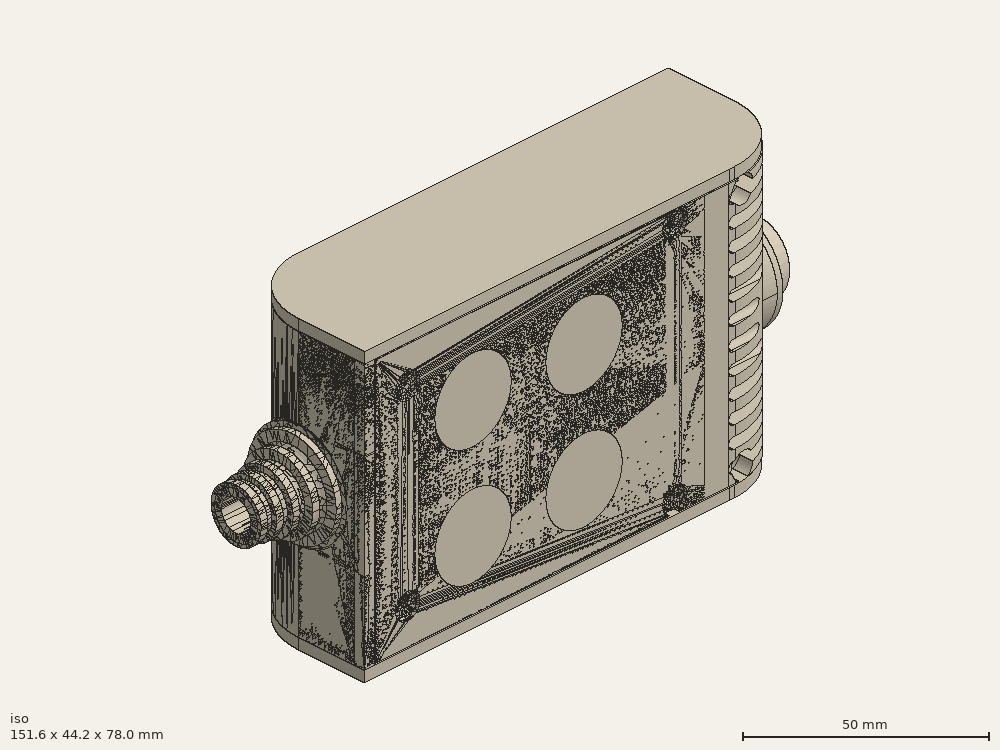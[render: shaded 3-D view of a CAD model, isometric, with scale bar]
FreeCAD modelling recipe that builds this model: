
FCSTD DOCUMENT  (FreeCAD 0.19R0.19.2)
Label: enclosure_174FCStd
License: All rights reserved
LicenseURL: http://en.wikipedia.org/wiki/All_rights_reserved
objects: Part::Revolution×152, Part::Feature×146, Part::MultiFuse×145, Sketcher::SketchObject×82, Part::Cut×69, Part::Extrusion×67, Part::Cylinder×66, Part::Fillet×58, Part::Box×36, App::MeasureDistance×4
note: 821 computed .brp shape members not serialized (recipe doc carries the construction recipe); baked Part::Feature solids carry a one-line shape summary decoded from their .brp

FEATURE [Sketcher::SketchObject] Sketch  label="topSketch"
  FullyConstrained = true
  sketch-geometry (20):
    g0: LineSegment StartX=5.21097e-06 StartY=3 StartZ=0 EndX=5.21097e-06 EndY=19 EndZ=0
    g1: ArcOfCircle CenterX=19 CenterY=19 CenterZ=0 NormalX=0 NormalY=0 NormalZ=1 AngleXU=0 Radius=19 StartAngle=1.5708 EndAngle=3.14159
    g2: ArcOfCircle CenterX=19 CenterY=19 CenterZ=0 NormalX=0 NormalY=0 NormalZ=1 AngleXU=0 Radius=16 StartAngle=1.5708 EndAngle=3.14159
    g3: LineSegment StartX=114 StartY=35 StartZ=0 EndX=19 EndY=35 EndZ=0
    g4: LineSegment StartX=5.21097e-06 StartY=3 StartZ=0 EndX=5.21097e-06 EndY=0 EndZ=0
    g5: LineSegment StartX=3 StartY=0 StartZ=0 EndX=5.21097e-06 EndY=0 EndZ=0
    g6: LineSegment StartX=3 StartY=19 StartZ=0 EndX=3 EndY=0 EndZ=0
    g7: LineSegment StartX=19 StartY=38 StartZ=0 EndX=124 EndY=38 EndZ=0
    g8: Circle CenterX=119 CenterY=35 CenterZ=0 NormalX=0 NormalY=0 NormalZ=1 AngleXU=0 Radius=1
    g9: Circle CenterX=121 CenterY=35 CenterZ=0 NormalX=0 NormalY=0 NormalZ=1 AngleXU=0 Radius=1
    g10: Circle CenterX=121 CenterY=33 CenterZ=0 NormalX=0 NormalY=0 NormalZ=1 AngleXU=0 Radius=1
    g11: BSplineCurve PolesCount=3 KnotsCount=2 Degree=2 IsPeriodic=0
    g12: GeomPoint X=119 Y=35 Z=0
    g13: GeomPoint X=121 Y=33 Z=0
    g14: LineSegment StartX=119 StartY=35 StartZ=0 EndX=114 EndY=35 EndZ=0
    g15: ArcOfCircle CenterX=105 CenterY=19 CenterZ=0 NormalX=0 NormalY=0 NormalZ=1 AngleXU=0 Radius=19 StartAngle=5.7297 EndAngle=6.28319
    g16: ArcOfCircle CenterX=105 CenterY=19 CenterZ=0 NormalX=0 NormalY=0 NormalZ=1 AngleXU=0 Radius=16 StartAngle=5.60905 EndAngle=6.28319
    g17: LineSegment StartX=121 StartY=33 StartZ=0 EndX=121 EndY=19 EndZ=0
    g18: LineSegment StartX=124 StartY=38 StartZ=0 EndX=124 EndY=19 EndZ=0
    g19: LineSegment StartX=117.5 StartY=9.01251 StartZ=0 EndX=121.163 EndY=9.0125 EndZ=0
  constraints (46):
    c: Vertical(g0)
    c: Block(g0)
    c: Coincident(g1,g0)
    c: Block(g1)
    c: Coincident(g2,g1)
    c: Block(g2)
    c: Coincident(g3,g2)
    c: Horizontal(g3)
    c: Tangent(g3,g2)
    c: Coincident(g4,g0)
    c: Distance(g4) = 3
    c: Vertical(g4)
    c: Coincident(g5,g4)
    c: Horizontal(g5)
    c: Coincident(g6,g2)
    c: Coincident(g6,g5)
    c: Vertical(g6)
    c: Horizontal(g7)
    c: Distance(g7) = 105
    c: Coincident(g7,g1)
    c: Block(g3)
    c: Weight(g8) = 1
    c: Equal(g8,g9)
    c: Equal(g8,g10)
    c: InternalAlignment(g8,g11)
    c: InternalAlignment(g9,g11)
    c: InternalAlignment(g10,g11)
    c: InternalAlignment(g12,g11)
    c: InternalAlignment(g13,g11)
    c: Block(g11)
    c: Coincident(g14,g11)
    c: Coincident(g14,g3)
    c: Horizontal(g14)
    c: Block(g15)
    c: Coincident(g16,g15)
    c: Block(g16)
    c: Coincident(g17,g11)
    c: Coincident(g17,g16)
    c: Vertical(g17)
    c: Distance(g17) = 14
    c: Coincident(g18,g7)
    c: Coincident(g18,g15)
    c: Vertical(g18)
    c: Distance(g18) = 19
    c: Coincident(g19,g16)
    c: Coincident(g19,g15)
FEATURE [Sketcher::SketchObject] Sketch001  label="bottomSketch"
  FullyConstrained = true
  sketch-geometry (32):
    g0: LineSegment StartX=3.3 StartY=-6.03275e-07 StartZ=0 EndX=98 EndY=-6.03275e-07 EndZ=0
    g1: ArcOfCircle CenterX=98 CenterY=19 CenterZ=0 NormalX=0 NormalY=0 NormalZ=1 AngleXU=0 Radius=19 StartAngle=4.71239 EndAngle=5.71103
    g2: LineSegment StartX=6.3 StartY=8 StartZ=0 EndX=3.3 EndY=8 EndZ=0
    g3: LineSegment StartX=3.3 StartY=8 StartZ=0 EndX=3.3 EndY=-6.03275e-07 EndZ=0
    g4: ArcOfCircle CenterX=8.3 CenterY=5 CenterZ=0 NormalX=0 NormalY=0 NormalZ=1 AngleXU=0 Radius=2 StartAngle=3.14159 EndAngle=4.71239
    g5: LineSegment StartX=6.3 StartY=8 StartZ=0 EndX=6.3 EndY=5 EndZ=0
    g6: ArcOfCircle CenterX=98 CenterY=19 CenterZ=0 NormalX=0 NormalY=0 NormalZ=1 AngleXU=0 Radius=12.7 StartAngle=4.71239 EndAngle=6.28319
    g7: LineSegment StartX=94.7 StartY=3 StartZ=0 EndX=8.3 EndY=3 EndZ=0
    g8-g12: Circle x5 (B-spline internal-alignment scaffolding for g13; pole/knot coordinates omitted)
    g13: BSplineCurve PolesCount=5 KnotsCount=3 Degree=3 IsPeriodic=0
    g14: GeomPoint X=98 Y=6.3 Z=0
    g15: GeomPoint X=96.3938 Y=4.71946 Z=0
    g16: GeomPoint X=94.7 Y=3 Z=0
    g17-g23: Circle x7 (B-spline internal-alignment scaffolding for g24; pole/knot coordinates omitted)
    g24: BSplineCurve PolesCount=7 KnotsCount=5 Degree=3 IsPeriodic=0
    g25-g29: GeomPoint x5 (B-spline internal-alignment scaffolding for g24; pole/knot coordinates omitted)
    g30: ArcOfCircle CenterX=98 CenterY=19 CenterZ=0 NormalX=0 NormalY=0 NormalZ=1 AngleXU=0 Radius=15.7 StartAngle=5.81226 EndAngle=6.28319
    g31: LineSegment StartX=110.7 StartY=19 StartZ=0 EndX=113.7 EndY=19 EndZ=0
  constraints (41):
    c: Horizontal(g0)
    c: Coincident(g1,g0)
    c: Block(g1)
    c: Horizontal(g2)
    c: Distance(g2) = 3
    c: Coincident(g3,g2)
    c: Vertical(g3)
    c: Coincident(g3,g0)
    c: Block(g4)
    c: Block(g2)
    c: Coincident(g5,g2)
    c: Coincident(g5,g4)
    c: Vertical(g5)
    c: Coincident(g6,g1)
    c: Block(g6)
    c: Coincident(g7,g4)
    c: Horizontal(g7)
    c: Block(g0)
    c: Block(g7)
    c: Block(g3)
    c: Coincident(g13,g6)
    c: Weight(g8) = 1
    c: Equal(g8, g9-g12) x4
    c: Coincident(g13,g7)
    c: InternalAlignment(g8-g12 -> g13) x5
    c: InternalAlignment(g14,g13)
    c: InternalAlignment(g15,g13)
    c: InternalAlignment(g16,g13)
    c: Block(g13)
    c: Weight(g17) = 1
    c: Equal(g17, g18-g23) x6
    c: Coincident(g24,g1)
    c: InternalAlignment(g17-g23 -> g24) x7
    c: InternalAlignment(g25-g29 -> g24) x5
    c: Block(g24)
    c: Coincident(g30,g24)
    c: Coincident(g31,g6)
    c: Coincident(g31,g30)
    c: Horizontal(g31)
    c: Block(g31)
    c: Block(g30)
FEATURE [Part::Extrusion] Extrude  label="top"
  Base = -> Sketch
  Dir = (0,0,1)
  DirMode = 2
  FaceMakerClass = Part::FaceMakerBullseye
  LengthFwd = 72
  LengthRev = 0
  Solid = true
  Symmetric = false
FEATURE [Part::Extrusion] Extrude001  label="bottom"
  Base = -> Sketch001
  Dir = (0,0,1)
  DirMode = 2
  FaceMakerClass = Part::FaceMakerBullseye
  LengthFwd = 71.4
  LengthRev = 0
  Placement = pos=(0,0,0.3) rot=(0,0,1;0rad)
  Solid = true
  Symmetric = false
FEATURE [Sketcher::SketchObject] Sketch002  label="topSketch001"
  FullyConstrained = true
  sketch-geometry (8):
    g0: ArcOfCircle CenterX=19 CenterY=19.0975 CenterZ=0 NormalX=0 NormalY=0 NormalZ=1 AngleXU=0 Radius=18.9025 StartAngle=1.5708 EndAngle=3.14674
    g1: LineSegment StartX=0.0977805 StartY=19.0003 StartZ=0 EndX=0.0977805 EndY=0.000251602 EndZ=0
    g2: LineSegment StartX=19 StartY=38 StartZ=0 EndX=124 EndY=38 EndZ=0
    g3: LineSegment StartX=0.0977805 StartY=0.000251602 StartZ=0 EndX=105.098 EndY=0.000251602 EndZ=0
    g4: LineSegment StartX=124 StartY=38 StartZ=0 EndX=125.616 EndY=38 EndZ=0
    g5: LineSegment StartX=105.098 StartY=0.000251602 StartZ=0 EndX=106.713 EndY=0.000251602 EndZ=0
    g6: ArcOfCircle CenterX=106.616 CenterY=19 CenterZ=0 NormalX=0 NormalY=0 NormalZ=1 AngleXU=0 Radius=19 StartAngle=4.71754 EndAngle=6.28319
    g7: LineSegment StartX=125.616 StartY=38 StartZ=0 EndX=125.616 EndY=19 EndZ=0
  constraints (21):
    c: Block(g0)
    c: Coincident(g1,g0)
    c: Vertical(g1)
    c: Horizontal(g2)
    c: Distance(g2) = 105
    c: Coincident(g2,g0)
    c: Distance(g1) = 19
    c: Coincident(g3,g1)
    c: Horizontal(g3)
    c: Distance(g3) = 105
    c: Coincident(g4,g2)
    c: Horizontal(g4)
    c: Distance(g4) = 1.61553
    c: Horizontal(g5)
    c: Equal(g4,g5) = 1.61553
    c: Coincident(g5,g3)
    c: Block(g6)
    c: Coincident(g6,g5)
    c: Coincident(g7,g4)
    c: Coincident(g7,g6)
    c: Vertical(g7)
FEATURE [Part::Extrusion] Extrude002  label="sideA"
  Base = -> Sketch002
  Dir = (0,0,1)
  DirMode = 2
  FaceMakerClass = Part::FaceMakerBullseye
  LengthFwd = 3
  LengthRev = 0
  Placement = pos=(0,0,-3) rot=(0,0,1;0rad)
  Solid = true
  Symmetric = false
FEATURE [Sketcher::SketchObject] Sketch003  label="topSketch002"
  FullyConstrained = true
  sketch-geometry (6):
    g0: LineSegment StartX=19 StartY=38 StartZ=0 EndX=117 EndY=38 EndZ=0
    g1: ArcOfCircle CenterX=19 CenterY=19 CenterZ=0 NormalX=0 NormalY=0 NormalZ=1 AngleXU=0 Radius=19 StartAngle=1.5708 EndAngle=3.14159
    g2: LineSegment StartX=117 StartY=38 StartZ=0 EndX=117 EndY=19 EndZ=0
    g3: LineSegment StartX=98 StartY=1.0161e-12 StartZ=0 EndX=5.22862e-06 EndY=1.0161e-12 EndZ=0
    g4: LineSegment StartX=5.22862e-06 StartY=19 StartZ=0 EndX=5.22862e-06 EndY=1.0161e-12 EndZ=0
    g5: ArcOfCircle CenterX=98 CenterY=19 CenterZ=0 NormalX=0 NormalY=0 NormalZ=1 AngleXU=0 Radius=19 StartAngle=4.71239 EndAngle=6.28319
  constraints (16):
    c: Horizontal(g0)
    c: Distance(g0) = 98
    c: Coincident(g1,g0)
    c: Block(g1)
    c: Coincident(g2,g0)
    c: Vertical(g2)
    c: Distance(g2) = 19
    c: Horizontal(g3)
    c: Coincident(g4,g1)
    c: Vertical(g4)
    c: Coincident(g3,g4)
    c: Block(g3)
    c: Coincident(g5,g2)
    c: Coincident(g5,g3)
    c: Block(g0)
    c: Block(g5)
FEATURE [Sketcher::SketchObject] Sketch004
  FullyConstrained = true
  MapMode = 3
  Placement = pos=(0,0,0) rot=(1,0,0;1.5708rad)
  Support = -> [Extrude]
  sketch-geometry (8):
    g0: Circle CenterX=80.351 CenterY=-67.6202 CenterZ=0 NormalX=0 NormalY=0 NormalZ=1 AngleXU=0 Radius=2
    g1: Circle CenterX=80.351 CenterY=-67.6202 CenterZ=0 NormalX=0 NormalY=0 NormalZ=1 AngleXU=0 Radius=3
    g2: Circle CenterX=80.351 CenterY=-4.92017 CenterZ=0 NormalX=0 NormalY=0 NormalZ=1 AngleXU=0 Radius=2
    g3: Circle CenterX=80.351 CenterY=-4.92017 CenterZ=0 NormalX=0 NormalY=0 NormalZ=1 AngleXU=0 Radius=3
    g4: Circle CenterX=23.851 CenterY=-4.92017 CenterZ=0 NormalX=0 NormalY=0 NormalZ=1 AngleXU=0 Radius=2
    g5: Circle CenterX=23.851 CenterY=-4.92017 CenterZ=0 NormalX=0 NormalY=0 NormalZ=1 AngleXU=0 Radius=3
    g6: Circle CenterX=23.851 CenterY=-67.6202 CenterZ=0 NormalX=0 NormalY=0 NormalZ=1 AngleXU=0 Radius=2
    g7: Circle CenterX=23.851 CenterY=-67.6202 CenterZ=0 NormalX=0 NormalY=0 NormalZ=1 AngleXU=0 Radius=3
  constraints (8):
    c: Block(g3)
    c: Block(g2)
    c: Block(g1)
    c: Block(g0)
    c: Block(g6)
    c: Block(g7)
    c: Block(g4)
    c: Block(g5)
FEATURE [Part::Extrusion] Extrude004
  Base = -> Sketch004
  Dir = (0,-1,2e-16)
  DirMode = 2
  FaceMakerClass = Part::FaceMakerBullseye
  LengthFwd = 6
  LengthRev = 0
  Placement = pos=(0,9,0) rot=(0,0,1;0rad)
  Solid = true
  Symmetric = false
FEATURE [Sketcher::SketchObject] Sketch005
  FullyConstrained = true
  MapMode = 3
  Placement = pos=(0,0,0) rot=(1,0,0;1.5708rad)
  Support = -> [Extrude]
  sketch-geometry (8):
    g0: Circle CenterX=80.351 CenterY=-67.6202 CenterZ=0 NormalX=0 NormalY=0 NormalZ=1 AngleXU=0 Radius=3
    g1: Circle CenterX=80.351 CenterY=-4.92017 CenterZ=0 NormalX=0 NormalY=0 NormalZ=1 AngleXU=0 Radius=3
    g2: Circle CenterX=23.851 CenterY=-4.92017 CenterZ=0 NormalX=0 NormalY=0 NormalZ=1 AngleXU=0 Radius=3
    g3: Circle CenterX=23.851 CenterY=-67.6202 CenterZ=0 NormalX=0 NormalY=0 NormalZ=1 AngleXU=0 Radius=3
    g4: Circle CenterX=23.851 CenterY=-67.6202 CenterZ=0 NormalX=0 NormalY=0 NormalZ=1 AngleXU=0 Radius=5
    g5: Circle CenterX=80.351 CenterY=-67.6202 CenterZ=0 NormalX=0 NormalY=0 NormalZ=1 AngleXU=0 Radius=5
    g6: Circle CenterX=23.851 CenterY=-4.92017 CenterZ=0 NormalX=0 NormalY=0 NormalZ=1 AngleXU=0 Radius=5
    g7: Circle CenterX=80.351 CenterY=-4.92017 CenterZ=0 NormalX=0 NormalY=0 NormalZ=1 AngleXU=0 Radius=5
  constraints (8):
    c: Block(g1)
    c: Block(g0)
    c: Block(g3)
    c: Block(g2)
    c: Block(g5)
    c: Block(g4)
    c: Block(g6)
    c: Block(g7)
FEATURE [Part::Extrusion] Extrude005
  Base = -> Sketch005
  Dir = (0,-1,2e-16)
  DirMode = 2
  FaceMakerClass = Part::FaceMakerBullseye
  LengthFwd = 2
  LengthRev = 0
  Solid = true
  Symmetric = false
FEATURE [Sketcher::SketchObject] Sketch006
  FullyConstrained = true
  MapMode = 3
  Placement = pos=(0,0,0) rot=(1,0,0;1.5708rad)
  sketch-geometry (8):
    g0: Circle CenterX=80.351 CenterY=-67.6202 CenterZ=0 NormalX=0 NormalY=0 NormalZ=1 AngleXU=0 Radius=3
    g1: Circle CenterX=80.351 CenterY=-4.92017 CenterZ=0 NormalX=0 NormalY=0 NormalZ=1 AngleXU=0 Radius=3
    g2: Circle CenterX=23.851 CenterY=-4.92017 CenterZ=0 NormalX=0 NormalY=0 NormalZ=1 AngleXU=0 Radius=3
    g3: Circle CenterX=23.851 CenterY=-67.6202 CenterZ=0 NormalX=0 NormalY=0 NormalZ=1 AngleXU=0 Radius=3
    g4: Circle CenterX=23.851 CenterY=-67.6202 CenterZ=0 NormalX=0 NormalY=0 NormalZ=1 AngleXU=0 Radius=5
    g5: Circle CenterX=80.351 CenterY=-67.6202 CenterZ=0 NormalX=0 NormalY=0 NormalZ=1 AngleXU=0 Radius=5
    g6: Circle CenterX=23.851 CenterY=-4.92017 CenterZ=0 NormalX=0 NormalY=0 NormalZ=1 AngleXU=0 Radius=5
    g7: Circle CenterX=80.351 CenterY=-4.92017 CenterZ=0 NormalX=0 NormalY=0 NormalZ=1 AngleXU=0 Radius=5
  constraints (8):
    c: Block(g1)
    c: Block(g0)
    c: Block(g3)
    c: Block(g2)
    c: Block(g5)
    c: Block(g4)
    c: Block(g6)
    c: Block(g7)
FEATURE [Part::Extrusion] Extrude007
  Base = -> Sketch006
  Dir = (0,-1,2e-16)
  DirMode = 2
  FaceMakerClass = Part::FaceMakerBullseye
  LengthFwd = 2
  LengthRev = 0
  Solid = true
  Symmetric = false
FEATURE [Part::Fillet] Fillet
  Base = -> Extrude007
  Edges = 4 edges r=1.99: [Edge6,Edge12,Edge18,Edge24]
FEATURE [Part::Cut] Cut
  Base = -> Extrude005
  Placement = pos=(0,5,0) rot=(0,0,1;0rad)
  Tool = -> Fillet
FEATURE [Part::MultiFuse] Fusion  label="pCBScrews"
  Placement = pos=(-2.5,0,72.3) rot=(0,0,1;0rad)
  Shapes = -> [Extrude004,Cut]
FEATURE [App::MeasureDistance] Distance  label="Distance: 0.69 mm"
  Distance = 0.685967
  P1 = (24.0138,2.9647,0.3)
  P2 = (23.8901,3,-0.373787)
FEATURE [App::MeasureDistance] Distance001  label="Distance: 0.53 mm"
  Distance = 0.533607
  P1 = (80.2939,3,72.2334)
  P2 = (80.281,2.99661,71.7)
FEATURE [Part::Fillet] Fillet001
  Base = -> Extrude001
  Edges = 1 edges r=2.4: [Edge17]
FEATURE [Part::Fillet] Fillet002  label="bottom001"
  Base = -> Fillet001
  Edges = 1 edges r=2.4: [Edge36]
FEATURE [Part::Fillet] Fillet003  label="top001"
  Base = -> Extrude
  Edges = 1 edges r=2: [Edge1]
FEATURE [Sketcher::SketchObject] Sketch007
  FullyConstrained = true
  sketch-geometry (16):
    g0: LineSegment StartX=4 StartY=0 StartZ=0 EndX=4 EndY=2.4 EndZ=0
    g1: LineSegment StartX=4 StartY=2.4 StartZ=0 EndX=7 EndY=2.4 EndZ=0
    g2: LineSegment StartX=4 StartY=0 StartZ=0 EndX=5.7 EndY=0 EndZ=0
    g3: LineSegment StartX=5.7 StartY=0 StartZ=0 EndX=5.7 EndY=-5.6 EndZ=0
    g4-g8: Circle x5 (B-spline internal-alignment scaffolding for g9; pole/knot coordinates omitted)
    g9: BSplineCurve PolesCount=5 KnotsCount=3 Degree=3 IsPeriodic=0
    g10: GeomPoint X=7 Y=2.4 Z=0
    g11: GeomPoint X=10.4582 Y=-1.55472 Z=0
    g12: GeomPoint X=14 Y=-5.6 Z=0
    g13: LineSegment StartX=14 StartY=-5.6 StartZ=0 EndX=14 EndY=-14.1 EndZ=0
    g14: LineSegment StartX=14 StartY=-14.1 StartZ=0 EndX=6.5 EndY=-14.1 EndZ=0
    g15: LineSegment StartX=5.7 StartY=-5.6 StartZ=0 EndX=6.5 EndY=-14.1 EndZ=0
  constraints (28):
    c: Distance(g0) = 2.4
    c: Vertical(g0)
    c: Block(g0)
    c: Coincident(g1,g0)
    c: Horizontal(g1)
    c: Distance(g1) = 3
    c: Coincident(g2,g0)
    c: Horizontal(g2)
    c: Distance(g2) = 1.7
    c: Coincident(g3,g2)
    c: Vertical(g3)
    c: Distance(g3) = 5.6
    c: Coincident(g9,g1)
    c: Weight(g4) = 1
    c: Equal(g4, g5-g8) x4
    c: InternalAlignment(g4-g8 -> g9) x5
    c: InternalAlignment(g10,g9)
    c: InternalAlignment(g11,g9)
    c: InternalAlignment(g12,g9)
    c: Block(g9)
    c: Coincident(g13,g9)
    c: Vertical(g13)
    c: Distance(g13) = 8.5
    c: Coincident(g14,g13)
    c: Horizontal(g14)
    c: Distance(g14) = 7.5
    c: Coincident(g15,g3)
    c: Coincident(g15,g14)
FEATURE [Part::Feature] Face
  shape: bbox 10 x 16.5 x 2e-07 mm, 1 faces, 0 solids (baked)
FEATURE [Part::Revolution] Revolve  label="plugHousing"
  Angle = 360
  Axis = (0,1,0)
  Base = (0,0,0)
  FaceMakerClass = Part::FaceMakerBullseye
  Placement = pos=(0,0,36.15) rot=(0,0,1;0rad)
  Solid = false
  Source = -> Face
  Symmetric = false
FEATURE [Part::Feature] Face001
  shape: bbox 10 x 16.5 x 2e-07 mm, 1 faces, 0 solids (baked)
FEATURE [Part::Revolution] Revolve001  label="plugHousing001"
  Angle = 360
  Axis = (0,1,0)
  Base = (0,0,0)
  FaceMakerClass = Part::FaceMakerBullseye
  Placement = pos=(0,0,36.15) rot=(0,0,1;0rad)
  Solid = false
  Source = -> Face001
  Symmetric = false
FEATURE [Part::MultiFuse] Fusion001  label="plugHousing002"
  Placement = pos=(0,0,0) rot=(0,0,1;1.5708rad)
  Shapes = -> [Revolve001,Revolve]
FEATURE [Part::Feature] Face002
  shape: bbox 10 x 16.5 x 2e-07 mm, 1 faces, 0 solids (baked)
FEATURE [Part::Revolution] Revolve003  label="plugHousing005"
  Angle = 360
  Axis = (0,1,0)
  Base = (0,0,0)
  FaceMakerClass = Part::FaceMakerBullseye
  Placement = pos=(0,0,36.15) rot=(0,0,1;0rad)
  Solid = false
  Source = -> Face002
  Symmetric = false
FEATURE [Part::Feature] Face003
  shape: bbox 10 x 16.5 x 2e-07 mm, 1 faces, 0 solids (baked)
FEATURE [Part::Revolution] Revolve002  label="plugHousing003"
  Angle = 360
  Axis = (0,1,0)
  Base = (0,0,0)
  FaceMakerClass = Part::FaceMakerBullseye
  Placement = pos=(0,0,36.15) rot=(0,0,1;0rad)
  Solid = false
  Source = -> Face003
  Symmetric = false
FEATURE [Part::MultiFuse] Fusion002  label="plugHousing004"
  Placement = pos=(0,0,0) rot=(0,0,1;1.5708rad)
  Shapes = -> [Revolve002,Revolve003]
FEATURE [Part::MultiFuse] Fusion003  label="plugHousing006"
  Placement = pos=(0,19,0) rot=(0,0,1;3.14159rad)
  Shapes = -> [Fusion002,Fusion001]
FEATURE [Part::Feature] Face004
  shape: bbox 10 x 16.5 x 2e-07 mm, 1 faces, 0 solids (baked)
FEATURE [Part::Revolution] Revolve006  label="plugHousing010"
  Angle = 360
  Axis = (0,1,0)
  Base = (0,0,0)
  FaceMakerClass = Part::FaceMakerBullseye
  Placement = pos=(0,0,36.15) rot=(0,0,1;0rad)
  Solid = false
  Source = -> Face004
  Symmetric = false
FEATURE [Part::Feature] Face005
  shape: bbox 10 x 16.5 x 2e-07 mm, 1 faces, 0 solids (baked)
FEATURE [Part::Revolution] Revolve007  label="plugHousing011"
  Angle = 360
  Axis = (0,1,0)
  Base = (0,0,0)
  FaceMakerClass = Part::FaceMakerBullseye
  Placement = pos=(0,0,36.15) rot=(0,0,1;0rad)
  Solid = false
  Source = -> Face005
  Symmetric = false
FEATURE [Part::Feature] Face006
  shape: bbox 10 x 16.5 x 2e-07 mm, 1 faces, 0 solids (baked)
FEATURE [Part::Revolution] Revolve004  label="plugHousing007"
  Angle = 360
  Axis = (0,1,0)
  Base = (0,0,0)
  FaceMakerClass = Part::FaceMakerBullseye
  Placement = pos=(0,0,36.15) rot=(0,0,1;0rad)
  Solid = false
  Source = -> Face006
  Symmetric = false
FEATURE [Part::MultiFuse] Fusion004  label="plugHousing009"
  Placement = pos=(0,0,0) rot=(0,0,1;1.5708rad)
  Shapes = -> [Revolve004,Revolve007]
FEATURE [Part::Feature] Face007
  shape: bbox 10 x 16.5 x 2e-07 mm, 1 faces, 0 solids (baked)
FEATURE [Part::Revolution] Revolve005  label="plugHousing008"
  Angle = 360
  Axis = (0,1,0)
  Base = (0,0,0)
  FaceMakerClass = Part::FaceMakerBullseye
  Placement = pos=(0,0,36.15) rot=(0,0,1;0rad)
  Solid = false
  Source = -> Face007
  Symmetric = false
FEATURE [Part::MultiFuse] Fusion005  label="plugHousing012"
  Placement = pos=(0,0,0) rot=(0,0,1;1.5708rad)
  Shapes = -> [Revolve006,Revolve005]
FEATURE [Part::MultiFuse] Fusion006  label="plugHousing013"
  Placement = pos=(0,19,0) rot=(0,0,1;3.14159rad)
  Shapes = -> [Fusion005,Fusion004]
FEATURE [Part::MultiFuse] Fusion007  label="plugHousing014"
  Placement = pos=(122.621,0,-0.15) rot=(0,0,1;0rad)
  Shapes = -> [Fusion003,Fusion006]
FEATURE [Part::Cylinder] Cylinder002
  Angle = 360
  AttacherType = Attacher::AttachEngine3D
  Height = 20
  Placement = pos=(0,0,36.15) rot=(0,0,1;0rad)
  Radius = 4
FEATURE [Part::Cylinder] Cylinder003
  Angle = 360
  AttacherType = Attacher::AttachEngine3D
  Height = 10
  Placement = pos=(0,0,36.15) rot=(0,0,1;0rad)
  Radius = 4
FEATURE [Part::MultiFuse] Fusion009  label="removeToCreateHoleForPlugHousing"
  Placement = pos=(70,19,36.15) rot=(0,1,0;1.5708rad)
  Shapes = -> [Cylinder002,Cylinder003]
FEATURE [Part::Cylinder] Cylinder004
  Angle = 360
  AttacherType = Attacher::AttachEngine3D
  Height = 20
  Placement = pos=(0,0,36.15) rot=(0,0,1;0rad)
  Radius = 4
FEATURE [Part::Cylinder] Cylinder005
  Angle = 360
  AttacherType = Attacher::AttachEngine3D
  Height = 10
  Placement = pos=(0,0,36.15) rot=(0,0,1;0rad)
  Radius = 4
FEATURE [Part::MultiFuse] Fusion010  label="removeToCreateHoleForPlugHousing001"
  Placement = pos=(70,19,36.15) rot=(0,1,0;1.5708rad)
  Shapes = -> [Cylinder004,Cylinder005]
FEATURE [Part::Cut] Cut001
  Base = -> Fillet003
  Tool = -> Fusion010
FEATURE [Part::Cut] Cut002  label="Bottom"
  Base = -> Fillet002
  Tool = -> Fusion009
FEATURE [Part::Feature] Face008
  shape: bbox 10 x 16.5 x 2e-07 mm, 1 faces, 0 solids (baked)
FEATURE [Part::Revolution] Revolve011  label="plugHousing021"
  Angle = 360
  Axis = (0,1,0)
  Base = (0,0,0)
  FaceMakerClass = Part::FaceMakerBullseye
  Placement = pos=(0,0,36.15) rot=(0,0,1;0rad)
  Solid = false
  Source = -> Face008
  Symmetric = false
FEATURE [Part::Feature] Face009
  shape: bbox 10 x 16.5 x 2e-07 mm, 1 faces, 0 solids (baked)
FEATURE [Part::Revolution] Revolve012  label="plugHousing022"
  Angle = 360
  Axis = (0,1,0)
  Base = (0,0,0)
  FaceMakerClass = Part::FaceMakerBullseye
  Placement = pos=(0,0,36.15) rot=(0,0,1;0rad)
  Solid = false
  Source = -> Face009
  Symmetric = false
FEATURE [Part::Feature] Face010 .. Face013  x4 (patterned run collapsed; names and placements below)
  shape: bbox 10 x 16.5 x 2e-07 mm, 1 faces, 0 solids (baked)
FEATURE [Part::Revolution] Revolve015  label="plugHousing027"
  Angle = 360
  Axis = (0,1,0)
  Base = (0,0,0)
  FaceMakerClass = Part::FaceMakerBullseye
  Placement = pos=(0,0,36.15) rot=(0,0,1;0rad)
  Solid = false
  Source = -> Face013
  Symmetric = false
FEATURE [Part::Feature] Face014
  shape: bbox 10 x 16.5 x 2e-07 mm, 1 faces, 0 solids (baked)
FEATURE [Part::Feature] Face015
  shape: bbox 10 x 16.5 x 2e-07 mm, 1 faces, 0 solids (baked)
FEATURE [Part::Feature] Face016
  shape: bbox 10 x 16.5 x 2e-07 mm, 1 faces, 0 solids (baked)
FEATURE [Part::Revolution] Revolve019  label="plugHousing033"
  Angle = 360
  Axis = (0,1,0)
  Base = (0,0,0)
  FaceMakerClass = Part::FaceMakerBullseye
  Placement = pos=(0,0,36.15) rot=(0,0,1;0rad)
  Solid = false
  Source = -> Face016
  Symmetric = false
FEATURE [Part::Feature] Face017
  shape: bbox 10 x 16.5 x 2e-07 mm, 1 faces, 0 solids (baked)
FEATURE [Part::Revolution] Revolve020  label="plugHousing034"
  Angle = 360
  Axis = (0,1,0)
  Base = (0,0,0)
  FaceMakerClass = Part::FaceMakerBullseye
  Placement = pos=(0,0,36.15) rot=(0,0,1;0rad)
  Solid = false
  Source = -> Face017
  Symmetric = false
FEATURE [Part::Feature] Face018
  shape: bbox 10 x 16.5 x 2e-07 mm, 1 faces, 0 solids (baked)
FEATURE [Part::Revolution] Revolve016  label="plugHousing030"
  Angle = 360
  Axis = (0,1,0)
  Base = (0,0,0)
  FaceMakerClass = Part::FaceMakerBullseye
  Placement = pos=(0,0,36.15) rot=(0,0,1;0rad)
  Solid = false
  Source = -> Face018
  Symmetric = false
FEATURE [Part::MultiFuse] Fusion020  label="plugHousing038"
  Placement = pos=(0,0,0) rot=(0,0,1;1.5708rad)
  Shapes = -> [Revolve016,Revolve020]
FEATURE [Part::Feature] Face019
  shape: bbox 10 x 16.5 x 2e-07 mm, 1 faces, 0 solids (baked)
FEATURE [Part::Feature] Face020
  shape: bbox 10 x 16.5 x 2e-07 mm, 1 faces, 0 solids (baked)
FEATURE [Part::Revolution] Revolve017  label="plugHousing031"
  Angle = 360
  Axis = (0,1,0)
  Base = (0,0,0)
  FaceMakerClass = Part::FaceMakerBullseye
  Placement = pos=(0,0,36.15) rot=(0,0,1;0rad)
  Solid = false
  Source = -> Face020
  Symmetric = false
FEATURE [Part::MultiFuse] Fusion021  label="plugHousing039"
  Placement = pos=(0,0,0) rot=(0,0,1;1.5708rad)
  Shapes = -> [Revolve019,Revolve017]
FEATURE [Part::MultiFuse] Fusion023  label="plugHousing041"
  Placement = pos=(0,19,0) rot=(0,0,1;3.14159rad)
  Shapes = -> [Fusion021,Fusion020]
FEATURE [Part::Revolution] Revolve022  label="plugHousing043"
  Angle = 360
  Axis = (0,1,0)
  Base = (0,0,0)
  FaceMakerClass = Part::FaceMakerBullseye
  Placement = pos=(0,0,36.15) rot=(0,0,1;0rad)
  Solid = false
  Source = -> Face019
  Symmetric = false
FEATURE [Part::Feature] Face021
  shape: bbox 10 x 16.5 x 2e-07 mm, 1 faces, 0 solids (baked)
FEATURE [Part::Revolution] Revolve023  label="plugHousing044"
  Angle = 360
  Axis = (0,1,0)
  Base = (0,0,0)
  FaceMakerClass = Part::FaceMakerBullseye
  Placement = pos=(0,0,36.15) rot=(0,0,1;0rad)
  Solid = false
  Source = -> Face021
  Symmetric = false
FEATURE [Part::Feature] Face022
  shape: bbox 10 x 16.5 x 2e-07 mm, 1 faces, 0 solids (baked)
FEATURE [Part::Revolution] Revolve018  label="plugHousing032"
  Angle = 360
  Axis = (0,1,0)
  Base = (0,0,0)
  FaceMakerClass = Part::FaceMakerBullseye
  Placement = pos=(0,0,36.15) rot=(0,0,1;0rad)
  Solid = false
  Source = -> Face022
  Symmetric = false
FEATURE [Part::MultiFuse] Fusion022  label="plugHousing040"
  Placement = pos=(0,0,0) rot=(0,0,1;1.5708rad)
  Shapes = -> [Revolve018,Revolve023]
FEATURE [Part::Feature] Face023
  shape: bbox 10 x 16.5 x 2e-07 mm, 1 faces, 0 solids (baked)
FEATURE [Part::Revolution] Revolve021  label="plugHousing035"
  Angle = 360
  Axis = (0,1,0)
  Base = (0,0,0)
  FaceMakerClass = Part::FaceMakerBullseye
  Placement = pos=(0,0,36.15) rot=(0,0,1;0rad)
  Solid = false
  Source = -> Face023
  Symmetric = false
FEATURE [Part::MultiFuse] Fusion018  label="plugHousing036"
  Placement = pos=(0,0,0) rot=(0,0,1;1.5708rad)
  Shapes = -> [Revolve022,Revolve021]
FEATURE [Part::MultiFuse] Fusion019  label="plugHousing037"
  Placement = pos=(0,19,0) rot=(0,0,1;3.14159rad)
  Shapes = -> [Fusion018,Fusion022]
FEATURE [Part::MultiFuse] Fusion024  label="plugHousing042"
  Placement = pos=(122.621,0,-0.15) rot=(0,0,1;0rad)
  Shapes = -> [Fusion023,Fusion019]
FEATURE [Part::Cylinder] Cylinder006
  Angle = 360
  AttacherType = Attacher::AttachEngine3D
  Height = 20
  Placement = pos=(0,0,36.15) rot=(0,0,1;0rad)
  Radius = 14.3
FEATURE [Part::Cylinder] Cylinder007
  Angle = 360
  AttacherType = Attacher::AttachEngine3D
  Height = 10
  Placement = pos=(0,0,36.15) rot=(0,0,1;0rad)
  Radius = 4
FEATURE [Part::MultiFuse] Fusion026  label="removeToCreteHoleForPlugHousing"
  Placement = pos=(70,19,36) rot=(0,1,0;1.5708rad)
  Shapes = -> [Cylinder006,Cylinder007]
FEATURE [Part::Box] Box001  label="Cube001"
  AttacherType = Attacher::AttachEngine3D
  Height = 28
  Length = 3
  Placement = pos=(110.7,19,22) rot=(0,0,1;0rad)
  Width = 15.7
FEATURE [Part::Cut] Cut003  label="top002"
  Base = -> Cut001
  Tool = -> Fusion007
FEATURE [Part::Revolution] Revolve008  label="plugHousing015"
  Angle = 360
  Axis = (0,1,0)
  Base = (0,0,0)
  FaceMakerClass = Part::FaceMakerBullseye
  Placement = pos=(0,0,36.15) rot=(0,0,1;0rad)
  Solid = false
  Source = -> Face010
  Symmetric = false
FEATURE [Part::MultiFuse] Fusion013  label="plugHousing020"
  Placement = pos=(0,0,0) rot=(0,0,1;1.5708rad)
  Shapes = -> [Revolve008,Revolve012]
FEATURE [Part::Cut] Cut004  label="top003"
  Base = -> Cut003
  Placement = pos=(1,0,0) rot=(0,0,1;0rad)
  Tool = -> Fusion026
FEATURE [Part::Cylinder] Cylinder008
  Angle = 360
  AttacherType = Attacher::AttachEngine3D
  Height = 20
  Placement = pos=(0,0,36.15) rot=(0,0,1;0rad)
  Radius = 10.3
FEATURE [Part::Cylinder] Cylinder009
  Angle = 360
  AttacherType = Attacher::AttachEngine3D
  Height = 10
  Placement = pos=(0,0,36.15) rot=(0,0,1;0rad)
  Radius = 4
FEATURE [Part::MultiFuse] Fusion027  label="removeToCreteHoleForPlugHousing001"
  Placement = pos=(70,19,36) rot=(0,1,0;1.5708rad)
  Shapes = -> [Cylinder008,Cylinder009]
FEATURE [Part::Cut] Cut005  label="plugHousingTab"
  Base = -> Box001
  Tool = -> Fusion027
FEATURE [Part::MultiFuse] Fusion028  label="plugHousing045"
  Shapes = -> [Fusion024,Cut005]
FEATURE [Part::Box] Box002  label="Cube002"
  AttacherType = Attacher::AttachEngine3D
  Height = 28.8
  Length = 3
  Placement = pos=(107.3,28,21.6) rot=(0,0,1;0rad)
  Width = 7
FEATURE [Part::Box] Box003  label="Cube003"
  AttacherType = Attacher::AttachEngine3D
  Height = 3
  Length = 6.4
  Placement = pos=(107.3,28,18.6) rot=(0,0,1;0rad)
  Width = 7
FEATURE [Part::Box] Box004  label="Cube004"
  AttacherType = Attacher::AttachEngine3D
  Height = 3
  Length = 6.4
  Placement = pos=(107.3,28,50.4) rot=(0,0,1;0rad)
  Width = 7
FEATURE [Part::MultiFuse] Fusion029  label="plugHousingBracketHolder"
  Shapes = -> [Box004,Box002,Box003]
FEATURE [Part::Cylinder] Cylinder010
  Angle = 360
  AttacherType = Attacher::AttachEngine3D
  Height = 20
  Placement = pos=(0,0,36.15) rot=(0,0,1;0rad)
  Radius = 14.3
FEATURE [Part::Cylinder] Cylinder011
  Angle = 360
  AttacherType = Attacher::AttachEngine3D
  Height = 10
  Placement = pos=(0,0,36.15) rot=(0,0,1;0rad)
  Radius = 4
FEATURE [Part::MultiFuse] Fusion030  label="removeToCreteHoleForPlugHousing002"
  Placement = pos=(70,19,36) rot=(0,1,0;1.5708rad)
  Shapes = -> [Cylinder010,Cylinder011]
FEATURE [Part::Cut] Cut006  label="plugHousingBracketHolder001"
  Base = -> Fusion029
  Tool = -> Fusion030
FEATURE [Part::Cylinder] Cylinder012
  Angle = 360
  AttacherType = Attacher::AttachEngine3D
  Height = 20
  Placement = pos=(0,0,36.15) rot=(0,0,1;0rad)
  Radius = 7
FEATURE [Part::Cylinder] Cylinder013
  Angle = 360
  AttacherType = Attacher::AttachEngine3D
  Height = 10
  Placement = pos=(0,0,36.15) rot=(0,0,1;0rad)
  Radius = 4
FEATURE [Part::MultiFuse] Fusion032  label="removeToCreteHoleForPlugHousing003"
  Placement = pos=(70,19,36) rot=(0,1,0;1.5708rad)
  Shapes = -> [Cylinder012,Cylinder013]
FEATURE [Part::Cut] Cut007  label="bottom002"
  Base = -> Cut002
  Tool = -> Fusion032
FEATURE [Sketcher::SketchObject] Sketch008
  FullyConstrained = true
  sketch-geometry (54):
    g0: LineSegment StartX=-4.2 StartY=0 StartZ=0 EndX=-6.2 EndY=0 EndZ=0
    g1: LineSegment StartX=-14 StartY=-18 StartZ=0 EndX=-14 EndY=-26.5 EndZ=0
    g2: LineSegment StartX=-4.2 StartY=0 StartZ=0 EndX=-4.2 EndY=-13.4877 EndZ=0
    g3: Circle CenterX=-4.2 CenterY=-13.4877 CenterZ=0 NormalX=0 NormalY=0 NormalZ=1 AngleXU=0 Radius=1
    g4: Circle CenterX=-4.2 CenterY=-26.5 CenterZ=0 NormalX=0 NormalY=0 NormalZ=1 AngleXU=0 Radius=1
    g5: Circle CenterX=-8.2 CenterY=-26.5 CenterZ=0 NormalX=0 NormalY=0 NormalZ=1 AngleXU=0 Radius=1
    g6: BSplineCurve PolesCount=3 KnotsCount=2 Degree=2 IsPeriodic=0
    g7: GeomPoint X=-4.2 Y=-13.4877 Z=0
    g8: GeomPoint X=-8.2 Y=-26.5 Z=0
    g9: LineSegment StartX=-14 StartY=-26.5 StartZ=0 EndX=-8.2 EndY=-26.5 EndZ=0
    g10: LineSegment StartX=-10.15 StartY=-12 StartZ=0 EndX=-10.15 EndY=-14 EndZ=0
    g11: LineSegment StartX=-12.8401 StartY=-16 StartZ=0 EndX=-10.1571 EndY=-16 EndZ=0
    g12: LineSegment StartX=-10.15 StartY=-14 StartZ=0 EndX=-8.70761 EndY=-14 EndZ=0
    g13: LineSegment StartX=-12.8401 StartY=-16 StartZ=0 EndX=-12.8401 EndY=-17.6958 EndZ=0
    g14: LineSegment StartX=-10.15 StartY=-12 StartZ=0 EndX=-7.79258 EndY=-12 EndZ=0
    g15: Circle CenterX=-6.2215 CenterY=-2 CenterZ=0 NormalX=0 NormalY=0 NormalZ=1 AngleXU=0 Radius=1
    g16: Circle CenterX=-6.22762 CenterY=-2.58724 CenterZ=0 NormalX=0 NormalY=0 NormalZ=1 AngleXU=0 Radius=1
    g17: Circle CenterX=-6.32538 CenterY=-4 CenterZ=0 NormalX=0 NormalY=0 NormalZ=1 AngleXU=0 Radius=1
    g18: BSplineCurve PolesCount=3 KnotsCount=2 Degree=2 IsPeriodic=0
    g19: GeomPoint X=-6.2215 Y=-2 Z=0
    g20: GeomPoint X=-6.32538 Y=-4 Z=0
    g21: Circle CenterX=-6.48644 CenterY=-5.99526 CenterZ=0 NormalX=0 NormalY=0 NormalZ=1 AngleXU=0 Radius=1
    g22: Circle CenterX=-6.58486 CenterY=-6.99526 CenterZ=0 NormalX=0 NormalY=0 NormalZ=1 AngleXU=0 Radius=1
    g23: Circle CenterX=-6.77343 CenterY=-8 CenterZ=0 NormalX=0 NormalY=0 NormalZ=1 AngleXU=0 Radius=1
    g24: BSplineCurve PolesCount=3 KnotsCount=2 Degree=2 IsPeriodic=0
    g25: GeomPoint X=-6.48644 Y=-5.99526 Z=0
    g26: GeomPoint X=-6.77343 Y=-8 Z=0
    g27: Circle CenterX=-7.19003 CenterY=-10 CenterZ=0 NormalX=0 NormalY=0 NormalZ=1 AngleXU=0 Radius=1
    g28: Circle CenterX=-7.44407 CenterY=-11.0915 CenterZ=0 NormalX=0 NormalY=0 NormalZ=1 AngleXU=0 Radius=1
    g29: Circle CenterX=-7.79258 CenterY=-12 CenterZ=0 NormalX=0 NormalY=0 NormalZ=1 AngleXU=0 Radius=1
    g30: BSplineCurve PolesCount=3 KnotsCount=2 Degree=2 IsPeriodic=0
    g31: GeomPoint X=-7.19003 Y=-10 Z=0
    g32: GeomPoint X=-7.79258 Y=-12 Z=0
    g33: Circle CenterX=-8.70761 CenterY=-14 CenterZ=0 NormalX=0 NormalY=0 NormalZ=1 AngleXU=0 Radius=1
    g34: Circle CenterX=-9.33087 CenterY=-15.1837 CenterZ=0 NormalX=0 NormalY=0 NormalZ=1 AngleXU=0 Radius=1
    g35: Circle CenterX=-10.1571 CenterY=-16 CenterZ=0 NormalX=0 NormalY=0 NormalZ=1 AngleXU=0 Radius=1
    g36: BSplineCurve PolesCount=3 KnotsCount=2 Degree=2 IsPeriodic=0
    g37: GeomPoint X=-8.70761 Y=-14 Z=0
    g38: GeomPoint X=-10.1571 Y=-16 Z=0
    g39: Circle CenterX=-12.8401 CenterY=-17.6958 CenterZ=0 NormalX=0 NormalY=0 NormalZ=1 AngleXU=0 Radius=1
    g40: Circle CenterX=-13.3521 CenterY=-17.9027 CenterZ=0 NormalX=0 NormalY=0 NormalZ=1 AngleXU=0 Radius=1
    g41: Circle CenterX=-14 CenterY=-18 CenterZ=0 NormalX=0 NormalY=0 NormalZ=1 AngleXU=0 Radius=1
    g42: BSplineCurve PolesCount=3 KnotsCount=2 Degree=2 IsPeriodic=0
    g43: GeomPoint X=-12.8401 Y=-17.6958 Z=0
    g44: GeomPoint X=-14 Y=-18 Z=0
    g45: LineSegment StartX=-6.2 StartY=0 StartZ=0 EndX=-7.2 EndY=0 EndZ=0
    g46: LineSegment StartX=-7.2 StartY=0 StartZ=0 EndX=-7.2 EndY=-2 EndZ=0
    g47: LineSegment StartX=-7.2 StartY=-2 StartZ=0 EndX=-6.2215 EndY=-2 EndZ=0
    g48: LineSegment StartX=-6.32538 StartY=-4 StartZ=0 EndX=-7.65538 EndY=-4 EndZ=0
    g49: LineSegment StartX=-7.65538 StartY=-4 StartZ=0 EndX=-7.65538 EndY=-5.99526 EndZ=0
    g50: LineSegment StartX=-7.65538 StartY=-5.99526 StartZ=0 EndX=-6.48644 EndY=-5.99526 EndZ=0
    g51: LineSegment StartX=-6.77343 StartY=-8 StartZ=0 EndX=-8.43343 EndY=-8 EndZ=0
    g52: LineSegment StartX=-8.43343 StartY=-8 StartZ=0 EndX=-8.43343 EndY=-10 EndZ=0
    g53: LineSegment StartX=-8.43343 StartY=-10 StartZ=0 EndX=-7.19003 EndY=-10 EndZ=0
  constraints (112):
    c: Horizontal(g0)
    c: Distance(g0) = 2
    c: Block(g0)
    c: Vertical(g1)
    c: Coincident(g2,g0)
    c: Vertical(g2)
    c: Block(g2)
    c: Coincident(g6,g2)
    c: Weight(g3) = 1
    c: Equal(g3,g4)
    c: Equal(g3,g5)
    c: InternalAlignment(g3,g6)
    c: InternalAlignment(g4,g6)
    c: InternalAlignment(g5,g6)
    c: InternalAlignment(g7,g6)
    c: InternalAlignment(g8,g6)
    c: Block(g6)
    c: Coincident(g9,g1)
    c: Coincident(g9,g6)
    c: Horizontal(g9)
    c: Vertical(g10)
    c: Block(g10)
    c: Horizontal(g11)
    c: Block(g11)
    c: Coincident(g12,g10)
    c: Horizontal(g12)
    c: Block(g12)
    c: Coincident(g13,g11)
    c: Vertical(g13)
    c: Block(g13)
    c: Coincident(g14,g10)
    c: Horizontal(g14)
    c: Block(g14)
    c: Block(g9)
    c: Block(g1)
    c: Weight(g15) = 1
    c: Equal(g15,g16)
    c: Equal(g15,g17)
    c: InternalAlignment(g15,g18)
    c: InternalAlignment(g16,g18)
    c: InternalAlignment(g17,g18)
    c: InternalAlignment(g19,g18)
    c: InternalAlignment(g20,g18)
    c: Weight(g21) = 1
    c: Equal(g21,g22)
    c: Equal(g21,g23)
    c: InternalAlignment(g21,g24)
    c: InternalAlignment(g22,g24)
    c: InternalAlignment(g23,g24)
    c: InternalAlignment(g25,g24)
    c: InternalAlignment(g26,g24)
    c: Weight(g27) = 1
    c: Equal(g27,g28)
    c: Equal(g27,g29)
    c: Coincident(g30,g14)
    c: InternalAlignment(g27,g30)
    c: InternalAlignment(g28,g30)
    c: InternalAlignment(g29,g30)
    c: InternalAlignment(g31,g30)
    c: InternalAlignment(g32,g30)
    c: Coincident(g36,g12)
    c: Weight(g33) = 1
    c: Equal(g33,g34)
    c: Equal(g33,g35)
    c: Coincident(g36,g11)
    c: InternalAlignment(g33,g36)
    c: InternalAlignment(g34,g36)
    c: InternalAlignment(g35,g36)
    c: InternalAlignment(g37,g36)
    c: InternalAlignment(g38,g36)
    c: Coincident(g42,g13)
    c: Weight(g39) = 1
    c: Equal(g39,g40)
    c: Equal(g39,g41)
    c: Coincident(g42,g1)
    c: InternalAlignment(g39,g42)
    c: InternalAlignment(g40,g42)
    c: InternalAlignment(g41,g42)
    c: InternalAlignment(g43,g42)
    c: InternalAlignment(g44,g42)
    c: Block(g18)
    c: Block(g24)
    c: Block(g30)
    c: Block(g36)
    c: Block(g42)
    c: Horizontal(g45)
    c: Coincident(g45,g0)
    c: Vertical(g46)
    c: Coincident(g46,g45)
    c: Coincident(g47,g46)
    c: Coincident(g47,g18)
    c: Horizontal(g47)
    c: Block(g46)
    c: Coincident(g48,g18)
    c: Horizontal(g48)
    c: Distance(g48) = 1.33
    c: Vertical(g49)
    c: Coincident(g49,g48)
    c: Coincident(g50,g49)
    c: Coincident(g50,g24)
    c: Horizontal(g50)
    c: Tangent(g50,g22)
    c: Horizontal(g51)
    c: Coincident(g51,g24)
    c: Block(g51)
    c: Vertical(g52)
    c: Block(g52)
    c: Coincident(g52,g51)
    c: Coincident(g53,g52)
    c: Coincident(g53,g30)
    c: Horizontal(g53)
    c: Distance(g1) = 8.5
FEATURE [Part::Feature] Face024
  shape: bbox 9.8 x 26.5 x 2e-07 mm, 1 faces, 0 solids (baked)
FEATURE [Part::Revolution] Revolve024
  Angle = 360
  Axis = (0,1,0)
  Base = (0,0,0)
  FaceMakerClass = Part::FaceMakerBullseye
  Placement = pos=(0,0,0) rot=(0,0,1;1.5708rad)
  Solid = false
  Source = -> Face024
  Symmetric = false
FEATURE [Part::Feature] Face025
  shape: bbox 9.8 x 26.5 x 2e-07 mm, 1 faces, 0 solids (baked)
FEATURE [Part::Revolution] Revolve025
  Angle = 360
  Axis = (0,1,0)
  Base = (0,0,0)
  FaceMakerClass = Part::FaceMakerBullseye
  Placement = pos=(0,0,0) rot=(0,0,1;1.5708rad)
  Solid = false
  Source = -> Face025
  Symmetric = false
FEATURE [Part::MultiFuse] Fusion033
  Placement = pos=(-18,19,36) rot=(0,0,1;0rad)
  Shapes = -> [Revolve025,Revolve024]
FEATURE [Part::Cylinder] Cylinder014
  Angle = 360
  AttacherType = Attacher::AttachEngine3D
  Height = 20
  Placement = pos=(0,0,36.15) rot=(0,0,1;0rad)
  Radius = 14.3
FEATURE [Part::Cylinder] Cylinder015
  Angle = 360
  AttacherType = Attacher::AttachEngine3D
  Height = 10
  Placement = pos=(0,0,36.15) rot=(0,0,1;0rad)
  Radius = 4
FEATURE [Part::MultiFuse] Fusion034  label="removeToCreteHoleForPlugHousing004"
  Placement = pos=(-42,19,36) rot=(0,1,0;1.5708rad)
  Shapes = -> [Cylinder014,Cylinder015]
FEATURE [Part::Cut] Cut008  label="top004"
  Base = -> Cut004
  Placement = pos=(-1,0,0) rot=(0,0,1;0rad)
  Tool = -> Fusion034
FEATURE [Part::Box] Box005  label="Cube005"
  AttacherType = Attacher::AttachEngine3D
  Height = 28
  Length = 3
  Placement = pos=(110.7,19,22) rot=(0,0,1;0rad)
  Width = 15.7
FEATURE [Part::Cylinder] Cylinder016
  Angle = 360
  AttacherType = Attacher::AttachEngine3D
  Height = 10
  Placement = pos=(0,0,36.15) rot=(0,0,1;0rad)
  Radius = 4
FEATURE [Part::Cylinder] Cylinder017
  Angle = 360
  AttacherType = Attacher::AttachEngine3D
  Height = 20
  Placement = pos=(0,0,36.15) rot=(0,0,1;0rad)
  Radius = 10.3
FEATURE [Part::MultiFuse] Fusion035  label="removeToCreteHoleForPlugHousing005"
  Placement = pos=(70,19,36) rot=(0,1,0;1.5708rad)
  Shapes = -> [Cylinder017,Cylinder016]
FEATURE [Part::Cut] Cut009  label="plugHousingTab001"
  Base = -> Box005
  Placement = pos=(-107.4,-14,0) rot=(0,0,1;0rad)
  Tool = -> Fusion035
FEATURE [Part::Box] Box006  label="Cube006"
  AttacherType = Attacher::AttachEngine3D
  Height = 28
  Length = 3
  Placement = pos=(110.7,19,22) rot=(0,0,1;0rad)
  Width = 15.7
FEATURE [Part::Cylinder] Cylinder018
  Angle = 360
  AttacherType = Attacher::AttachEngine3D
  Height = 10
  Placement = pos=(0,0,36.15) rot=(0,0,1;0rad)
  Radius = 4
FEATURE [Part::Cylinder] Cylinder019
  Angle = 360
  AttacherType = Attacher::AttachEngine3D
  Height = 20
  Placement = pos=(0,0,36.15) rot=(0,0,1;0rad)
  Radius = 10.3
FEATURE [Part::MultiFuse] Fusion036  label="removeToCreteHoleForPlugHousing006"
  Placement = pos=(70,19,36) rot=(0,1,0;1.5708rad)
  Shapes = -> [Cylinder019,Cylinder018]
FEATURE [Part::Cut] Cut010  label="plugHousingTab002"
  Base = -> Box006
  Placement = pos=(-107.4,-14,0) rot=(0,0,1;0rad)
  Tool = -> Fusion036
FEATURE [Part::MultiFuse] Fusion037
  Placement = pos=(9.6,23,0) rot=(0,0,1;3.14159rad)
  Shapes = -> [Cut009,Cut010]
FEATURE [Part::Box] Box  label="Cube"
  AttacherType = Attacher::AttachEngine3D
  Height = 10
  Length = 3
  Placement = pos=(3.3,4,12) rot=(0,0,1;0rad)
  Width = 10
FEATURE [Part::Fillet] Fillet004
  Base = -> Fusion028
  Edges = 1 edges r=2: [Edge25]
FEATURE [Part::Fillet] Fillet005  label="plugHousing046"
  Base = -> Fillet004
  Edges = 1 edges r=2: [Edge8]
FEATURE [Part::Fillet] Fillet006
  Base = -> Box
  Edges = 1 edges r=2: [Edge11]
FEATURE [Part::Box] Box007  label="Cube007"
  AttacherType = Attacher::AttachEngine3D
  Height = 10
  Length = 3
  Placement = pos=(3.3,4,50) rot=(0,0,1;0rad)
  Width = 10
FEATURE [Part::Fillet] Fillet007
  Base = -> Box007
  Edges = 1 edges r=2: [Edge12]
FEATURE [Part::Box] Box008  label="Cube008"
  AttacherType = Attacher::AttachEngine3D
  Height = 28
  Length = 4
  Placement = pos=(5,0,22) rot=(0,0,1;0rad)
  Width = 10
FEATURE [Part::Fillet] Fillet008
  Base = -> Box008
  Edges = 1 edges r=1: [Edge7]
FEATURE [Part::Fillet] Fillet009
  Base = -> Fillet008
  Edges = 1 edges r=2: [Edge5]
FEATURE [Part::Fillet] Fillet010
  Base = -> Fillet009
  Edges = 1 edges r=2: [Edge2]
FEATURE [Sketcher::SketchObject] Sketch009  label="topSketch003"
  FullyConstrained = true
  sketch-geometry (4):
    g0: LineSegment StartX=16.8446 StartY=31.512 StartZ=0 EndX=16.3251 EndY=34.4666 EndZ=0
    g1: ArcOfCircle CenterX=19 CenterY=19.2524 CenterZ=0 NormalX=0 NormalY=0 NormalZ=1 AngleXU=0 Radius=15.4476 StartAngle=1.74483 EndAngle=2.72717
    g2: ArcOfCircle CenterX=19 CenterY=19.2524 CenterZ=0 NormalX=0 NormalY=0 NormalZ=1 AngleXU=0 Radius=12.4476 StartAngle=1.74483 EndAngle=2.73189
    g3: LineSegment StartX=4.86004 StartY=25.4725 StartZ=0 EndX=7.58253 EndY=24.2107 EndZ=0
  constraints (7):
    c: Block(g0)
    c: Coincident(g1,g0)
    c: Coincident(g2,g0)
    c: Coincident(g3,g1)
    c: Coincident(g3,g2)
    c: Block(g1)
    c: Block(g2)
FEATURE [Part::Extrusion] Extrude008
  Base = -> Sketch009
  Dir = (0,0,1)
  DirMode = 2
  FaceMakerClass = Part::FaceMakerBullseye
  LengthFwd = 10
  LengthRev = 0
  Placement = pos=(0,0,31) rot=(0,0,1;0rad)
  Solid = true
  Symmetric = false
FEATURE [Part::Cylinder] Cylinder020
  Angle = 360
  AttacherType = Attacher::AttachEngine3D
  Height = 20
  Placement = pos=(0,0,36.15) rot=(0,0,1;0rad)
  Radius = 8.2
FEATURE [Part::Cylinder] Cylinder021
  Angle = 360
  AttacherType = Attacher::AttachEngine3D
  Height = 10
  Placement = pos=(0,0,36.15) rot=(0,0,1;0rad)
  Radius = 4
FEATURE [Part::MultiFuse] Fusion038  label="removeToCreteHoleForPlugHousing007"
  Placement = pos=(-42,19,36) rot=(0,1,0;1.5708rad)
  Shapes = -> [Cylinder020,Cylinder021]
FEATURE [Part::Cut] Cut011
  Base = -> Extrude008
  Tool = -> Fusion038
FEATURE [Part::Fillet] Fillet011
  Base = -> Cut011
  Edges = 1 edges r=2: [Edge1]
FEATURE [Part::Fillet] Fillet012
  Base = -> Fillet011
  Edges = 1 edges r=2.5: [Edge1]
FEATURE [Part::Fillet] Fillet013
  Base = -> Fillet012
  Edges = 1 edges r=2.5: [Edge2]
FEATURE [Part::Box] Box010  label="Cube010"
  AttacherType = Attacher::AttachEngine3D
  Height = 16
  Length = 8
  Placement = pos=(12.7,31.52,28) rot=(0,0,1;0rad)
  Width = 4
FEATURE [Sketcher::SketchObject] Sketch010  label="topSketch004"
  FullyConstrained = true
  sketch-geometry (4):
    g0: LineSegment StartX=16.8446 StartY=31.512 StartZ=0 EndX=16.3251 EndY=34.4666 EndZ=0
    g1: ArcOfCircle CenterX=19 CenterY=19.2524 CenterZ=0 NormalX=0 NormalY=0 NormalZ=1 AngleXU=0 Radius=15.4476 StartAngle=1.74483 EndAngle=2.72717
    g2: ArcOfCircle CenterX=19 CenterY=19.2524 CenterZ=0 NormalX=0 NormalY=0 NormalZ=1 AngleXU=0 Radius=12.4476 StartAngle=1.74483 EndAngle=2.73189
    g3: LineSegment StartX=4.86004 StartY=25.4725 StartZ=0 EndX=7.58253 EndY=24.2107 EndZ=0
  constraints (7):
    c: Block(g0)
    c: Coincident(g1,g0)
    c: Coincident(g2,g0)
    c: Coincident(g3,g1)
    c: Coincident(g3,g2)
    c: Block(g1)
    c: Block(g2)
FEATURE [Part::Cylinder] Cylinder022
  Angle = 360
  AttacherType = Attacher::AttachEngine3D
  Height = 10
  Placement = pos=(0,0,36.15) rot=(0,0,1;0rad)
  Radius = 4
FEATURE [Sketcher::SketchObject] Sketch011  label="topSketch005"
  FullyConstrained = true
  sketch-geometry (4):
    g0: LineSegment StartX=16.8446 StartY=31.512 StartZ=0 EndX=16.3251 EndY=34.4666 EndZ=0
    g1: ArcOfCircle CenterX=19 CenterY=19.2524 CenterZ=0 NormalX=0 NormalY=0 NormalZ=1 AngleXU=0 Radius=15.4476 StartAngle=1.74483 EndAngle=2.72717
    g2: ArcOfCircle CenterX=19 CenterY=19.2524 CenterZ=0 NormalX=0 NormalY=0 NormalZ=1 AngleXU=0 Radius=12.4476 StartAngle=1.74483 EndAngle=2.73189
    g3: LineSegment StartX=4.86004 StartY=25.4725 StartZ=0 EndX=7.58253 EndY=24.2107 EndZ=0
  constraints (7):
    c: Block(g0)
    c: Coincident(g1,g0)
    c: Coincident(g2,g0)
    c: Coincident(g3,g1)
    c: Coincident(g3,g2)
    c: Block(g1)
    c: Block(g2)
FEATURE [Part::Extrusion] Extrude010
  Base = -> Sketch011
  Dir = (0,0,1)
  DirMode = 2
  FaceMakerClass = Part::FaceMakerBullseye
  LengthFwd = 10.6
  LengthRev = 0
  Placement = pos=(0,0,31) rot=(0,0,1;0rad)
  Solid = true
  Symmetric = false
FEATURE [Part::Cylinder] Cylinder023
  Angle = 360
  AttacherType = Attacher::AttachEngine3D
  Height = 20
  Placement = pos=(0,0,36.15) rot=(0,0,1;0rad)
  Radius = 8.2
FEATURE [Part::MultiFuse] Fusion039  label="removeToCreteHoleForPlugHousing008"
  Placement = pos=(-42,19,36) rot=(0,1,0;1.5708rad)
  Shapes = -> [Cylinder023,Cylinder022]
FEATURE [Part::Cut] Cut012
  Base = -> Extrude010
  Placement = pos=(0,0,-0.3) rot=(0,0,1;0rad)
  Tool = -> Fusion039
FEATURE [Part::Cut] Cut013
  Base = -> Box010
  Tool = -> Cut012
FEATURE [Part::Fillet] Fillet014
  Base = -> Cut013
  Edges = 1 edges r=0.7: [Edge13]
FEATURE [Part::Fillet] Fillet015
  Base = -> Fillet014
  Edges = 1 edges r=0.7: [Edge13]
FEATURE [Part::Fillet] Fillet016
  Base = -> Fillet015
  Edges = 1 edges r=0.7: [Edge16]
FEATURE [Part::Fillet] Fillet017
  Base = -> Fillet016
  Edges = 1 edges r=0.7: [Edge11]
FEATURE [Part::Fillet] Fillet018
  Base = -> Fillet017
  Edges = 1 edges r=0.7: [Edge10]
FEATURE [Part::Fillet] Fillet019
  Base = -> Fillet018
  Edges = 1 edges r=1.2: [Edge5]
FEATURE [Part::Fillet] Fillet020
  Base = -> Fillet019
  Edges = 1 edges r=1.2: [Edge12]
FEATURE [Part::Fillet] Fillet021
  Base = -> Fillet020
  Edges = 1 edges r=2: [Edge1]
  Placement = pos=(0.3,0,0) rot=(0,0,1;0rad)
FEATURE [Part::MultiFuse] Fusion040  label="top005"
  Shapes = -> [Cut008,Fillet021]
FEATURE [Part::MultiFuse] Fusion041  label="wireHolder"
  Shapes = -> [Fusion033,Fillet013]
FEATURE [Part::MultiFuse] Fusion042
  Shapes = -> [Fillet007,Fusion041]
FEATURE [Part::MultiFuse] Fusion043  label="wireHolder001"
  Shapes = -> [Fusion042,Fillet010]
FEATURE [Part::MultiFuse] Fusion044  label="wireHolder002"
  Shapes = -> [Fillet006,Fusion037,Fusion043]
FEATURE [Part::Feature] Face026
  shape: bbox 11 x 6 x 2e-07 mm, 1 faces, 0 solids (baked)
FEATURE [Part::Revolution] Revolve026
  Angle = 360
  Axis = (0,1,0)
  Base = (0,0,0)
  FaceMakerClass = Part::FaceMakerBullseye
  Placement = pos=(30.3,-1,19.7) rot=(0,0,1;0rad)
  Solid = false
  Source = -> Face026
  Symmetric = false
FEATURE [Sketcher::SketchObject] Sketch013  label="topSketch006"
  FullyConstrained = true
  sketch-geometry (13):
    g0: LineSegment StartX=117 StartY=19 StartZ=0 EndX=117 EndY=38 EndZ=0
    g1: ArcOfCircle CenterX=98 CenterY=19 CenterZ=0 NormalX=0 NormalY=0 NormalZ=1 AngleXU=0 Radius=19 StartAngle=5.7297 EndAngle=6.28319
    g2: LineSegment StartX=0 StartY=3 StartZ=0 EndX=0 EndY=19 EndZ=0
    g3: LineSegment StartX=19 StartY=38 StartZ=0 EndX=117 EndY=38 EndZ=0
    g4: ArcOfCircle CenterX=19 CenterY=19 CenterZ=0 NormalX=0 NormalY=0 NormalZ=1 AngleXU=0 Radius=19 StartAngle=1.5708 EndAngle=3.14159
    g5: ArcOfCircle CenterX=19 CenterY=19 CenterZ=0 NormalX=0 NormalY=0 NormalZ=1 AngleXU=0 Radius=16 StartAngle=1.5708 EndAngle=3.14159
    g6: ArcOfCircle CenterX=98 CenterY=19 CenterZ=0 NormalX=0 NormalY=0 NormalZ=1 AngleXU=0 Radius=16 StartAngle=5.60905 EndAngle=6.28319
    g7: LineSegment StartX=114 StartY=19 StartZ=0 EndX=114 EndY=35 EndZ=0
    g8: LineSegment StartX=110.5 StartY=9.01251 StartZ=0 EndX=114.163 EndY=9.01251 EndZ=0
    g9: LineSegment StartX=114 StartY=35 StartZ=0 EndX=19 EndY=35 EndZ=0
    g10: LineSegment StartX=0 StartY=3 StartZ=0 EndX=0 EndY=0 EndZ=0
    g11: LineSegment StartX=3 StartY=0 StartZ=0 EndX=0 EndY=0 EndZ=0
    g12: LineSegment StartX=3 StartY=19 StartZ=0 EndX=3 EndY=0 EndZ=0
  constraints (33):
    c: Vertical(g0)
    c: Distance(g0) = 19
    c: Block(g0)
    c: Coincident(g1,g0)
    c: Block(g1)
    c: Vertical(g2)
    c: Block(g2)
    c: Coincident(g3,g0)
    c: Horizontal(g3)
    c: Distance(g3) = 98
    c: Coincident(g4,g3)
    c: Coincident(g4,g2)
    c: Block(g4)
    c: Coincident(g5,g4)
    c: Coincident(g6,g1)
    c: Block(g6)
    c: Block(g5)
    c: Coincident(g7,g6)
    c: Vertical(g7)
    c: Coincident(g8,g6)
    c: Coincident(g8,g1)
    c: Coincident(g9,g7)
    c: Coincident(g9,g5)
    c: Horizontal(g9)
    c: Tangent(g9,g5)
    c: Coincident(g10,g2)
    c: Distance(g10) = 3
    c: Vertical(g10)
    c: Coincident(g11,g10)
    c: Horizontal(g11)
    c: Coincident(g12,g5)
    c: Coincident(g12,g11)
    c: Vertical(g12)
FEATURE [Part::Extrusion] Extrude011  label="top006"
  Base = -> Sketch013
  Dir = (0,0,1)
  DirMode = 2
  FaceMakerClass = Part::FaceMakerBullseye
  LengthFwd = 72
  LengthRev = 0
  Solid = true
  Symmetric = false
FEATURE [Sketcher::SketchObject] Sketch014
  FullyConstrained = true
  MapMode = 3
  Placement = pos=(0,0,0) rot=(1,0,0;1.5708rad)
  Support = -> [Extrude011]
  sketch-geometry (8):
    g0: Circle CenterX=80.351 CenterY=-67.6202 CenterZ=0 NormalX=0 NormalY=0 NormalZ=1 AngleXU=0 Radius=2
    g1: Circle CenterX=80.351 CenterY=-67.6202 CenterZ=0 NormalX=0 NormalY=0 NormalZ=1 AngleXU=0 Radius=3
    g2: Circle CenterX=80.351 CenterY=-4.92017 CenterZ=0 NormalX=0 NormalY=0 NormalZ=1 AngleXU=0 Radius=2
    g3: Circle CenterX=80.351 CenterY=-4.92017 CenterZ=0 NormalX=0 NormalY=0 NormalZ=1 AngleXU=0 Radius=3
    g4: Circle CenterX=23.851 CenterY=-4.92017 CenterZ=0 NormalX=0 NormalY=0 NormalZ=1 AngleXU=0 Radius=2
    g5: Circle CenterX=23.851 CenterY=-4.92017 CenterZ=0 NormalX=0 NormalY=0 NormalZ=1 AngleXU=0 Radius=3
    g6: Circle CenterX=23.851 CenterY=-67.6202 CenterZ=0 NormalX=0 NormalY=0 NormalZ=1 AngleXU=0 Radius=2
    g7: Circle CenterX=23.851 CenterY=-67.6202 CenterZ=0 NormalX=0 NormalY=0 NormalZ=1 AngleXU=0 Radius=3
  constraints (8):
    c: Block(g3)
    c: Block(g2)
    c: Block(g1)
    c: Block(g0)
    c: Block(g6)
    c: Block(g7)
    c: Block(g4)
    c: Block(g5)
FEATURE [Part::Feature] Face027
  shape: bbox 11 x 6 x 2e-07 mm, 1 faces, 0 solids (baked)
FEATURE [Part::Revolution] Revolve027
  Angle = 360
  Axis = (0,1,0)
  Base = (0,0,0)
  FaceMakerClass = Part::FaceMakerBullseye
  Placement = pos=(30.3,-1,51.7) rot=(0,0,1;0rad)
  Solid = false
  Source = -> Face027
  Symmetric = false
FEATURE [Part::Feature] Face028
  shape: bbox 11 x 6 x 2e-07 mm, 1 faces, 0 solids (baked)
FEATURE [Part::Revolution] Revolve028
  Angle = 360
  Axis = (0,1,0)
  Base = (0,0,0)
  FaceMakerClass = Part::FaceMakerBullseye
  Placement = pos=(62.3,-1,19.7) rot=(0,0,1;0rad)
  Solid = false
  Source = -> Face028
  Symmetric = false
FEATURE [Part::Feature] Face029
  shape: bbox 11 x 6 x 2e-07 mm, 1 faces, 0 solids (baked)
FEATURE [Part::Revolution] Revolve029
  Angle = 360
  Axis = (0,1,0)
  Base = (0,0,0)
  FaceMakerClass = Part::FaceMakerBullseye
  Placement = pos=(62.3,-1,51.7) rot=(0,0,1;0rad)
  Solid = false
  Source = -> Face029
  Symmetric = false
FEATURE [Part::Feature] Wire
  shape: bbox 11 x 5.2 x 2e-07 mm, 0 faces, 0 solids (baked)
FEATURE [Part::Revolution] Revolve030
  Angle = 360
  Axis = (0,1,0)
  Base = (0,0,0)
  FaceMakerClass = Part::FaceMakerBullseye
  Placement = pos=(30.3,38,19.7) rot=(0,0,1;0rad)
  Solid = true
  Source = -> Wire
  Symmetric = false
FEATURE [Part::Feature] Wire001
  shape: bbox 11 x 5.2 x 2e-07 mm, 0 faces, 0 solids (baked)
FEATURE [Part::Revolution] Revolve031
  Angle = 360
  Axis = (0,1,0)
  Base = (0,0,0)
  FaceMakerClass = Part::FaceMakerBullseye
  Placement = pos=(30.3,38,51.7) rot=(0,0,1;0rad)
  Solid = true
  Source = -> Wire001
  Symmetric = false
FEATURE [Part::Feature] Wire002
  shape: bbox 11 x 5.2 x 2e-07 mm, 0 faces, 0 solids (baked)
FEATURE [Part::Revolution] Revolve032
  Angle = 360
  Axis = (0,1,0)
  Base = (0,0,0)
  FaceMakerClass = Part::FaceMakerBullseye
  Placement = pos=(62.3,38,51.7) rot=(0,0,1;0rad)
  Solid = true
  Source = -> Wire002
  Symmetric = false
FEATURE [Part::Feature] Wire003
  shape: bbox 11 x 5.2 x 2e-07 mm, 0 faces, 0 solids (baked)
FEATURE [Part::Revolution] Revolve033
  Angle = 360
  Axis = (0,1,0)
  Base = (0,0,0)
  FaceMakerClass = Part::FaceMakerBullseye
  Placement = pos=(62.3,38,19.7) rot=(0,0,1;0rad)
  Solid = true
  Source = -> Wire003
  Symmetric = false
FEATURE [Part::MultiFuse] Fusion045  label="altRandScrewHousing"
  Shapes = -> [Revolve029,Revolve027,Revolve028,Revolve026]
FEATURE [Part::MultiFuse] Fusion046  label="fanScrewHousing"
  Shapes = -> [Revolve033,Revolve032,Revolve031,Revolve030]
FEATURE [Sketcher::SketchObject] Sketch015
  FullyConstrained = true
  sketch-geometry (17):
    g0: Circle CenterX=-3.5 CenterY=23.5 CenterZ=0 NormalX=0 NormalY=0 NormalZ=1 AngleXU=0 Radius=1
    g1: Circle CenterX=-1 CenterY=15.25 CenterZ=0 NormalX=0 NormalY=0 NormalZ=1 AngleXU=0 Radius=1
    g2: Circle CenterX=-3.5 CenterY=7 CenterZ=0 NormalX=0 NormalY=0 NormalZ=1 AngleXU=0 Radius=1
    g3: BSplineCurve PolesCount=3 KnotsCount=2 Degree=2 IsPeriodic=0
    g4: GeomPoint X=-3.5 Y=23.5 Z=0
    g5: GeomPoint X=-3.5 Y=7 Z=0
    g6: Circle CenterX=-4.8 CenterY=30.5 CenterZ=0 NormalX=0 NormalY=0 NormalZ=1 AngleXU=0 Radius=1
    g7: Circle CenterX=-3.5 CenterY=30.5 CenterZ=0 NormalX=0 NormalY=0 NormalZ=1 AngleXU=0 Radius=1
    g8: Circle CenterX=-3.5 CenterY=29.2 CenterZ=0 NormalX=0 NormalY=0 NormalZ=1 AngleXU=0 Radius=1
    g9: BSplineCurve PolesCount=3 KnotsCount=2 Degree=2 IsPeriodic=0
    g10: GeomPoint X=-4.8 Y=30.5 Z=0
    g11: GeomPoint X=-3.5 Y=29.2 Z=0
    g12: LineSegment StartX=-3.5 StartY=29.2 StartZ=0 EndX=-3.5 EndY=23.5 EndZ=0
    g13: LineSegment StartX=-4.8 StartY=30.5 StartZ=0 EndX=0 EndY=30.5 EndZ=0
    g14: LineSegment StartX=-3.5 StartY=0.3 StartZ=0 EndX=0 EndY=0.3 EndZ=0
    g15: LineSegment StartX=-3.5 StartY=0.3 StartZ=0 EndX=-3.5 EndY=7 EndZ=0
    g16: LineSegment StartX=0 StartY=0.3 StartZ=0 EndX=0 EndY=30.5 EndZ=0
  constraints (33):
    c: Weight(g0) = 1
    c: Equal(g0,g1)
    c: Equal(g0,g2)
    c: InternalAlignment(g0,g3)
    c: InternalAlignment(g1,g3)
    c: InternalAlignment(g2,g3)
    c: InternalAlignment(g4,g3)
    c: InternalAlignment(g5,g3)
    c: Block(g3)
    c: Weight(g6) = 1
    c: Equal(g6,g7)
    c: Equal(g6,g8)
    c: InternalAlignment(g6,g9)
    c: InternalAlignment(g7,g9)
    c: InternalAlignment(g8,g9)
    c: InternalAlignment(g10,g9)
    c: InternalAlignment(g11,g9)
    c: Block(g9)
    c: Coincident(g12,g9)
    c: Coincident(g12,g3)
    c: Vertical(g12)
    c: Coincident(g13,g9)
    c: Horizontal(g13)
    c: Distance(g13) = 4.8
    c: Horizontal(g14)
    c: Block(g14)
    c: Coincident(g15,g14)
    c: Coincident(g15,g3)
    c: Vertical(g15)
    c: Coincident(g16,g14)
    c: Coincident(g16,g13)
    c: Vertical(g16)
    c: Tangent(g16,g1)
FEATURE [Sketcher::SketchObject] Sketch016
  FullyConstrained = true
  sketch-geometry (16):
    g0: Circle CenterX=-3.5 CenterY=23.5 CenterZ=0 NormalX=0 NormalY=0 NormalZ=1 AngleXU=0 Radius=1
    g1: Circle CenterX=-1 CenterY=15.25 CenterZ=0 NormalX=0 NormalY=0 NormalZ=1 AngleXU=0 Radius=1
    g2: Circle CenterX=-3.5 CenterY=7 CenterZ=0 NormalX=0 NormalY=0 NormalZ=1 AngleXU=0 Radius=1
    g3: BSplineCurve PolesCount=3 KnotsCount=2 Degree=2 IsPeriodic=0
    g4: GeomPoint X=-3.5 Y=23.5 Z=0
    g5: GeomPoint X=-3.5 Y=7 Z=0
    g6: LineSegment StartX=-3.5 StartY=28.2 StartZ=0 EndX=-3.5 EndY=23.5 EndZ=0
    g7: LineSegment StartX=0 StartY=29.5 StartZ=0 EndX=0 EndY=30 EndZ=0
    g8: LineSegment StartX=-3.5 StartY=28.2 StartZ=0 EndX=-3.5 EndY=30 EndZ=0
    g9: LineSegment StartX=0 StartY=30 StartZ=0 EndX=0 EndY=30.5 EndZ=0
    g10: LineSegment StartX=0 StartY=30.5 StartZ=0 EndX=-3.5 EndY=30.5 EndZ=0
    g11: LineSegment StartX=-3.5 StartY=30.5 StartZ=0 EndX=-3.5 EndY=30 EndZ=0
    g12: LineSegment StartX=0 StartY=29.5 StartZ=0 EndX=0 EndY=5 EndZ=0
    g13: LineSegment StartX=-3.5 StartY=0.3 StartZ=0 EndX=-3.5 EndY=7 EndZ=0
    g14: LineSegment StartX=-3.5 StartY=0.3 StartZ=0 EndX=0 EndY=0.3 EndZ=0
    g15: LineSegment StartX=0 StartY=5 StartZ=0 EndX=0 EndY=0.3 EndZ=0
  constraints (39):
    c: Weight(g0) = 1
    c: Equal(g0,g1)
    c: Equal(g0,g2)
    c: InternalAlignment(g0,g3)
    c: InternalAlignment(g1,g3)
    c: InternalAlignment(g2,g3)
    c: InternalAlignment(g4,g3)
    c: InternalAlignment(g5,g3)
    c: Block(g3)
    c: Coincident(g6,g3)
    c: Vertical(g6)
    c: Vertical(g7)
    c: Distance(g7) = 0.5
    c: Coincident(g8,g6)
    c: Vertical(g8)
    c: Block(g6)
    c: Block(g7)
    c: Vertical(g9)
    c: Equal(g7,g9) = 0.5
    c: Block(g9)
    c: Coincident(g9,g7)
    c: Horizontal(g10)
    c: Coincident(g10,g9)
    c: Coincident(g11,g10)
    c: Coincident(g11,g8)
    c: Vertical(g11)
    c: Block(g11)
    c: Coincident(g12,g7)
    c: Vertical(g12)
    c: Coincident(g13,g3)
    c: Vertical(g13)
    c: Distance(g13) = 6.7
    c: Coincident(g14,g13)
    c: Horizontal(g14)
    c: Block(g14)
    c: Coincident(g15,g12)
    c: Coincident(g15,g14)
    c: Vertical(g15)
    c: Block(g15)
FEATURE [Sketcher::SketchObject] Sketch017
  FullyConstrained = true
  sketch-geometry (11):
    g0: LineSegment StartX=-3.5 StartY=1e-16 StartZ=0 EndX=-1.6 EndY=1e-16 EndZ=0
    g1: LineSegment StartX=-1.6 StartY=1e-16 StartZ=0 EndX=-1.6 EndY=1.5 EndZ=0
    g2: LineSegment StartX=-3.5 StartY=1.5 StartZ=0 EndX=-1.6 EndY=1.5 EndZ=0
    g3: LineSegment StartX=-3.5 StartY=1e-16 StartZ=0 EndX=-4.8 EndY=1e-16 EndZ=0
    g4: Circle CenterX=-3.5 CenterY=1.3 CenterZ=0 NormalX=0 NormalY=0 NormalZ=1 AngleXU=0 Radius=1
    g5: Circle CenterX=-3.5 CenterY=1e-16 CenterZ=0 NormalX=0 NormalY=0 NormalZ=1 AngleXU=0 Radius=1
    g6: Circle CenterX=-4.8 CenterY=1e-16 CenterZ=0 NormalX=0 NormalY=0 NormalZ=1 AngleXU=0 Radius=1
    g7: BSplineCurve PolesCount=3 KnotsCount=2 Degree=2 IsPeriodic=0
    g8: GeomPoint X=-3.5 Y=1.3 Z=0
    g9: GeomPoint X=-4.8 Y=1e-16 Z=0
    g10: LineSegment StartX=-3.5 StartY=1.3 StartZ=0 EndX=-3.5 EndY=1.5 EndZ=0
  constraints (24):
    c: Horizontal(g0)
    c: Distance(g0) = 1.9
    c: Block(g0)
    c: Coincident(g1,g0)
    c: Vertical(g1)
    c: Coincident(g2,g1)
    c: Horizontal(g2)
    c: Coincident(g3,g0)
    c: Horizontal(g3)
    c: Distance(g3) = 1.3
    c: Weight(g4) = 1
    c: Equal(g4,g5)
    c: Coincident(g5,g0)
    c: Equal(g4,g6)
    c: Coincident(g7,g3)
    c: InternalAlignment(g4,g7)
    c: InternalAlignment(g5,g7)
    c: InternalAlignment(g6,g7)
    c: InternalAlignment(g8,g7)
    c: InternalAlignment(g9,g7)
    c: Coincident(g10,g7)
    c: Coincident(g10,g2)
    c: Vertical(g10)
    c: Block(g10)
FEATURE [Part::Feature] Face035
  shape: bbox 3.2 x 1.5 x 2e-07 mm, 1 faces, 0 solids (baked)
FEATURE [Part::Revolution] Revolve039  label="backCaseScrewRetainer"
  Angle = 360
  Axis = (0,1,0)
  Base = (0,0,0)
  FaceMakerClass = Part::FaceMakerBullseye
  Placement = pos=(12.5,3,62) rot=(0,0,1;0rad)
  Solid = false
  Source = -> Face035
  Symmetric = false
FEATURE [Part::Feature] Face036
  shape: bbox 3.2 x 1.5 x 2e-07 mm, 1 faces, 0 solids (baked)
FEATURE [Part::Feature] Face039
  shape: bbox 4.8 x 30.2 x 2e-07 mm, 1 faces, 0 solids (baked)
FEATURE [Part::Revolution] Revolve043  label="frontCaseScrewPost002"
  Angle = 360
  Axis = (0,1,0)
  Base = (0,0,0)
  FaceMakerClass = Part::FaceMakerBullseye
  Placement = pos=(89.5,4.5,3.5) rot=(0,0,1;0rad)
  Solid = false
  Source = -> Face039
  Symmetric = false
FEATURE [Part::Feature] Face042
  shape: bbox 4.8 x 30.2 x 2e-07 mm, 1 faces, 0 solids (baked)
FEATURE [Part::Revolution] Revolve046  label="frontCaseScrewPost003"
  Angle = 360
  Axis = (0,1,0)
  Base = (0,0,0)
  FaceMakerClass = Part::FaceMakerBullseye
  Placement = pos=(89.5,4.5,68.5) rot=(0,0,1;0rad)
  Solid = false
  Source = -> Face042
  Symmetric = false
FEATURE [Part::Feature] Face043
  shape: bbox 3.2 x 1.5 x 2e-07 mm, 1 faces, 0 solids (baked)
FEATURE [Part::Revolution] Revolve047  label="frontCaseScrewRetainer002"
  Angle = 360
  Axis = (0,1,0)
  Base = (0,0,0)
  FaceMakerClass = Part::FaceMakerBullseye
  Placement = pos=(89.5,3,68.5) rot=(0,0,1;0rad)
  Solid = false
  Source = -> Face043
  Symmetric = false
FEATURE [Part::Feature] Face044
  shape: bbox 3.2 x 1.5 x 2e-07 mm, 1 faces, 0 solids (baked)
FEATURE [Part::Revolution] Revolve048  label="frontCaseScrewRetainer003"
  Angle = 360
  Axis = (0,1,0)
  Base = (0,0,0)
  FaceMakerClass = Part::FaceMakerBullseye
  Placement = pos=(89.5,3,3.5) rot=(0,0,1;0rad)
  Solid = false
  Source = -> Face044
  Symmetric = false
FEATURE [App::MeasureDistance] Distance002  label="Distance: 1.67 mm"
  Distance = 1.66921
  P1 = (99.2361,4.7524,71.7)
  P2 = (99.2347,6.42161,71.7)
FEATURE [Sketcher::SketchObject] Sketch018
  FullyConstrained = true
  sketch-geometry (7):
    g0: LineSegment StartX=0 StartY=0 StartZ=0 EndX=0 EndY=6 EndZ=0
    g1: Circle CenterX=0 CenterY=0 CenterZ=0 NormalX=0 NormalY=0 NormalZ=1 AngleXU=0 Radius=1
    g2: Circle CenterX=8 CenterY=6 CenterZ=0 NormalX=0 NormalY=0 NormalZ=1 AngleXU=0 Radius=1
    g3: BSplineCurve PolesCount=3 KnotsCount=2 Degree=2 IsPeriodic=0
    g4: GeomPoint X=0 Y=0 Z=0
    g5: GeomPoint X=8 Y=6 Z=0
    g6: LineSegment StartX=0 StartY=6 StartZ=0 EndX=8 EndY=6 EndZ=0
  constraints (14):
    c: Coincident(g0,g-1)
    c: Distance(g0) = 6
    c: Vertical(g0)
    c: Coincident(g3,g0)
    c: Weight(g1) = 1
    c: Equal(g1,g2)
    c: InternalAlignment(g1,g3)
    c: InternalAlignment(g2,g3)
    c: InternalAlignment(g4,g3)
    c: InternalAlignment(g5,g3)
    c: Block(g3)
    c: Coincident(g6,g0)
    c: Coincident(g6,g3)
    c: Horizontal(g6)
FEATURE [Part::Extrusion] Extrude012  label="caseScrewPillarBracket"
  Base = -> Sketch018
  Dir = (0,0,1)
  DirMode = 2
  FaceMakerClass = Part::FaceMakerBullseye
  LengthFwd = 2.4
  LengthRev = 0
  Placement = pos=(15.76,29,8.8) rot=(0,1,0;0rad)
  Solid = true
  Symmetric = false
FEATURE [Sketcher::SketchObject] Sketch019
  FullyConstrained = true
  sketch-geometry (7):
    g0: LineSegment StartX=0 StartY=0 StartZ=0 EndX=0 EndY=6 EndZ=0
    g1: Circle CenterX=0 CenterY=0 CenterZ=0 NormalX=0 NormalY=0 NormalZ=1 AngleXU=0 Radius=1
    g2: Circle CenterX=8 CenterY=6 CenterZ=0 NormalX=0 NormalY=0 NormalZ=1 AngleXU=0 Radius=1
    g3: BSplineCurve PolesCount=3 KnotsCount=2 Degree=2 IsPeriodic=0
    g4: GeomPoint X=0 Y=0 Z=0
    g5: GeomPoint X=8 Y=6 Z=0
    g6: LineSegment StartX=0 StartY=6 StartZ=0 EndX=8 EndY=6 EndZ=0
  constraints (14):
    c: Coincident(g0,g-1)
    c: Distance(g0) = 6
    c: Vertical(g0)
    c: Coincident(g3,g0)
    c: Weight(g1) = 1
    c: Equal(g1,g2)
    c: InternalAlignment(g1,g3)
    c: InternalAlignment(g2,g3)
    c: InternalAlignment(g4,g3)
    c: InternalAlignment(g5,g3)
    c: Block(g3)
    c: Coincident(g6,g0)
    c: Coincident(g6,g3)
    c: Horizontal(g6)
FEATURE [Part::Extrusion] Extrude013  label="caseScrewPillarBracket001"
  Base = -> Sketch019
  Dir = (0,0,1)
  DirMode = 2
  FaceMakerClass = Part::FaceMakerBullseye
  LengthFwd = 2.4
  LengthRev = 0
  Placement = pos=(15.76,29,60.8) rot=(0,0,1;0rad)
  Solid = true
  Symmetric = false
FEATURE [Sketcher::SketchObject] Sketch020
  FullyConstrained = true
  sketch-geometry (7):
    g0: LineSegment StartX=0 StartY=0 StartZ=0 EndX=0 EndY=6 EndZ=0
    g1: Circle CenterX=0 CenterY=0 CenterZ=0 NormalX=0 NormalY=0 NormalZ=1 AngleXU=0 Radius=1
    g2: Circle CenterX=8 CenterY=6 CenterZ=0 NormalX=0 NormalY=0 NormalZ=1 AngleXU=0 Radius=1
    g3: BSplineCurve PolesCount=3 KnotsCount=2 Degree=2 IsPeriodic=0
    g4: GeomPoint X=0 Y=0 Z=0
    g5: GeomPoint X=8 Y=6 Z=0
    g6: LineSegment StartX=0 StartY=6 StartZ=0 EndX=8 EndY=6 EndZ=0
  constraints (14):
    c: Coincident(g0,g-1)
    c: Distance(g0) = 6
    c: Vertical(g0)
    c: Coincident(g3,g0)
    c: Weight(g1) = 1
    c: Equal(g1,g2)
    c: InternalAlignment(g1,g3)
    c: InternalAlignment(g2,g3)
    c: InternalAlignment(g4,g3)
    c: InternalAlignment(g5,g3)
    c: Block(g3)
    c: Coincident(g6,g0)
    c: Coincident(g6,g3)
    c: Horizontal(g6)
FEATURE [Part::Extrusion] Extrude014  label="caseScrewPillarBracket002"
  Base = -> Sketch020
  Dir = (0,0,1)
  DirMode = 2
  FaceMakerClass = Part::FaceMakerBullseye
  LengthFwd = 2.4
  LengthRev = 0
  Placement = pos=(13.7,29,13.26) rot=(0,-1,0;1.5708rad)
  Solid = true
  Symmetric = false
FEATURE [Sketcher::SketchObject] Sketch021
  FullyConstrained = true
  sketch-geometry (7):
    g0: LineSegment StartX=0 StartY=0 StartZ=0 EndX=0 EndY=6 EndZ=0
    g1: Circle CenterX=0 CenterY=0 CenterZ=0 NormalX=0 NormalY=0 NormalZ=1 AngleXU=0 Radius=1
    g2: Circle CenterX=8 CenterY=6 CenterZ=0 NormalX=0 NormalY=0 NormalZ=1 AngleXU=0 Radius=1
    g3: BSplineCurve PolesCount=3 KnotsCount=2 Degree=2 IsPeriodic=0
    g4: GeomPoint X=0 Y=0 Z=0
    g5: GeomPoint X=8 Y=6 Z=0
    g6: LineSegment StartX=0 StartY=6 StartZ=0 EndX=8 EndY=6 EndZ=0
  constraints (14):
    c: Coincident(g0,g-1)
    c: Distance(g0) = 6
    c: Vertical(g0)
    c: Coincident(g3,g0)
    c: Weight(g1) = 1
    c: Equal(g1,g2)
    c: InternalAlignment(g1,g3)
    c: InternalAlignment(g2,g3)
    c: InternalAlignment(g4,g3)
    c: InternalAlignment(g5,g3)
    c: Block(g3)
    c: Coincident(g6,g0)
    c: Coincident(g6,g3)
    c: Horizontal(g6)
FEATURE [Part::Extrusion] Extrude015  label="caseScrewPillarBracket003"
  Base = -> Sketch021
  Dir = (0,0,1)
  DirMode = 2
  FaceMakerClass = Part::FaceMakerBullseye
  LengthFwd = 2.4
  LengthRev = 0
  Placement = pos=(11.3,29,58.74) rot=(0,1,0;1.5708rad)
  Solid = true
  Symmetric = false
FEATURE [Sketcher::SketchObject] Sketch022
  FullyConstrained = true
  sketch-geometry (7):
    g0: LineSegment StartX=0 StartY=0 StartZ=0 EndX=0 EndY=6 EndZ=0
    g1: Circle CenterX=0 CenterY=0 CenterZ=0 NormalX=0 NormalY=0 NormalZ=1 AngleXU=0 Radius=1
    g2: Circle CenterX=8 CenterY=6 CenterZ=0 NormalX=0 NormalY=0 NormalZ=1 AngleXU=0 Radius=1
    g3: BSplineCurve PolesCount=3 KnotsCount=2 Degree=2 IsPeriodic=0
    g4: GeomPoint X=0 Y=0 Z=0
    g5: GeomPoint X=8 Y=6 Z=0
    g6: LineSegment StartX=0 StartY=6 StartZ=0 EndX=8 EndY=6 EndZ=0
  constraints (14):
    c: Coincident(g0,g-1)
    c: Distance(g0) = 6
    c: Vertical(g0)
    c: Coincident(g3,g0)
    c: Weight(g1) = 1
    c: Equal(g1,g2)
    c: InternalAlignment(g1,g3)
    c: InternalAlignment(g2,g3)
    c: InternalAlignment(g4,g3)
    c: InternalAlignment(g5,g3)
    c: Block(g3)
    c: Coincident(g6,g0)
    c: Coincident(g6,g3)
    c: Horizontal(g6)
FEATURE [Part::Extrusion] Extrude016  label="caseScrewPillarBracket004"
  Base = -> Sketch022
  Dir = (0,0,1)
  DirMode = 2
  FaceMakerClass = Part::FaceMakerBullseye
  LengthFwd = 2.4
  LengthRev = 0
  Placement = pos=(88.3,29,65.23) rot=(0,1,0;1.5708rad)
  Solid = true
  Symmetric = false
FEATURE [Sketcher::SketchObject] Sketch023
  FullyConstrained = true
  sketch-geometry (7):
    g0: LineSegment StartX=0 StartY=0 StartZ=0 EndX=0 EndY=6 EndZ=0
    g1: Circle CenterX=0 CenterY=0 CenterZ=0 NormalX=0 NormalY=0 NormalZ=1 AngleXU=0 Radius=1
    g2: Circle CenterX=8 CenterY=6 CenterZ=0 NormalX=0 NormalY=0 NormalZ=1 AngleXU=0 Radius=1
    g3: BSplineCurve PolesCount=3 KnotsCount=2 Degree=2 IsPeriodic=0
    g4: GeomPoint X=0 Y=0 Z=0
    g5: GeomPoint X=8 Y=6 Z=0
    g6: LineSegment StartX=0 StartY=6 StartZ=0 EndX=8 EndY=6 EndZ=0
  constraints (14):
    c: Coincident(g0,g-1)
    c: Distance(g0) = 6
    c: Vertical(g0)
    c: Coincident(g3,g0)
    c: Weight(g1) = 1
    c: Equal(g1,g2)
    c: InternalAlignment(g1,g3)
    c: InternalAlignment(g2,g3)
    c: InternalAlignment(g4,g3)
    c: InternalAlignment(g5,g3)
    c: Block(g3)
    c: Coincident(g6,g0)
    c: Coincident(g6,g3)
    c: Horizontal(g6)
FEATURE [Part::Extrusion] Extrude017  label="caseScrewPillarBracket005"
  Base = -> Sketch023
  Dir = (0,0,1)
  DirMode = 2
  FaceMakerClass = Part::FaceMakerBullseye
  LengthFwd = 2.4
  LengthRev = 0
  Placement = pos=(90.7,29,6.77) rot=(0,-1,0;1.5708rad)
  Solid = true
  Symmetric = false
FEATURE [Sketcher::SketchObject] Sketch024
  FullyConstrained = true
  sketch-geometry (7):
    g0: LineSegment StartX=0 StartY=0 StartZ=0 EndX=0 EndY=6 EndZ=0
    g1: Circle CenterX=0 CenterY=0 CenterZ=0 NormalX=0 NormalY=0 NormalZ=1 AngleXU=0 Radius=1
    g2: Circle CenterX=8 CenterY=6 CenterZ=0 NormalX=0 NormalY=0 NormalZ=1 AngleXU=0 Radius=1
    g3: BSplineCurve PolesCount=3 KnotsCount=2 Degree=2 IsPeriodic=0
    g4: GeomPoint X=0 Y=0 Z=0
    g5: GeomPoint X=8 Y=6 Z=0
    g6: LineSegment StartX=0 StartY=6 StartZ=0 EndX=8 EndY=6 EndZ=0
  constraints (14):
    c: Coincident(g0,g-1)
    c: Distance(g0) = 6
    c: Vertical(g0)
    c: Coincident(g3,g0)
    c: Weight(g1) = 1
    c: Equal(g1,g2)
    c: InternalAlignment(g1,g3)
    c: InternalAlignment(g2,g3)
    c: InternalAlignment(g4,g3)
    c: InternalAlignment(g5,g3)
    c: Block(g3)
    c: Coincident(g6,g0)
    c: Coincident(g6,g3)
    c: Horizontal(g6)
FEATURE [Part::Extrusion] Extrude018  label="caseScrewPillarBracket006"
  Base = -> Sketch024
  Dir = (0,0,1)
  DirMode = 2
  FaceMakerClass = Part::FaceMakerBullseye
  LengthFwd = 2.4
  LengthRev = 0
  Placement = pos=(103.7,29,6.77) rot=(0,-1,0;1.5708rad)
  Solid = true
  Symmetric = false
FEATURE [Sketcher::SketchObject] Sketch025
  FullyConstrained = true
  sketch-geometry (7):
    g0: LineSegment StartX=0 StartY=0 StartZ=0 EndX=0 EndY=6 EndZ=0
    g1: Circle CenterX=0 CenterY=0 CenterZ=0 NormalX=0 NormalY=0 NormalZ=1 AngleXU=0 Radius=1
    g2: Circle CenterX=8 CenterY=6 CenterZ=0 NormalX=0 NormalY=0 NormalZ=1 AngleXU=0 Radius=1
    g3: BSplineCurve PolesCount=3 KnotsCount=2 Degree=2 IsPeriodic=0
    g4: GeomPoint X=0 Y=0 Z=0
    g5: GeomPoint X=8 Y=6 Z=0
    g6: LineSegment StartX=0 StartY=6 StartZ=0 EndX=8 EndY=6 EndZ=0
  constraints (14):
    c: Coincident(g0,g-1)
    c: Distance(g0) = 6
    c: Vertical(g0)
    c: Coincident(g3,g0)
    c: Weight(g1) = 1
    c: Equal(g1,g2)
    c: InternalAlignment(g1,g3)
    c: InternalAlignment(g2,g3)
    c: InternalAlignment(g4,g3)
    c: InternalAlignment(g5,g3)
    c: Block(g3)
    c: Coincident(g6,g0)
    c: Coincident(g6,g3)
    c: Horizontal(g6)
FEATURE [Part::Extrusion] Extrude019  label="caseScrewPillarBracket007"
  Base = -> Sketch025
  Dir = (0,0,1)
  DirMode = 2
  FaceMakerClass = Part::FaceMakerBullseye
  LengthFwd = 2.4
  LengthRev = 0
  Placement = pos=(101.3,29,65.23) rot=(0,1,0;1.5708rad)
  Solid = true
  Symmetric = false
FEATURE [Part::Box] Box011  label="frontCaseScrewPillarBracket"
  AttacherType = Attacher::AttachEngine3D
  Height = 2.4
  Length = 16
  Placement = pos=(87,28,2.3) rot=(0,0,1;0rad)
  Width = 7
FEATURE [Part::Box] Box012  label="frontCaseScrewPillarBracket001"
  AttacherType = Attacher::AttachEngine3D
  Height = 2.4
  Length = 16
  Placement = pos=(87,28,67.3) rot=(0,0,1;0rad)
  Width = 7
FEATURE [Sketcher::SketchObject] Sketch026
  FullyConstrained = true
  sketch-geometry (17):
    g0: Circle CenterX=-3.5 CenterY=23.5 CenterZ=0 NormalX=0 NormalY=0 NormalZ=1 AngleXU=0 Radius=1
    g1: Circle CenterX=-1 CenterY=15.25 CenterZ=0 NormalX=0 NormalY=0 NormalZ=1 AngleXU=0 Radius=1
    g2: Circle CenterX=-3.5 CenterY=7 CenterZ=0 NormalX=0 NormalY=0 NormalZ=1 AngleXU=0 Radius=1
    g3: BSplineCurve PolesCount=3 KnotsCount=2 Degree=2 IsPeriodic=0
    g4: GeomPoint X=-3.5 Y=23.5 Z=0
    g5: GeomPoint X=-3.5 Y=7 Z=0
    g6: Circle CenterX=-4.8 CenterY=30.5 CenterZ=0 NormalX=0 NormalY=0 NormalZ=1 AngleXU=0 Radius=1
    g7: Circle CenterX=-3.5 CenterY=30.5 CenterZ=0 NormalX=0 NormalY=0 NormalZ=1 AngleXU=0 Radius=1
    g8: Circle CenterX=-3.5 CenterY=29.2 CenterZ=0 NormalX=0 NormalY=0 NormalZ=1 AngleXU=0 Radius=1
    g9: BSplineCurve PolesCount=3 KnotsCount=2 Degree=2 IsPeriodic=0
    g10: GeomPoint X=-4.8 Y=30.5 Z=0
    g11: GeomPoint X=-3.5 Y=29.2 Z=0
    g12: LineSegment StartX=-3.5 StartY=29.2 StartZ=0 EndX=-3.5 EndY=23.5 EndZ=0
    g13: LineSegment StartX=-4.8 StartY=30.5 StartZ=0 EndX=0 EndY=30.5 EndZ=0
    g14: LineSegment StartX=-3.5 StartY=5 StartZ=0 EndX=-3.5 EndY=7 EndZ=0
    g15: LineSegment StartX=0 StartY=5 StartZ=0 EndX=0 EndY=30.5 EndZ=0
    g16: LineSegment StartX=-3.5 StartY=5 StartZ=0 EndX=0 EndY=5 EndZ=0
  constraints (33):
    c: Weight(g0) = 1
    c: Equal(g0,g1)
    c: Equal(g0,g2)
    c: InternalAlignment(g0,g3)
    c: InternalAlignment(g1,g3)
    c: InternalAlignment(g2,g3)
    c: InternalAlignment(g4,g3)
    c: InternalAlignment(g5,g3)
    c: Block(g3)
    c: Weight(g6) = 1
    c: Equal(g6,g7)
    c: Equal(g6,g8)
    c: InternalAlignment(g6,g9)
    c: InternalAlignment(g7,g9)
    c: InternalAlignment(g8,g9)
    c: InternalAlignment(g10,g9)
    c: InternalAlignment(g11,g9)
    c: Block(g9)
    c: Coincident(g12,g9)
    c: Coincident(g12,g3)
    c: Vertical(g12)
    c: Coincident(g13,g9)
    c: Horizontal(g13)
    c: Distance(g13) = 4.8
    c: Coincident(g14,g3)
    c: Vertical(g14)
    c: Coincident(g15,g13)
    c: Vertical(g15)
    c: Tangent(g15,g1)
    c: Distance(g14) = 2
    c: Coincident(g16,g14)
    c: Horizontal(g16)
    c: Coincident(g15,g16)
FEATURE [Part::Feature] Face050
  shape: bbox 4.8 x 25.5 x 2e-07 mm, 1 faces, 0 solids (baked)
FEATURE [Part::Revolution] Revolve054  label="moreFrontCaseScrewPost001"
  Angle = 360
  Axis = (0,1,0)
  Base = (0,0,0)
  FaceMakerClass = Part::FaceMakerBullseye
  Placement = pos=(102.5,4.5,3.5) rot=(0,0,1;0rad)
  Solid = false
  Source = -> Face050
  Symmetric = false
FEATURE [Part::Feature] Face051
  shape: bbox 4.8 x 25.5 x 2e-07 mm, 1 faces, 0 solids (baked)
FEATURE [Part::Revolution] Revolve055  label="moreFrontCaseScrewPost002"
  Angle = 360
  Axis = (0,1,0)
  Base = (0,0,0)
  FaceMakerClass = Part::FaceMakerBullseye
  Placement = pos=(102.5,4.5,68.5) rot=(0,0,1;0rad)
  Solid = false
  Source = -> Face051
  Symmetric = false
FEATURE [Sketcher::SketchObject] Sketch027
  FullyConstrained = true
  sketch-geometry (10):
    g0: LineSegment StartX=-1.6 StartY=4.7 StartZ=0 EndX=-1.6 EndY=1.7 EndZ=0
    g1: LineSegment StartX=-3.5 StartY=4.7 StartZ=0 EndX=-1.6 EndY=4.7 EndZ=0
    g2: LineSegment StartX=-1.6 StartY=1.7 StartZ=0 EndX=-1.6 EndY=1.5 EndZ=0
    g3: LineSegment StartX=-1.6 StartY=1.5 StartZ=0 EndX=-5.2 EndY=1.5 EndZ=0
    g4: Circle CenterX=-3.5 CenterY=4.7 CenterZ=0 NormalX=0 NormalY=0 NormalZ=1 AngleXU=0 Radius=1
    g5: Circle CenterX=-3.59627 CenterY=2.99743 CenterZ=0 NormalX=0 NormalY=0 NormalZ=1 AngleXU=0 Radius=1
    g6: Circle CenterX=-5.2 CenterY=1.5 CenterZ=0 NormalX=0 NormalY=0 NormalZ=1 AngleXU=0 Radius=1
    g7: BSplineCurve PolesCount=3 KnotsCount=2 Degree=2 IsPeriodic=0
    g8: GeomPoint X=-3.5 Y=4.7 Z=0
    g9: GeomPoint X=-5.2 Y=1.5 Z=0
  constraints (23):
    c: Vertical(g0)
    c: Distance(g0) = 3
    c: Coincident(g1,g0)
    c: Horizontal(g1)
    c: Block(g0)
    c: Block(g1)
    c: Coincident(g2,g0)
    c: Vertical(g2)
    c: Distance(g2) = 0.2
    c: Coincident(g3,g2)
    c: Horizontal(g3)
    c: Block(g3)
    c: Coincident(g7,g1)
    c: Weight(g4) = 1
    c: Equal(g4,g5)
    c: Equal(g4,g6)
    c: Coincident(g7,g3)
    c: InternalAlignment(g4,g7)
    c: InternalAlignment(g5,g7)
    c: InternalAlignment(g6,g7)
    c: InternalAlignment(g8,g7)
    c: InternalAlignment(g9,g7)
    c: Block(g7)
FEATURE [Sketcher::SketchObject] Sketch028
  FullyConstrained = true
  sketch-geometry (18):
    g0: LineSegment StartX=0 StartY=3e-16 StartZ=0 EndX=0 EndY=1.7 EndZ=0
    g1: LineSegment StartX=-3.5 StartY=0 StartZ=0 EndX=-3.5 EndY=0.9 EndZ=0
    g2: Circle CenterX=-2.7 CenterY=1.7 CenterZ=0 NormalX=0 NormalY=0 NormalZ=1 AngleXU=0 Radius=1
    g3: Circle CenterX=-3.5 CenterY=1.7 CenterZ=0 NormalX=0 NormalY=0 NormalZ=1 AngleXU=0 Radius=1
    g4: Circle CenterX=-3.5 CenterY=0.9 CenterZ=0 NormalX=0 NormalY=0 NormalZ=1 AngleXU=0 Radius=1
    g5: BSplineCurve PolesCount=3 KnotsCount=2 Degree=2 IsPeriodic=0
    g6: GeomPoint X=-2.7 Y=1.7 Z=0
    g7: GeomPoint X=-3.5 Y=0.9 Z=0
    g8: LineSegment StartX=-3.5 StartY=0 StartZ=0 EndX=-3.5 EndY=-7 EndZ=0
    g9: LineSegment StartX=0 StartY=3e-16 StartZ=0 EndX=0 EndY=-7 EndZ=0
    g10: LineSegment StartX=-3.5 StartY=-7 StartZ=0 EndX=0 EndY=-7 EndZ=0
    g11: LineSegment StartX=-2.7 StartY=1.7 StartZ=0 EndX=-1.6 EndY=1.7 EndZ=0
    g12: LineSegment StartX=0 StartY=1.7 StartZ=0 EndX=0 EndY=4.5 EndZ=0
    g13: LineSegment StartX=0 StartY=4.5 StartZ=0 EndX=0 EndY=10.8 EndZ=0
    g14: LineSegment StartX=0 StartY=10.8 StartZ=0 EndX=-2 EndY=10.8 EndZ=0
    g15: LineSegment StartX=-1.6 StartY=4.7 StartZ=0 EndX=-1.6 EndY=1.7 EndZ=0
    g16: LineSegment StartX=-1.6 StartY=4.7 StartZ=0 EndX=-2 EndY=4.7 EndZ=0
    g17: LineSegment StartX=-2 StartY=4.7 StartZ=0 EndX=-2 EndY=10.8 EndZ=0
  constraints (44):
    c: Vertical(g0)
    c: Vertical(g1)
    c: Distance(g1) = 0.9
    c: Block(g0)
    c: Distance(g0) = 1.7
    c: Weight(g2) = 1
    c: Equal(g2,g3)
    c: Equal(g2,g4)
    c: Coincident(g5,g1)
    c: InternalAlignment(g2,g5)
    c: InternalAlignment(g3,g5)
    c: InternalAlignment(g4,g5)
    c: InternalAlignment(g6,g5)
    c: InternalAlignment(g7,g5)
    c: Block(g5)
    c: Coincident(g8,g1)
    c: Vertical(g8)
    c: Distance(g8) = 7
    c: Vertical(g9)
    c: Equal(g8,g9) = 7
    c: Coincident(g9,g0)
    c: Coincident(g10,g8)
    c: Coincident(g10,g9)
    c: Horizontal(g10)
    c: Coincident(g11,g5)
    c: Horizontal(g11)
    c: Coincident(g12,g0)
    c: Vertical(g12)
    c: Distance(g12) = 2.8
    c: Coincident(g13,g12)
    c: Vertical(g13)
    c: Distance(g13) = 6.3
    c: Coincident(g14,g13)
    c: Horizontal(g14)
    c: Distance(g14) = 2
    c: Vertical(g15)
    c: Distance(g15) = 3
    c: Block(g11)
    c: Coincident(g15,g11)
    c: Coincident(g16,g15)
    c: Horizontal(g16)
    c: Coincident(g17,g16)
    c: Coincident(g17,g14)
    c: Vertical(g17)
FEATURE [Part::Revolution] Revolve040  label="backCaseScrewRetainer001"
  Angle = 360
  Axis = (0,1,0)
  Base = (0,0,0)
  FaceMakerClass = Part::FaceMakerBullseye
  Placement = pos=(12.5,3,10) rot=(0,0,1;0rad)
  Solid = false
  Source = -> Face036
  Symmetric = false
FEATURE [Part::Feature] Face055
  shape: bbox 3.5 x 30.2 x 2e-07 mm, 1 faces, 0 solids (baked)
FEATURE [Part::Revolution] Revolve059  label="backCaseScrewPost"
  Angle = 360
  Axis = (0,1,0)
  Base = (0,0,0)
  FaceMakerClass = Part::FaceMakerBullseye
  Placement = pos=(12.5,4.5,10) rot=(0,0,1;0rad)
  Solid = false
  Source = -> Face055
  Symmetric = false
FEATURE [Part::Feature] Face056
  shape: bbox 3.5 x 30.2 x 2e-07 mm, 1 faces, 0 solids (baked)
FEATURE [Part::Revolution] Revolve060  label="backCaseScrewPost001"
  Angle = 360
  Axis = (0,1,0)
  Base = (0,0,0)
  FaceMakerClass = Part::FaceMakerBullseye
  Placement = pos=(12.5,4.5,62) rot=(0,0,1;0rad)
  Solid = false
  Source = -> Face056
  Symmetric = false
FEATURE [Part::Feature] Face057
  shape: bbox 3.5 x 17.8 x 2e-07 mm, 1 faces, 0 solids (baked)
FEATURE [Part::Revolution] Revolve061  label="removeToCreateScrewAndThreadedInsertHole"
  Angle = 360
  Axis = (0,1,0)
  Base = (0,0,0)
  FaceMakerClass = Part::FaceMakerBullseye
  Placement = pos=(12.5,0,10) rot=(0,0,1;0rad)
  Solid = false
  Source = -> Face057
  Symmetric = false
FEATURE [Part::Feature] Face058
  shape: bbox 3.5 x 17.8 x 2e-07 mm, 1 faces, 0 solids (baked)
FEATURE [Part::Revolution] Revolve062  label="removeToCreateScrewAndThreadedInsertHole001"
  Angle = 360
  Axis = (0,1,0)
  Base = (0,0,0)
  FaceMakerClass = Part::FaceMakerBullseye
  Placement = pos=(12.5,0,62) rot=(0,0,1;0rad)
  Solid = false
  Source = -> Face058
  Symmetric = false
FEATURE [Part::Feature] Face059
  shape: bbox 3.5 x 17.8 x 2e-07 mm, 1 faces, 0 solids (baked)
FEATURE [Part::Revolution] Revolve063  label="removeToCreateScrewAndThreadedInsertHole002"
  Angle = 360
  Axis = (0,1,0)
  Base = (0,0,0)
  FaceMakerClass = Part::FaceMakerBullseye
  Placement = pos=(89.5,0,68.5) rot=(0,0,1;0rad)
  Solid = false
  Source = -> Face059
  Symmetric = false
FEATURE [Part::Feature] Face060
  shape: bbox 3.5 x 17.8 x 2e-07 mm, 1 faces, 0 solids (baked)
FEATURE [Part::Revolution] Revolve064  label="removeToCreateScrewAndThreadedInsertHole003"
  Angle = 360
  Axis = (0,1,0)
  Base = (0,0,0)
  FaceMakerClass = Part::FaceMakerBullseye
  Placement = pos=(89.5,0,3.5) rot=(0,0,1;0rad)
  Solid = false
  Source = -> Face060
  Symmetric = false
FEATURE [Part::Feature] Face061
  shape: bbox 3.5 x 17.8 x 2e-07 mm, 1 faces, 0 solids (baked)
FEATURE [Part::Revolution] Revolve065  label="removeToCreateScrewAndThreadedInsertHole004"
  Angle = 360
  Axis = (0,1,0)
  Base = (0,0,0)
  FaceMakerClass = Part::FaceMakerBullseye
  Placement = pos=(102.5,4.7,3.5) rot=(0,0,1;0rad)
  Solid = false
  Source = -> Face061
  Symmetric = false
FEATURE [Part::Feature] Face062
  shape: bbox 3.5 x 17.8 x 2e-07 mm, 1 faces, 0 solids (baked)
FEATURE [Part::Revolution] Revolve066  label="removeToCreateScrewAndThreadedInsertHole005"
  Angle = 360
  Axis = (0,1,0)
  Base = (0,0,0)
  FaceMakerClass = Part::FaceMakerBullseye
  Placement = pos=(102.5,4.7,68.5) rot=(0,0,1;0rad)
  Solid = false
  Source = -> Face062
  Symmetric = false
FEATURE [Part::MultiFuse] Fusion047  label="makeHoles"
  Shapes = -> [Revolve066,Revolve065,Revolve064,Revolve063,Revolve062,Revolve061]
FEATURE [Part::Feature] Face063
  shape: bbox 3.6 x 3.2 x 2e-07 mm, 1 faces, 0 solids (baked)
FEATURE [Part::Revolution] Revolve067  label="moreFrontCaseScrewRetainer002"
  Angle = 360
  Axis = (0,1,0)
  Base = (0,0,0)
  FaceMakerClass = Part::FaceMakerBullseye
  Placement = pos=(102.5,4.5,68.5) rot=(0,0,1;0rad)
  Solid = false
  Source = -> Face063
  Symmetric = false
FEATURE [Part::Feature] Face064
  shape: bbox 3.6 x 3.2 x 2e-07 mm, 1 faces, 0 solids (baked)
FEATURE [Part::Revolution] Revolve068  label="moreFrontCaseScrewRetainer003"
  Angle = 360
  Axis = (0,1,0)
  Base = (0,0,0)
  FaceMakerClass = Part::FaceMakerBullseye
  Placement = pos=(102.5,4.5,3.5) rot=(0,0,1;0rad)
  Solid = false
  Source = -> Face064
  Symmetric = false
FEATURE [Part::Feature] Face065
  shape: bbox 3.5 x 17.8 x 2e-07 mm, 1 faces, 0 solids (baked)
FEATURE [Part::Revolution] Revolve069  label="removeToCreateScrewAndThreadedInsertHole006"
  Angle = 360
  Axis = (0,1,0)
  Base = (0,0,0)
  FaceMakerClass = Part::FaceMakerBullseye
  Placement = pos=(12.5,0,10) rot=(0,0,1;0rad)
  Solid = false
  Source = -> Face065
  Symmetric = false
FEATURE [Part::Feature] Face066
  shape: bbox 3.5 x 17.8 x 2e-07 mm, 1 faces, 0 solids (baked)
FEATURE [Part::Revolution] Revolve070  label="removeToCreateScrewAndThreadedInsertHole007"
  Angle = 360
  Axis = (0,1,0)
  Base = (0,0,0)
  FaceMakerClass = Part::FaceMakerBullseye
  Placement = pos=(12.5,0,62) rot=(0,0,1;0rad)
  Solid = false
  Source = -> Face066
  Symmetric = false
FEATURE [Part::Feature] Face067
  shape: bbox 3.5 x 17.8 x 2e-07 mm, 1 faces, 0 solids (baked)
FEATURE [Part::Revolution] Revolve071  label="removeToCreateScrewAndThreadedInsertHole008"
  Angle = 360
  Axis = (0,1,0)
  Base = (0,0,0)
  FaceMakerClass = Part::FaceMakerBullseye
  Placement = pos=(89.5,0,68.5) rot=(0,0,1;0rad)
  Solid = false
  Source = -> Face067
  Symmetric = false
FEATURE [Part::Feature] Face068
  shape: bbox 3.5 x 17.8 x 2e-07 mm, 1 faces, 0 solids (baked)
FEATURE [Part::Revolution] Revolve072  label="removeToCreateScrewAndThreadedInsertHole009"
  Angle = 360
  Axis = (0,1,0)
  Base = (0,0,0)
  FaceMakerClass = Part::FaceMakerBullseye
  Placement = pos=(89.5,0,3.5) rot=(0,0,1;0rad)
  Solid = false
  Source = -> Face068
  Symmetric = false
FEATURE [Part::Feature] Face069
  shape: bbox 3.5 x 17.8 x 2e-07 mm, 1 faces, 0 solids (baked)
FEATURE [Part::Feature] Face070
  shape: bbox 3.5 x 17.8 x 2e-07 mm, 1 faces, 0 solids (baked)
FEATURE [Part::Revolution] Revolve073  label="removeToCreateScrewAndThreadedInsertHole010"
  Angle = 360
  Axis = (0,1,0)
  Base = (0,0,0)
  FaceMakerClass = Part::FaceMakerBullseye
  Placement = pos=(102.5,4.7,3.5) rot=(0,0,1;0rad)
  Solid = false
  Source = -> Face069
  Symmetric = false
FEATURE [Part::Revolution] Revolve074  label="removeToCreateScrewAndThreadedInsertHole011"
  Angle = 360
  Axis = (0,1,0)
  Base = (0,0,0)
  FaceMakerClass = Part::FaceMakerBullseye
  Placement = pos=(102.5,4.7,68.5) rot=(0,0,1;0rad)
  Solid = false
  Source = -> Face070
  Symmetric = false
FEATURE [Part::MultiFuse] Fusion048  label="makeHoles001"
  Shapes = -> [Revolve074,Revolve073,Revolve072,Revolve071,Revolve070,Revolve069]
FEATURE [Part::MultiFuse] Fusion049  label="caseScrewRetainers"
  Shapes = -> [Revolve067,Revolve068,Revolve048,Revolve047,Revolve039,Revolve040]
FEATURE [Part::Cut] Cut015  label="caseScrewRetainers001"
  Base = -> Fusion049
  Tool = -> Fusion048
FEATURE [Part::MultiFuse] Fusion050  label="casePillars"
  Shapes = -> [Revolve055,Revolve054,Revolve043,Revolve046,Revolve059,Revolve060]
FEATURE [Part::Feature] Face071 .. Face076  x6 (patterned run collapsed; names and placements below)
  shape: bbox 3.5 x 17.8 x 2e-07 mm, 1 faces, 0 solids (baked)
FEATURE [Part::Revolution] Revolve075  label="removeToCreateScrewAndThreadedInsertHole012"
  Angle = 360
  Axis = (0,1,0)
  Base = (0,0,0)
  FaceMakerClass = Part::FaceMakerBullseye
  Placement = pos=(12.5,0,10) rot=(0,0,1;0rad)
  Solid = false
  Source = -> Face071
  Symmetric = false
FEATURE [Part::Revolution] Revolve076  label="removeToCreateScrewAndThreadedInsertHole013"
  Angle = 360
  Axis = (0,1,0)
  Base = (0,0,0)
  FaceMakerClass = Part::FaceMakerBullseye
  Placement = pos=(12.5,0,62) rot=(0,0,1;0rad)
  Solid = false
  Source = -> Face072
  Symmetric = false
FEATURE [Part::Revolution] Revolve077  label="removeToCreateScrewAndThreadedInsertHole014"
  Angle = 360
  Axis = (0,1,0)
  Base = (0,0,0)
  FaceMakerClass = Part::FaceMakerBullseye
  Placement = pos=(89.5,0,68.5) rot=(0,0,1;0rad)
  Solid = false
  Source = -> Face073
  Symmetric = false
FEATURE [Part::Revolution] Revolve078  label="removeToCreateScrewAndThreadedInsertHole015"
  Angle = 360
  Axis = (0,1,0)
  Base = (0,0,0)
  FaceMakerClass = Part::FaceMakerBullseye
  Placement = pos=(89.5,0,3.5) rot=(0,0,1;0rad)
  Solid = false
  Source = -> Face074
  Symmetric = false
FEATURE [Part::Revolution] Revolve079  label="removeToCreateScrewAndThreadedInsertHole016"
  Angle = 360
  Axis = (0,1,0)
  Base = (0,0,0)
  FaceMakerClass = Part::FaceMakerBullseye
  Placement = pos=(102.5,4.7,3.5) rot=(0,0,1;0rad)
  Solid = false
  Source = -> Face075
  Symmetric = false
FEATURE [Part::Revolution] Revolve080  label="removeToCreateScrewAndThreadedInsertHole017"
  Angle = 360
  Axis = (0,1,0)
  Base = (0,0,0)
  FaceMakerClass = Part::FaceMakerBullseye
  Placement = pos=(102.5,4.7,68.5) rot=(0,0,1;0rad)
  Solid = false
  Source = -> Face076
  Symmetric = false
FEATURE [Part::MultiFuse] Fusion051  label="makeHoles002"
  Shapes = -> [Revolve080,Revolve079,Revolve078,Revolve077,Revolve076,Revolve075]
FEATURE [Part::Cut] Cut016  label="caesPillars"
  Base = -> Fusion050
  Tool = -> Fusion051
FEATURE [Part::Revolution] Revolve009  label="plugHousing016"
  Angle = 360
  Axis = (0,1,0)
  Base = (0,0,0)
  FaceMakerClass = Part::FaceMakerBullseye
  Placement = pos=(0,0,36.15) rot=(0,0,1;0rad)
  Solid = false
  Source = -> Face012
  Symmetric = false
FEATURE [Part::MultiFuse] Fusion014  label="plugHousing023"
  Placement = pos=(0,0,0) rot=(0,0,1;1.5708rad)
  Shapes = -> [Revolve011,Revolve009]
FEATURE [Part::Revolution] Revolve010  label="plugHousing017"
  Angle = 360
  Axis = (0,1,0)
  Base = (0,0,0)
  FaceMakerClass = Part::FaceMakerBullseye
  Placement = pos=(0,0,36.15) rot=(0,0,1;0rad)
  Solid = false
  Source = -> Face014
  Symmetric = false
FEATURE [Part::MultiFuse] Fusion015  label="plugHousing024"
  Placement = pos=(0,0,0) rot=(0,0,1;1.5708rad)
  Shapes = -> [Revolve010,Revolve015]
FEATURE [Part::Revolution] Revolve014  label="plugHousing026"
  Angle = 360
  Axis = (0,1,0)
  Base = (0,0,0)
  FaceMakerClass = Part::FaceMakerBullseye
  Placement = pos=(0,0,36.15) rot=(0,0,1;0rad)
  Solid = false
  Source = -> Face011
  Symmetric = false
FEATURE [Part::Revolution] Revolve013  label="plugHousing025"
  Angle = 360
  Axis = (0,1,0)
  Base = (0,0,0)
  FaceMakerClass = Part::FaceMakerBullseye
  Placement = pos=(0,0,36.15) rot=(0,0,1;0rad)
  Solid = false
  Source = -> Face015
  Symmetric = false
FEATURE [Part::MultiFuse] Fusion016  label="plugHousing028"
  Placement = pos=(0,19,0) rot=(0,0,1;3.14159rad)
  Shapes = -> [Fusion014,Fusion013]
FEATURE [Part::MultiFuse] Fusion011  label="plugHousing018"
  Placement = pos=(0,0,0) rot=(0,0,1;1.5708rad)
  Shapes = -> [Revolve014,Revolve013]
FEATURE [Part::MultiFuse] Fusion012  label="plugHousing019"
  Placement = pos=(0,19,0) rot=(0,0,1;3.14159rad)
  Shapes = -> [Fusion011,Fusion015]
FEATURE [Part::MultiFuse] Fusion017  label="plugHousing029"
  Placement = pos=(122.621,0,-0.15) rot=(0,0,1;0rad)
  Shapes = -> [Fusion016,Fusion012]
FEATURE [Part::MultiFuse] Fusion052  label="casePillarRetainers"
  Shapes = -> [Extrude012,Extrude013,Extrude014,Extrude015,Extrude016,Extrude017,Extrude018,Extrude019,Box011,Box012]
FEATURE [Part::Feature] Face077
  shape: bbox 3.5 x 17.8 x 2e-07 mm, 1 faces, 0 solids (baked)
FEATURE [Part::Revolution] Revolve081  label="removeToCreateScrewAndThreadedInsertHole018"
  Angle = 360
  Axis = (0,1,0)
  Base = (0,0,0)
  FaceMakerClass = Part::FaceMakerBullseye
  Placement = pos=(62.3,30.3,19.7) rot=(0,0,1;0rad)
  Solid = false
  Source = -> Face077
  Symmetric = false
FEATURE [Part::Feature] Face078
  shape: bbox 3.5 x 17.8 x 2e-07 mm, 1 faces, 0 solids (baked)
FEATURE [Part::Revolution] Revolve082  label="removeToCreateScrewAndThreadedInsertHole019"
  Angle = 360
  Axis = (0,1,0)
  Base = (0,0,0)
  FaceMakerClass = Part::FaceMakerBullseye
  Placement = pos=(62.3,30.3,51.7) rot=(0,0,1;0rad)
  Solid = false
  Source = -> Face078
  Symmetric = false
FEATURE [Part::Feature] Face079
  shape: bbox 3.5 x 17.8 x 2e-07 mm, 1 faces, 0 solids (baked)
FEATURE [Part::Revolution] Revolve083  label="removeToCreateScrewAndThreadedInsertHole020"
  Angle = 360
  Axis = (0,1,0)
  Base = (0,0,0)
  FaceMakerClass = Part::FaceMakerBullseye
  Placement = pos=(30.3,30.3,19.7) rot=(0,0,1;0rad)
  Solid = false
  Source = -> Face079
  Symmetric = false
FEATURE [Part::Feature] Face080
  shape: bbox 3.5 x 17.8 x 2e-07 mm, 1 faces, 0 solids (baked)
FEATURE [Part::Revolution] Revolve084  label="removeToCreateScrewAndThreadedInsertHole021"
  Angle = 360
  Axis = (0,1,0)
  Base = (0,0,0)
  FaceMakerClass = Part::FaceMakerBullseye
  Placement = pos=(30.3,30.3,51.7) rot=(0,0,1;0rad)
  Solid = false
  Source = -> Face080
  Symmetric = false
FEATURE [Part::MultiFuse] Fusion053  label="createThreadedInsertHolesForFan"
  Shapes = -> [Revolve081,Revolve082,Revolve083,Revolve084]
FEATURE [Part::Cut] Cut017  label="fanScrewHousing001"
  Base = -> Fusion046
  Tool = -> Fusion053
FEATURE [Part::Feature] Face081
  shape: bbox 3.5 x 17.8 x 2e-07 mm, 1 faces, 0 solids (baked)
FEATURE [Part::Revolution] Revolve085  label="removeToCreateScrewAndThreadedInsertHole022"
  Angle = 360
  Axis = (0,1,0)
  Base = (0,0,0)
  FaceMakerClass = Part::FaceMakerBullseye
  Placement = pos=(62.3,30.3,19.7) rot=(0,0,1;0rad)
  Solid = false
  Source = -> Face081
  Symmetric = false
FEATURE [Part::Feature] Face082
  shape: bbox 3.5 x 17.8 x 2e-07 mm, 1 faces, 0 solids (baked)
FEATURE [Part::Revolution] Revolve086  label="removeToCreateScrewAndThreadedInsertHole023"
  Angle = 360
  Axis = (0,1,0)
  Base = (0,0,0)
  FaceMakerClass = Part::FaceMakerBullseye
  Placement = pos=(62.3,30.3,51.7) rot=(0,0,1;0rad)
  Solid = false
  Source = -> Face082
  Symmetric = false
FEATURE [Part::Feature] Face083
  shape: bbox 3.5 x 17.8 x 2e-07 mm, 1 faces, 0 solids (baked)
FEATURE [Part::Revolution] Revolve087  label="removeToCreateScrewAndThreadedInsertHole024"
  Angle = 360
  Axis = (0,1,0)
  Base = (0,0,0)
  FaceMakerClass = Part::FaceMakerBullseye
  Placement = pos=(30.3,30.3,19.7) rot=(0,0,1;0rad)
  Solid = false
  Source = -> Face083
  Symmetric = false
FEATURE [Part::Feature] Face084
  shape: bbox 3.5 x 17.8 x 2e-07 mm, 1 faces, 0 solids (baked)
FEATURE [Part::Revolution] Revolve088  label="removeToCreateScrewAndThreadedInsertHole025"
  Angle = 360
  Axis = (0,1,0)
  Base = (0,0,0)
  FaceMakerClass = Part::FaceMakerBullseye
  Placement = pos=(30.3,30.3,51.7) rot=(0,0,1;0rad)
  Solid = false
  Source = -> Face084
  Symmetric = false
FEATURE [Part::MultiFuse] Fusion054  label="createThreadedInsertHolesForFan001"
  Shapes = -> [Revolve085,Revolve086,Revolve087,Revolve088]
FEATURE [Part::Cut] Cut018  label="top007"
  Base = -> Fusion040
  Tool = -> Fusion054
FEATURE [Sketcher::SketchObject] Sketch029
  FullyConstrained = false
  Placement = pos=(0,0,0) rot=(1,0,0;1.5708rad)
  sketch-geometry (24):
    g0: ArcOfCircle CenterX=-4 CenterY=-10.5 CenterZ=0 NormalX=0 NormalY=0 NormalZ=1 AngleXU=0 Radius=1.5 StartAngle=6e-16 EndAngle=3.14159
    g1: ArcOfCircle CenterX=-34.2 CenterY=-10.5 CenterZ=0 NormalX=0 NormalY=0 NormalZ=1 AngleXU=0 Radius=1.5 StartAngle=0 EndAngle=3.14159
    g2: ArcOfCircle CenterX=-34.2 CenterY=-27.7 CenterZ=0 NormalX=0 NormalY=0 NormalZ=1 AngleXU=0 Radius=1.5 StartAngle=3.14159 EndAngle=6.28319
    g3: ArcOfCircle CenterX=-4 CenterY=-27.7 CenterZ=0 NormalX=0 NormalY=0 NormalZ=1 AngleXU=0 Radius=1.5 StartAngle=3.1416 EndAngle=6.28319
    g4: ArcOfCircle CenterX=-10 CenterY=-4.3 CenterZ=0 NormalX=0 NormalY=0 NormalZ=1 AngleXU=0 Radius=1.5 StartAngle=2e-16 EndAngle=3.14159
    g5: ArcOfCircle CenterX=-16.1 CenterY=-1.8 CenterZ=0 NormalX=0 NormalY=0 NormalZ=1 AngleXU=0 Radius=1.5 StartAngle=5e-16 EndAngle=3.14159
    g6: ArcOfCircle CenterX=-22.1 CenterY=-1.8 CenterZ=0 NormalX=0 NormalY=0 NormalZ=1 AngleXU=0 Radius=1.5 StartAngle=5e-16 EndAngle=3.14159
    g7: ArcOfCircle CenterX=-28.2 CenterY=-4.3 CenterZ=0 NormalX=0 NormalY=0 NormalZ=1 AngleXU=0 Radius=1.5 StartAngle=2e-16 EndAngle=3.14159
    g8: ArcOfCircle CenterX=-10 CenterY=-33.9 CenterZ=0 NormalX=0 NormalY=0 NormalZ=1 AngleXU=0 Radius=1.5 StartAngle=3.14159 EndAngle=6.28319
    g9: ArcOfCircle CenterX=-16.1 CenterY=-36.4 CenterZ=0 NormalX=0 NormalY=0 NormalZ=1 AngleXU=0 Radius=1.5 StartAngle=3.14159 EndAngle=6.28319
    g10: ArcOfCircle CenterX=-22.1 CenterY=-36.4 CenterZ=0 NormalX=0 NormalY=0 NormalZ=1 AngleXU=0 Radius=1.5 StartAngle=3.14159 EndAngle=6.28319
    g11: ArcOfCircle CenterX=-28.2 CenterY=-33.9 CenterZ=0 NormalX=0 NormalY=0 NormalZ=1 AngleXU=0 Radius=1.5 StartAngle=3.14159 EndAngle=6.28319
    g12: LineSegment StartX=-35.7 StartY=-10.5 StartZ=0 EndX=-35.7 EndY=-27.7 EndZ=0
    g13: LineSegment StartX=-32.7 StartY=-10.5 StartZ=0 EndX=-32.7 EndY=-27.7 EndZ=0
    g14: LineSegment StartX=-29.7 StartY=-33.9 StartZ=0 EndX=-29.7 EndY=-4.3 EndZ=0
    g15: LineSegment StartX=-26.7 StartY=-33.9 StartZ=0 EndX=-26.7 EndY=-4.3 EndZ=0
    g16: LineSegment StartX=-2.5 StartY=-10.5 StartZ=0 EndX=-2.5 EndY=-27.7 EndZ=0
    g17: LineSegment StartX=-8.5 StartY=-4.3 StartZ=0 EndX=-8.5 EndY=-33.9 EndZ=0
    g18: LineSegment StartX=-5.5 StartY=-10.5 StartZ=0 EndX=-5.5 EndY=-27.7 EndZ=0
    g19: LineSegment StartX=-11.5 StartY=-4.3 StartZ=0 EndX=-11.5 EndY=-33.9 EndZ=0
    g20: LineSegment StartX=-14.6 StartY=-1.8 StartZ=0 EndX=-14.6 EndY=-36.4 EndZ=0
    g21: LineSegment StartX=-17.6 StartY=-1.8 StartZ=0 EndX=-17.6 EndY=-36.4 EndZ=0
    g22: LineSegment StartX=-20.6 StartY=-36.4 StartZ=0 EndX=-20.6 EndY=-1.8 EndZ=0
    g23: LineSegment StartX=-23.6 StartY=-1.8 StartZ=0 EndX=-23.6 EndY=-36.4 EndZ=0
  constraints (48):
    c: Block(g0)
    c: Block(g1)
    c: Block(g2)
    c: Block(g3)
    c: Block(g4)
    c: Block(g5)
    c: Block(g6)
    c: Block(g7)
    c: Block(g8)
    c: Block(g9)
    c: Block(g10)
    c: Block(g11)
    c: Coincident(g12,g1)
    c: Coincident(g12,g2)
    c: Vertical(g12)
    c: Coincident(g13,g1)
    c: Coincident(g13,g2)
    c: Vertical(g13)
    c: Coincident(g14,g11)
    c: Coincident(g14,g7)
    c: Vertical(g14)
    c: Coincident(g15,g11)
    c: Coincident(g15,g7)
    c: Vertical(g15)
    c: Coincident(g16,g0)
    c: Coincident(g16,g3)
    c: Vertical(g16)
    c: Coincident(g17,g4)
    c: Coincident(g17,g8)
    c: Vertical(g17)
    c: Coincident(g18,g0)
    c: Coincident(g18,g3)
    c: Vertical(g18)
    c: Coincident(g19,g4)
    c: Coincident(g19,g8)
    c: Vertical(g19)
    c: Coincident(g20,g5)
    c: Coincident(g20,g9)
    c: Vertical(g20)
    c: Coincident(g21,g5)
    c: Coincident(g21,g9)
    c: Vertical(g21)
    c: Coincident(g22,g10)
    c: Coincident(g22,g6)
    c: Vertical(g22)
    c: Coincident(g23,g6)
    c: Coincident(g23,g10)
    c: Vertical(g23)
FEATURE [Part::Extrusion] Extrude020  label="removeToCreateFanGrillHoles"
  Base = -> Sketch029
  Dir = (0,-1,6e-16)
  DirMode = 2
  FaceMakerClass = Part::FaceMakerBullseye
  LengthFwd = 10
  LengthRev = 0
  Placement = pos=(65.4,44,54.82) rot=(0,0,1;0rad)
  Solid = true
  Symmetric = false
FEATURE [Part::MultiFuse] Fusion055  label="top008"
  Shapes = -> [Cut017,Cut018]
FEATURE [Part::Cut] Cut019  label="top009"
  Base = -> Fusion055
  Tool = -> Extrude020
FEATURE [App::MeasureDistance] Distance003  label="Distance: 71.95 mm"
  Distance = 71.9513
  P1 = (117,38,72)
  P2 = (117,38,0.0487319)
FEATURE [Sketcher::SketchObject] Sketch030
  FullyConstrained = true
  Placement = pos=(117,19,0) rot=(0.57735,0.57735,0.57735;2.0944rad)
  sketch-geometry (48):
    g0: LineSegment StartX=-49.19 StartY=69.25 StartZ=0 EndX=-49.19 EndY=66.25 EndZ=0
    g1: LineSegment StartX=-49.19 StartY=63.5 StartZ=0 EndX=-49.19 EndY=60.5 EndZ=0
    g2: LineSegment StartX=-49.19 StartY=57.75 StartZ=0 EndX=-49.19 EndY=54.75 EndZ=0
    g3: LineSegment StartX=-49.19 StartY=52 StartZ=0 EndX=-49.19 EndY=49 EndZ=0
    g4: LineSegment StartX=-49.19 StartY=46.25 StartZ=0 EndX=-49.19 EndY=43.25 EndZ=0
    g5: LineSegment StartX=-49.19 StartY=40.5 StartZ=0 EndX=-49.19 EndY=37.5 EndZ=0
    g6: LineSegment StartX=-49.19 StartY=34.5 StartZ=0 EndX=-49.19 EndY=31.5 EndZ=0
    g7: LineSegment StartX=-49.19 StartY=28.75 StartZ=0 EndX=-49.19 EndY=25.75 EndZ=0
    g8: LineSegment StartX=-49.19 StartY=23 StartZ=0 EndX=-49.19 EndY=20 EndZ=0
    g9: LineSegment StartX=-49.19 StartY=17.25 StartZ=0 EndX=-49.19 EndY=14.25 EndZ=0
    g10: LineSegment StartX=-49.19 StartY=11.5 StartZ=0 EndX=-49.19 EndY=8.5 EndZ=0
    g11: LineSegment StartX=-49.19 StartY=5.75 StartZ=0 EndX=-49.19 EndY=2.75 EndZ=0
    g12: ArcOfCircle CenterX=-1.5 CenterY=67.75 CenterZ=0 NormalX=0 NormalY=0 NormalZ=1 AngleXU=0 Radius=1.5 StartAngle=4.71239 EndAngle=7.85398
    g13: ArcOfCircle CenterX=-1.5 CenterY=62 CenterZ=0 NormalX=0 NormalY=0 NormalZ=1 AngleXU=0 Radius=1.5 StartAngle=4.71239 EndAngle=7.85398
    g14: ArcOfCircle CenterX=-1.5 CenterY=56.25 CenterZ=0 NormalX=0 NormalY=0 NormalZ=1 AngleXU=0 Radius=1.5 StartAngle=4.71239 EndAngle=7.85398
    g15: ArcOfCircle CenterX=-11.49 CenterY=50.5 CenterZ=0 NormalX=0 NormalY=0 NormalZ=1 AngleXU=0 Radius=1.5 StartAngle=4.71239 EndAngle=7.85398
    g16: ArcOfCircle CenterX=-16.28 CenterY=44.75 CenterZ=0 NormalX=0 NormalY=0 NormalZ=1 AngleXU=0 Radius=1.5 StartAngle=4.71239 EndAngle=7.85398
    g17: ArcOfCircle CenterX=-18.2337 CenterY=39 CenterZ=0 NormalX=0 NormalY=0 NormalZ=1 AngleXU=0 Radius=1.5 StartAngle=4.71485 EndAngle=7.85398
    g18: ArcOfCircle CenterX=-16.2837 CenterY=27.25 CenterZ=0 NormalX=0 NormalY=0 NormalZ=1 AngleXU=0 Radius=1.5 StartAngle=4.71485 EndAngle=7.85398
    g19: ArcOfCircle CenterX=-18.2337 CenterY=33 CenterZ=0 NormalX=0 NormalY=0 NormalZ=1 AngleXU=0 Radius=1.5 StartAngle=4.71485 EndAngle=7.85398
    g20: ArcOfCircle CenterX=-11.49 CenterY=21.5 CenterZ=0 NormalX=0 NormalY=0 NormalZ=1 AngleXU=0 Radius=1.5 StartAngle=4.71239 EndAngle=7.85398
    g21: ArcOfCircle CenterX=-1.5 CenterY=4.25 CenterZ=0 NormalX=0 NormalY=0 NormalZ=1 AngleXU=0 Radius=1.5 StartAngle=4.71239 EndAngle=7.85398
    g22: ArcOfCircle CenterX=-1.5 CenterY=10 CenterZ=0 NormalX=0 NormalY=0 NormalZ=1 AngleXU=0 Radius=1.5 StartAngle=4.71239 EndAngle=7.85398
    g23: ArcOfCircle CenterX=-1.5 CenterY=15.75 CenterZ=0 NormalX=0 NormalY=0 NormalZ=1 AngleXU=0 Radius=1.5 StartAngle=4.71239 EndAngle=7.85398
    g24: LineSegment StartX=-49.19 StartY=69.25 StartZ=0 EndX=-1.5 EndY=69.25 EndZ=0
    g25: LineSegment StartX=-49.19 StartY=66.25 StartZ=0 EndX=-1.5 EndY=66.25 EndZ=0
    g26: LineSegment StartX=-49.19 StartY=63.5 StartZ=0 EndX=-1.5 EndY=63.5 EndZ=0
    g27: LineSegment StartX=-49.19 StartY=60.5 StartZ=0 EndX=-1.5 EndY=60.5 EndZ=0
    g28: LineSegment StartX=-49.19 StartY=57.75 StartZ=0 EndX=-1.5 EndY=57.75 EndZ=0
    g29: LineSegment StartX=-49.19 StartY=54.75 StartZ=0 EndX=-1.5 EndY=54.75 EndZ=0
    g30: LineSegment StartX=-49.19 StartY=52 StartZ=0 EndX=-11.49 EndY=52 EndZ=0
    g31: LineSegment StartX=-49.19 StartY=49 StartZ=0 EndX=-11.49 EndY=49 EndZ=0
    g32: LineSegment StartX=-49.19 StartY=46.25 StartZ=0 EndX=-16.28 EndY=46.25 EndZ=0
    g33: LineSegment StartX=-49.19 StartY=43.25 StartZ=0 EndX=-16.28 EndY=43.25 EndZ=0
    g34: LineSegment StartX=-49.19 StartY=40.5 StartZ=0 EndX=-18.2337 EndY=40.5 EndZ=0
    g35: LineSegment StartX=-49.19 StartY=37.5 StartZ=0 EndX=-18.23 EndY=37.5 EndZ=0
    g36: LineSegment StartX=-49.19 StartY=34.5 StartZ=0 EndX=-18.2337 EndY=34.5 EndZ=0
    g37: LineSegment StartX=-49.19 StartY=31.5 StartZ=0 EndX=-18.23 EndY=31.5 EndZ=0
    g38: LineSegment StartX=-49.19 StartY=28.75 StartZ=0 EndX=-16.2837 EndY=28.75 EndZ=0
    g39: LineSegment StartX=-49.19 StartY=25.75 StartZ=0 EndX=-16.28 EndY=25.75 EndZ=0
    g40: LineSegment StartX=-49.19 StartY=23 StartZ=0 EndX=-11.49 EndY=23 EndZ=0
    g41: LineSegment StartX=-49.19 StartY=20 StartZ=0 EndX=-11.49 EndY=20 EndZ=0
    g42: LineSegment StartX=-49.19 StartY=17.25 StartZ=0 EndX=-1.5 EndY=17.25 EndZ=0
    g43: LineSegment StartX=-49.19 StartY=14.25 StartZ=0 EndX=-1.5 EndY=14.25 EndZ=0
    g44: LineSegment StartX=-49.19 StartY=11.5 StartZ=0 EndX=-1.5 EndY=11.5 EndZ=0
    g45: LineSegment StartX=-49.19 StartY=8.5 StartZ=0 EndX=-1.5 EndY=8.5 EndZ=0
    g46: LineSegment StartX=-49.19 StartY=5.75 StartZ=0 EndX=-1.5 EndY=5.75 EndZ=0
    g47: LineSegment StartX=-49.19 StartY=2.75 StartZ=0 EndX=-1.5 EndY=2.75 EndZ=0
  constraints (120):
    c: Vertical(g0)
    c: Distance(g0) = 3
    c: Block(g0)
    c: Vertical(g1)
    c: Distance(g1) = 3
    c: Vertical(g2)
    c: Equal(g0,g2) = 3
    c: Block(g2)
    c: Vertical(g3)
    c: Equal(g1,g3) = 3
    c: Vertical(g4)
    c: Equal(g0,g4) = 3
    c: Block(g4)
    c: Vertical(g5)
    c: Equal(g1,g5) = 3
    c: Vertical(g6)
    c: Equal(g0,g6) = 3
    c: Block(g6)
    c: Vertical(g7)
    c: Equal(g1,g7) = 3
    c: Vertical(g8)
    c: Equal(g0,g8) = 3
    c: Block(g8)
    c: Vertical(g9)
    c: Equal(g1,g9) = 3
    c: Vertical(g10)
    c: Equal(g0,g10) = 3
    c: Block(g10)
    c: Vertical(g11)
    c: Equal(g1,g11) = 3
    c: Block(g12)
    c: Block(g13)
    c: Block(g14)
    c: Block(g15)
    c: Block(g16)
    c: Block(g17)
    c: Block(g18)
    c: Block(g19)
    c: Block(g20)
    c: Block(g21)
    c: Block(g22)
    c: Block(g23)
    c: Block(g11)
    c: Block(g9)
    c: Block(g7)
    c: Block(g5)
    c: Block(g3)
    c: Block(g1)
    c: Coincident(g24,g0)
    c: Coincident(g24,g12)
    c: Horizontal(g24)
    c: Coincident(g25,g0)
    c: Coincident(g25,g12)
    c: Horizontal(g25)
    c: Coincident(g26,g1)
    c: Coincident(g26,g13)
    c: Horizontal(g26)
    c: Coincident(g27,g1)
    c: Coincident(g27,g13)
    c: Horizontal(g27)
    c: Coincident(g28,g2)
    c: Coincident(g28,g14)
    c: Horizontal(g28)
    c: Coincident(g29,g2)
    c: Coincident(g29,g14)
    c: Horizontal(g29)
    c: Coincident(g30,g3)
    c: Coincident(g30,g15)
    c: Horizontal(g30)
    c: Coincident(g31,g3)
    c: Coincident(g31,g15)
    c: Horizontal(g31)
    c: Coincident(g32,g4)
    c: Coincident(g32,g16)
    c: Horizontal(g32)
    c: Coincident(g33,g4)
    c: Coincident(g33,g16)
    c: Horizontal(g33)
    c: Coincident(g34,g5)
    c: Coincident(g34,g17)
    c: Horizontal(g34)
    c: Coincident(g35,g5)
    c: Coincident(g35,g17)
    c: Horizontal(g35)
    c: Coincident(g36,g6)
    c: Coincident(g36,g19)
    c: Horizontal(g36)
    c: Coincident(g37,g6)
    c: Coincident(g37,g19)
    c: Horizontal(g37)
    c: Coincident(g38,g7)
    c: Coincident(g38,g18)
    c: Horizontal(g38)
    c: Coincident(g39,g7)
    c: Coincident(g39,g18)
    c: Horizontal(g39)
    c: Coincident(g40,g8)
    c: Coincident(g40,g20)
    c: Horizontal(g40)
    c: Coincident(g41,g8)
    c: Coincident(g41,g20)
    c: Horizontal(g41)
    c: Coincident(g42,g9)
    c: Coincident(g42,g23)
    c: Horizontal(g42)
    c: Coincident(g43,g9)
    c: Coincident(g43,g23)
    c: Horizontal(g43)
    c: Coincident(g44,g10)
    c: Coincident(g44,g22)
    c: Horizontal(g44)
    c: Coincident(g45,g10)
    c: Coincident(g45,g22)
    c: Horizontal(g45)
    c: Coincident(g46,g11)
    c: Coincident(g46,g21)
    c: Horizontal(g46)
    c: Coincident(g47,g11)
    c: Coincident(g47,g21)
    c: Horizontal(g47)
FEATURE [Sketcher::SketchObject] Sketch031
  FullyConstrained = true
  Placement = pos=(117,19,0) rot=(0.57735,0.57735,0.57735;2.0944rad)
  sketch-geometry (24):
    g0: ArcOfCircle CenterX=-49.19 CenterY=67.75 CenterZ=0 NormalX=0 NormalY=0 NormalZ=1 AngleXU=0 Radius=1.5 StartAngle=1.5708 EndAngle=4.71239
    g1: ArcOfCircle CenterX=-49.19 CenterY=62 CenterZ=0 NormalX=0 NormalY=0 NormalZ=1 AngleXU=0 Radius=1.5 StartAngle=1.5708 EndAngle=4.71239
    g2: ArcOfCircle CenterX=-49.19 CenterY=56.25 CenterZ=0 NormalX=0 NormalY=0 NormalZ=1 AngleXU=0 Radius=1.5 StartAngle=1.5708 EndAngle=4.71239
    g3: ArcOfCircle CenterX=-49.19 CenterY=50.5 CenterZ=0 NormalX=0 NormalY=0 NormalZ=1 AngleXU=0 Radius=1.5 StartAngle=1.5708 EndAngle=4.71239
    g4: ArcOfCircle CenterX=-49.19 CenterY=44.75 CenterZ=0 NormalX=0 NormalY=0 NormalZ=1 AngleXU=0 Radius=1.5 StartAngle=1.5708 EndAngle=4.71239
    g5: ArcOfCircle CenterX=-49.19 CenterY=39 CenterZ=0 NormalX=0 NormalY=0 NormalZ=1 AngleXU=0 Radius=1.5 StartAngle=1.5708 EndAngle=4.71239
    g6: ArcOfCircle CenterX=-49.19 CenterY=33 CenterZ=0 NormalX=0 NormalY=0 NormalZ=1 AngleXU=0 Radius=1.5 StartAngle=1.5708 EndAngle=4.71239
    g7: ArcOfCircle CenterX=-49.19 CenterY=27.25 CenterZ=0 NormalX=0 NormalY=0 NormalZ=1 AngleXU=0 Radius=1.5 StartAngle=1.5708 EndAngle=4.71239
    g8: ArcOfCircle CenterX=-49.19 CenterY=21.5 CenterZ=0 NormalX=0 NormalY=0 NormalZ=1 AngleXU=0 Radius=1.5 StartAngle=1.5708 EndAngle=4.71239
    g9: ArcOfCircle CenterX=-49.19 CenterY=15.75 CenterZ=0 NormalX=0 NormalY=0 NormalZ=1 AngleXU=0 Radius=1.5 StartAngle=1.5708 EndAngle=4.71239
    g10: ArcOfCircle CenterX=-49.19 CenterY=10 CenterZ=0 NormalX=0 NormalY=0 NormalZ=1 AngleXU=0 Radius=1.5 StartAngle=1.5708 EndAngle=4.71239
    g11: ArcOfCircle CenterX=-49.19 CenterY=4.25 CenterZ=0 NormalX=0 NormalY=0 NormalZ=1 AngleXU=0 Radius=1.5 StartAngle=1.5708 EndAngle=4.71239
    g12: LineSegment StartX=-49.19 StartY=69.25 StartZ=0 EndX=-49.19 EndY=66.25 EndZ=0
    g13: LineSegment StartX=-49.19 StartY=63.5 StartZ=0 EndX=-49.19 EndY=60.5 EndZ=0
    g14: LineSegment StartX=-49.19 StartY=57.75 StartZ=0 EndX=-49.19 EndY=54.75 EndZ=0
    g15: LineSegment StartX=-49.19 StartY=52 StartZ=0 EndX=-49.19 EndY=49 EndZ=0
    g16: LineSegment StartX=-49.19 StartY=46.25 StartZ=0 EndX=-49.19 EndY=43.25 EndZ=0
    g17: LineSegment StartX=-49.19 StartY=40.5 StartZ=0 EndX=-49.19 EndY=37.5 EndZ=0
    g18: LineSegment StartX=-49.19 StartY=34.5 StartZ=0 EndX=-49.19 EndY=31.5 EndZ=0
    g19: LineSegment StartX=-49.19 StartY=28.75 StartZ=0 EndX=-49.19 EndY=25.75 EndZ=0
    g20: LineSegment StartX=-49.19 StartY=23 StartZ=0 EndX=-49.19 EndY=20 EndZ=0
    g21: LineSegment StartX=-49.19 StartY=17.25 StartZ=0 EndX=-49.19 EndY=14.25 EndZ=0
    g22: LineSegment StartX=-49.19 StartY=11.5 StartZ=0 EndX=-49.19 EndY=8.5 EndZ=0
    g23: LineSegment StartX=-49.19 StartY=5.75 StartZ=0 EndX=-49.19 EndY=2.75 EndZ=0
  constraints (48):
    c: Block(g0)
    c: Block(g1)
    c: Block(g2)
    c: Block(g3)
    c: Block(g4)
    c: Block(g5)
    c: Block(g6)
    c: Block(g7)
    c: Block(g8)
    c: Block(g9)
    c: Block(g10)
    c: Block(g11)
    c: Coincident(g12,g0)
    c: Coincident(g12,g0)
    c: Vertical(g12)
    c: Vertical(g13)
    c: Coincident(g13,g1)
    c: Vertical(g14)
    c: Coincident(g14,g2)
    c: Vertical(g15)
    c: Coincident(g15,g3)
    c: Vertical(g16)
    c: Coincident(g16,g4)
    c: Vertical(g17)
    c: Coincident(g17,g5)
    c: Vertical(g18)
    c: Coincident(g18,g6)
    c: Vertical(g19)
    c: Coincident(g19,g7)
    c: Vertical(g20)
    c: Coincident(g20,g8)
    c: Vertical(g21)
    c: Coincident(g21,g9)
    c: Vertical(g22)
    c: Coincident(g22,g10)
    c: Vertical(g23)
    c: Coincident(g23,g11)
    c: Block(g23)
    c: Block(g22)
    c: Block(g21)
    c: Block(g20)
    c: Block(g13)
    c: Block(g14)
    c: Block(g15)
    c: Block(g16)
    c: Block(g17)
    c: Block(g18)
    c: Block(g19)
FEATURE [Part::Extrusion] Extrude022
  Base = -> Sketch030
  Dir = (1,-2e-16,2e-16)
  DirMode = 2
  FaceMakerClass = Part::FaceMakerBullseye
  LengthFwd = 19
  LengthRev = 0
  Placement = pos=(-19,0,0) rot=(0,0,1;0rad)
  Solid = true
  Symmetric = false
FEATURE [Part::Fillet] Fillet022
  Base = -> Extrude022
  Edges = 24 edges r=1.49: [Edge6,Edge11,Edge18,Edge23,Edge30,Edge35,Edge42,Edge47,Edge54,Edge59,Edge66,Edge71,Edge78,Edge83,Edge90,Edge95,Edge102,Edge107,Edge114,Edge119,Edge126,Edge131,Edge138,Edge143]
FEATURE [Part::Cut] Cut020  label="top010"
  Base = -> Cut019
  Tool = -> Fillet022
FEATURE [Sketcher::SketchObject] Sketch032
  FullyConstrained = true
  Placement = pos=(117,19,0) rot=(0.57735,0.57735,0.57735;2.0944rad)
  sketch-geometry (48):
    g0: LineSegment StartX=-49.19 StartY=69.25 StartZ=0 EndX=-49.19 EndY=66.25 EndZ=0
    g1: LineSegment StartX=-49.19 StartY=63.5 StartZ=0 EndX=-49.19 EndY=60.5 EndZ=0
    g2: LineSegment StartX=-49.19 StartY=57.75 StartZ=0 EndX=-49.19 EndY=54.75 EndZ=0
    g3: LineSegment StartX=-49.19 StartY=52 StartZ=0 EndX=-49.19 EndY=49 EndZ=0
    g4: LineSegment StartX=-49.19 StartY=46.25 StartZ=0 EndX=-49.19 EndY=43.25 EndZ=0
    g5: LineSegment StartX=-49.19 StartY=40.5 StartZ=0 EndX=-49.19 EndY=37.5 EndZ=0
    g6: LineSegment StartX=-49.19 StartY=34.5 StartZ=0 EndX=-49.19 EndY=31.5 EndZ=0
    g7: LineSegment StartX=-49.19 StartY=28.75 StartZ=0 EndX=-49.19 EndY=25.75 EndZ=0
    g8: LineSegment StartX=-49.19 StartY=23 StartZ=0 EndX=-49.19 EndY=20 EndZ=0
    g9: LineSegment StartX=-49.19 StartY=17.25 StartZ=0 EndX=-49.19 EndY=14.25 EndZ=0
    g10: LineSegment StartX=-49.19 StartY=11.5 StartZ=0 EndX=-49.19 EndY=8.5 EndZ=0
    g11: LineSegment StartX=-49.19 StartY=5.75 StartZ=0 EndX=-49.19 EndY=2.75 EndZ=0
    g12: ArcOfCircle CenterX=-1.5 CenterY=67.75 CenterZ=0 NormalX=0 NormalY=0 NormalZ=1 AngleXU=0 Radius=1.5 StartAngle=4.71239 EndAngle=7.85398
    g13: ArcOfCircle CenterX=-1.5 CenterY=62 CenterZ=0 NormalX=0 NormalY=0 NormalZ=1 AngleXU=0 Radius=1.5 StartAngle=4.71239 EndAngle=7.85398
    g14: ArcOfCircle CenterX=-1.5 CenterY=56.25 CenterZ=0 NormalX=0 NormalY=0 NormalZ=1 AngleXU=0 Radius=1.5 StartAngle=4.71239 EndAngle=7.85398
    g15: ArcOfCircle CenterX=-11.49 CenterY=50.5 CenterZ=0 NormalX=0 NormalY=0 NormalZ=1 AngleXU=0 Radius=1.5 StartAngle=4.71239 EndAngle=7.85398
    g16: ArcOfCircle CenterX=-16.28 CenterY=44.75 CenterZ=0 NormalX=0 NormalY=0 NormalZ=1 AngleXU=0 Radius=1.5 StartAngle=4.71239 EndAngle=7.85398
    g17: ArcOfCircle CenterX=-18.2337 CenterY=39 CenterZ=0 NormalX=0 NormalY=0 NormalZ=1 AngleXU=0 Radius=1.5 StartAngle=4.71485 EndAngle=7.85398
    g18: ArcOfCircle CenterX=-16.2837 CenterY=27.25 CenterZ=0 NormalX=0 NormalY=0 NormalZ=1 AngleXU=0 Radius=1.5 StartAngle=4.71485 EndAngle=7.85398
    g19: ArcOfCircle CenterX=-18.2337 CenterY=33 CenterZ=0 NormalX=0 NormalY=0 NormalZ=1 AngleXU=0 Radius=1.5 StartAngle=4.71485 EndAngle=7.85398
    g20: ArcOfCircle CenterX=-11.49 CenterY=21.5 CenterZ=0 NormalX=0 NormalY=0 NormalZ=1 AngleXU=0 Radius=1.5 StartAngle=4.71239 EndAngle=7.85398
    g21: ArcOfCircle CenterX=-1.5 CenterY=4.25 CenterZ=0 NormalX=0 NormalY=0 NormalZ=1 AngleXU=0 Radius=1.5 StartAngle=4.71239 EndAngle=7.85398
    g22: ArcOfCircle CenterX=-1.5 CenterY=10 CenterZ=0 NormalX=0 NormalY=0 NormalZ=1 AngleXU=0 Radius=1.5 StartAngle=4.71239 EndAngle=7.85398
    g23: ArcOfCircle CenterX=-1.5 CenterY=15.75 CenterZ=0 NormalX=0 NormalY=0 NormalZ=1 AngleXU=0 Radius=1.5 StartAngle=4.71239 EndAngle=7.85398
    g24: LineSegment StartX=-49.19 StartY=69.25 StartZ=0 EndX=-1.5 EndY=69.25 EndZ=0
    g25: LineSegment StartX=-49.19 StartY=66.25 StartZ=0 EndX=-1.5 EndY=66.25 EndZ=0
    g26: LineSegment StartX=-49.19 StartY=63.5 StartZ=0 EndX=-1.5 EndY=63.5 EndZ=0
    g27: LineSegment StartX=-49.19 StartY=60.5 StartZ=0 EndX=-1.5 EndY=60.5 EndZ=0
    g28: LineSegment StartX=-49.19 StartY=57.75 StartZ=0 EndX=-1.5 EndY=57.75 EndZ=0
    g29: LineSegment StartX=-49.19 StartY=54.75 StartZ=0 EndX=-1.5 EndY=54.75 EndZ=0
    g30: LineSegment StartX=-49.19 StartY=52 StartZ=0 EndX=-11.49 EndY=52 EndZ=0
    g31: LineSegment StartX=-49.19 StartY=49 StartZ=0 EndX=-11.49 EndY=49 EndZ=0
    g32: LineSegment StartX=-49.19 StartY=46.25 StartZ=0 EndX=-16.28 EndY=46.25 EndZ=0
    g33: LineSegment StartX=-49.19 StartY=43.25 StartZ=0 EndX=-16.28 EndY=43.25 EndZ=0
    g34: LineSegment StartX=-49.19 StartY=40.5 StartZ=0 EndX=-18.2337 EndY=40.5 EndZ=0
    g35: LineSegment StartX=-49.19 StartY=37.5 StartZ=0 EndX=-18.23 EndY=37.5 EndZ=0
    g36: LineSegment StartX=-49.19 StartY=34.5 StartZ=0 EndX=-18.2337 EndY=34.5 EndZ=0
    g37: LineSegment StartX=-49.19 StartY=31.5 StartZ=0 EndX=-18.23 EndY=31.5 EndZ=0
    g38: LineSegment StartX=-49.19 StartY=28.75 StartZ=0 EndX=-16.2837 EndY=28.75 EndZ=0
    g39: LineSegment StartX=-49.19 StartY=25.75 StartZ=0 EndX=-16.28 EndY=25.75 EndZ=0
    g40: LineSegment StartX=-49.19 StartY=23 StartZ=0 EndX=-11.49 EndY=23 EndZ=0
    g41: LineSegment StartX=-49.19 StartY=20 StartZ=0 EndX=-11.49 EndY=20 EndZ=0
    g42: LineSegment StartX=-49.19 StartY=17.25 StartZ=0 EndX=-1.5 EndY=17.25 EndZ=0
    g43: LineSegment StartX=-49.19 StartY=14.25 StartZ=0 EndX=-1.5 EndY=14.25 EndZ=0
    g44: LineSegment StartX=-49.19 StartY=11.5 StartZ=0 EndX=-1.5 EndY=11.5 EndZ=0
    g45: LineSegment StartX=-49.19 StartY=8.5 StartZ=0 EndX=-1.5 EndY=8.5 EndZ=0
    g46: LineSegment StartX=-49.19 StartY=5.75 StartZ=0 EndX=-1.5 EndY=5.75 EndZ=0
    g47: LineSegment StartX=-49.19 StartY=2.75 StartZ=0 EndX=-1.5 EndY=2.75 EndZ=0
  constraints (120):
    c: Vertical(g0)
    c: Distance(g0) = 3
    c: Block(g0)
    c: Vertical(g1)
    c: Distance(g1) = 3
    c: Vertical(g2)
    c: Equal(g0,g2) = 3
    c: Block(g2)
    c: Vertical(g3)
    c: Equal(g1,g3) = 3
    c: Vertical(g4)
    c: Equal(g0,g4) = 3
    c: Block(g4)
    c: Vertical(g5)
    c: Equal(g1,g5) = 3
    c: Vertical(g6)
    c: Equal(g0,g6) = 3
    c: Block(g6)
    c: Vertical(g7)
    c: Equal(g1,g7) = 3
    c: Vertical(g8)
    c: Equal(g0,g8) = 3
    c: Block(g8)
    c: Vertical(g9)
    c: Equal(g1,g9) = 3
    c: Vertical(g10)
    c: Equal(g0,g10) = 3
    c: Block(g10)
    c: Vertical(g11)
    c: Equal(g1,g11) = 3
    c: Block(g12)
    c: Block(g13)
    c: Block(g14)
    c: Block(g15)
    c: Block(g16)
    c: Block(g17)
    c: Block(g18)
    c: Block(g19)
    c: Block(g20)
    c: Block(g21)
    c: Block(g22)
    c: Block(g23)
    c: Block(g11)
    c: Block(g9)
    c: Block(g7)
    c: Block(g5)
    c: Block(g3)
    c: Block(g1)
    c: Coincident(g24,g0)
    c: Coincident(g24,g12)
    c: Horizontal(g24)
    c: Coincident(g25,g0)
    c: Coincident(g25,g12)
    c: Horizontal(g25)
    c: Coincident(g26,g1)
    c: Coincident(g26,g13)
    c: Horizontal(g26)
    c: Coincident(g27,g1)
    c: Coincident(g27,g13)
    c: Horizontal(g27)
    c: Coincident(g28,g2)
    c: Coincident(g28,g14)
    c: Horizontal(g28)
    c: Coincident(g29,g2)
    c: Coincident(g29,g14)
    c: Horizontal(g29)
    c: Coincident(g30,g3)
    c: Coincident(g30,g15)
    c: Horizontal(g30)
    c: Coincident(g31,g3)
    c: Coincident(g31,g15)
    c: Horizontal(g31)
    c: Coincident(g32,g4)
    c: Coincident(g32,g16)
    c: Horizontal(g32)
    c: Coincident(g33,g4)
    c: Coincident(g33,g16)
    c: Horizontal(g33)
    c: Coincident(g34,g5)
    c: Coincident(g34,g17)
    c: Horizontal(g34)
    c: Coincident(g35,g5)
    c: Coincident(g35,g17)
    c: Horizontal(g35)
    c: Coincident(g36,g6)
    c: Coincident(g36,g19)
    c: Horizontal(g36)
    c: Coincident(g37,g6)
    c: Coincident(g37,g19)
    c: Horizontal(g37)
    c: Coincident(g38,g7)
    c: Coincident(g38,g18)
    c: Horizontal(g38)
    c: Coincident(g39,g7)
    c: Coincident(g39,g18)
    c: Horizontal(g39)
    c: Coincident(g40,g8)
    c: Coincident(g40,g20)
    c: Horizontal(g40)
    c: Coincident(g41,g8)
    c: Coincident(g41,g20)
    c: Horizontal(g41)
    c: Coincident(g42,g9)
    c: Coincident(g42,g23)
    c: Horizontal(g42)
    c: Coincident(g43,g9)
    c: Coincident(g43,g23)
    c: Horizontal(g43)
    c: Coincident(g44,g10)
    c: Coincident(g44,g22)
    c: Horizontal(g44)
    c: Coincident(g45,g10)
    c: Coincident(g45,g22)
    c: Horizontal(g45)
    c: Coincident(g46,g11)
    c: Coincident(g46,g21)
    c: Horizontal(g46)
    c: Coincident(g47,g11)
    c: Coincident(g47,g21)
    c: Horizontal(g47)
FEATURE [Part::Extrusion] Extrude023
  Base = -> Sketch032
  Dir = (1,-2e-16,2e-16)
  DirMode = 2
  FaceMakerClass = Part::FaceMakerBullseye
  LengthFwd = 19
  LengthRev = 0
  Placement = pos=(-19,0,0) rot=(0,0,1;0rad)
  Solid = true
  Symmetric = false
FEATURE [Part::Fillet] Fillet023
  Base = -> Extrude023
  Edges = <same value as first occurrence — deduplicated (x6 in doc)>
  Placement = pos=(0,0.05,0) rot=(0,0,1;0rad)
FEATURE [Part::Cut] Cut014  label="bottom003"
  Base = -> Cut007
  Tool = -> Fusion047
FEATURE [Part::Cut] Cut021  label="bottom004"
  Base = -> Cut014
  Tool = -> Fillet023
FEATURE [Sketcher::SketchObject] Sketch033
  FullyConstrained = true
  Placement = pos=(117,19,0) rot=(0.57735,0.57735,0.57735;2.0944rad)
  sketch-geometry (8):
    g0: LineSegment StartX=-49.19 StartY=69.25 StartZ=0 EndX=-49.19 EndY=66.25 EndZ=0
    g1: LineSegment StartX=-49.19 StartY=5.75 StartZ=0 EndX=-49.19 EndY=2.75 EndZ=0
    g2: ArcOfCircle CenterX=-1.5 CenterY=67.75 CenterZ=0 NormalX=0 NormalY=0 NormalZ=1 AngleXU=0 Radius=1.5 StartAngle=4.71239 EndAngle=7.85398
    g3: ArcOfCircle CenterX=-1.5 CenterY=4.25 CenterZ=0 NormalX=0 NormalY=0 NormalZ=1 AngleXU=0 Radius=1.5 StartAngle=4.71239 EndAngle=7.85398
    g4: LineSegment StartX=-49.19 StartY=69.25 StartZ=0 EndX=-1.5 EndY=69.25 EndZ=0
    g5: LineSegment StartX=-49.19 StartY=66.25 StartZ=0 EndX=-1.5 EndY=66.25 EndZ=0
    g6: LineSegment StartX=-49.19 StartY=5.75 StartZ=0 EndX=-1.5 EndY=5.75 EndZ=0
    g7: LineSegment StartX=-49.19 StartY=2.75 StartZ=0 EndX=-1.5 EndY=2.75 EndZ=0
  constraints (19):
    c: Vertical(g0)
    c: Distance(g0) = 3
    c: Block(g0)
    c: Vertical(g1)
    c: Block(g2)
    c: Block(g3)
    c: Block(g1)
    c: Coincident(g4,g0)
    c: Coincident(g4,g2)
    c: Horizontal(g4)
    c: Coincident(g5,g0)
    c: Coincident(g5,g2)
    c: Horizontal(g5)
    c: Coincident(g6,g1)
    c: Coincident(g6,g3)
    c: Horizontal(g6)
    c: Coincident(g7,g1)
    c: Coincident(g7,g3)
    c: Horizontal(g7)
FEATURE [Sketcher::SketchObject] Sketch034
  FullyConstrained = true
  Placement = pos=(117,19,0) rot=(0.57735,0.57735,0.57735;2.0944rad)
  sketch-geometry (8):
    g0: LineSegment StartX=-49.19 StartY=63.5 StartZ=0 EndX=-49.19 EndY=60.5 EndZ=0
    g1: LineSegment StartX=-49.19 StartY=11.5 StartZ=0 EndX=-49.19 EndY=8.5 EndZ=0
    g2: ArcOfCircle CenterX=-1.5 CenterY=62 CenterZ=0 NormalX=0 NormalY=0 NormalZ=1 AngleXU=0 Radius=1.5 StartAngle=4.71239 EndAngle=7.85398
    g3: ArcOfCircle CenterX=-1.5 CenterY=10 CenterZ=0 NormalX=0 NormalY=0 NormalZ=1 AngleXU=0 Radius=1.5 StartAngle=4.71239 EndAngle=7.85398
    g4: LineSegment StartX=-49.19 StartY=63.5 StartZ=0 EndX=-1.5 EndY=63.5 EndZ=0
    g5: LineSegment StartX=-49.19 StartY=60.5 StartZ=0 EndX=-1.5 EndY=60.5 EndZ=0
    g6: LineSegment StartX=-49.19 StartY=11.5 StartZ=0 EndX=-1.5 EndY=11.5 EndZ=0
    g7: LineSegment StartX=-49.19 StartY=8.5 StartZ=0 EndX=-1.5 EndY=8.5 EndZ=0
  constraints (19):
    c: Vertical(g0)
    c: Distance(g0) = 3
    c: Vertical(g1)
    c: Block(g1)
    c: Block(g2)
    c: Block(g3)
    c: Block(g0)
    c: Coincident(g4,g0)
    c: Coincident(g4,g2)
    c: Horizontal(g4)
    c: Coincident(g5,g0)
    c: Coincident(g5,g2)
    c: Horizontal(g5)
    c: Coincident(g6,g1)
    c: Coincident(g6,g3)
    c: Horizontal(g6)
    c: Coincident(g7,g1)
    c: Coincident(g7,g3)
    c: Horizontal(g7)
FEATURE [Part::Extrusion] Extrude024
  Base = -> Sketch033
  Dir = (1,0,0)
  DirMode = 2
  FaceMakerClass = Part::FaceMakerBullseye
  LengthFwd = 10
  LengthRev = 0
  Solid = true
  Symmetric = false
FEATURE [Part::Extrusion] Extrude025
  Base = -> Sketch034
  Dir = (1,0,0)
  DirMode = 2
  FaceMakerClass = Part::FaceMakerBullseye
  LengthFwd = 10
  LengthRev = 0
  Solid = true
  Symmetric = false
FEATURE [Part::Fillet] Fillet024  label="removeFromtMoreFrontCaseScrewRetainers"
  Base = -> Extrude024
  Edges = 4 edges r=1.49: [Edge6,Edge11,Edge18,Edge23]
  Placement = pos=(-11,0,0) rot=(0,0,1;0rad)
FEATURE [Part::Fillet] Fillet025  label="removeFromtMoreFrontCaseScrewRetainers001"
  Base = -> Extrude025
  Edges = 4 edges r=1.49: [Edge6,Edge11,Edge18,Edge23]
  Placement = pos=(-19,0,0) rot=(0,0,1;0rad)
FEATURE [Part::Cut] Cut022
  Base = -> Cut015
  Tool = -> Fillet025
FEATURE [Part::Cut] Cut023  label="screwRetainers"
  Base = -> Cut022
  Tool = -> Fillet024
FEATURE [Part::MultiFuse] Fusion056  label="bottom005"
  Shapes = -> [Fusion044,Cut021]
FEATURE [Part::MultiFuse] Fusion057  label="casePillars001"
  Shapes = -> [Cut016,Fusion052]
FEATURE [Part::MultiFuse] Fusion058  label="bottom006"
  Shapes = -> [Fusion056,Cut023]
FEATURE [Part::MultiFuse] Fusion059  label="bottom007"
  Shapes = -> [Fusion058,Fillet005]
FEATURE [Part::MultiFuse] Fusion060  label="bottom008"
  Shapes = -> [Fusion059,Fusion]
FEATURE [Part::MultiFuse] Fusion061  label="top011"
  Shapes = -> [Cut006,Cut020]
FEATURE [Part::MultiFuse] Fusion062  label="top012"
  Shapes = -> [Fusion057,Fusion061]
FEATURE [Sketcher::SketchObject] Sketch035  label="topSketch007"
  FullyConstrained = true
  sketch-geometry (6):
    g0: LineSegment StartX=19 StartY=38 StartZ=0 EndX=117 EndY=38 EndZ=0
    g1: ArcOfCircle CenterX=19 CenterY=19 CenterZ=0 NormalX=0 NormalY=0 NormalZ=1 AngleXU=0 Radius=19 StartAngle=1.5708 EndAngle=3.14159
    g2: LineSegment StartX=117 StartY=38 StartZ=0 EndX=117 EndY=19 EndZ=0
    g3: LineSegment StartX=98 StartY=1.0161e-12 StartZ=0 EndX=5.22862e-06 EndY=1.0161e-12 EndZ=0
    g4: LineSegment StartX=5.22862e-06 StartY=19 StartZ=0 EndX=5.22862e-06 EndY=1.0161e-12 EndZ=0
    g5: ArcOfCircle CenterX=98 CenterY=19 CenterZ=0 NormalX=0 NormalY=0 NormalZ=1 AngleXU=0 Radius=19 StartAngle=4.71239 EndAngle=6.28319
  constraints (16):
    c: Horizontal(g0)
    c: Distance(g0) = 98
    c: Coincident(g1,g0)
    c: Block(g1)
    c: Coincident(g2,g0)
    c: Vertical(g2)
    c: Distance(g2) = 19
    c: Horizontal(g3)
    c: Coincident(g4,g1)
    c: Vertical(g4)
    c: Coincident(g3,g4)
    c: Block(g3)
    c: Coincident(g5,g2)
    c: Coincident(g5,g3)
    c: Block(g0)
    c: Block(g5)
FEATURE [Part::Extrusion] Extrude026  label="sideA001"
  Base = -> Sketch035
  Dir = (0,0,1)
  DirMode = 2
  FaceMakerClass = Part::FaceMakerBullseye
  LengthFwd = 3
  LengthRev = 0
  Placement = pos=(0,0,-2.7) rot=(0,0,1;0rad)
  Solid = true
  Symmetric = false
FEATURE [Sketcher::SketchObject] Sketch036  label="topSketch008"
  FullyConstrained = true
  sketch-geometry (6):
    g0: LineSegment StartX=19 StartY=38 StartZ=0 EndX=117 EndY=38 EndZ=0
    g1: ArcOfCircle CenterX=19 CenterY=19 CenterZ=0 NormalX=0 NormalY=0 NormalZ=1 AngleXU=0 Radius=19 StartAngle=1.5708 EndAngle=3.14159
    g2: LineSegment StartX=117 StartY=38 StartZ=0 EndX=117 EndY=19 EndZ=0
    g3: LineSegment StartX=98 StartY=1.0161e-12 StartZ=0 EndX=5.22862e-06 EndY=1.0161e-12 EndZ=0
    g4: LineSegment StartX=5.22862e-06 StartY=19 StartZ=0 EndX=5.22862e-06 EndY=1.0161e-12 EndZ=0
    g5: ArcOfCircle CenterX=98 CenterY=19 CenterZ=0 NormalX=0 NormalY=0 NormalZ=1 AngleXU=0 Radius=19 StartAngle=4.71239 EndAngle=6.28319
  constraints (16):
    c: Horizontal(g0)
    c: Distance(g0) = 98
    c: Coincident(g1,g0)
    c: Block(g1)
    c: Coincident(g2,g0)
    c: Vertical(g2)
    c: Distance(g2) = 19
    c: Horizontal(g3)
    c: Coincident(g4,g1)
    c: Vertical(g4)
    c: Coincident(g3,g4)
    c: Block(g3)
    c: Coincident(g5,g2)
    c: Coincident(g5,g3)
    c: Block(g0)
    c: Block(g5)
FEATURE [Part::Extrusion] Extrude027  label="sideB001"
  Base = -> Sketch036
  Dir = (0,0,1)
  DirMode = 2
  FaceMakerClass = Part::FaceMakerBullseye
  LengthFwd = 3
  LengthRev = 0
  Placement = pos=(0,0,71.7) rot=(0,0,1;0rad)
  Solid = true
  Symmetric = false
FEATURE [Part::MultiFuse] Fusion064  label="removeFromBottom"
  Shapes = -> [Extrude026,Extrude027]
FEATURE [Part::Cut] Cut024  label="bottom009"
  Base = -> Fusion060
  Tool = -> Fusion064
FEATURE [Sketcher::SketchObject] Sketch037  label="topSketch009"
  FullyConstrained = true
  sketch-geometry (8):
    g0: ArcOfCircle CenterX=19 CenterY=19.1201 CenterZ=0 NormalX=0 NormalY=0 NormalZ=1 AngleXU=0 Radius=18.8799 StartAngle=1.5708 EndAngle=3.14793
    g1: LineSegment StartX=0.120501 StartY=19.0004 StartZ=0 EndX=0.120501 EndY=0.000382114 EndZ=0
    g2: LineSegment StartX=19 StartY=38 StartZ=0 EndX=124 EndY=38 EndZ=0
    g3: LineSegment StartX=0.120501 StartY=0.000382114 StartZ=0 EndX=105.121 EndY=0.000382114 EndZ=0
    g4: LineSegment StartX=124 StartY=38 StartZ=0 EndX=125.616 EndY=38 EndZ=0
    g5: LineSegment StartX=105.121 StartY=0.000382114 StartZ=0 EndX=106.736 EndY=0.000382114 EndZ=0
    g6: ArcOfCircle CenterX=106.616 CenterY=19 CenterZ=0 NormalX=0 NormalY=0 NormalZ=1 AngleXU=0 Radius=19 StartAngle=4.71873 EndAngle=6.28319
    g7: LineSegment StartX=125.616 StartY=38 StartZ=0 EndX=125.616 EndY=19 EndZ=0
  constraints (21):
    c: Block(g0)
    c: Coincident(g1,g0)
    c: Vertical(g1)
    c: Horizontal(g2)
    c: Distance(g2) = 105
    c: Coincident(g2,g0)
    c: Distance(g1) = 19
    c: Coincident(g3,g1)
    c: Horizontal(g3)
    c: Distance(g3) = 105
    c: Coincident(g4,g2)
    c: Horizontal(g4)
    c: Distance(g4) = 1.61553
    c: Horizontal(g5)
    c: Equal(g4,g5) = 1.61553
    c: Coincident(g5,g3)
    c: Block(g6)
    c: Coincident(g6,g5)
    c: Coincident(g7,g4)
    c: Coincident(g7,g6)
    c: Vertical(g7)
FEATURE [Part::Extrusion] Extrude028  label="sideB"
  Base = -> Sketch037
  Dir = (0,0,1)
  DirMode = 2
  FaceMakerClass = Part::FaceMakerBullseye
  LengthFwd = 3
  LengthRev = 0
  Placement = pos=(0,0,72) rot=(0,0,1;0rad)
  Solid = true
  Symmetric = false
FEATURE [Sketcher::SketchObject] Sketch038  label="topSketch010"
  FullyConstrained = true
  sketch-geometry (22):
    g0: LineSegment StartX=5.21097e-06 StartY=3 StartZ=0 EndX=5.21097e-06 EndY=19 EndZ=0
    g1: ArcOfCircle CenterX=19 CenterY=19 CenterZ=0 NormalX=0 NormalY=0 NormalZ=1 AngleXU=0 Radius=19 StartAngle=1.5708 EndAngle=3.14159
    g2: ArcOfCircle CenterX=19 CenterY=19 CenterZ=0 NormalX=0 NormalY=0 NormalZ=1 AngleXU=0 Radius=16 StartAngle=1.5708 EndAngle=3.14159
    g3: LineSegment StartX=114 StartY=35 StartZ=0 EndX=19 EndY=35 EndZ=0
    g4: LineSegment StartX=5.21097e-06 StartY=3 StartZ=0 EndX=5.21097e-06 EndY=0 EndZ=0
    g5: LineSegment StartX=3 StartY=0 StartZ=0 EndX=5.21097e-06 EndY=0 EndZ=0
    g6: LineSegment StartX=3 StartY=19 StartZ=0 EndX=3 EndY=0 EndZ=0
    g7: LineSegment StartX=19 StartY=38 StartZ=0 EndX=124 EndY=38 EndZ=0
    g8: Circle CenterX=119 CenterY=35 CenterZ=0 NormalX=0 NormalY=0 NormalZ=1 AngleXU=0 Radius=1
    g9: Circle CenterX=121 CenterY=35 CenterZ=0 NormalX=0 NormalY=0 NormalZ=1 AngleXU=0 Radius=1
    g10: Circle CenterX=121 CenterY=33 CenterZ=0 NormalX=0 NormalY=0 NormalZ=1 AngleXU=0 Radius=1
    g11: BSplineCurve PolesCount=3 KnotsCount=2 Degree=2 IsPeriodic=0
    g12: GeomPoint X=119 Y=35 Z=0
    g13: GeomPoint X=121 Y=33 Z=0
    g14: LineSegment StartX=119 StartY=35 StartZ=0 EndX=114 EndY=35 EndZ=0
    g15: ArcOfCircle CenterX=105 CenterY=19 CenterZ=0 NormalX=0 NormalY=0 NormalZ=1 AngleXU=0 Radius=16 StartAngle=5.60905 EndAngle=6.28319
    g16: LineSegment StartX=121 StartY=33 StartZ=0 EndX=121 EndY=19 EndZ=0
    g17: LineSegment StartX=117.5 StartY=9.01251 StartZ=0 EndX=121.163 EndY=9.0125 EndZ=0
    g18: ArcOfCircle CenterX=105 CenterY=19 CenterZ=0 NormalX=0 NormalY=0 NormalZ=1 AngleXU=0 Radius=20.6155 StartAngle=5.7297 EndAngle=6.28319
    g19: LineSegment StartX=121.163 StartY=9.0125 StartZ=0 EndX=122.538 EndY=8.16329 EndZ=0
    g20: LineSegment StartX=124 StartY=38 StartZ=0 EndX=125.616 EndY=38 EndZ=0
    g21: LineSegment StartX=125.616 StartY=19 StartZ=0 EndX=125.616 EndY=38 EndZ=0
  constraints (49):
    c: Vertical(g0)
    c: Block(g0)
    c: Coincident(g1,g0)
    c: Block(g1)
    c: Coincident(g2,g1)
    c: Block(g2)
    c: Coincident(g3,g2)
    c: Horizontal(g3)
    c: Tangent(g3,g2)
    c: Coincident(g4,g0)
    c: Distance(g4) = 3
    c: Vertical(g4)
    c: Coincident(g5,g4)
    c: Horizontal(g5)
    c: Coincident(g6,g2)
    c: Coincident(g6,g5)
    c: Vertical(g6)
    c: Horizontal(g7)
    c: Distance(g7) = 105
    c: Coincident(g7,g1)
    c: Block(g3)
    c: Weight(g8) = 1
    c: Equal(g8,g9)
    c: Equal(g8,g10)
    c: InternalAlignment(g8,g11)
    c: InternalAlignment(g9,g11)
    c: InternalAlignment(g10,g11)
    c: InternalAlignment(g12,g11)
    c: InternalAlignment(g13,g11)
    c: Block(g11)
    c: Coincident(g14,g11)
    c: Coincident(g14,g3)
    c: Horizontal(g14)
    c: Block(g15)
    c: Coincident(g16,g11)
    c: Coincident(g16,g15)
    c: Vertical(g16)
    c: Distance(g16) = 14
    c: Coincident(g17,g15)
    c: Block(g18)
    c: Coincident(g19,g18)
    c: Coincident(g20,g7)
    c: Horizontal(g20)
    c: Vertical(g21)
    c: Coincident(g20,g21)
    c: Block(g20)
    c: Block(g21)
    c: Block(g19)
    c: Block(g17)
FEATURE [Part::Extrusion] Extrude029
  Base = -> Sketch038
  Dir = (0,0,1)
  DirMode = 2
  FaceMakerClass = Part::FaceMakerBullseye
  LengthFwd = 72
  LengthRev = 0
  Solid = true
  Symmetric = false
FEATURE [Part::Feature] Face085
  shape: bbox 4.8 x 25.5 x 2e-07 mm, 1 faces, 0 solids (baked)
FEATURE [Part::Revolution] Revolve089  label="moreFrontCaseScrewPost003"
  Angle = 360
  Axis = (0,1,0)
  Base = (0,0,0)
  FaceMakerClass = Part::FaceMakerBullseye
  Placement = pos=(109.5,4.5,3.5) rot=(0,0,1;0rad)
  Solid = false
  Source = -> Face085
  Symmetric = false
FEATURE [Part::Feature] Face086
  shape: bbox 4.8 x 25.5 x 2e-07 mm, 1 faces, 0 solids (baked)
FEATURE [Part::Revolution] Revolve090  label="moreFrontCaseScrewPost004"
  Angle = 360
  Axis = (0,1,0)
  Base = (0,0,0)
  FaceMakerClass = Part::FaceMakerBullseye
  Placement = pos=(109.5,4.5,68.5) rot=(0,0,1;0rad)
  Solid = false
  Source = -> Face086
  Symmetric = false
FEATURE [Part::Fillet] Fillet026  label="top013"
  Base = -> Extrude029
  Edges = 1 edges r=2: [Edge35]
FEATURE [Sketcher::SketchObject] Sketch039
  FullyConstrained = true
  sketch-geometry (7):
    g0: LineSegment StartX=0 StartY=0 StartZ=0 EndX=0 EndY=6 EndZ=0
    g1: Circle CenterX=0 CenterY=0 CenterZ=0 NormalX=0 NormalY=0 NormalZ=1 AngleXU=0 Radius=1
    g2: Circle CenterX=8 CenterY=6 CenterZ=0 NormalX=0 NormalY=0 NormalZ=1 AngleXU=0 Radius=1
    g3: BSplineCurve PolesCount=3 KnotsCount=2 Degree=2 IsPeriodic=0
    g4: GeomPoint X=0 Y=0 Z=0
    g5: GeomPoint X=8 Y=6 Z=0
    g6: LineSegment StartX=0 StartY=6 StartZ=0 EndX=8 EndY=6 EndZ=0
  constraints (14):
    c: Coincident(g0,g-1)
    c: Distance(g0) = 6
    c: Vertical(g0)
    c: Coincident(g3,g0)
    c: Weight(g1) = 1
    c: Equal(g1,g2)
    c: InternalAlignment(g1,g3)
    c: InternalAlignment(g2,g3)
    c: InternalAlignment(g4,g3)
    c: InternalAlignment(g5,g3)
    c: Block(g3)
    c: Coincident(g6,g0)
    c: Coincident(g6,g3)
    c: Horizontal(g6)
FEATURE [Sketcher::SketchObject] Sketch040
  FullyConstrained = true
  sketch-geometry (7):
    g0: LineSegment StartX=0 StartY=0 StartZ=0 EndX=0 EndY=6 EndZ=0
    g1: Circle CenterX=0 CenterY=0 CenterZ=0 NormalX=0 NormalY=0 NormalZ=1 AngleXU=0 Radius=1
    g2: Circle CenterX=8 CenterY=6 CenterZ=0 NormalX=0 NormalY=0 NormalZ=1 AngleXU=0 Radius=1
    g3: BSplineCurve PolesCount=3 KnotsCount=2 Degree=2 IsPeriodic=0
    g4: GeomPoint X=0 Y=0 Z=0
    g5: GeomPoint X=8 Y=6 Z=0
    g6: LineSegment StartX=0 StartY=6 StartZ=0 EndX=8 EndY=6 EndZ=0
  constraints (14):
    c: Coincident(g0,g-1)
    c: Distance(g0) = 6
    c: Vertical(g0)
    c: Coincident(g3,g0)
    c: Weight(g1) = 1
    c: Equal(g1,g2)
    c: InternalAlignment(g1,g3)
    c: InternalAlignment(g2,g3)
    c: InternalAlignment(g4,g3)
    c: InternalAlignment(g5,g3)
    c: Block(g3)
    c: Coincident(g6,g0)
    c: Coincident(g6,g3)
    c: Horizontal(g6)
FEATURE [Sketcher::SketchObject] Sketch041
  FullyConstrained = true
  sketch-geometry (7):
    g0: LineSegment StartX=0 StartY=0 StartZ=0 EndX=0 EndY=6 EndZ=0
    g1: Circle CenterX=0 CenterY=0 CenterZ=0 NormalX=0 NormalY=0 NormalZ=1 AngleXU=0 Radius=1
    g2: Circle CenterX=8 CenterY=6 CenterZ=0 NormalX=0 NormalY=0 NormalZ=1 AngleXU=0 Radius=1
    g3: BSplineCurve PolesCount=3 KnotsCount=2 Degree=2 IsPeriodic=0
    g4: GeomPoint X=0 Y=0 Z=0
    g5: GeomPoint X=8 Y=6 Z=0
    g6: LineSegment StartX=0 StartY=6 StartZ=0 EndX=8 EndY=6 EndZ=0
  constraints (14):
    c: Coincident(g0,g-1)
    c: Distance(g0) = 6
    c: Vertical(g0)
    c: Coincident(g3,g0)
    c: Weight(g1) = 1
    c: Equal(g1,g2)
    c: InternalAlignment(g1,g3)
    c: InternalAlignment(g2,g3)
    c: InternalAlignment(g4,g3)
    c: InternalAlignment(g5,g3)
    c: Block(g3)
    c: Coincident(g6,g0)
    c: Coincident(g6,g3)
    c: Horizontal(g6)
FEATURE [Sketcher::SketchObject] Sketch042
  FullyConstrained = true
  sketch-geometry (7):
    g0: LineSegment StartX=0 StartY=0 StartZ=0 EndX=0 EndY=6 EndZ=0
    g1: Circle CenterX=0 CenterY=0 CenterZ=0 NormalX=0 NormalY=0 NormalZ=1 AngleXU=0 Radius=1
    g2: Circle CenterX=8 CenterY=6 CenterZ=0 NormalX=0 NormalY=0 NormalZ=1 AngleXU=0 Radius=1
    g3: BSplineCurve PolesCount=3 KnotsCount=2 Degree=2 IsPeriodic=0
    g4: GeomPoint X=0 Y=0 Z=0
    g5: GeomPoint X=8 Y=6 Z=0
    g6: LineSegment StartX=0 StartY=6 StartZ=0 EndX=8 EndY=6 EndZ=0
  constraints (14):
    c: Coincident(g0,g-1)
    c: Distance(g0) = 6
    c: Vertical(g0)
    c: Coincident(g3,g0)
    c: Weight(g1) = 1
    c: Equal(g1,g2)
    c: InternalAlignment(g1,g3)
    c: InternalAlignment(g2,g3)
    c: InternalAlignment(g4,g3)
    c: InternalAlignment(g5,g3)
    c: Block(g3)
    c: Coincident(g6,g0)
    c: Coincident(g6,g3)
    c: Horizontal(g6)
FEATURE [Part::Extrusion] Extrude030  label="caseScrewPillarBracket008"
  Base = -> Sketch039
  Dir = (0,0,1)
  DirMode = 2
  FaceMakerClass = Part::FaceMakerBullseye
  LengthFwd = 2.4
  LengthRev = 0
  Placement = pos=(15.76,29,8.8) rot=(0,1,0;0rad)
  Solid = true
  Symmetric = false
FEATURE [Part::Extrusion] Extrude031  label="caseScrewPillarBracket009"
  Base = -> Sketch040
  Dir = (0,0,1)
  DirMode = 2
  FaceMakerClass = Part::FaceMakerBullseye
  LengthFwd = 2.4
  LengthRev = 0
  Placement = pos=(15.76,29,60.8) rot=(0,0,1;0rad)
  Solid = true
  Symmetric = false
FEATURE [Part::Extrusion] Extrude032  label="caseScrewPillarBracket010"
  Base = -> Sketch041
  Dir = (0,0,1)
  DirMode = 2
  FaceMakerClass = Part::FaceMakerBullseye
  LengthFwd = 2.4
  LengthRev = 0
  Placement = pos=(13.7,29,13.26) rot=(0,-1,0;1.5708rad)
  Solid = true
  Symmetric = false
FEATURE [Part::Extrusion] Extrude033  label="caseScrewPillarBracket011"
  Base = -> Sketch042
  Dir = (0,0,1)
  DirMode = 2
  FaceMakerClass = Part::FaceMakerBullseye
  LengthFwd = 2.4
  LengthRev = 0
  Placement = pos=(11.3,29,58.74) rot=(0,1,0;1.5708rad)
  Solid = true
  Symmetric = false
FEATURE [Sketcher::SketchObject] Sketch043
  FullyConstrained = true
  sketch-geometry (7):
    g0: LineSegment StartX=0 StartY=0 StartZ=0 EndX=0 EndY=6 EndZ=0
    g1: Circle CenterX=0 CenterY=0 CenterZ=0 NormalX=0 NormalY=0 NormalZ=1 AngleXU=0 Radius=1
    g2: Circle CenterX=8 CenterY=6 CenterZ=0 NormalX=0 NormalY=0 NormalZ=1 AngleXU=0 Radius=1
    g3: BSplineCurve PolesCount=3 KnotsCount=2 Degree=2 IsPeriodic=0
    g4: GeomPoint X=0 Y=0 Z=0
    g5: GeomPoint X=8 Y=6 Z=0
    g6: LineSegment StartX=0 StartY=6 StartZ=0 EndX=8 EndY=6 EndZ=0
  constraints (14):
    c: Coincident(g0,g-1)
    c: Distance(g0) = 6
    c: Vertical(g0)
    c: Coincident(g3,g0)
    c: Weight(g1) = 1
    c: Equal(g1,g2)
    c: InternalAlignment(g1,g3)
    c: InternalAlignment(g2,g3)
    c: InternalAlignment(g4,g3)
    c: InternalAlignment(g5,g3)
    c: Block(g3)
    c: Coincident(g6,g0)
    c: Coincident(g6,g3)
    c: Horizontal(g6)
FEATURE [Part::Extrusion] Extrude034  label="caseScrewPillarBracket012"
  Base = -> Sketch043
  Dir = (0,0,1)
  DirMode = 2
  FaceMakerClass = Part::FaceMakerBullseye
  LengthFwd = 2.4
  LengthRev = 0
  Placement = pos=(88.3,29,65.23) rot=(0,1,0;1.5708rad)
  Solid = true
  Symmetric = false
FEATURE [Sketcher::SketchObject] Sketch044
  FullyConstrained = true
  sketch-geometry (7):
    g0: LineSegment StartX=0 StartY=0 StartZ=0 EndX=0 EndY=6 EndZ=0
    g1: Circle CenterX=0 CenterY=0 CenterZ=0 NormalX=0 NormalY=0 NormalZ=1 AngleXU=0 Radius=1
    g2: Circle CenterX=8 CenterY=6 CenterZ=0 NormalX=0 NormalY=0 NormalZ=1 AngleXU=0 Radius=1
    g3: BSplineCurve PolesCount=3 KnotsCount=2 Degree=2 IsPeriodic=0
    g4: GeomPoint X=0 Y=0 Z=0
    g5: GeomPoint X=8 Y=6 Z=0
    g6: LineSegment StartX=0 StartY=6 StartZ=0 EndX=8 EndY=6 EndZ=0
  constraints (14):
    c: Coincident(g0,g-1)
    c: Distance(g0) = 6
    c: Vertical(g0)
    c: Coincident(g3,g0)
    c: Weight(g1) = 1
    c: Equal(g1,g2)
    c: InternalAlignment(g1,g3)
    c: InternalAlignment(g2,g3)
    c: InternalAlignment(g4,g3)
    c: InternalAlignment(g5,g3)
    c: Block(g3)
    c: Coincident(g6,g0)
    c: Coincident(g6,g3)
    c: Horizontal(g6)
FEATURE [Part::Extrusion] Extrude035  label="caseScrewPillarBracket013"
  Base = -> Sketch044
  Dir = (0,0,1)
  DirMode = 2
  FaceMakerClass = Part::FaceMakerBullseye
  LengthFwd = 2.4
  LengthRev = 0
  Placement = pos=(90.7,29,6.77) rot=(0,-1,0;1.5708rad)
  Solid = true
  Symmetric = false
FEATURE [Sketcher::SketchObject] Sketch045
  FullyConstrained = true
  sketch-geometry (7):
    g0: LineSegment StartX=0 StartY=0 StartZ=0 EndX=0 EndY=6 EndZ=0
    g1: Circle CenterX=0 CenterY=0 CenterZ=0 NormalX=0 NormalY=0 NormalZ=1 AngleXU=0 Radius=1
    g2: Circle CenterX=8 CenterY=6 CenterZ=0 NormalX=0 NormalY=0 NormalZ=1 AngleXU=0 Radius=1
    g3: BSplineCurve PolesCount=3 KnotsCount=2 Degree=2 IsPeriodic=0
    g4: GeomPoint X=0 Y=0 Z=0
    g5: GeomPoint X=8 Y=6 Z=0
    g6: LineSegment StartX=0 StartY=6 StartZ=0 EndX=8 EndY=6 EndZ=0
  constraints (14):
    c: Coincident(g0,g-1)
    c: Distance(g0) = 6
    c: Vertical(g0)
    c: Coincident(g3,g0)
    c: Weight(g1) = 1
    c: Equal(g1,g2)
    c: InternalAlignment(g1,g3)
    c: InternalAlignment(g2,g3)
    c: InternalAlignment(g4,g3)
    c: InternalAlignment(g5,g3)
    c: Block(g3)
    c: Coincident(g6,g0)
    c: Coincident(g6,g3)
    c: Horizontal(g6)
FEATURE [Sketcher::SketchObject] Sketch046
  FullyConstrained = true
  sketch-geometry (7):
    g0: LineSegment StartX=0 StartY=0 StartZ=0 EndX=0 EndY=6 EndZ=0
    g1: Circle CenterX=0 CenterY=0 CenterZ=0 NormalX=0 NormalY=0 NormalZ=1 AngleXU=0 Radius=1
    g2: Circle CenterX=8 CenterY=6 CenterZ=0 NormalX=0 NormalY=0 NormalZ=1 AngleXU=0 Radius=1
    g3: BSplineCurve PolesCount=3 KnotsCount=2 Degree=2 IsPeriodic=0
    g4: GeomPoint X=0 Y=0 Z=0
    g5: GeomPoint X=8 Y=6 Z=0
    g6: LineSegment StartX=0 StartY=6 StartZ=0 EndX=8 EndY=6 EndZ=0
  constraints (14):
    c: Coincident(g0,g-1)
    c: Distance(g0) = 6
    c: Vertical(g0)
    c: Coincident(g3,g0)
    c: Weight(g1) = 1
    c: Equal(g1,g2)
    c: InternalAlignment(g1,g3)
    c: InternalAlignment(g2,g3)
    c: InternalAlignment(g4,g3)
    c: InternalAlignment(g5,g3)
    c: Block(g3)
    c: Coincident(g6,g0)
    c: Coincident(g6,g3)
    c: Horizontal(g6)
FEATURE [Part::Extrusion] Extrude036  label="caseScrewPillarBracket014"
  Base = -> Sketch045
  Dir = (0,0,1)
  DirMode = 2
  FaceMakerClass = Part::FaceMakerBullseye
  LengthFwd = 2.4
  LengthRev = 0
  Placement = pos=(110.7,29,6.77) rot=(0,-1,0;1.5708rad)
  Solid = true
  Symmetric = false
FEATURE [Part::Extrusion] Extrude037  label="caseScrewPillarBracket015"
  Base = -> Sketch046
  Dir = (0,0,1)
  DirMode = 2
  FaceMakerClass = Part::FaceMakerBullseye
  LengthFwd = 2.4
  LengthRev = 0
  Placement = pos=(108.3,29,65.23) rot=(0,1,0;1.5708rad)
  Solid = true
  Symmetric = false
FEATURE [Part::Box] Box013  label="frontCaseScrewPillarBracket002"
  AttacherType = Attacher::AttachEngine3D
  Height = 2.4
  Length = 22
  Placement = pos=(87,28,2.3) rot=(0,0,1;0rad)
  Width = 7
FEATURE [Part::Box] Box014  label="frontCaseScrewPillarBracket003"
  AttacherType = Attacher::AttachEngine3D
  Height = 2.4
  Length = 22
  Placement = pos=(87,28,67.3) rot=(0,0,1;0rad)
  Width = 7
FEATURE [Part::Feature] Face087
  shape: bbox 4.8 x 30.2 x 2e-07 mm, 1 faces, 0 solids (baked)
FEATURE [Part::Revolution] Revolve091  label="frontCaseScrewPost004"
  Angle = 360
  Axis = (0,1,0)
  Base = (0,0,0)
  FaceMakerClass = Part::FaceMakerBullseye
  Placement = pos=(89.5,4.5,3.5) rot=(0,0,1;0rad)
  Solid = false
  Source = -> Face087
  Symmetric = false
FEATURE [Part::Feature] Face088
  shape: bbox 4.8 x 30.2 x 2e-07 mm, 1 faces, 0 solids (baked)
FEATURE [Part::Revolution] Revolve092  label="frontCaseScrewPost005"
  Angle = 360
  Axis = (0,1,0)
  Base = (0,0,0)
  FaceMakerClass = Part::FaceMakerBullseye
  Placement = pos=(89.5,4.5,68.5) rot=(0,0,1;0rad)
  Solid = false
  Source = -> Face088
  Symmetric = false
FEATURE [Part::Feature] Face089
  shape: bbox 3.5 x 30.2 x 2e-07 mm, 1 faces, 0 solids (baked)
FEATURE [Part::Revolution] Revolve093  label="backCaseScrewPost002"
  Angle = 360
  Axis = (0,1,0)
  Base = (0,0,0)
  FaceMakerClass = Part::FaceMakerBullseye
  Placement = pos=(12.5,4.5,10) rot=(0,0,1;0rad)
  Solid = false
  Source = -> Face089
  Symmetric = false
FEATURE [Part::Feature] Face090
  shape: bbox 3.5 x 30.2 x 2e-07 mm, 1 faces, 0 solids (baked)
FEATURE [Part::Revolution] Revolve094  label="backCaseScrewPost003"
  Angle = 360
  Axis = (0,1,0)
  Base = (0,0,0)
  FaceMakerClass = Part::FaceMakerBullseye
  Placement = pos=(12.5,4.5,62) rot=(0,0,1;0rad)
  Solid = false
  Source = -> Face090
  Symmetric = false
FEATURE [Part::Box] Box015  label="Cube011"
  AttacherType = Attacher::AttachEngine3D
  Height = 28.8
  Length = 3
  Placement = pos=(107.3,28,21.6) rot=(0,0,1;0rad)
  Width = 7
FEATURE [Part::Box] Box016  label="Cube012"
  AttacherType = Attacher::AttachEngine3D
  Height = 3
  Length = 7.4
  Placement = pos=(107.3,28,18.6) rot=(0,0,1;0rad)
  Width = 7
FEATURE [Part::Box] Box017  label="Cube013"
  AttacherType = Attacher::AttachEngine3D
  Height = 3
  Length = 7.4
  Placement = pos=(107.3,28,50.4) rot=(0,0,1;0rad)
  Width = 7
FEATURE [Part::Cylinder] Cylinder024
  Angle = 360
  AttacherType = Attacher::AttachEngine3D
  Height = 20
  Placement = pos=(0,0,36.15) rot=(0,0,1;0rad)
  Radius = 14.3
FEATURE [Part::Cylinder] Cylinder025
  Angle = 360
  AttacherType = Attacher::AttachEngine3D
  Height = 10
  Placement = pos=(0,0,36.15) rot=(0,0,1;0rad)
  Radius = 4
FEATURE [Part::MultiFuse] Fusion066  label="removeToCreteHoleForPlugHousing009"
  Placement = pos=(70,19,36) rot=(0,1,0;1.5708rad)
  Shapes = -> [Cylinder024,Cylinder025]
FEATURE [Part::MultiFuse] Fusion065  label="plugHousingBracketHolder002"
  Shapes = -> [Box017,Box015,Box016]
FEATURE [Part::Cut] Cut025  label="plugHousingBracketHolder003"
  Base = -> Fusion065
  Placement = pos=(7,0,0) rot=(0,0,1;0rad)
  Tool = -> Fusion066
FEATURE [Sketcher::SketchObject] Sketch047
  FullyConstrained = false
  Placement = pos=(0,0,0) rot=(1,0,0;1.5708rad)
  sketch-geometry (24):
    g0: ArcOfCircle CenterX=-4 CenterY=-10.5 CenterZ=0 NormalX=0 NormalY=0 NormalZ=1 AngleXU=0 Radius=1.5 StartAngle=6e-16 EndAngle=3.14159
    g1: ArcOfCircle CenterX=-34.2 CenterY=-10.5 CenterZ=0 NormalX=0 NormalY=0 NormalZ=1 AngleXU=0 Radius=1.5 StartAngle=0 EndAngle=3.14159
    g2: ArcOfCircle CenterX=-34.2 CenterY=-27.7 CenterZ=0 NormalX=0 NormalY=0 NormalZ=1 AngleXU=0 Radius=1.5 StartAngle=3.14159 EndAngle=6.28319
    g3: ArcOfCircle CenterX=-4 CenterY=-27.7 CenterZ=0 NormalX=0 NormalY=0 NormalZ=1 AngleXU=0 Radius=1.5 StartAngle=3.1416 EndAngle=6.28319
    g4: ArcOfCircle CenterX=-10 CenterY=-4.3 CenterZ=0 NormalX=0 NormalY=0 NormalZ=1 AngleXU=0 Radius=1.5 StartAngle=2e-16 EndAngle=3.14159
    g5: ArcOfCircle CenterX=-16.1 CenterY=-1.8 CenterZ=0 NormalX=0 NormalY=0 NormalZ=1 AngleXU=0 Radius=1.5 StartAngle=5e-16 EndAngle=3.14159
    g6: ArcOfCircle CenterX=-22.1 CenterY=-1.8 CenterZ=0 NormalX=0 NormalY=0 NormalZ=1 AngleXU=0 Radius=1.5 StartAngle=5e-16 EndAngle=3.14159
    g7: ArcOfCircle CenterX=-28.2 CenterY=-4.3 CenterZ=0 NormalX=0 NormalY=0 NormalZ=1 AngleXU=0 Radius=1.5 StartAngle=2e-16 EndAngle=3.14159
    g8: ArcOfCircle CenterX=-10 CenterY=-33.9 CenterZ=0 NormalX=0 NormalY=0 NormalZ=1 AngleXU=0 Radius=1.5 StartAngle=3.14159 EndAngle=6.28319
    g9: ArcOfCircle CenterX=-16.1 CenterY=-36.4 CenterZ=0 NormalX=0 NormalY=0 NormalZ=1 AngleXU=0 Radius=1.5 StartAngle=3.14159 EndAngle=6.28319
    g10: ArcOfCircle CenterX=-22.1 CenterY=-36.4 CenterZ=0 NormalX=0 NormalY=0 NormalZ=1 AngleXU=0 Radius=1.5 StartAngle=3.14159 EndAngle=6.28319
    g11: ArcOfCircle CenterX=-28.2 CenterY=-33.9 CenterZ=0 NormalX=0 NormalY=0 NormalZ=1 AngleXU=0 Radius=1.5 StartAngle=3.14159 EndAngle=6.28319
    g12: LineSegment StartX=-35.7 StartY=-10.5 StartZ=0 EndX=-35.7 EndY=-27.7 EndZ=0
    g13: LineSegment StartX=-32.7 StartY=-10.5 StartZ=0 EndX=-32.7 EndY=-27.7 EndZ=0
    g14: LineSegment StartX=-29.7 StartY=-33.9 StartZ=0 EndX=-29.7 EndY=-4.3 EndZ=0
    g15: LineSegment StartX=-26.7 StartY=-33.9 StartZ=0 EndX=-26.7 EndY=-4.3 EndZ=0
    g16: LineSegment StartX=-2.5 StartY=-10.5 StartZ=0 EndX=-2.5 EndY=-27.7 EndZ=0
    g17: LineSegment StartX=-8.5 StartY=-4.3 StartZ=0 EndX=-8.5 EndY=-33.9 EndZ=0
    g18: LineSegment StartX=-5.5 StartY=-10.5 StartZ=0 EndX=-5.5 EndY=-27.7 EndZ=0
    g19: LineSegment StartX=-11.5 StartY=-4.3 StartZ=0 EndX=-11.5 EndY=-33.9 EndZ=0
    g20: LineSegment StartX=-14.6 StartY=-1.8 StartZ=0 EndX=-14.6 EndY=-36.4 EndZ=0
    g21: LineSegment StartX=-17.6 StartY=-1.8 StartZ=0 EndX=-17.6 EndY=-36.4 EndZ=0
    g22: LineSegment StartX=-20.6 StartY=-36.4 StartZ=0 EndX=-20.6 EndY=-1.8 EndZ=0
    g23: LineSegment StartX=-23.6 StartY=-1.8 StartZ=0 EndX=-23.6 EndY=-36.4 EndZ=0
  constraints (48):
    c: Block(g0)
    c: Block(g1)
    c: Block(g2)
    c: Block(g3)
    c: Block(g4)
    c: Block(g5)
    c: Block(g6)
    c: Block(g7)
    c: Block(g8)
    c: Block(g9)
    c: Block(g10)
    c: Block(g11)
    c: Coincident(g12,g1)
    c: Coincident(g12,g2)
    c: Vertical(g12)
    c: Coincident(g13,g1)
    c: Coincident(g13,g2)
    c: Vertical(g13)
    c: Coincident(g14,g11)
    c: Coincident(g14,g7)
    c: Vertical(g14)
    c: Coincident(g15,g11)
    c: Coincident(g15,g7)
    c: Vertical(g15)
    c: Coincident(g16,g0)
    c: Coincident(g16,g3)
    c: Vertical(g16)
    c: Coincident(g17,g4)
    c: Coincident(g17,g8)
    c: Vertical(g17)
    c: Coincident(g18,g0)
    c: Coincident(g18,g3)
    c: Vertical(g18)
    c: Coincident(g19,g4)
    c: Coincident(g19,g8)
    c: Vertical(g19)
    c: Coincident(g20,g5)
    c: Coincident(g20,g9)
    c: Vertical(g20)
    c: Coincident(g21,g5)
    c: Coincident(g21,g9)
    c: Vertical(g21)
    c: Coincident(g22,g10)
    c: Coincident(g22,g6)
    c: Vertical(g22)
    c: Coincident(g23,g6)
    c: Coincident(g23,g10)
    c: Vertical(g23)
FEATURE [Part::Extrusion] Extrude038  label="removeToCreateFanGrillHoles001"
  Base = -> Sketch047
  Dir = (0,-1,6e-16)
  DirMode = 2
  FaceMakerClass = Part::FaceMakerBullseye
  LengthFwd = 10
  LengthRev = 0
  Placement = pos=(65.4,44,54.82) rot=(0,0,1;0rad)
  Solid = true
  Symmetric = false
FEATURE [Part::Feature] Wire004
  shape: bbox 11 x 5.2 x 2e-07 mm, 0 faces, 0 solids (baked)
FEATURE [Part::Revolution] Revolve095
  Angle = 360
  Axis = (0,1,0)
  Base = (0,0,0)
  FaceMakerClass = Part::FaceMakerBullseye
  Placement = pos=(30.3,38,19.7) rot=(0,0,1;0rad)
  Solid = true
  Source = -> Wire004
  Symmetric = false
FEATURE [Part::Feature] Wire005
  shape: bbox 11 x 5.2 x 2e-07 mm, 0 faces, 0 solids (baked)
FEATURE [Part::Revolution] Revolve096
  Angle = 360
  Axis = (0,1,0)
  Base = (0,0,0)
  FaceMakerClass = Part::FaceMakerBullseye
  Placement = pos=(30.3,38,51.7) rot=(0,0,1;0rad)
  Solid = true
  Source = -> Wire005
  Symmetric = false
FEATURE [Part::Feature] Wire006
  shape: bbox 11 x 5.2 x 2e-07 mm, 0 faces, 0 solids (baked)
FEATURE [Part::Revolution] Revolve097
  Angle = 360
  Axis = (0,1,0)
  Base = (0,0,0)
  FaceMakerClass = Part::FaceMakerBullseye
  Placement = pos=(62.3,38,51.7) rot=(0,0,1;0rad)
  Solid = true
  Source = -> Wire006
  Symmetric = false
FEATURE [Part::Feature] Wire007
  shape: bbox 11 x 5.2 x 2e-07 mm, 0 faces, 0 solids (baked)
FEATURE [Part::Revolution] Revolve098
  Angle = 360
  Axis = (0,1,0)
  Base = (0,0,0)
  FaceMakerClass = Part::FaceMakerBullseye
  Placement = pos=(62.3,38,19.7) rot=(0,0,1;0rad)
  Solid = true
  Source = -> Wire007
  Symmetric = false
FEATURE [Part::MultiFuse] Fusion067  label="fanScrewHousing002"
  Shapes = -> [Revolve098,Revolve097,Revolve096,Revolve095]
FEATURE [Part::Feature] Face091 .. Face094  x4 (patterned run collapsed; names and placements below)
  shape: bbox 3.5 x 17.8 x 2e-07 mm, 1 faces, 0 solids (baked)
FEATURE [Part::Revolution] Revolve099  label="removeToCreateScrewAndThreadedInsertHole026"
  Angle = 360
  Axis = (0,1,0)
  Base = (0,0,0)
  FaceMakerClass = Part::FaceMakerBullseye
  Placement = pos=(62.3,30.3,19.7) rot=(0,0,1;0rad)
  Solid = false
  Source = -> Face091
  Symmetric = false
FEATURE [Part::Revolution] Revolve100  label="removeToCreateScrewAndThreadedInsertHole027"
  Angle = 360
  Axis = (0,1,0)
  Base = (0,0,0)
  FaceMakerClass = Part::FaceMakerBullseye
  Placement = pos=(62.3,30.3,51.7) rot=(0,0,1;0rad)
  Solid = false
  Source = -> Face092
  Symmetric = false
FEATURE [Part::Revolution] Revolve101  label="removeToCreateScrewAndThreadedInsertHole028"
  Angle = 360
  Axis = (0,1,0)
  Base = (0,0,0)
  FaceMakerClass = Part::FaceMakerBullseye
  Placement = pos=(30.3,30.3,19.7) rot=(0,0,1;0rad)
  Solid = false
  Source = -> Face093
  Symmetric = false
FEATURE [Part::Revolution] Revolve102  label="removeToCreateScrewAndThreadedInsertHole029"
  Angle = 360
  Axis = (0,1,0)
  Base = (0,0,0)
  FaceMakerClass = Part::FaceMakerBullseye
  Placement = pos=(30.3,30.3,51.7) rot=(0,0,1;0rad)
  Solid = false
  Source = -> Face094
  Symmetric = false
FEATURE [Part::MultiFuse] Fusion068  label="createThreadedInsertHolesForFan002"
  Shapes = -> [Revolve099,Revolve100,Revolve101,Revolve102]
FEATURE [Part::Cut] Cut026  label="fanScrewHousing003"
  Base = -> Fusion067
  Tool = -> Fusion068
FEATURE [Sketcher::SketchObject] Sketch048
  FullyConstrained = false
  Placement = pos=(0,0,0) rot=(1,0,0;1.5708rad)
  sketch-geometry (24):
    g0: ArcOfCircle CenterX=-4 CenterY=-10.5 CenterZ=0 NormalX=0 NormalY=0 NormalZ=1 AngleXU=0 Radius=1.5 StartAngle=6e-16 EndAngle=3.14159
    g1: ArcOfCircle CenterX=-34.2 CenterY=-10.5 CenterZ=0 NormalX=0 NormalY=0 NormalZ=1 AngleXU=0 Radius=1.5 StartAngle=0 EndAngle=3.14159
    g2: ArcOfCircle CenterX=-34.2 CenterY=-27.7 CenterZ=0 NormalX=0 NormalY=0 NormalZ=1 AngleXU=0 Radius=1.5 StartAngle=3.14159 EndAngle=6.28319
    g3: ArcOfCircle CenterX=-4 CenterY=-27.7 CenterZ=0 NormalX=0 NormalY=0 NormalZ=1 AngleXU=0 Radius=1.5 StartAngle=3.1416 EndAngle=6.28319
    g4: ArcOfCircle CenterX=-10 CenterY=-4.3 CenterZ=0 NormalX=0 NormalY=0 NormalZ=1 AngleXU=0 Radius=1.5 StartAngle=2e-16 EndAngle=3.14159
    g5: ArcOfCircle CenterX=-16.1 CenterY=-1.8 CenterZ=0 NormalX=0 NormalY=0 NormalZ=1 AngleXU=0 Radius=1.5 StartAngle=5e-16 EndAngle=3.14159
    g6: ArcOfCircle CenterX=-22.1 CenterY=-1.8 CenterZ=0 NormalX=0 NormalY=0 NormalZ=1 AngleXU=0 Radius=1.5 StartAngle=5e-16 EndAngle=3.14159
    g7: ArcOfCircle CenterX=-28.2 CenterY=-4.3 CenterZ=0 NormalX=0 NormalY=0 NormalZ=1 AngleXU=0 Radius=1.5 StartAngle=2e-16 EndAngle=3.14159
    g8: ArcOfCircle CenterX=-10 CenterY=-33.9 CenterZ=0 NormalX=0 NormalY=0 NormalZ=1 AngleXU=0 Radius=1.5 StartAngle=3.14159 EndAngle=6.28319
    g9: ArcOfCircle CenterX=-16.1 CenterY=-36.4 CenterZ=0 NormalX=0 NormalY=0 NormalZ=1 AngleXU=0 Radius=1.5 StartAngle=3.14159 EndAngle=6.28319
    g10: ArcOfCircle CenterX=-22.1 CenterY=-36.4 CenterZ=0 NormalX=0 NormalY=0 NormalZ=1 AngleXU=0 Radius=1.5 StartAngle=3.14159 EndAngle=6.28319
    g11: ArcOfCircle CenterX=-28.2 CenterY=-33.9 CenterZ=0 NormalX=0 NormalY=0 NormalZ=1 AngleXU=0 Radius=1.5 StartAngle=3.14159 EndAngle=6.28319
    g12: LineSegment StartX=-35.7 StartY=-10.5 StartZ=0 EndX=-35.7 EndY=-27.7 EndZ=0
    g13: LineSegment StartX=-32.7 StartY=-10.5 StartZ=0 EndX=-32.7 EndY=-27.7 EndZ=0
    g14: LineSegment StartX=-29.7 StartY=-33.9 StartZ=0 EndX=-29.7 EndY=-4.3 EndZ=0
    g15: LineSegment StartX=-26.7 StartY=-33.9 StartZ=0 EndX=-26.7 EndY=-4.3 EndZ=0
    g16: LineSegment StartX=-2.5 StartY=-10.5 StartZ=0 EndX=-2.5 EndY=-27.7 EndZ=0
    g17: LineSegment StartX=-8.5 StartY=-4.3 StartZ=0 EndX=-8.5 EndY=-33.9 EndZ=0
    g18: LineSegment StartX=-5.5 StartY=-10.5 StartZ=0 EndX=-5.5 EndY=-27.7 EndZ=0
    g19: LineSegment StartX=-11.5 StartY=-4.3 StartZ=0 EndX=-11.5 EndY=-33.9 EndZ=0
    g20: LineSegment StartX=-14.6 StartY=-1.8 StartZ=0 EndX=-14.6 EndY=-36.4 EndZ=0
    g21: LineSegment StartX=-17.6 StartY=-1.8 StartZ=0 EndX=-17.6 EndY=-36.4 EndZ=0
    g22: LineSegment StartX=-20.6 StartY=-36.4 StartZ=0 EndX=-20.6 EndY=-1.8 EndZ=0
    g23: LineSegment StartX=-23.6 StartY=-1.8 StartZ=0 EndX=-23.6 EndY=-36.4 EndZ=0
  constraints (48):
    c: Block(g0)
    c: Block(g1)
    c: Block(g2)
    c: Block(g3)
    c: Block(g4)
    c: Block(g5)
    c: Block(g6)
    c: Block(g7)
    c: Block(g8)
    c: Block(g9)
    c: Block(g10)
    c: Block(g11)
    c: Coincident(g12,g1)
    c: Coincident(g12,g2)
    c: Vertical(g12)
    c: Coincident(g13,g1)
    c: Coincident(g13,g2)
    c: Vertical(g13)
    c: Coincident(g14,g11)
    c: Coincident(g14,g7)
    c: Vertical(g14)
    c: Coincident(g15,g11)
    c: Coincident(g15,g7)
    c: Vertical(g15)
    c: Coincident(g16,g0)
    c: Coincident(g16,g3)
    c: Vertical(g16)
    c: Coincident(g17,g4)
    c: Coincident(g17,g8)
    c: Vertical(g17)
    c: Coincident(g18,g0)
    c: Coincident(g18,g3)
    c: Vertical(g18)
    c: Coincident(g19,g4)
    c: Coincident(g19,g8)
    c: Vertical(g19)
    c: Coincident(g20,g5)
    c: Coincident(g20,g9)
    c: Vertical(g20)
    c: Coincident(g21,g5)
    c: Coincident(g21,g9)
    c: Vertical(g21)
    c: Coincident(g22,g10)
    c: Coincident(g22,g6)
    c: Vertical(g22)
    c: Coincident(g23,g6)
    c: Coincident(g23,g10)
    c: Vertical(g23)
FEATURE [Part::Extrusion] Extrude039  label="removeToCreateFanGrillHoles002"
  Base = -> Sketch048
  Dir = (0,-1,6e-16)
  DirMode = 2
  FaceMakerClass = Part::FaceMakerBullseye
  LengthFwd = 10
  LengthRev = 0
  Placement = pos=(65.4,44,54.82) rot=(0,0,1;0rad)
  Solid = true
  Symmetric = false
FEATURE [Part::Cut] Cut027  label="fanScrewHousing004"
  Base = -> Cut026
  Tool = -> Extrude038
FEATURE [Part::Cut] Cut028  label="top014"
  Base = -> Fillet026
  Tool = -> Extrude039
FEATURE [Part::Feature] Face095 .. Face098  x4 (patterned run collapsed; names and placements below)
  shape: bbox 3.5 x 17.8 x 2e-07 mm, 1 faces, 0 solids (baked)
FEATURE [Part::Revolution] Revolve103  label="removeToCreateScrewAndThreadedInsertHole030"
  Angle = 360
  Axis = (0,1,0)
  Base = (0,0,0)
  FaceMakerClass = Part::FaceMakerBullseye
  Placement = pos=(62.3,30.3,19.7) rot=(0,0,1;0rad)
  Solid = false
  Source = -> Face095
  Symmetric = false
FEATURE [Part::Revolution] Revolve104  label="removeToCreateScrewAndThreadedInsertHole031"
  Angle = 360
  Axis = (0,1,0)
  Base = (0,0,0)
  FaceMakerClass = Part::FaceMakerBullseye
  Placement = pos=(62.3,30.3,51.7) rot=(0,0,1;0rad)
  Solid = false
  Source = -> Face096
  Symmetric = false
FEATURE [Part::Revolution] Revolve105  label="removeToCreateScrewAndThreadedInsertHole032"
  Angle = 360
  Axis = (0,1,0)
  Base = (0,0,0)
  FaceMakerClass = Part::FaceMakerBullseye
  Placement = pos=(30.3,30.3,19.7) rot=(0,0,1;0rad)
  Solid = false
  Source = -> Face097
  Symmetric = false
FEATURE [Part::Revolution] Revolve106  label="removeToCreateScrewAndThreadedInsertHole033"
  Angle = 360
  Axis = (0,1,0)
  Base = (0,0,0)
  FaceMakerClass = Part::FaceMakerBullseye
  Placement = pos=(30.3,30.3,51.7) rot=(0,0,1;0rad)
  Solid = false
  Source = -> Face098
  Symmetric = false
FEATURE [Part::MultiFuse] Fusion069  label="createThreadedInsertHolesForFan003"
  Shapes = -> [Revolve103,Revolve104,Revolve105,Revolve106]
FEATURE [Part::Cut] Cut029  label="top015"
  Base = -> Cut028
  Tool = -> Fusion054
FEATURE [Part::Cut] Cut030  label="fanScrewHousing005"
  Base = -> Cut027
  Tool = -> Fusion069
FEATURE [Part::Cylinder] Cylinder026  label="removeToCreteHoleForPlugHousing010"
  Angle = 360
  AttacherType = Attacher::AttachEngine3D
  Height = 20
  Placement = pos=(-2,19,36) rot=(0,1,0;1.5708rad)
  Radius = 14.3
FEATURE [Part::Box] Box018  label="removeToCreteHoleForPlugHousing011"
  AttacherType = Attacher::AttachEngine3D
  Height = 28.6
  Length = 10
  Placement = pos=(-2,0,21.7) rot=(0,0,1;0rad)
  Width = 19
FEATURE [Part::Box] Box019  label="wireHolderBottomCaseBit"
  AttacherType = Attacher::AttachEngine3D
  Height = 28
  Length = 3
  Placement = pos=(0,0,22) rot=(0,0,1;0rad)
  Width = 21
FEATURE [Part::Cylinder] Cylinder027  label="removeToCreteHoleForPlugHousing012"
  Angle = 360
  AttacherType = Attacher::AttachEngine3D
  Height = 20
  Placement = pos=(-2,19,36) rot=(0,1,0;1.5708rad)
  Radius = 14.3
FEATURE [Part::Cut] Cut031  label="wireHolderBottomCaseBit001"
  Base = -> Box019
  Tool = -> Cylinder027
FEATURE [Part::MultiFuse] Fusion070  label="removeToCreteHoleForPlugHousing013"
  Shapes = -> [Box018,Cylinder026]
FEATURE [Part::Cut] Cut032  label="top016"
  Base = -> Cut029
  Tool = -> Fusion070
FEATURE [Part::Cylinder] Cylinder028
  Angle = 360
  AttacherType = Attacher::AttachEngine3D
  Height = 20
  Placement = pos=(0,0,36.15) rot=(0,0,1;0rad)
  Radius = 14.3
FEATURE [Part::Cylinder] Cylinder029
  Angle = 360
  AttacherType = Attacher::AttachEngine3D
  Height = 10
  Placement = pos=(0,0,36.15) rot=(0,0,1;0rad)
  Radius = 4
FEATURE [Part::MultiFuse] Fusion071  label="removeToCreteHoleForPlugHousing014"
  Placement = pos=(70,19,36) rot=(0,1,0;1.5708rad)
  Shapes = -> [Cylinder028,Cylinder029]
FEATURE [Sketcher::SketchObject] Sketch049  label="topSketch011"
  FullyConstrained = true
  sketch-geometry (4):
    g0: ArcOfCircle CenterX=105 CenterY=19 CenterZ=0 NormalX=0 NormalY=0 NormalZ=1 AngleXU=0 Radius=20.6155 StartAngle=5.54125 EndAngle=6.28319
    g1: ArcOfCircle CenterX=105 CenterY=19 CenterZ=0 NormalX=0 NormalY=0 NormalZ=1 AngleXU=0 Radius=13 StartAngle=5.54125 EndAngle=6.28319
    g2: LineSegment StartX=118 StartY=19 StartZ=0 EndX=125.616 EndY=19 EndZ=0
    g3: LineSegment StartX=114.583 StartY=10.2157 StartZ=0 EndX=120.197 EndY=5.06982 EndZ=0
  constraints (7):
    c: Block(g0)
    c: Block(g1)
    c: Coincident(g2,g1)
    c: Coincident(g2,g0)
    c: Horizontal(g2)
    c: Coincident(g3,g1)
    c: Coincident(g3,g0)
FEATURE [Part::Box] Box020  label="removeToCreteHoleForPlugHousing015"
  AttacherType = Attacher::AttachEngine3D
  Height = 28.6
  Length = 20
  Placement = pos=(106.15,0,21.7) rot=(0,0,1;0rad)
  Width = 19
FEATURE [Part::MultiFuse] Fusion072  label="removeToCreteHoleForPlugHousing016"
  Shapes = -> [Box020,Fusion071]
FEATURE [Part::Cut] Cut033  label="removeToCreteHoleForPlugHousing017"
  Base = -> Cut032
  Tool = -> Fusion072
FEATURE [Part::Cylinder] Cylinder030
  Angle = 360
  AttacherType = Attacher::AttachEngine3D
  Height = 20
  Placement = pos=(0,0,36.15) rot=(0,0,1;0rad)
  Radius = 14.3
FEATURE [Part::Cylinder] Cylinder031
  Angle = 360
  AttacherType = Attacher::AttachEngine3D
  Height = 10
  Placement = pos=(0,0,36.15) rot=(0,0,1;0rad)
  Radius = 4
FEATURE [Part::Box] Box021  label="removeToCreteHoleForPlugHousing019"
  AttacherType = Attacher::AttachEngine3D
  Height = 28.6
  Length = 20
  Placement = pos=(106.15,0,21.7) rot=(0,0,1;0rad)
  Width = 19
FEATURE [Part::MultiFuse] Fusion074  label="removeToCreteHoleForPlugHousing020"
  Placement = pos=(70,19,36) rot=(0,1,0;1.5708rad)
  Shapes = -> [Cylinder030,Cylinder031]
FEATURE [Part::MultiFuse] Fusion073  label="removeToCreteHoleForPlugHousing018"
  Placement = pos=(0,0,28.3) rot=(0,0,1;0rad)
  Shapes = -> [Box021,Fusion074]
FEATURE [Part::Cylinder] Cylinder032
  Angle = 360
  AttacherType = Attacher::AttachEngine3D
  Height = 20
  Placement = pos=(0,0,36.15) rot=(0,0,1;0rad)
  Radius = 14.3
FEATURE [Part::Cylinder] Cylinder033
  Angle = 360
  AttacherType = Attacher::AttachEngine3D
  Height = 10
  Placement = pos=(0,0,36.15) rot=(0,0,1;0rad)
  Radius = 4
FEATURE [Part::Box] Box022  label="removeToCreteHoleForPlugHousing021"
  AttacherType = Attacher::AttachEngine3D
  Height = 28.6
  Length = 20
  Placement = pos=(106.15,0,21.7) rot=(0,0,1;0rad)
  Width = 19
FEATURE [Part::MultiFuse] Fusion076  label="removeToCreteHoleForPlugHousing023"
  Placement = pos=(70,19,36) rot=(0,1,0;1.5708rad)
  Shapes = -> [Cylinder032,Cylinder033]
FEATURE [Part::MultiFuse] Fusion075  label="removeToCreteHoleForPlugHousing022"
  Placement = pos=(0,0,-28.3) rot=(0,0,1;0rad)
  Shapes = -> [Box022,Fusion076]
FEATURE [Part::MultiFuse] Fusion077  label="removeToCreatePlugHousingBottomBit"
  Shapes = -> [Fusion075,Fusion073]
FEATURE [Part::Cylinder] Cylinder034
  Angle = 360
  AttacherType = Attacher::AttachEngine3D
  Height = 20
  Placement = pos=(0,0,36.15) rot=(0,0,1;0rad)
  Radius = 14
FEATURE [Part::Cylinder] Cylinder035
  Angle = 360
  AttacherType = Attacher::AttachEngine3D
  Height = 10
  Placement = pos=(0,0,36.15) rot=(0,0,1;0rad)
  Radius = 4
FEATURE [Part::MultiFuse] Fusion078  label="removeToCreteHoleForPlugHousing024"
  Placement = pos=(70,19,36) rot=(0,1,0;1.5708rad)
  Shapes = -> [Cylinder034,Cylinder035]
FEATURE [Part::MultiFuse] Fusion079  label="removeToCreatePlugHousingBottomBit001"
  Shapes = -> [Fusion078,Fusion077]
FEATURE [Part::Extrusion] Extrude040  label="bottomPlugHousingBit"
  Base = -> Sketch049
  Dir = (0,0,1)
  DirMode = 2
  FaceMakerClass = Part::FaceMakerBullseye
  LengthFwd = 72
  LengthRev = 0
  Solid = true
  Symmetric = false
FEATURE [Part::Cut] Cut034  label="bottomPlugHousingBit001"
  Base = -> Extrude040
  Placement = pos=(-0.09,0,0) rot=(0,0,1;0rad)
  Tool = -> Fusion079
FEATURE [Part::Box] Box023  label="Cube014"
  AttacherType = Attacher::AttachEngine3D
  Height = 16
  Length = 8
  Placement = pos=(12.7,31.52,28) rot=(0,0,1;0rad)
  Width = 4
FEATURE [Part::Cylinder] Cylinder036
  Angle = 360
  AttacherType = Attacher::AttachEngine3D
  Height = 10
  Placement = pos=(0,0,36.15) rot=(0,0,1;0rad)
  Radius = 4
FEATURE [Part::Cylinder] Cylinder037
  Angle = 360
  AttacherType = Attacher::AttachEngine3D
  Height = 20
  Placement = pos=(0,0,36.15) rot=(0,0,1;0rad)
  Radius = 8.2
FEATURE [Part::MultiFuse] Fusion080  label="removeToCreteHoleForPlugHousing025"
  Placement = pos=(-42,19,36) rot=(0,1,0;1.5708rad)
  Shapes = -> [Cylinder037,Cylinder036]
FEATURE [Sketcher::SketchObject] Sketch050  label="topSketch012"
  FullyConstrained = true
  sketch-geometry (4):
    g0: LineSegment StartX=16.8446 StartY=31.512 StartZ=0 EndX=16.3251 EndY=34.4666 EndZ=0
    g1: ArcOfCircle CenterX=19 CenterY=19.2524 CenterZ=0 NormalX=0 NormalY=0 NormalZ=1 AngleXU=0 Radius=15.4476 StartAngle=1.74483 EndAngle=2.72717
    g2: ArcOfCircle CenterX=19 CenterY=19.2524 CenterZ=0 NormalX=0 NormalY=0 NormalZ=1 AngleXU=0 Radius=12.4476 StartAngle=1.74483 EndAngle=2.73189
    g3: LineSegment StartX=4.86004 StartY=25.4725 StartZ=0 EndX=7.58253 EndY=24.2107 EndZ=0
  constraints (7):
    c: Block(g0)
    c: Coincident(g1,g0)
    c: Coincident(g2,g0)
    c: Coincident(g3,g1)
    c: Coincident(g3,g2)
    c: Block(g1)
    c: Block(g2)
FEATURE [Part::Extrusion] Extrude041
  Base = -> Sketch050
  Dir = (0,0,1)
  DirMode = 2
  FaceMakerClass = Part::FaceMakerBullseye
  LengthFwd = 10.6
  LengthRev = 0
  Placement = pos=(0,0,31) rot=(0,0,1;0rad)
  Solid = true
  Symmetric = false
FEATURE [Part::Cut] Cut035
  Base = -> Extrude041
  Placement = pos=(0,0,-0.3) rot=(0,0,1;0rad)
  Tool = -> Fusion080
FEATURE [Part::Cut] Cut036
  Base = -> Box023
  Tool = -> Cut035
FEATURE [Part::Fillet] Fillet027
  Base = -> Cut036
  Edges = 1 edges r=0.7: [Edge13]
FEATURE [Part::Fillet] Fillet028
  Base = -> Fillet027
  Edges = 1 edges r=0.7: [Edge13]
FEATURE [Part::Fillet] Fillet029
  Base = -> Fillet028
  Edges = 1 edges r=0.7: [Edge16]
FEATURE [Part::Fillet] Fillet030
  Base = -> Fillet029
  Edges = 1 edges r=0.7: [Edge11]
FEATURE [Part::Fillet] Fillet031
  Base = -> Fillet030
  Edges = 1 edges r=0.7: [Edge10]
FEATURE [Part::Fillet] Fillet032
  Base = -> Fillet031
  Edges = 1 edges r=1.2: [Edge5]
FEATURE [Part::Fillet] Fillet033
  Base = -> Fillet032
  Edges = 1 edges r=1.2: [Edge12]
FEATURE [Part::Fillet] Fillet034  label="wireHousingRetainer"
  Base = -> Fillet033
  Edges = 1 edges r=2: [Edge1]
  Placement = pos=(0.3,0,0) rot=(0,0,1;0rad)
FEATURE [Part::Feature] Face099
  shape: bbox 3.5 x 17.8 x 2e-07 mm, 1 faces, 0 solids (baked)
FEATURE [Part::Revolution] Revolve107  label="removeToCreateScrewAndThreadedInsertHole034"
  Angle = 360
  Axis = (0,1,0)
  Base = (0,0,0)
  FaceMakerClass = Part::FaceMakerBullseye
  Placement = pos=(12.5,0,10) rot=(0,0,1;0rad)
  Solid = false
  Source = -> Face099
  Symmetric = false
FEATURE [Part::Feature] Face100
  shape: bbox 3.5 x 17.8 x 2e-07 mm, 1 faces, 0 solids (baked)
FEATURE [Part::Revolution] Revolve108  label="removeToCreateScrewAndThreadedInsertHole035"
  Angle = 360
  Axis = (0,1,0)
  Base = (0,0,0)
  FaceMakerClass = Part::FaceMakerBullseye
  Placement = pos=(12.5,0,62) rot=(0,0,1;0rad)
  Solid = false
  Source = -> Face100
  Symmetric = false
FEATURE [Part::Feature] Face101
  shape: bbox 3.5 x 17.8 x 2e-07 mm, 1 faces, 0 solids (baked)
FEATURE [Part::Revolution] Revolve109  label="removeToCreateScrewAndThreadedInsertHole036"
  Angle = 360
  Axis = (0,1,0)
  Base = (0,0,0)
  FaceMakerClass = Part::FaceMakerBullseye
  Placement = pos=(89.5,0,68.5) rot=(0,0,1;0rad)
  Solid = false
  Source = -> Face101
  Symmetric = false
FEATURE [Part::Feature] Face102
  shape: bbox 3.5 x 17.8 x 2e-07 mm, 1 faces, 0 solids (baked)
FEATURE [Part::Revolution] Revolve110  label="removeToCreateScrewAndThreadedInsertHole037"
  Angle = 360
  Axis = (0,1,0)
  Base = (0,0,0)
  FaceMakerClass = Part::FaceMakerBullseye
  Placement = pos=(89.5,0,3.5) rot=(0,0,1;0rad)
  Solid = false
  Source = -> Face102
  Symmetric = false
FEATURE [Part::Feature] Face103
  shape: bbox 3.5 x 17.8 x 2e-07 mm, 1 faces, 0 solids (baked)
FEATURE [Part::Revolution] Revolve111  label="removeToCreateScrewAndThreadedInsertHole038"
  Angle = 360
  Axis = (0,1,0)
  Base = (0,0,0)
  FaceMakerClass = Part::FaceMakerBullseye
  Placement = pos=(109.5,4.7,3.5) rot=(0,0,1;0rad)
  Solid = false
  Source = -> Face103
  Symmetric = false
FEATURE [Part::Feature] Face104
  shape: bbox 3.5 x 17.8 x 2e-07 mm, 1 faces, 0 solids (baked)
FEATURE [Part::Revolution] Revolve112  label="removeToCreateScrewAndThreadedInsertHole039"
  Angle = 360
  Axis = (0,1,0)
  Base = (0,0,0)
  FaceMakerClass = Part::FaceMakerBullseye
  Placement = pos=(109.5,4.7,68.5) rot=(0,0,1;0rad)
  Solid = false
  Source = -> Face104
  Symmetric = false
FEATURE [Part::MultiFuse] Fusion081  label="removeToCreateScrewAndThreadedInsertHole040"
  Shapes = -> [Revolve107,Revolve108,Revolve109,Revolve110,Revolve111,Revolve112]
FEATURE [Part::MultiFuse] Fusion082  label="casePillars002"
  Shapes = -> [Revolve094,Revolve092,Revolve090,Revolve089,Revolve091,Revolve093]
FEATURE [Part::Cut] Cut037  label="casePillars003"
  Base = -> Fusion082
  Tool = -> Fusion081
FEATURE [Sketcher::SketchObject] Sketch051
  FullyConstrained = true
  Placement = pos=(117,19,0) rot=(0.57735,0.57735,0.57735;2.0944rad)
  sketch-geometry (48):
    g0: LineSegment StartX=-49.19 StartY=69.25 StartZ=0 EndX=-49.19 EndY=66.25 EndZ=0
    g1: LineSegment StartX=-49.19 StartY=63.5 StartZ=0 EndX=-49.19 EndY=60.5 EndZ=0
    g2: LineSegment StartX=-49.19 StartY=57.75 StartZ=0 EndX=-49.19 EndY=54.75 EndZ=0
    g3: LineSegment StartX=-49.19 StartY=52 StartZ=0 EndX=-49.19 EndY=49 EndZ=0
    g4: LineSegment StartX=-49.19 StartY=46.25 StartZ=0 EndX=-49.19 EndY=43.25 EndZ=0
    g5: LineSegment StartX=-49.19 StartY=40.5 StartZ=0 EndX=-49.19 EndY=37.5 EndZ=0
    g6: LineSegment StartX=-49.19 StartY=34.5 StartZ=0 EndX=-49.19 EndY=31.5 EndZ=0
    g7: LineSegment StartX=-49.19 StartY=28.75 StartZ=0 EndX=-49.19 EndY=25.75 EndZ=0
    g8: LineSegment StartX=-49.19 StartY=23 StartZ=0 EndX=-49.19 EndY=20 EndZ=0
    g9: LineSegment StartX=-49.19 StartY=17.25 StartZ=0 EndX=-49.19 EndY=14.25 EndZ=0
    g10: LineSegment StartX=-49.19 StartY=11.5 StartZ=0 EndX=-49.19 EndY=8.5 EndZ=0
    g11: LineSegment StartX=-49.19 StartY=5.75 StartZ=0 EndX=-49.19 EndY=2.75 EndZ=0
    g12: ArcOfCircle CenterX=-1.5 CenterY=67.75 CenterZ=0 NormalX=0 NormalY=0 NormalZ=1 AngleXU=0 Radius=1.5 StartAngle=4.71239 EndAngle=7.85398
    g13: ArcOfCircle CenterX=-1.5 CenterY=62 CenterZ=0 NormalX=0 NormalY=0 NormalZ=1 AngleXU=0 Radius=1.5 StartAngle=4.71239 EndAngle=7.85398
    g14: ArcOfCircle CenterX=-1.5 CenterY=56.25 CenterZ=0 NormalX=0 NormalY=0 NormalZ=1 AngleXU=0 Radius=1.5 StartAngle=4.71239 EndAngle=7.85398
    g15: ArcOfCircle CenterX=-11.49 CenterY=50.5 CenterZ=0 NormalX=0 NormalY=0 NormalZ=1 AngleXU=0 Radius=1.5 StartAngle=4.71239 EndAngle=7.85398
    g16: ArcOfCircle CenterX=-16.28 CenterY=44.75 CenterZ=0 NormalX=0 NormalY=0 NormalZ=1 AngleXU=0 Radius=1.5 StartAngle=4.71239 EndAngle=7.85398
    g17: ArcOfCircle CenterX=-18.2337 CenterY=39 CenterZ=0 NormalX=0 NormalY=0 NormalZ=1 AngleXU=0 Radius=1.5 StartAngle=4.71485 EndAngle=7.85398
    g18: ArcOfCircle CenterX=-16.2837 CenterY=27.25 CenterZ=0 NormalX=0 NormalY=0 NormalZ=1 AngleXU=0 Radius=1.5 StartAngle=4.71485 EndAngle=7.85398
    g19: ArcOfCircle CenterX=-18.2337 CenterY=33 CenterZ=0 NormalX=0 NormalY=0 NormalZ=1 AngleXU=0 Radius=1.5 StartAngle=4.71485 EndAngle=7.85398
    g20: ArcOfCircle CenterX=-11.49 CenterY=21.5 CenterZ=0 NormalX=0 NormalY=0 NormalZ=1 AngleXU=0 Radius=1.5 StartAngle=4.71239 EndAngle=7.85398
    g21: ArcOfCircle CenterX=-1.5 CenterY=4.25 CenterZ=0 NormalX=0 NormalY=0 NormalZ=1 AngleXU=0 Radius=1.5 StartAngle=4.71239 EndAngle=7.85398
    g22: ArcOfCircle CenterX=-1.5 CenterY=10 CenterZ=0 NormalX=0 NormalY=0 NormalZ=1 AngleXU=0 Radius=1.5 StartAngle=4.71239 EndAngle=7.85398
    g23: ArcOfCircle CenterX=-1.5 CenterY=15.75 CenterZ=0 NormalX=0 NormalY=0 NormalZ=1 AngleXU=0 Radius=1.5 StartAngle=4.71239 EndAngle=7.85398
    g24: LineSegment StartX=-49.19 StartY=69.25 StartZ=0 EndX=-1.5 EndY=69.25 EndZ=0
    g25: LineSegment StartX=-49.19 StartY=66.25 StartZ=0 EndX=-1.5 EndY=66.25 EndZ=0
    g26: LineSegment StartX=-49.19 StartY=63.5 StartZ=0 EndX=-1.5 EndY=63.5 EndZ=0
    g27: LineSegment StartX=-49.19 StartY=60.5 StartZ=0 EndX=-1.5 EndY=60.5 EndZ=0
    g28: LineSegment StartX=-49.19 StartY=57.75 StartZ=0 EndX=-1.5 EndY=57.75 EndZ=0
    g29: LineSegment StartX=-49.19 StartY=54.75 StartZ=0 EndX=-1.5 EndY=54.75 EndZ=0
    g30: LineSegment StartX=-49.19 StartY=52 StartZ=0 EndX=-11.49 EndY=52 EndZ=0
    g31: LineSegment StartX=-49.19 StartY=49 StartZ=0 EndX=-11.49 EndY=49 EndZ=0
    g32: LineSegment StartX=-49.19 StartY=46.25 StartZ=0 EndX=-16.28 EndY=46.25 EndZ=0
    g33: LineSegment StartX=-49.19 StartY=43.25 StartZ=0 EndX=-16.28 EndY=43.25 EndZ=0
    g34: LineSegment StartX=-49.19 StartY=40.5 StartZ=0 EndX=-18.2337 EndY=40.5 EndZ=0
    g35: LineSegment StartX=-49.19 StartY=37.5 StartZ=0 EndX=-18.23 EndY=37.5 EndZ=0
    g36: LineSegment StartX=-49.19 StartY=34.5 StartZ=0 EndX=-18.2337 EndY=34.5 EndZ=0
    g37: LineSegment StartX=-49.19 StartY=31.5 StartZ=0 EndX=-18.23 EndY=31.5 EndZ=0
    g38: LineSegment StartX=-49.19 StartY=28.75 StartZ=0 EndX=-16.2837 EndY=28.75 EndZ=0
    g39: LineSegment StartX=-49.19 StartY=25.75 StartZ=0 EndX=-16.28 EndY=25.75 EndZ=0
    g40: LineSegment StartX=-49.19 StartY=23 StartZ=0 EndX=-11.49 EndY=23 EndZ=0
    g41: LineSegment StartX=-49.19 StartY=20 StartZ=0 EndX=-11.49 EndY=20 EndZ=0
    g42: LineSegment StartX=-49.19 StartY=17.25 StartZ=0 EndX=-1.5 EndY=17.25 EndZ=0
    g43: LineSegment StartX=-49.19 StartY=14.25 StartZ=0 EndX=-1.5 EndY=14.25 EndZ=0
    g44: LineSegment StartX=-49.19 StartY=11.5 StartZ=0 EndX=-1.5 EndY=11.5 EndZ=0
    g45: LineSegment StartX=-49.19 StartY=8.5 StartZ=0 EndX=-1.5 EndY=8.5 EndZ=0
    g46: LineSegment StartX=-49.19 StartY=5.75 StartZ=0 EndX=-1.5 EndY=5.75 EndZ=0
    g47: LineSegment StartX=-49.19 StartY=2.75 StartZ=0 EndX=-1.5 EndY=2.75 EndZ=0
  constraints (120):
    c: Vertical(g0)
    c: Distance(g0) = 3
    c: Block(g0)
    c: Vertical(g1)
    c: Distance(g1) = 3
    c: Vertical(g2)
    c: Equal(g0,g2) = 3
    c: Block(g2)
    c: Vertical(g3)
    c: Equal(g1,g3) = 3
    c: Vertical(g4)
    c: Equal(g0,g4) = 3
    c: Block(g4)
    c: Vertical(g5)
    c: Equal(g1,g5) = 3
    c: Vertical(g6)
    c: Equal(g0,g6) = 3
    c: Block(g6)
    c: Vertical(g7)
    c: Equal(g1,g7) = 3
    c: Vertical(g8)
    c: Equal(g0,g8) = 3
    c: Block(g8)
    c: Vertical(g9)
    c: Equal(g1,g9) = 3
    c: Vertical(g10)
    c: Equal(g0,g10) = 3
    c: Block(g10)
    c: Vertical(g11)
    c: Equal(g1,g11) = 3
    c: Block(g12)
    c: Block(g13)
    c: Block(g14)
    c: Block(g15)
    c: Block(g16)
    c: Block(g17)
    c: Block(g18)
    c: Block(g19)
    c: Block(g20)
    c: Block(g21)
    c: Block(g22)
    c: Block(g23)
    c: Block(g11)
    c: Block(g9)
    c: Block(g7)
    c: Block(g5)
    c: Block(g3)
    c: Block(g1)
    c: Coincident(g24,g0)
    c: Coincident(g24,g12)
    c: Horizontal(g24)
    c: Coincident(g25,g0)
    c: Coincident(g25,g12)
    c: Horizontal(g25)
    c: Coincident(g26,g1)
    c: Coincident(g26,g13)
    c: Horizontal(g26)
    c: Coincident(g27,g1)
    c: Coincident(g27,g13)
    c: Horizontal(g27)
    c: Coincident(g28,g2)
    c: Coincident(g28,g14)
    c: Horizontal(g28)
    c: Coincident(g29,g2)
    c: Coincident(g29,g14)
    c: Horizontal(g29)
    c: Coincident(g30,g3)
    c: Coincident(g30,g15)
    c: Horizontal(g30)
    c: Coincident(g31,g3)
    c: Coincident(g31,g15)
    c: Horizontal(g31)
    c: Coincident(g32,g4)
    c: Coincident(g32,g16)
    c: Horizontal(g32)
    c: Coincident(g33,g4)
    c: Coincident(g33,g16)
    c: Horizontal(g33)
    c: Coincident(g34,g5)
    c: Coincident(g34,g17)
    c: Horizontal(g34)
    c: Coincident(g35,g5)
    c: Coincident(g35,g17)
    c: Horizontal(g35)
    c: Coincident(g36,g6)
    c: Coincident(g36,g19)
    c: Horizontal(g36)
    c: Coincident(g37,g6)
    c: Coincident(g37,g19)
    c: Horizontal(g37)
    c: Coincident(g38,g7)
    c: Coincident(g38,g18)
    c: Horizontal(g38)
    c: Coincident(g39,g7)
    c: Coincident(g39,g18)
    c: Horizontal(g39)
    c: Coincident(g40,g8)
    c: Coincident(g40,g20)
    c: Horizontal(g40)
    c: Coincident(g41,g8)
    c: Coincident(g41,g20)
    c: Horizontal(g41)
    c: Coincident(g42,g9)
    c: Coincident(g42,g23)
    c: Horizontal(g42)
    c: Coincident(g43,g9)
    c: Coincident(g43,g23)
    c: Horizontal(g43)
    c: Coincident(g44,g10)
    c: Coincident(g44,g22)
    c: Horizontal(g44)
    c: Coincident(g45,g10)
    c: Coincident(g45,g22)
    c: Horizontal(g45)
    c: Coincident(g46,g11)
    c: Coincident(g46,g21)
    c: Horizontal(g46)
    c: Coincident(g47,g11)
    c: Coincident(g47,g21)
    c: Horizontal(g47)
FEATURE [Part::Extrusion] Extrude042
  Base = -> Sketch051
  Dir = (1,-2e-16,2e-16)
  DirMode = 2
  FaceMakerClass = Part::FaceMakerBullseye
  LengthFwd = 19
  LengthRev = 0
  Placement = pos=(-19,0,0) rot=(0,0,1;0rad)
  Solid = true
  Symmetric = false
FEATURE [Part::Fillet] Fillet035  label="removeToCreateVentalationHoles"
  Base = -> Extrude042
  Edges = <same value as first occurrence — deduplicated (x6 in doc)>
  Placement = pos=(7,0,0) rot=(0,0,1;0rad)
FEATURE [Part::Cut] Cut038  label="top017"
  Base = -> Cut033
  Tool = -> Fillet035
FEATURE [Sketcher::SketchObject] Sketch052  label="bottomSketch001"
  FullyConstrained = true
  sketch-geometry (45):
    g0: LineSegment StartX=6.29999 StartY=8 StartZ=0 EndX=3.29999 EndY=8 EndZ=0
    g1: LineSegment StartX=3.29999 StartY=8 StartZ=0 EndX=3.29999 EndY=-6.03275e-07 EndZ=0
    g2: ArcOfCircle CenterX=8.29999 CenterY=5 CenterZ=0 NormalX=0 NormalY=0 NormalZ=1 AngleXU=0 Radius=2 StartAngle=3.14159 EndAngle=4.71239
    g3: LineSegment StartX=6.29999 StartY=8 StartZ=0 EndX=6.29999 EndY=5 EndZ=0
    g4: ArcOfCircle CenterX=105 CenterY=19 CenterZ=0 NormalX=0 NormalY=0 NormalZ=1 AngleXU=0 Radius=12.7 StartAngle=4.71239 EndAngle=5.94289
    g5-g11: Circle x7 (B-spline internal-alignment scaffolding for g12; pole/knot coordinates omitted)
    g12: BSplineCurve PolesCount=7 KnotsCount=5 Degree=3 IsPeriodic=0
    g13-g17: GeomPoint x5 (B-spline internal-alignment scaffolding for g12; pole/knot coordinates omitted)
    g18: ArcOfCircle CenterX=105 CenterY=19 CenterZ=0 NormalX=0 NormalY=0 NormalZ=1 AngleXU=0 Radius=15.7 StartAngle=5.81226 EndAngle=6.28319
    g19: BSplineCurve PolesCount=5 KnotsCount=3 Degree=3 IsPeriodic=0
    g20: LineSegment StartX=8.29999 StartY=3 StartZ=0 EndX=101.7 EndY=3 EndZ=0
    g21: LineSegment StartX=3.29999 StartY=-6.03275e-07 StartZ=0 EndX=105 EndY=-6.03275e-07 EndZ=0
    g22: LineSegment StartX=120.974 StartY=8.71251 StartZ=0 EndX=122.332 EndY=7.83778 EndZ=0
    g23: LineSegment StartX=105 StartY=-6.03274e-07 StartZ=0 EndX=113 EndY=-6.03274e-07 EndZ=0
    g24: ArcOfCircle CenterX=105 CenterY=19 CenterZ=0 NormalX=0 NormalY=0 NormalZ=1 AngleXU=0 Radius=20.6155 StartAngle=5.11091 EndAngle=5.71103
    g25: ArcOfCircle CenterX=117.7 CenterY=19 CenterZ=0 NormalX=0 NormalY=0 NormalZ=1 AngleXU=0 Radius=3 StartAngle=1.2e-15 EndAngle=2.10468
    g26: Circle CenterX=116.345 CenterY=16.3232 CenterZ=0 NormalX=0 NormalY=0 NormalZ=1 AngleXU=0 Radius=1
    g27: Circle CenterX=117.24 CenterY=15.7584 CenterZ=0 NormalX=0 NormalY=0 NormalZ=1 AngleXU=0 Radius=1
    g28: Circle CenterX=116.972 CenterY=14.7612 CenterZ=0 NormalX=0 NormalY=0 NormalZ=1 AngleXU=0 Radius=1
    g29: BSplineCurve PolesCount=3 KnotsCount=2 Degree=2 IsPeriodic=0
    g30: GeomPoint X=116.345 Y=16.3232 Z=0
    g31: GeomPoint X=116.972 Y=14.7612 Z=0
    g32: Circle CenterX=115.828 CenterY=17.157 CenterZ=0 NormalX=0 NormalY=0 NormalZ=1 AngleXU=0 Radius=1
    g33: Circle CenterX=115.841 CenterY=16.639 CenterZ=0 NormalX=0 NormalY=0 NormalZ=1 AngleXU=0 Radius=1
    g34: Circle CenterX=116.345 CenterY=16.3232 CenterZ=0 NormalX=0 NormalY=0 NormalZ=1 AngleXU=0 Radius=1
    g35: BSplineCurve PolesCount=3 KnotsCount=2 Degree=2 IsPeriodic=0
    g36: GeomPoint X=115.828 Y=17.157 Z=0
    g37: GeomPoint X=116.345 Y=16.3232 Z=0
    g38: LineSegment StartX=115.828 StartY=17.157 StartZ=0 EndX=115.828 EndY=20.8307 EndZ=0
    g39: Circle CenterX=115.828 CenterY=20.8307 CenterZ=0 NormalX=0 NormalY=0 NormalZ=1 AngleXU=0 Radius=1
    g40: Circle CenterX=115.831 CenterY=21.3396 CenterZ=0 NormalX=0 NormalY=0 NormalZ=1 AngleXU=0 Radius=1
    g41: Circle CenterX=116.173 CenterY=21.5825 CenterZ=0 NormalX=0 NormalY=0 NormalZ=1 AngleXU=0 Radius=1
    g42: BSplineCurve PolesCount=3 KnotsCount=2 Degree=2 IsPeriodic=0
    g43: GeomPoint X=115.828 Y=20.8307 Z=0
    g44: GeomPoint X=116.173 Y=21.5825 Z=0
  constraints (70):
    c: Horizontal(g0)
    c: Distance(g0) = 3
    c: Coincident(g1,g0)
    c: Vertical(g1)
    c: Block(g2)
    c: Block(g0)
    c: Coincident(g3,g0)
    c: Coincident(g3,g2)
    c: Vertical(g3)
    c: Block(g1)
    c: Block(g4)
    c: Coincident(g19,g4)
    c: Block(g19)
    c: Equal(g5, g6-g11) x6
    c: InternalAlignment(g5-g11 -> g12) x7
    c: InternalAlignment(g13-g17 -> g12) x5
    c: Block(g12)
    c: Coincident(g18,g12)
    c: Block(g18)
    c: Coincident(g20,g2)
    c: Coincident(g20,g19)
    c: Horizontal(g20)
    c: Distance(g20) = 93.4
    c: Coincident(g21,g1)
    c: Horizontal(g21)
    c: Distance(g21) = 101.7
    c: Horizontal(g23)
    c: Distance(g23) = 8
    c: Coincident(g24,g23)
    c: Block(g23)
    c: Coincident(g22,g24)
    c: Block(g24)
    c: Block(g22)
    c: Distance(g22) = 1.61553
    c: Coincident(g25,g18)
    c: Block(g25)
    c: Weight(g26) = 1
    c: Equal(g26,g27)
    c: Equal(g26,g28)
    c: Coincident(g29,g4)
    c: InternalAlignment(g26,g29)
    c: InternalAlignment(g27,g29)
    c: InternalAlignment(g28,g29)
    c: InternalAlignment(g30,g29)
    c: InternalAlignment(g31,g29)
    c: Block(g29)
    c: Weight(g32) = 1
    c: Equal(g32,g33)
    c: Equal(g32,g34)
    c: Coincident(g35,g29)
    c: InternalAlignment(g32,g35)
    c: InternalAlignment(g33,g35)
    c: InternalAlignment(g34,g35)
    c: InternalAlignment(g36,g35)
    c: InternalAlignment(g37,g35)
    c: Block(g35)
    c: Coincident(g38,g35)
    c: Vertical(g38)
    c: Block(g38)
    c: Coincident(g42,g38)
    c: Weight(g39) = 1
    c: Equal(g39,g40)
    c: Equal(g39,g41)
    c: Coincident(g42,g25)
    c: InternalAlignment(g39,g42)
    c: InternalAlignment(g40,g42)
    c: InternalAlignment(g41,g42)
    c: InternalAlignment(g43,g42)
    c: InternalAlignment(g44,g42)
    c: Block(g42)
FEATURE [Part::Extrusion] Extrude043  label="bottom010"
  Base = -> Sketch052
  Dir = (0,0,1)
  DirMode = 2
  FaceMakerClass = Part::FaceMakerBullseye
  LengthFwd = 71.4
  LengthRev = 0
  Placement = pos=(0,0,0.3) rot=(0,0,1;0rad)
  Solid = true
  Symmetric = false
FEATURE [Sketcher::SketchObject] Sketch053  label="topSketch013"
  FullyConstrained = true
  sketch-geometry (22):
    g0: LineSegment StartX=5.21097e-06 StartY=3 StartZ=0 EndX=5.21097e-06 EndY=19 EndZ=0
    g1: ArcOfCircle CenterX=19 CenterY=19 CenterZ=0 NormalX=0 NormalY=0 NormalZ=1 AngleXU=0 Radius=19 StartAngle=1.5708 EndAngle=3.14159
    g2: ArcOfCircle CenterX=19 CenterY=19 CenterZ=0 NormalX=0 NormalY=0 NormalZ=1 AngleXU=0 Radius=16 StartAngle=1.5708 EndAngle=3.14159
    g3: LineSegment StartX=114 StartY=35 StartZ=0 EndX=19 EndY=35 EndZ=0
    g4: LineSegment StartX=5.21097e-06 StartY=3 StartZ=0 EndX=5.21097e-06 EndY=0 EndZ=0
    g5: LineSegment StartX=3 StartY=0 StartZ=0 EndX=5.21097e-06 EndY=0 EndZ=0
    g6: LineSegment StartX=3 StartY=19 StartZ=0 EndX=3 EndY=0 EndZ=0
    g7: LineSegment StartX=19 StartY=38 StartZ=0 EndX=124 EndY=38 EndZ=0
    g8: Circle CenterX=119 CenterY=35 CenterZ=0 NormalX=0 NormalY=0 NormalZ=1 AngleXU=0 Radius=1
    g9: Circle CenterX=121 CenterY=35 CenterZ=0 NormalX=0 NormalY=0 NormalZ=1 AngleXU=0 Radius=1
    g10: Circle CenterX=121 CenterY=33 CenterZ=0 NormalX=0 NormalY=0 NormalZ=1 AngleXU=0 Radius=1
    g11: BSplineCurve PolesCount=3 KnotsCount=2 Degree=2 IsPeriodic=0
    g12: GeomPoint X=119 Y=35 Z=0
    g13: GeomPoint X=121 Y=33 Z=0
    g14: LineSegment StartX=119 StartY=35 StartZ=0 EndX=114 EndY=35 EndZ=0
    g15: ArcOfCircle CenterX=105 CenterY=19 CenterZ=0 NormalX=0 NormalY=0 NormalZ=1 AngleXU=0 Radius=16 StartAngle=5.60905 EndAngle=6.28319
    g16: LineSegment StartX=121 StartY=33 StartZ=0 EndX=121 EndY=19 EndZ=0
    g17: LineSegment StartX=117.5 StartY=9.01251 StartZ=0 EndX=121.163 EndY=9.0125 EndZ=0
    g18: ArcOfCircle CenterX=105 CenterY=19 CenterZ=0 NormalX=0 NormalY=0 NormalZ=1 AngleXU=0 Radius=20.6155 StartAngle=5.7297 EndAngle=6.28319
    g19: LineSegment StartX=121.163 StartY=9.0125 StartZ=0 EndX=122.538 EndY=8.16329 EndZ=0
    g20: LineSegment StartX=124 StartY=38 StartZ=0 EndX=125.616 EndY=38 EndZ=0
    g21: LineSegment StartX=125.616 StartY=19 StartZ=0 EndX=125.616 EndY=38 EndZ=0
  constraints (50):
    c: Vertical(g0)
    c: Block(g0)
    c: Coincident(g1,g0)
    c: Block(g1)
    c: Coincident(g2,g1)
    c: Block(g2)
    c: Coincident(g3,g2)
    c: Horizontal(g3)
    c: Tangent(g3,g2)
    c: Coincident(g4,g0)
    c: Distance(g4) = 3
    c: Vertical(g4)
    c: Coincident(g5,g4)
    c: Horizontal(g5)
    c: Coincident(g6,g2)
    c: Coincident(g6,g5)
    c: Vertical(g6)
    c: Horizontal(g7)
    c: Distance(g7) = 105
    c: Coincident(g7,g1)
    c: Block(g3)
    c: Weight(g8) = 1
    c: Equal(g8,g9)
    c: Equal(g8,g10)
    c: InternalAlignment(g8,g11)
    c: InternalAlignment(g9,g11)
    c: InternalAlignment(g10,g11)
    c: InternalAlignment(g12,g11)
    c: InternalAlignment(g13,g11)
    c: Block(g11)
    c: Coincident(g14,g11)
    c: Coincident(g14,g3)
    c: Horizontal(g14)
    c: Block(g15)
    c: Coincident(g16,g11)
    c: Coincident(g16,g15)
    c: Vertical(g16)
    c: Distance(g16) = 14
    c: Coincident(g17,g15)
    c: Block(g18)
    c: Coincident(g19,g18)
    c: Coincident(g20,g7)
    c: Horizontal(g20)
    c: Vertical(g21)
    c: Coincident(g20,g21)
    c: Block(g20)
    c: Block(g21)
    c: Block(g19)
    c: Block(g17)
    c: Distance(g20) = 1.61553
FEATURE [Part::Extrusion] Extrude044
  Base = -> Sketch053
  Dir = (0,0,1)
  DirMode = 2
  FaceMakerClass = Part::FaceMakerBullseye
  LengthFwd = 72
  LengthRev = 0
  Solid = true
  Symmetric = false
FEATURE [Part::Fillet] Fillet036  label="top018"
  Base = -> Extrude044
  Edges = 1 edges r=2: [Edge41]
FEATURE [Sketcher::SketchObject] Sketch054
  FullyConstrained = false
  Placement = pos=(0,0,0) rot=(1,0,0;1.5708rad)
  sketch-geometry (24):
    g0: ArcOfCircle CenterX=-4 CenterY=-10.5 CenterZ=0 NormalX=0 NormalY=0 NormalZ=1 AngleXU=0 Radius=1.5 StartAngle=6e-16 EndAngle=3.14159
    g1: ArcOfCircle CenterX=-34.2 CenterY=-10.5 CenterZ=0 NormalX=0 NormalY=0 NormalZ=1 AngleXU=0 Radius=1.5 StartAngle=0 EndAngle=3.14159
    g2: ArcOfCircle CenterX=-34.2 CenterY=-27.7 CenterZ=0 NormalX=0 NormalY=0 NormalZ=1 AngleXU=0 Radius=1.5 StartAngle=3.14159 EndAngle=6.28319
    g3: ArcOfCircle CenterX=-4 CenterY=-27.7 CenterZ=0 NormalX=0 NormalY=0 NormalZ=1 AngleXU=0 Radius=1.5 StartAngle=3.1416 EndAngle=6.28319
    g4: ArcOfCircle CenterX=-10 CenterY=-4.3 CenterZ=0 NormalX=0 NormalY=0 NormalZ=1 AngleXU=0 Radius=1.5 StartAngle=2e-16 EndAngle=3.14159
    g5: ArcOfCircle CenterX=-16.1 CenterY=-1.8 CenterZ=0 NormalX=0 NormalY=0 NormalZ=1 AngleXU=0 Radius=1.5 StartAngle=5e-16 EndAngle=3.14159
    g6: ArcOfCircle CenterX=-22.1 CenterY=-1.8 CenterZ=0 NormalX=0 NormalY=0 NormalZ=1 AngleXU=0 Radius=1.5 StartAngle=5e-16 EndAngle=3.14159
    g7: ArcOfCircle CenterX=-28.2 CenterY=-4.3 CenterZ=0 NormalX=0 NormalY=0 NormalZ=1 AngleXU=0 Radius=1.5 StartAngle=2e-16 EndAngle=3.14159
    g8: ArcOfCircle CenterX=-10 CenterY=-33.9 CenterZ=0 NormalX=0 NormalY=0 NormalZ=1 AngleXU=0 Radius=1.5 StartAngle=3.14159 EndAngle=6.28319
    g9: ArcOfCircle CenterX=-16.1 CenterY=-36.4 CenterZ=0 NormalX=0 NormalY=0 NormalZ=1 AngleXU=0 Radius=1.5 StartAngle=3.14159 EndAngle=6.28319
    g10: ArcOfCircle CenterX=-22.1 CenterY=-36.4 CenterZ=0 NormalX=0 NormalY=0 NormalZ=1 AngleXU=0 Radius=1.5 StartAngle=3.14159 EndAngle=6.28319
    g11: ArcOfCircle CenterX=-28.2 CenterY=-33.9 CenterZ=0 NormalX=0 NormalY=0 NormalZ=1 AngleXU=0 Radius=1.5 StartAngle=3.14159 EndAngle=6.28319
    g12: LineSegment StartX=-35.7 StartY=-10.5 StartZ=0 EndX=-35.7 EndY=-27.7 EndZ=0
    g13: LineSegment StartX=-32.7 StartY=-10.5 StartZ=0 EndX=-32.7 EndY=-27.7 EndZ=0
    g14: LineSegment StartX=-29.7 StartY=-33.9 StartZ=0 EndX=-29.7 EndY=-4.3 EndZ=0
    g15: LineSegment StartX=-26.7 StartY=-33.9 StartZ=0 EndX=-26.7 EndY=-4.3 EndZ=0
    g16: LineSegment StartX=-2.5 StartY=-10.5 StartZ=0 EndX=-2.5 EndY=-27.7 EndZ=0
    g17: LineSegment StartX=-8.5 StartY=-4.3 StartZ=0 EndX=-8.5 EndY=-33.9 EndZ=0
    g18: LineSegment StartX=-5.5 StartY=-10.5 StartZ=0 EndX=-5.5 EndY=-27.7 EndZ=0
    g19: LineSegment StartX=-11.5 StartY=-4.3 StartZ=0 EndX=-11.5 EndY=-33.9 EndZ=0
    g20: LineSegment StartX=-14.6 StartY=-1.8 StartZ=0 EndX=-14.6 EndY=-36.4 EndZ=0
    g21: LineSegment StartX=-17.6 StartY=-1.8 StartZ=0 EndX=-17.6 EndY=-36.4 EndZ=0
    g22: LineSegment StartX=-20.6 StartY=-36.4 StartZ=0 EndX=-20.6 EndY=-1.8 EndZ=0
    g23: LineSegment StartX=-23.6 StartY=-1.8 StartZ=0 EndX=-23.6 EndY=-36.4 EndZ=0
  constraints (48):
    c: Block(g0)
    c: Block(g1)
    c: Block(g2)
    c: Block(g3)
    c: Block(g4)
    c: Block(g5)
    c: Block(g6)
    c: Block(g7)
    c: Block(g8)
    c: Block(g9)
    c: Block(g10)
    c: Block(g11)
    c: Coincident(g12,g1)
    c: Coincident(g12,g2)
    c: Vertical(g12)
    c: Coincident(g13,g1)
    c: Coincident(g13,g2)
    c: Vertical(g13)
    c: Coincident(g14,g11)
    c: Coincident(g14,g7)
    c: Vertical(g14)
    c: Coincident(g15,g11)
    c: Coincident(g15,g7)
    c: Vertical(g15)
    c: Coincident(g16,g0)
    c: Coincident(g16,g3)
    c: Vertical(g16)
    c: Coincident(g17,g4)
    c: Coincident(g17,g8)
    c: Vertical(g17)
    c: Coincident(g18,g0)
    c: Coincident(g18,g3)
    c: Vertical(g18)
    c: Coincident(g19,g4)
    c: Coincident(g19,g8)
    c: Vertical(g19)
    c: Coincident(g20,g5)
    c: Coincident(g20,g9)
    c: Vertical(g20)
    c: Coincident(g21,g5)
    c: Coincident(g21,g9)
    c: Vertical(g21)
    c: Coincident(g22,g10)
    c: Coincident(g22,g6)
    c: Vertical(g22)
    c: Coincident(g23,g6)
    c: Coincident(g23,g10)
    c: Vertical(g23)
FEATURE [Part::Extrusion] Extrude045  label="removeToCreateFanGrillHoles003"
  Base = -> Sketch054
  Dir = (0,-1,6e-16)
  DirMode = 2
  FaceMakerClass = Part::FaceMakerBullseye
  LengthFwd = 10
  LengthRev = 0
  Placement = pos=(65.4,44,54.82) rot=(0,0,1;0rad)
  Solid = true
  Symmetric = false
FEATURE [Part::Feature] Face105 .. Face108  x4 (patterned run collapsed; names and placements below)
  shape: bbox 3.5 x 17.8 x 2e-07 mm, 1 faces, 0 solids (baked)
FEATURE [Part::Revolution] Revolve113  label="removeToCreateScrewAndThreadedInsertHole041"
  Angle = 360
  Axis = (0,1,0)
  Base = (0,0,0)
  FaceMakerClass = Part::FaceMakerBullseye
  Placement = pos=(62.3,30.3,19.7) rot=(0,0,1;0rad)
  Solid = false
  Source = -> Face105
  Symmetric = false
FEATURE [Part::Revolution] Revolve114  label="removeToCreateScrewAndThreadedInsertHole042"
  Angle = 360
  Axis = (0,1,0)
  Base = (0,0,0)
  FaceMakerClass = Part::FaceMakerBullseye
  Placement = pos=(62.3,30.3,51.7) rot=(0,0,1;0rad)
  Solid = false
  Source = -> Face106
  Symmetric = false
FEATURE [Part::Revolution] Revolve115  label="removeToCreateScrewAndThreadedInsertHole043"
  Angle = 360
  Axis = (0,1,0)
  Base = (0,0,0)
  FaceMakerClass = Part::FaceMakerBullseye
  Placement = pos=(30.3,30.3,19.7) rot=(0,0,1;0rad)
  Solid = false
  Source = -> Face107
  Symmetric = false
FEATURE [Part::Revolution] Revolve116  label="removeToCreateScrewAndThreadedInsertHole044"
  Angle = 360
  Axis = (0,1,0)
  Base = (0,0,0)
  FaceMakerClass = Part::FaceMakerBullseye
  Placement = pos=(30.3,30.3,51.7) rot=(0,0,1;0rad)
  Solid = false
  Source = -> Face108
  Symmetric = false
FEATURE [Part::MultiFuse] Fusion083  label="createThreadedInsertHolesForFan004"
  Shapes = -> [Revolve113,Revolve114,Revolve115,Revolve116]
FEATURE [Part::Box] Box024  label="removeToCreteHoleForPlugHousing026"
  AttacherType = Attacher::AttachEngine3D
  Height = 28.6
  Length = 10
  Placement = pos=(-2,0,21.7) rot=(0,0,1;0rad)
  Width = 19
FEATURE [Part::Cylinder] Cylinder038  label="removeToCreteHoleForPlugHousing027"
  Angle = 360
  AttacherType = Attacher::AttachEngine3D
  Height = 20
  Placement = pos=(-2,19,36) rot=(0,1,0;1.5708rad)
  Radius = 14.3
FEATURE [Part::MultiFuse] Fusion084  label="removeToCreteHoleForPlugHousing028"
  Shapes = -> [Box024,Cylinder038]
FEATURE [Part::Cylinder] Cylinder039
  Angle = 360
  AttacherType = Attacher::AttachEngine3D
  Height = 20
  Placement = pos=(0,0,36.15) rot=(0,0,1;0rad)
  Radius = 14.3
FEATURE [Part::Cylinder] Cylinder040
  Angle = 360
  AttacherType = Attacher::AttachEngine3D
  Height = 10
  Placement = pos=(0,0,36.15) rot=(0,0,1;0rad)
  Radius = 4
FEATURE [Part::Box] Box025  label="removeToCreteHoleForPlugHousing030"
  AttacherType = Attacher::AttachEngine3D
  Height = 28.6
  Length = 20
  Placement = pos=(106.15,0,21.7) rot=(0,0,1;0rad)
  Width = 19
FEATURE [Part::MultiFuse] Fusion086  label="removeToCreteHoleForPlugHousing031"
  Placement = pos=(70,19,36) rot=(0,1,0;1.5708rad)
  Shapes = -> [Cylinder039,Cylinder040]
FEATURE [Part::MultiFuse] Fusion085  label="removeToCreteHoleForPlugHousing029"
  Shapes = -> [Box025,Fusion086]
FEATURE [Sketcher::SketchObject] Sketch055
  FullyConstrained = true
  Placement = pos=(117,19,0) rot=(0.57735,0.57735,0.57735;2.0944rad)
  sketch-geometry (48):
    g0: LineSegment StartX=-49.19 StartY=69.25 StartZ=0 EndX=-49.19 EndY=66.25 EndZ=0
    g1: LineSegment StartX=-49.19 StartY=63.5 StartZ=0 EndX=-49.19 EndY=60.5 EndZ=0
    g2: LineSegment StartX=-49.19 StartY=57.75 StartZ=0 EndX=-49.19 EndY=54.75 EndZ=0
    g3: LineSegment StartX=-49.19 StartY=52 StartZ=0 EndX=-49.19 EndY=49 EndZ=0
    g4: LineSegment StartX=-49.19 StartY=46.25 StartZ=0 EndX=-49.19 EndY=43.25 EndZ=0
    g5: LineSegment StartX=-49.19 StartY=40.5 StartZ=0 EndX=-49.19 EndY=37.5 EndZ=0
    g6: LineSegment StartX=-49.19 StartY=34.5 StartZ=0 EndX=-49.19 EndY=31.5 EndZ=0
    g7: LineSegment StartX=-49.19 StartY=28.75 StartZ=0 EndX=-49.19 EndY=25.75 EndZ=0
    g8: LineSegment StartX=-49.19 StartY=23 StartZ=0 EndX=-49.19 EndY=20 EndZ=0
    g9: LineSegment StartX=-49.19 StartY=17.25 StartZ=0 EndX=-49.19 EndY=14.25 EndZ=0
    g10: LineSegment StartX=-49.19 StartY=11.5 StartZ=0 EndX=-49.19 EndY=8.5 EndZ=0
    g11: LineSegment StartX=-49.19 StartY=5.75 StartZ=0 EndX=-49.19 EndY=2.75 EndZ=0
    g12: ArcOfCircle CenterX=-1.5 CenterY=67.75 CenterZ=0 NormalX=0 NormalY=0 NormalZ=1 AngleXU=0 Radius=1.5 StartAngle=4.71239 EndAngle=7.85398
    g13: ArcOfCircle CenterX=-1.5 CenterY=62 CenterZ=0 NormalX=0 NormalY=0 NormalZ=1 AngleXU=0 Radius=1.5 StartAngle=4.71239 EndAngle=7.85398
    g14: ArcOfCircle CenterX=-1.5 CenterY=56.25 CenterZ=0 NormalX=0 NormalY=0 NormalZ=1 AngleXU=0 Radius=1.5 StartAngle=4.71239 EndAngle=7.85398
    g15: ArcOfCircle CenterX=-11.49 CenterY=50.5 CenterZ=0 NormalX=0 NormalY=0 NormalZ=1 AngleXU=0 Radius=1.5 StartAngle=4.71239 EndAngle=7.85398
    g16: ArcOfCircle CenterX=-16.28 CenterY=44.75 CenterZ=0 NormalX=0 NormalY=0 NormalZ=1 AngleXU=0 Radius=1.5 StartAngle=4.71239 EndAngle=7.85398
    g17: ArcOfCircle CenterX=-18.2337 CenterY=39 CenterZ=0 NormalX=0 NormalY=0 NormalZ=1 AngleXU=0 Radius=1.5 StartAngle=4.71485 EndAngle=7.85398
    g18: ArcOfCircle CenterX=-16.2837 CenterY=27.25 CenterZ=0 NormalX=0 NormalY=0 NormalZ=1 AngleXU=0 Radius=1.5 StartAngle=4.71485 EndAngle=7.85398
    g19: ArcOfCircle CenterX=-18.2337 CenterY=33 CenterZ=0 NormalX=0 NormalY=0 NormalZ=1 AngleXU=0 Radius=1.5 StartAngle=4.71485 EndAngle=7.85398
    g20: ArcOfCircle CenterX=-11.49 CenterY=21.5 CenterZ=0 NormalX=0 NormalY=0 NormalZ=1 AngleXU=0 Radius=1.5 StartAngle=4.71239 EndAngle=7.85398
    g21: ArcOfCircle CenterX=-1.5 CenterY=4.25 CenterZ=0 NormalX=0 NormalY=0 NormalZ=1 AngleXU=0 Radius=1.5 StartAngle=4.71239 EndAngle=7.85398
    g22: ArcOfCircle CenterX=-1.5 CenterY=10 CenterZ=0 NormalX=0 NormalY=0 NormalZ=1 AngleXU=0 Radius=1.5 StartAngle=4.71239 EndAngle=7.85398
    g23: ArcOfCircle CenterX=-1.5 CenterY=15.75 CenterZ=0 NormalX=0 NormalY=0 NormalZ=1 AngleXU=0 Radius=1.5 StartAngle=4.71239 EndAngle=7.85398
    g24: LineSegment StartX=-49.19 StartY=69.25 StartZ=0 EndX=-1.5 EndY=69.25 EndZ=0
    g25: LineSegment StartX=-49.19 StartY=66.25 StartZ=0 EndX=-1.5 EndY=66.25 EndZ=0
    g26: LineSegment StartX=-49.19 StartY=63.5 StartZ=0 EndX=-1.5 EndY=63.5 EndZ=0
    g27: LineSegment StartX=-49.19 StartY=60.5 StartZ=0 EndX=-1.5 EndY=60.5 EndZ=0
    g28: LineSegment StartX=-49.19 StartY=57.75 StartZ=0 EndX=-1.5 EndY=57.75 EndZ=0
    g29: LineSegment StartX=-49.19 StartY=54.75 StartZ=0 EndX=-1.5 EndY=54.75 EndZ=0
    g30: LineSegment StartX=-49.19 StartY=52 StartZ=0 EndX=-11.49 EndY=52 EndZ=0
    g31: LineSegment StartX=-49.19 StartY=49 StartZ=0 EndX=-11.49 EndY=49 EndZ=0
    g32: LineSegment StartX=-49.19 StartY=46.25 StartZ=0 EndX=-16.28 EndY=46.25 EndZ=0
    g33: LineSegment StartX=-49.19 StartY=43.25 StartZ=0 EndX=-16.28 EndY=43.25 EndZ=0
    g34: LineSegment StartX=-49.19 StartY=40.5 StartZ=0 EndX=-18.2337 EndY=40.5 EndZ=0
    g35: LineSegment StartX=-49.19 StartY=37.5 StartZ=0 EndX=-18.23 EndY=37.5 EndZ=0
    g36: LineSegment StartX=-49.19 StartY=34.5 StartZ=0 EndX=-18.2337 EndY=34.5 EndZ=0
    g37: LineSegment StartX=-49.19 StartY=31.5 StartZ=0 EndX=-18.23 EndY=31.5 EndZ=0
    g38: LineSegment StartX=-49.19 StartY=28.75 StartZ=0 EndX=-16.2837 EndY=28.75 EndZ=0
    g39: LineSegment StartX=-49.19 StartY=25.75 StartZ=0 EndX=-16.28 EndY=25.75 EndZ=0
    g40: LineSegment StartX=-49.19 StartY=23 StartZ=0 EndX=-11.49 EndY=23 EndZ=0
    g41: LineSegment StartX=-49.19 StartY=20 StartZ=0 EndX=-11.49 EndY=20 EndZ=0
    g42: LineSegment StartX=-49.19 StartY=17.25 StartZ=0 EndX=-1.5 EndY=17.25 EndZ=0
    g43: LineSegment StartX=-49.19 StartY=14.25 StartZ=0 EndX=-1.5 EndY=14.25 EndZ=0
    g44: LineSegment StartX=-49.19 StartY=11.5 StartZ=0 EndX=-1.5 EndY=11.5 EndZ=0
    g45: LineSegment StartX=-49.19 StartY=8.5 StartZ=0 EndX=-1.5 EndY=8.5 EndZ=0
    g46: LineSegment StartX=-49.19 StartY=5.75 StartZ=0 EndX=-1.5 EndY=5.75 EndZ=0
    g47: LineSegment StartX=-49.19 StartY=2.75 StartZ=0 EndX=-1.5 EndY=2.75 EndZ=0
  constraints (120):
    c: Vertical(g0)
    c: Distance(g0) = 3
    c: Block(g0)
    c: Vertical(g1)
    c: Distance(g1) = 3
    c: Vertical(g2)
    c: Equal(g0,g2) = 3
    c: Block(g2)
    c: Vertical(g3)
    c: Equal(g1,g3) = 3
    c: Vertical(g4)
    c: Equal(g0,g4) = 3
    c: Block(g4)
    c: Vertical(g5)
    c: Equal(g1,g5) = 3
    c: Vertical(g6)
    c: Equal(g0,g6) = 3
    c: Block(g6)
    c: Vertical(g7)
    c: Equal(g1,g7) = 3
    c: Vertical(g8)
    c: Equal(g0,g8) = 3
    c: Block(g8)
    c: Vertical(g9)
    c: Equal(g1,g9) = 3
    c: Vertical(g10)
    c: Equal(g0,g10) = 3
    c: Block(g10)
    c: Vertical(g11)
    c: Equal(g1,g11) = 3
    c: Block(g12)
    c: Block(g13)
    c: Block(g14)
    c: Block(g15)
    c: Block(g16)
    c: Block(g17)
    c: Block(g18)
    c: Block(g19)
    c: Block(g20)
    c: Block(g21)
    c: Block(g22)
    c: Block(g23)
    c: Block(g11)
    c: Block(g9)
    c: Block(g7)
    c: Block(g5)
    c: Block(g3)
    c: Block(g1)
    c: Coincident(g24,g0)
    c: Coincident(g24,g12)
    c: Horizontal(g24)
    c: Coincident(g25,g0)
    c: Coincident(g25,g12)
    c: Horizontal(g25)
    c: Coincident(g26,g1)
    c: Coincident(g26,g13)
    c: Horizontal(g26)
    c: Coincident(g27,g1)
    c: Coincident(g27,g13)
    c: Horizontal(g27)
    c: Coincident(g28,g2)
    c: Coincident(g28,g14)
    c: Horizontal(g28)
    c: Coincident(g29,g2)
    c: Coincident(g29,g14)
    c: Horizontal(g29)
    c: Coincident(g30,g3)
    c: Coincident(g30,g15)
    c: Horizontal(g30)
    c: Coincident(g31,g3)
    c: Coincident(g31,g15)
    c: Horizontal(g31)
    c: Coincident(g32,g4)
    c: Coincident(g32,g16)
    c: Horizontal(g32)
    c: Coincident(g33,g4)
    c: Coincident(g33,g16)
    c: Horizontal(g33)
    c: Coincident(g34,g5)
    c: Coincident(g34,g17)
    c: Horizontal(g34)
    c: Coincident(g35,g5)
    c: Coincident(g35,g17)
    c: Horizontal(g35)
    c: Coincident(g36,g6)
    c: Coincident(g36,g19)
    c: Horizontal(g36)
    c: Coincident(g37,g6)
    c: Coincident(g37,g19)
    c: Horizontal(g37)
    c: Coincident(g38,g7)
    c: Coincident(g38,g18)
    c: Horizontal(g38)
    c: Coincident(g39,g7)
    c: Coincident(g39,g18)
    c: Horizontal(g39)
    c: Coincident(g40,g8)
    c: Coincident(g40,g20)
    c: Horizontal(g40)
    c: Coincident(g41,g8)
    c: Coincident(g41,g20)
    c: Horizontal(g41)
    c: Coincident(g42,g9)
    c: Coincident(g42,g23)
    c: Horizontal(g42)
    c: Coincident(g43,g9)
    c: Coincident(g43,g23)
    c: Horizontal(g43)
    c: Coincident(g44,g10)
    c: Coincident(g44,g22)
    c: Horizontal(g44)
    c: Coincident(g45,g10)
    c: Coincident(g45,g22)
    c: Horizontal(g45)
    c: Coincident(g46,g11)
    c: Coincident(g46,g21)
    c: Horizontal(g46)
    c: Coincident(g47,g11)
    c: Coincident(g47,g21)
    c: Horizontal(g47)
FEATURE [Part::Extrusion] Extrude046
  Base = -> Sketch055
  Dir = (1,0,0)
  DirMode = 2
  FaceMakerClass = Part::FaceMakerBullseye
  LengthFwd = 23
  LengthRev = 0
  Placement = pos=(-19,0,0) rot=(0,0,1;0rad)
  Solid = true
  Symmetric = false
FEATURE [Part::Fillet] Fillet038  label="removeToCreateVentalationHoles001"
  Base = -> Extrude046
  Edges = <same value as first occurrence — deduplicated (x6 in doc)>
  Placement = pos=(7,0,0) rot=(0,0,1;0rad)
FEATURE [Sketcher::SketchObject] Sketch056  label="topSketch014"
  FullyConstrained = true
  sketch-geometry (22):
    g0: LineSegment StartX=5.21097e-06 StartY=3 StartZ=0 EndX=5.21097e-06 EndY=19 EndZ=0
    g1: ArcOfCircle CenterX=19 CenterY=19 CenterZ=0 NormalX=0 NormalY=0 NormalZ=1 AngleXU=0 Radius=19 StartAngle=1.5708 EndAngle=3.14159
    g2: ArcOfCircle CenterX=19 CenterY=19 CenterZ=0 NormalX=0 NormalY=0 NormalZ=1 AngleXU=0 Radius=16 StartAngle=1.5708 EndAngle=3.14159
    g3: LineSegment StartX=114 StartY=35 StartZ=0 EndX=19 EndY=35 EndZ=0
    g4: LineSegment StartX=5.21097e-06 StartY=3 StartZ=0 EndX=5.21097e-06 EndY=0 EndZ=0
    g5: LineSegment StartX=3 StartY=0 StartZ=0 EndX=5.21097e-06 EndY=0 EndZ=0
    g6: LineSegment StartX=3 StartY=19 StartZ=0 EndX=3 EndY=0 EndZ=0
    g7: LineSegment StartX=19 StartY=38 StartZ=0 EndX=124 EndY=38 EndZ=0
    g8: Circle CenterX=119 CenterY=35 CenterZ=0 NormalX=0 NormalY=0 NormalZ=1 AngleXU=0 Radius=1
    g9: Circle CenterX=121 CenterY=35 CenterZ=0 NormalX=0 NormalY=0 NormalZ=1 AngleXU=0 Radius=1
    g10: Circle CenterX=121 CenterY=33 CenterZ=0 NormalX=0 NormalY=0 NormalZ=1 AngleXU=0 Radius=1
    g11: BSplineCurve PolesCount=3 KnotsCount=2 Degree=2 IsPeriodic=0
    g12: GeomPoint X=119 Y=35 Z=0
    g13: GeomPoint X=121 Y=33 Z=0
    g14: LineSegment StartX=119 StartY=35 StartZ=0 EndX=114 EndY=35 EndZ=0
    g15: ArcOfCircle CenterX=105 CenterY=19 CenterZ=0 NormalX=0 NormalY=0 NormalZ=1 AngleXU=0 Radius=16 StartAngle=5.60905 EndAngle=6.28319
    g16: LineSegment StartX=121 StartY=33 StartZ=0 EndX=121 EndY=19 EndZ=0
    g17: LineSegment StartX=117.5 StartY=9.01251 StartZ=0 EndX=121.163 EndY=9.0125 EndZ=0
    g18: ArcOfCircle CenterX=105 CenterY=19 CenterZ=0 NormalX=0 NormalY=0 NormalZ=1 AngleXU=0 Radius=20.6155 StartAngle=5.7297 EndAngle=6.28319
    g19: LineSegment StartX=121.163 StartY=9.0125 StartZ=0 EndX=122.538 EndY=8.16329 EndZ=0
    g20: LineSegment StartX=124 StartY=38 StartZ=0 EndX=125.616 EndY=38 EndZ=0
    g21: LineSegment StartX=125.616 StartY=19 StartZ=0 EndX=125.616 EndY=38 EndZ=0
  constraints (49):
    c: Vertical(g0)
    c: Block(g0)
    c: Coincident(g1,g0)
    c: Block(g1)
    c: Coincident(g2,g1)
    c: Block(g2)
    c: Coincident(g3,g2)
    c: Horizontal(g3)
    c: Tangent(g3,g2)
    c: Coincident(g4,g0)
    c: Distance(g4) = 3
    c: Vertical(g4)
    c: Coincident(g5,g4)
    c: Horizontal(g5)
    c: Coincident(g6,g2)
    c: Coincident(g6,g5)
    c: Vertical(g6)
    c: Horizontal(g7)
    c: Distance(g7) = 105
    c: Coincident(g7,g1)
    c: Block(g3)
    c: Weight(g8) = 1
    c: Equal(g8,g9)
    c: Equal(g8,g10)
    c: InternalAlignment(g8,g11)
    c: InternalAlignment(g9,g11)
    c: InternalAlignment(g10,g11)
    c: InternalAlignment(g12,g11)
    c: InternalAlignment(g13,g11)
    c: Block(g11)
    c: Coincident(g14,g11)
    c: Coincident(g14,g3)
    c: Horizontal(g14)
    c: Block(g15)
    c: Coincident(g16,g11)
    c: Coincident(g16,g15)
    c: Vertical(g16)
    c: Distance(g16) = 14
    c: Coincident(g17,g15)
    c: Block(g18)
    c: Coincident(g19,g18)
    c: Coincident(g20,g7)
    c: Horizontal(g20)
    c: Vertical(g21)
    c: Coincident(g20,g21)
    c: Block(g20)
    c: Block(g21)
    c: Block(g19)
    c: Block(g17)
FEATURE [Part::Box] Box026  label="removeToCreteHoleForPlugHousing032"
  AttacherType = Attacher::AttachEngine3D
  Height = 28.6
  Length = 10
  Placement = pos=(-2,0,21.7) rot=(0,0,1;0rad)
  Width = 19
FEATURE [Part::Feature] Face109 .. Face112  x4 (patterned run collapsed; names and placements below)
  shape: bbox 3.5 x 17.8 x 2e-07 mm, 1 faces, 0 solids (baked)
FEATURE [Part::Revolution] Revolve117  label="removeToCreateScrewAndThreadedInsertHole045"
  Angle = 360
  Axis = (0,1,0)
  Base = (0,0,0)
  FaceMakerClass = Part::FaceMakerBullseye
  Placement = pos=(62.3,30.3,19.7) rot=(0,0,1;0rad)
  Solid = false
  Source = -> Face109
  Symmetric = false
FEATURE [Part::Revolution] Revolve118  label="removeToCreateScrewAndThreadedInsertHole046"
  Angle = 360
  Axis = (0,1,0)
  Base = (0,0,0)
  FaceMakerClass = Part::FaceMakerBullseye
  Placement = pos=(62.3,30.3,51.7) rot=(0,0,1;0rad)
  Solid = false
  Source = -> Face110
  Symmetric = false
FEATURE [Part::Revolution] Revolve119  label="removeToCreateScrewAndThreadedInsertHole047"
  Angle = 360
  Axis = (0,1,0)
  Base = (0,0,0)
  FaceMakerClass = Part::FaceMakerBullseye
  Placement = pos=(30.3,30.3,19.7) rot=(0,0,1;0rad)
  Solid = false
  Source = -> Face111
  Symmetric = false
FEATURE [Part::Revolution] Revolve120  label="removeToCreateScrewAndThreadedInsertHole048"
  Angle = 360
  Axis = (0,1,0)
  Base = (0,0,0)
  FaceMakerClass = Part::FaceMakerBullseye
  Placement = pos=(30.3,30.3,51.7) rot=(0,0,1;0rad)
  Solid = false
  Source = -> Face112
  Symmetric = false
FEATURE [Part::MultiFuse] Fusion087  label="createThreadedInsertHolesForFan005"
  Shapes = -> [Revolve117,Revolve118,Revolve119,Revolve120]
FEATURE [Part::Extrusion] Extrude047
  Base = -> Sketch056
  Dir = (0,0,1)
  DirMode = 2
  FaceMakerClass = Part::FaceMakerBullseye
  LengthFwd = 72
  LengthRev = 0
  Solid = true
  Symmetric = false
FEATURE [Part::Fillet] Fillet039  label="top019"
  Base = -> Extrude047
  Edges = 1 edges r=2: [Edge35]
FEATURE [Sketcher::SketchObject] Sketch057
  FullyConstrained = false
  Placement = pos=(0,0,0) rot=(1,0,0;1.5708rad)
  sketch-geometry (24):
    g0: ArcOfCircle CenterX=-4 CenterY=-10.5 CenterZ=0 NormalX=0 NormalY=0 NormalZ=1 AngleXU=0 Radius=1.5 StartAngle=6e-16 EndAngle=3.14159
    g1: ArcOfCircle CenterX=-34.2 CenterY=-10.5 CenterZ=0 NormalX=0 NormalY=0 NormalZ=1 AngleXU=0 Radius=1.5 StartAngle=0 EndAngle=3.14159
    g2: ArcOfCircle CenterX=-34.2 CenterY=-27.7 CenterZ=0 NormalX=0 NormalY=0 NormalZ=1 AngleXU=0 Radius=1.5 StartAngle=3.14159 EndAngle=6.28319
    g3: ArcOfCircle CenterX=-4 CenterY=-27.7 CenterZ=0 NormalX=0 NormalY=0 NormalZ=1 AngleXU=0 Radius=1.5 StartAngle=3.1416 EndAngle=6.28319
    g4: ArcOfCircle CenterX=-10 CenterY=-4.3 CenterZ=0 NormalX=0 NormalY=0 NormalZ=1 AngleXU=0 Radius=1.5 StartAngle=2e-16 EndAngle=3.14159
    g5: ArcOfCircle CenterX=-16.1 CenterY=-1.8 CenterZ=0 NormalX=0 NormalY=0 NormalZ=1 AngleXU=0 Radius=1.5 StartAngle=5e-16 EndAngle=3.14159
    g6: ArcOfCircle CenterX=-22.1 CenterY=-1.8 CenterZ=0 NormalX=0 NormalY=0 NormalZ=1 AngleXU=0 Radius=1.5 StartAngle=5e-16 EndAngle=3.14159
    g7: ArcOfCircle CenterX=-28.2 CenterY=-4.3 CenterZ=0 NormalX=0 NormalY=0 NormalZ=1 AngleXU=0 Radius=1.5 StartAngle=2e-16 EndAngle=3.14159
    g8: ArcOfCircle CenterX=-10 CenterY=-33.9 CenterZ=0 NormalX=0 NormalY=0 NormalZ=1 AngleXU=0 Radius=1.5 StartAngle=3.14159 EndAngle=6.28319
    g9: ArcOfCircle CenterX=-16.1 CenterY=-36.4 CenterZ=0 NormalX=0 NormalY=0 NormalZ=1 AngleXU=0 Radius=1.5 StartAngle=3.14159 EndAngle=6.28319
    g10: ArcOfCircle CenterX=-22.1 CenterY=-36.4 CenterZ=0 NormalX=0 NormalY=0 NormalZ=1 AngleXU=0 Radius=1.5 StartAngle=3.14159 EndAngle=6.28319
    g11: ArcOfCircle CenterX=-28.2 CenterY=-33.9 CenterZ=0 NormalX=0 NormalY=0 NormalZ=1 AngleXU=0 Radius=1.5 StartAngle=3.14159 EndAngle=6.28319
    g12: LineSegment StartX=-35.7 StartY=-10.5 StartZ=0 EndX=-35.7 EndY=-27.7 EndZ=0
    g13: LineSegment StartX=-32.7 StartY=-10.5 StartZ=0 EndX=-32.7 EndY=-27.7 EndZ=0
    g14: LineSegment StartX=-29.7 StartY=-33.9 StartZ=0 EndX=-29.7 EndY=-4.3 EndZ=0
    g15: LineSegment StartX=-26.7 StartY=-33.9 StartZ=0 EndX=-26.7 EndY=-4.3 EndZ=0
    g16: LineSegment StartX=-2.5 StartY=-10.5 StartZ=0 EndX=-2.5 EndY=-27.7 EndZ=0
    g17: LineSegment StartX=-8.5 StartY=-4.3 StartZ=0 EndX=-8.5 EndY=-33.9 EndZ=0
    g18: LineSegment StartX=-5.5 StartY=-10.5 StartZ=0 EndX=-5.5 EndY=-27.7 EndZ=0
    g19: LineSegment StartX=-11.5 StartY=-4.3 StartZ=0 EndX=-11.5 EndY=-33.9 EndZ=0
    g20: LineSegment StartX=-14.6 StartY=-1.8 StartZ=0 EndX=-14.6 EndY=-36.4 EndZ=0
    g21: LineSegment StartX=-17.6 StartY=-1.8 StartZ=0 EndX=-17.6 EndY=-36.4 EndZ=0
    g22: LineSegment StartX=-20.6 StartY=-36.4 StartZ=0 EndX=-20.6 EndY=-1.8 EndZ=0
    g23: LineSegment StartX=-23.6 StartY=-1.8 StartZ=0 EndX=-23.6 EndY=-36.4 EndZ=0
  constraints (48):
    c: Block(g0)
    c: Block(g1)
    c: Block(g2)
    c: Block(g3)
    c: Block(g4)
    c: Block(g5)
    c: Block(g6)
    c: Block(g7)
    c: Block(g8)
    c: Block(g9)
    c: Block(g10)
    c: Block(g11)
    c: Coincident(g12,g1)
    c: Coincident(g12,g2)
    c: Vertical(g12)
    c: Coincident(g13,g1)
    c: Coincident(g13,g2)
    c: Vertical(g13)
    c: Coincident(g14,g11)
    c: Coincident(g14,g7)
    c: Vertical(g14)
    c: Coincident(g15,g11)
    c: Coincident(g15,g7)
    c: Vertical(g15)
    c: Coincident(g16,g0)
    c: Coincident(g16,g3)
    c: Vertical(g16)
    c: Coincident(g17,g4)
    c: Coincident(g17,g8)
    c: Vertical(g17)
    c: Coincident(g18,g0)
    c: Coincident(g18,g3)
    c: Vertical(g18)
    c: Coincident(g19,g4)
    c: Coincident(g19,g8)
    c: Vertical(g19)
    c: Coincident(g20,g5)
    c: Coincident(g20,g9)
    c: Vertical(g20)
    c: Coincident(g21,g5)
    c: Coincident(g21,g9)
    c: Vertical(g21)
    c: Coincident(g22,g10)
    c: Coincident(g22,g6)
    c: Vertical(g22)
    c: Coincident(g23,g6)
    c: Coincident(g23,g10)
    c: Vertical(g23)
FEATURE [Part::Extrusion] Extrude048  label="removeToCreateFanGrillHoles004"
  Base = -> Sketch057
  Dir = (0,-1,6e-16)
  DirMode = 2
  FaceMakerClass = Part::FaceMakerBullseye
  LengthFwd = 10
  LengthRev = 0
  Placement = pos=(65.4,44,54.82) rot=(0,0,1;0rad)
  Solid = true
  Symmetric = false
FEATURE [Part::Cut] Cut040  label="top021"
  Base = -> Fillet039
  Tool = -> Extrude048
FEATURE [Part::Cylinder] Cylinder041  label="removeToCreteHoleForPlugHousing034"
  Angle = 360
  AttacherType = Attacher::AttachEngine3D
  Height = 20
  Placement = pos=(-2,19,36) rot=(0,1,0;1.5708rad)
  Radius = 14.3
FEATURE [Part::MultiFuse] Fusion089  label="removeToCreteHoleForPlugHousing035"
  Shapes = -> [Box026,Cylinder041]
FEATURE [Part::Cylinder] Cylinder042
  Angle = 360
  AttacherType = Attacher::AttachEngine3D
  Height = 20
  Placement = pos=(0,0,36.15) rot=(0,0,1;0rad)
  Radius = 14.3
FEATURE [Part::Cylinder] Cylinder043
  Angle = 360
  AttacherType = Attacher::AttachEngine3D
  Height = 10
  Placement = pos=(0,0,36.15) rot=(0,0,1;0rad)
  Radius = 4
FEATURE [Part::Box] Box027  label="removeToCreteHoleForPlugHousing036"
  AttacherType = Attacher::AttachEngine3D
  Height = 28.6
  Length = 20
  Placement = pos=(106.15,0,21.7) rot=(0,0,1;0rad)
  Width = 19
FEATURE [Part::Cut] Cut041  label="top022"
  Base = -> Cut040
  Tool = -> Fusion087
FEATURE [Part::Cut] Cut039  label="top020"
  Base = -> Cut041
  Tool = -> Fusion089
FEATURE [Part::MultiFuse] Fusion090  label="removeToCreteHoleForPlugHousing037"
  Placement = pos=(70,19,36) rot=(0,1,0;1.5708rad)
  Shapes = -> [Cylinder042,Cylinder043]
FEATURE [Part::MultiFuse] Fusion088  label="removeToCreteHoleForPlugHousing033"
  Shapes = -> [Box027,Fusion090]
FEATURE [Part::Cut] Cut042  label="removeToCreteHoleForPlugHousing038"
  Base = -> Cut039
  Tool = -> Fusion088
FEATURE [Part::MultiFuse] Fusion091  label="removeFromTop"
  Shapes = -> [Fillet038,Fusion085,Fusion084,Fusion083,Extrude045]
FEATURE [Part::Cut] Cut043  label="REAL TOP ====="
  Base = -> Fillet036
  Tool = -> Fusion091
FEATURE [Part::MultiFuse] Fusion092  label="caseScrewPillarBracket016"
  Shapes = -> [Extrude030,Extrude031,Extrude032,Extrude033,Extrude034,Extrude035,Extrude036,Extrude037,Box013,Box014]
FEATURE [Sketcher::SketchObject] Sketch058  label="topSketch015"
  FullyConstrained = true
  sketch-geometry (20):
    g0: LineSegment StartX=5.21097e-06 StartY=3 StartZ=0 EndX=5.21097e-06 EndY=19 EndZ=0
    g1: ArcOfCircle CenterX=19 CenterY=19 CenterZ=0 NormalX=0 NormalY=0 NormalZ=1 AngleXU=0 Radius=19 StartAngle=1.5708 EndAngle=3.14159
    g2: ArcOfCircle CenterX=19 CenterY=19 CenterZ=0 NormalX=0 NormalY=0 NormalZ=1 AngleXU=0 Radius=16 StartAngle=1.5708 EndAngle=3.14159
    g3: LineSegment StartX=114 StartY=35 StartZ=0 EndX=19 EndY=35 EndZ=0
    g4: LineSegment StartX=5.21097e-06 StartY=3 StartZ=0 EndX=5.21097e-06 EndY=0 EndZ=0
    g5: LineSegment StartX=3 StartY=0 StartZ=0 EndX=5.21097e-06 EndY=0 EndZ=0
    g6: LineSegment StartX=3 StartY=19 StartZ=0 EndX=3 EndY=0 EndZ=0
    g7: LineSegment StartX=19 StartY=38 StartZ=0 EndX=124 EndY=38 EndZ=0
    g8: Circle CenterX=119 CenterY=35 CenterZ=0 NormalX=0 NormalY=0 NormalZ=1 AngleXU=0 Radius=1
    g9: Circle CenterX=121 CenterY=35 CenterZ=0 NormalX=0 NormalY=0 NormalZ=1 AngleXU=0 Radius=1
    g10: Circle CenterX=121 CenterY=33 CenterZ=0 NormalX=0 NormalY=0 NormalZ=1 AngleXU=0 Radius=1
    g11: BSplineCurve PolesCount=3 KnotsCount=2 Degree=2 IsPeriodic=0
    g12: GeomPoint X=119 Y=35 Z=0
    g13: GeomPoint X=121 Y=33 Z=0
    g14: LineSegment StartX=119 StartY=35 StartZ=0 EndX=114 EndY=35 EndZ=0
    g15: ArcOfCircle CenterX=105 CenterY=19 CenterZ=0 NormalX=0 NormalY=0 NormalZ=1 AngleXU=0 Radius=19 StartAngle=5.7297 EndAngle=6.28319
    g16: ArcOfCircle CenterX=105 CenterY=19 CenterZ=0 NormalX=0 NormalY=0 NormalZ=1 AngleXU=0 Radius=16 StartAngle=5.60905 EndAngle=6.28319
    g17: LineSegment StartX=121 StartY=33 StartZ=0 EndX=121 EndY=19 EndZ=0
    g18: LineSegment StartX=124 StartY=38 StartZ=0 EndX=124 EndY=19 EndZ=0
    g19: LineSegment StartX=117.5 StartY=9.01251 StartZ=0 EndX=121.163 EndY=9.0125 EndZ=0
  constraints (46):
    c: Vertical(g0)
    c: Block(g0)
    c: Coincident(g1,g0)
    c: Block(g1)
    c: Coincident(g2,g1)
    c: Block(g2)
    c: Coincident(g3,g2)
    c: Horizontal(g3)
    c: Tangent(g3,g2)
    c: Coincident(g4,g0)
    c: Distance(g4) = 3
    c: Vertical(g4)
    c: Coincident(g5,g4)
    c: Horizontal(g5)
    c: Coincident(g6,g2)
    c: Coincident(g6,g5)
    c: Vertical(g6)
    c: Horizontal(g7)
    c: Distance(g7) = 105
    c: Coincident(g7,g1)
    c: Block(g3)
    c: Weight(g8) = 1
    c: Equal(g8,g9)
    c: Equal(g8,g10)
    c: InternalAlignment(g8,g11)
    c: InternalAlignment(g9,g11)
    c: InternalAlignment(g10,g11)
    c: InternalAlignment(g12,g11)
    c: InternalAlignment(g13,g11)
    c: Block(g11)
    c: Coincident(g14,g11)
    c: Coincident(g14,g3)
    c: Horizontal(g14)
    c: Block(g15)
    c: Coincident(g16,g15)
    c: Block(g16)
    c: Coincident(g17,g11)
    c: Coincident(g17,g16)
    c: Vertical(g17)
    c: Distance(g17) = 14
    c: Coincident(g18,g7)
    c: Coincident(g18,g15)
    c: Vertical(g18)
    c: Distance(g18) = 19
    c: Coincident(g19,g16)
    c: Coincident(g19,g15)
FEATURE [Part::Extrusion] Extrude049  label="top023"
  Base = -> Sketch058
  Dir = (0,0,1)
  DirMode = 2
  FaceMakerClass = Part::FaceMakerBullseye
  LengthFwd = 72
  LengthRev = 0
  Solid = true
  Symmetric = false
FEATURE [Sketcher::SketchObject] Sketch059
  FullyConstrained = true
  MapMode = 3
  Placement = pos=(0,0,0) rot=(1,0,0;1.5708rad)
  Support = -> [Extrude049]
  sketch-geometry (8):
    g0: Circle CenterX=80.351 CenterY=-67.6202 CenterZ=0 NormalX=0 NormalY=0 NormalZ=1 AngleXU=0 Radius=2
    g1: Circle CenterX=80.351 CenterY=-67.6202 CenterZ=0 NormalX=0 NormalY=0 NormalZ=1 AngleXU=0 Radius=3
    g2: Circle CenterX=80.351 CenterY=-4.92017 CenterZ=0 NormalX=0 NormalY=0 NormalZ=1 AngleXU=0 Radius=2
    g3: Circle CenterX=80.351 CenterY=-4.92017 CenterZ=0 NormalX=0 NormalY=0 NormalZ=1 AngleXU=0 Radius=3
    g4: Circle CenterX=23.851 CenterY=-4.92017 CenterZ=0 NormalX=0 NormalY=0 NormalZ=1 AngleXU=0 Radius=2
    g5: Circle CenterX=23.851 CenterY=-4.92017 CenterZ=0 NormalX=0 NormalY=0 NormalZ=1 AngleXU=0 Radius=3
    g6: Circle CenterX=23.851 CenterY=-67.6202 CenterZ=0 NormalX=0 NormalY=0 NormalZ=1 AngleXU=0 Radius=2
    g7: Circle CenterX=23.851 CenterY=-67.6202 CenterZ=0 NormalX=0 NormalY=0 NormalZ=1 AngleXU=0 Radius=3
  constraints (8):
    c: Block(g3)
    c: Block(g2)
    c: Block(g1)
    c: Block(g0)
    c: Block(g6)
    c: Block(g7)
    c: Block(g4)
    c: Block(g5)
FEATURE [Sketcher::SketchObject] Sketch060
  FullyConstrained = true
  MapMode = 3
  Placement = pos=(0,0,0) rot=(1,0,0;1.5708rad)
  Support = -> [Extrude049]
  sketch-geometry (8):
    g0: Circle CenterX=80.351 CenterY=-67.6202 CenterZ=0 NormalX=0 NormalY=0 NormalZ=1 AngleXU=0 Radius=3
    g1: Circle CenterX=80.351 CenterY=-4.92017 CenterZ=0 NormalX=0 NormalY=0 NormalZ=1 AngleXU=0 Radius=3
    g2: Circle CenterX=23.851 CenterY=-4.92017 CenterZ=0 NormalX=0 NormalY=0 NormalZ=1 AngleXU=0 Radius=3
    g3: Circle CenterX=23.851 CenterY=-67.6202 CenterZ=0 NormalX=0 NormalY=0 NormalZ=1 AngleXU=0 Radius=3
    g4: Circle CenterX=23.851 CenterY=-67.6202 CenterZ=0 NormalX=0 NormalY=0 NormalZ=1 AngleXU=0 Radius=5
    g5: Circle CenterX=80.351 CenterY=-67.6202 CenterZ=0 NormalX=0 NormalY=0 NormalZ=1 AngleXU=0 Radius=5
    g6: Circle CenterX=23.851 CenterY=-4.92017 CenterZ=0 NormalX=0 NormalY=0 NormalZ=1 AngleXU=0 Radius=5
    g7: Circle CenterX=80.351 CenterY=-4.92017 CenterZ=0 NormalX=0 NormalY=0 NormalZ=1 AngleXU=0 Radius=5
  constraints (8):
    c: Block(g1)
    c: Block(g0)
    c: Block(g3)
    c: Block(g2)
    c: Block(g5)
    c: Block(g4)
    c: Block(g6)
    c: Block(g7)
FEATURE [Sketcher::SketchObject] Sketch061
  FullyConstrained = true
  MapMode = 3
  Placement = pos=(0,0,0) rot=(1,0,0;1.5708rad)
  sketch-geometry (8):
    g0: Circle CenterX=80.351 CenterY=-67.6202 CenterZ=0 NormalX=0 NormalY=0 NormalZ=1 AngleXU=0 Radius=3
    g1: Circle CenterX=80.351 CenterY=-4.92017 CenterZ=0 NormalX=0 NormalY=0 NormalZ=1 AngleXU=0 Radius=3
    g2: Circle CenterX=23.851 CenterY=-4.92017 CenterZ=0 NormalX=0 NormalY=0 NormalZ=1 AngleXU=0 Radius=3
    g3: Circle CenterX=23.851 CenterY=-67.6202 CenterZ=0 NormalX=0 NormalY=0 NormalZ=1 AngleXU=0 Radius=3
    g4: Circle CenterX=23.851 CenterY=-67.6202 CenterZ=0 NormalX=0 NormalY=0 NormalZ=1 AngleXU=0 Radius=5
    g5: Circle CenterX=80.351 CenterY=-67.6202 CenterZ=0 NormalX=0 NormalY=0 NormalZ=1 AngleXU=0 Radius=5
    g6: Circle CenterX=23.851 CenterY=-4.92017 CenterZ=0 NormalX=0 NormalY=0 NormalZ=1 AngleXU=0 Radius=5
    g7: Circle CenterX=80.351 CenterY=-4.92017 CenterZ=0 NormalX=0 NormalY=0 NormalZ=1 AngleXU=0 Radius=5
  constraints (8):
    c: Block(g1)
    c: Block(g0)
    c: Block(g3)
    c: Block(g2)
    c: Block(g5)
    c: Block(g4)
    c: Block(g6)
    c: Block(g7)
FEATURE [Sketcher::SketchObject] Sketch062  label="topSketch016"
  FullyConstrained = true
  sketch-geometry (20):
    g0: LineSegment StartX=5.21097e-06 StartY=3 StartZ=0 EndX=5.21097e-06 EndY=19 EndZ=0
    g1: ArcOfCircle CenterX=19 CenterY=19 CenterZ=0 NormalX=0 NormalY=0 NormalZ=1 AngleXU=0 Radius=19 StartAngle=1.5708 EndAngle=3.14159
    g2: ArcOfCircle CenterX=19 CenterY=19 CenterZ=0 NormalX=0 NormalY=0 NormalZ=1 AngleXU=0 Radius=16 StartAngle=1.5708 EndAngle=3.14159
    g3: LineSegment StartX=114 StartY=35 StartZ=0 EndX=19 EndY=35 EndZ=0
    g4: LineSegment StartX=5.21097e-06 StartY=3 StartZ=0 EndX=5.21097e-06 EndY=0 EndZ=0
    g5: LineSegment StartX=3 StartY=0 StartZ=0 EndX=5.21097e-06 EndY=0 EndZ=0
    g6: LineSegment StartX=3 StartY=19 StartZ=0 EndX=3 EndY=0 EndZ=0
    g7: LineSegment StartX=19 StartY=38 StartZ=0 EndX=124 EndY=38 EndZ=0
    g8: Circle CenterX=119 CenterY=35 CenterZ=0 NormalX=0 NormalY=0 NormalZ=1 AngleXU=0 Radius=1
    g9: Circle CenterX=121 CenterY=35 CenterZ=0 NormalX=0 NormalY=0 NormalZ=1 AngleXU=0 Radius=1
    g10: Circle CenterX=121 CenterY=33 CenterZ=0 NormalX=0 NormalY=0 NormalZ=1 AngleXU=0 Radius=1
    g11: BSplineCurve PolesCount=3 KnotsCount=2 Degree=2 IsPeriodic=0
    g12: GeomPoint X=119 Y=35 Z=0
    g13: GeomPoint X=121 Y=33 Z=0
    g14: LineSegment StartX=119 StartY=35 StartZ=0 EndX=114 EndY=35 EndZ=0
    g15: ArcOfCircle CenterX=105 CenterY=19 CenterZ=0 NormalX=0 NormalY=0 NormalZ=1 AngleXU=0 Radius=19 StartAngle=5.7297 EndAngle=6.28319
    g16: ArcOfCircle CenterX=105 CenterY=19 CenterZ=0 NormalX=0 NormalY=0 NormalZ=1 AngleXU=0 Radius=16 StartAngle=5.60905 EndAngle=6.28319
    g17: LineSegment StartX=121 StartY=33 StartZ=0 EndX=121 EndY=19 EndZ=0
    g18: LineSegment StartX=124 StartY=38 StartZ=0 EndX=124 EndY=19 EndZ=0
    g19: LineSegment StartX=117.5 StartY=9.01251 StartZ=0 EndX=121.163 EndY=9.0125 EndZ=0
  constraints (46):
    c: Vertical(g0)
    c: Block(g0)
    c: Coincident(g1,g0)
    c: Block(g1)
    c: Coincident(g2,g1)
    c: Block(g2)
    c: Coincident(g3,g2)
    c: Horizontal(g3)
    c: Tangent(g3,g2)
    c: Coincident(g4,g0)
    c: Distance(g4) = 3
    c: Vertical(g4)
    c: Coincident(g5,g4)
    c: Horizontal(g5)
    c: Coincident(g6,g2)
    c: Coincident(g6,g5)
    c: Vertical(g6)
    c: Horizontal(g7)
    c: Distance(g7) = 105
    c: Coincident(g7,g1)
    c: Block(g3)
    c: Weight(g8) = 1
    c: Equal(g8,g9)
    c: Equal(g8,g10)
    c: InternalAlignment(g8,g11)
    c: InternalAlignment(g9,g11)
    c: InternalAlignment(g10,g11)
    c: InternalAlignment(g12,g11)
    c: InternalAlignment(g13,g11)
    c: Block(g11)
    c: Coincident(g14,g11)
    c: Coincident(g14,g3)
    c: Horizontal(g14)
    c: Block(g15)
    c: Coincident(g16,g15)
    c: Block(g16)
    c: Coincident(g17,g11)
    c: Coincident(g17,g16)
    c: Vertical(g17)
    c: Distance(g17) = 14
    c: Coincident(g18,g7)
    c: Coincident(g18,g15)
    c: Vertical(g18)
    c: Distance(g18) = 19
    c: Coincident(g19,g16)
    c: Coincident(g19,g15)
FEATURE [Part::Extrusion] Extrude053  label="top024"
  Base = -> Sketch062
  Dir = (0,0,1)
  DirMode = 2
  FaceMakerClass = Part::FaceMakerBullseye
  LengthFwd = 72
  LengthRev = 0
  Solid = true
  Symmetric = false
FEATURE [Sketcher::SketchObject] Sketch063
  FullyConstrained = true
  MapMode = 3
  Placement = pos=(0,0,0) rot=(1,0,0;1.5708rad)
  Support = -> [Extrude053]
  sketch-geometry (8):
    g0: Circle CenterX=80.351 CenterY=-67.6202 CenterZ=0 NormalX=0 NormalY=0 NormalZ=1 AngleXU=0 Radius=2
    g1: Circle CenterX=80.351 CenterY=-67.6202 CenterZ=0 NormalX=0 NormalY=0 NormalZ=1 AngleXU=0 Radius=3
    g2: Circle CenterX=80.351 CenterY=-4.92017 CenterZ=0 NormalX=0 NormalY=0 NormalZ=1 AngleXU=0 Radius=2
    g3: Circle CenterX=80.351 CenterY=-4.92017 CenterZ=0 NormalX=0 NormalY=0 NormalZ=1 AngleXU=0 Radius=3
    g4: Circle CenterX=23.851 CenterY=-4.92017 CenterZ=0 NormalX=0 NormalY=0 NormalZ=1 AngleXU=0 Radius=2
    g5: Circle CenterX=23.851 CenterY=-4.92017 CenterZ=0 NormalX=0 NormalY=0 NormalZ=1 AngleXU=0 Radius=3
    g6: Circle CenterX=23.851 CenterY=-67.6202 CenterZ=0 NormalX=0 NormalY=0 NormalZ=1 AngleXU=0 Radius=2
    g7: Circle CenterX=23.851 CenterY=-67.6202 CenterZ=0 NormalX=0 NormalY=0 NormalZ=1 AngleXU=0 Radius=3
  constraints (8):
    c: Block(g3)
    c: Block(g2)
    c: Block(g1)
    c: Block(g0)
    c: Block(g6)
    c: Block(g7)
    c: Block(g4)
    c: Block(g5)
FEATURE [Part::Extrusion] Extrude054
  Base = -> Sketch063
  Dir = (0,-1,2e-16)
  DirMode = 2
  FaceMakerClass = Part::FaceMakerBullseye
  LengthFwd = 6
  LengthRev = 0
  Placement = pos=(0,9,0) rot=(0,0,1;0rad)
  Solid = true
  Symmetric = false
FEATURE [Sketcher::SketchObject] Sketch064  label="topSketch017"
  FullyConstrained = true
  sketch-geometry (20):
    g0: LineSegment StartX=5.21097e-06 StartY=3 StartZ=0 EndX=5.21097e-06 EndY=19 EndZ=0
    g1: ArcOfCircle CenterX=19 CenterY=19 CenterZ=0 NormalX=0 NormalY=0 NormalZ=1 AngleXU=0 Radius=19 StartAngle=1.5708 EndAngle=3.14159
    g2: ArcOfCircle CenterX=19 CenterY=19 CenterZ=0 NormalX=0 NormalY=0 NormalZ=1 AngleXU=0 Radius=16 StartAngle=1.5708 EndAngle=3.14159
    g3: LineSegment StartX=114 StartY=35 StartZ=0 EndX=19 EndY=35 EndZ=0
    g4: LineSegment StartX=5.21097e-06 StartY=3 StartZ=0 EndX=5.21097e-06 EndY=0 EndZ=0
    g5: LineSegment StartX=3 StartY=0 StartZ=0 EndX=5.21097e-06 EndY=0 EndZ=0
    g6: LineSegment StartX=3 StartY=19 StartZ=0 EndX=3 EndY=0 EndZ=0
    g7: LineSegment StartX=19 StartY=38 StartZ=0 EndX=124 EndY=38 EndZ=0
    g8: Circle CenterX=119 CenterY=35 CenterZ=0 NormalX=0 NormalY=0 NormalZ=1 AngleXU=0 Radius=1
    g9: Circle CenterX=121 CenterY=35 CenterZ=0 NormalX=0 NormalY=0 NormalZ=1 AngleXU=0 Radius=1
    g10: Circle CenterX=121 CenterY=33 CenterZ=0 NormalX=0 NormalY=0 NormalZ=1 AngleXU=0 Radius=1
    g11: BSplineCurve PolesCount=3 KnotsCount=2 Degree=2 IsPeriodic=0
    g12: GeomPoint X=119 Y=35 Z=0
    g13: GeomPoint X=121 Y=33 Z=0
    g14: LineSegment StartX=119 StartY=35 StartZ=0 EndX=114 EndY=35 EndZ=0
    g15: ArcOfCircle CenterX=105 CenterY=19 CenterZ=0 NormalX=0 NormalY=0 NormalZ=1 AngleXU=0 Radius=19 StartAngle=5.7297 EndAngle=6.28319
    g16: ArcOfCircle CenterX=105 CenterY=19 CenterZ=0 NormalX=0 NormalY=0 NormalZ=1 AngleXU=0 Radius=16 StartAngle=5.60905 EndAngle=6.28319
    g17: LineSegment StartX=121 StartY=33 StartZ=0 EndX=121 EndY=19 EndZ=0
    g18: LineSegment StartX=124 StartY=38 StartZ=0 EndX=124 EndY=19 EndZ=0
    g19: LineSegment StartX=117.5 StartY=9.01251 StartZ=0 EndX=121.163 EndY=9.0125 EndZ=0
  constraints (46):
    c: Vertical(g0)
    c: Block(g0)
    c: Coincident(g1,g0)
    c: Block(g1)
    c: Coincident(g2,g1)
    c: Block(g2)
    c: Coincident(g3,g2)
    c: Horizontal(g3)
    c: Tangent(g3,g2)
    c: Coincident(g4,g0)
    c: Distance(g4) = 3
    c: Vertical(g4)
    c: Coincident(g5,g4)
    c: Horizontal(g5)
    c: Coincident(g6,g2)
    c: Coincident(g6,g5)
    c: Vertical(g6)
    c: Horizontal(g7)
    c: Distance(g7) = 105
    c: Coincident(g7,g1)
    c: Block(g3)
    c: Weight(g8) = 1
    c: Equal(g8,g9)
    c: Equal(g8,g10)
    c: InternalAlignment(g8,g11)
    c: InternalAlignment(g9,g11)
    c: InternalAlignment(g10,g11)
    c: InternalAlignment(g12,g11)
    c: InternalAlignment(g13,g11)
    c: Block(g11)
    c: Coincident(g14,g11)
    c: Coincident(g14,g3)
    c: Horizontal(g14)
    c: Block(g15)
    c: Coincident(g16,g15)
    c: Block(g16)
    c: Coincident(g17,g11)
    c: Coincident(g17,g16)
    c: Vertical(g17)
    c: Distance(g17) = 14
    c: Coincident(g18,g7)
    c: Coincident(g18,g15)
    c: Vertical(g18)
    c: Distance(g18) = 19
    c: Coincident(g19,g16)
    c: Coincident(g19,g15)
FEATURE [Sketcher::SketchObject] Sketch065
  FullyConstrained = true
  MapMode = 3
  Placement = pos=(0,0,0) rot=(1,0,0;1.5708rad)
  sketch-geometry (8):
    g0: Circle CenterX=80.351 CenterY=-67.6202 CenterZ=0 NormalX=0 NormalY=0 NormalZ=1 AngleXU=0 Radius=3
    g1: Circle CenterX=80.351 CenterY=-4.92017 CenterZ=0 NormalX=0 NormalY=0 NormalZ=1 AngleXU=0 Radius=3
    g2: Circle CenterX=23.851 CenterY=-4.92017 CenterZ=0 NormalX=0 NormalY=0 NormalZ=1 AngleXU=0 Radius=3
    g3: Circle CenterX=23.851 CenterY=-67.6202 CenterZ=0 NormalX=0 NormalY=0 NormalZ=1 AngleXU=0 Radius=3
    g4: Circle CenterX=23.851 CenterY=-67.6202 CenterZ=0 NormalX=0 NormalY=0 NormalZ=1 AngleXU=0 Radius=5
    g5: Circle CenterX=80.351 CenterY=-67.6202 CenterZ=0 NormalX=0 NormalY=0 NormalZ=1 AngleXU=0 Radius=5
    g6: Circle CenterX=23.851 CenterY=-4.92017 CenterZ=0 NormalX=0 NormalY=0 NormalZ=1 AngleXU=0 Radius=5
    g7: Circle CenterX=80.351 CenterY=-4.92017 CenterZ=0 NormalX=0 NormalY=0 NormalZ=1 AngleXU=0 Radius=5
  constraints (8):
    c: Block(g1)
    c: Block(g0)
    c: Block(g3)
    c: Block(g2)
    c: Block(g5)
    c: Block(g4)
    c: Block(g6)
    c: Block(g7)
FEATURE [Part::Extrusion] Extrude056
  Base = -> Sketch065
  Dir = (0,-1,2e-16)
  DirMode = 2
  FaceMakerClass = Part::FaceMakerBullseye
  LengthFwd = 2
  LengthRev = 0
  Solid = true
  Symmetric = false
FEATURE [Part::Extrusion] Extrude057  label="top025"
  Base = -> Sketch064
  Dir = (0,0,1)
  DirMode = 2
  FaceMakerClass = Part::FaceMakerBullseye
  LengthFwd = 72
  LengthRev = 0
  Solid = true
  Symmetric = false
FEATURE [Sketcher::SketchObject] Sketch066
  FullyConstrained = true
  MapMode = 3
  Placement = pos=(0,0,0) rot=(1,0,0;1.5708rad)
  Support = -> [Extrude057]
  sketch-geometry (8):
    g0: Circle CenterX=80.351 CenterY=-67.6202 CenterZ=0 NormalX=0 NormalY=0 NormalZ=1 AngleXU=0 Radius=3
    g1: Circle CenterX=80.351 CenterY=-4.92017 CenterZ=0 NormalX=0 NormalY=0 NormalZ=1 AngleXU=0 Radius=3
    g2: Circle CenterX=23.851 CenterY=-4.92017 CenterZ=0 NormalX=0 NormalY=0 NormalZ=1 AngleXU=0 Radius=3
    g3: Circle CenterX=23.851 CenterY=-67.6202 CenterZ=0 NormalX=0 NormalY=0 NormalZ=1 AngleXU=0 Radius=3
    g4: Circle CenterX=23.851 CenterY=-67.6202 CenterZ=0 NormalX=0 NormalY=0 NormalZ=1 AngleXU=0 Radius=5
    g5: Circle CenterX=80.351 CenterY=-67.6202 CenterZ=0 NormalX=0 NormalY=0 NormalZ=1 AngleXU=0 Radius=5
    g6: Circle CenterX=23.851 CenterY=-4.92017 CenterZ=0 NormalX=0 NormalY=0 NormalZ=1 AngleXU=0 Radius=5
    g7: Circle CenterX=80.351 CenterY=-4.92017 CenterZ=0 NormalX=0 NormalY=0 NormalZ=1 AngleXU=0 Radius=5
  constraints (8):
    c: Block(g1)
    c: Block(g0)
    c: Block(g3)
    c: Block(g2)
    c: Block(g5)
    c: Block(g4)
    c: Block(g6)
    c: Block(g7)
FEATURE [Part::Extrusion] Extrude055
  Base = -> Sketch066
  Dir = (0,-1,2e-16)
  DirMode = 2
  FaceMakerClass = Part::FaceMakerBullseye
  LengthFwd = 2
  LengthRev = 0
  Solid = true
  Symmetric = false
FEATURE [Part::Fillet] Fillet041
  Base = -> Extrude056
  Edges = 4 edges r=1.99: [Edge6,Edge12,Edge18,Edge24]
FEATURE [Part::Cut] Cut045
  Base = -> Extrude055
  Placement = pos=(0,6,0) rot=(0,0,1;0rad)
  Tool = -> Fillet041
FEATURE [Part::MultiFuse] Fusion095  label="pcbScrewPillars"
  Placement = pos=(-3.2,-1,72.3) rot=(0,0,1;0rad)
  Shapes = -> [Cut045,Extrude054]
FEATURE [Part::Feature] Face113
  shape: bbox 3.2 x 1.5 x 2e-07 mm, 1 faces, 0 solids (baked)
FEATURE [Part::Revolution] Revolve121  label="backCaseScrewRetainer002"
  Angle = 360
  Axis = (0,1,0)
  Base = (0,0,0)
  FaceMakerClass = Part::FaceMakerBullseye
  Placement = pos=(12.5,3,62) rot=(0,0,1;0rad)
  Solid = false
  Source = -> Face113
  Symmetric = false
FEATURE [Part::Feature] Face114
  shape: bbox 3.2 x 1.5 x 2e-07 mm, 1 faces, 0 solids (baked)
FEATURE [Part::Feature] Face115
  shape: bbox 3.2 x 1.5 x 2e-07 mm, 1 faces, 0 solids (baked)
FEATURE [Part::Feature] Face116
  shape: bbox 3.2 x 1.5 x 2e-07 mm, 1 faces, 0 solids (baked)
FEATURE [Part::Revolution] Revolve122  label="frontCaseScrewRetainer004"
  Angle = 360
  Axis = (0,1,0)
  Base = (0,0,0)
  FaceMakerClass = Part::FaceMakerBullseye
  Placement = pos=(89.5,3,68.5) rot=(0,0,1;0rad)
  Solid = false
  Source = -> Face115
  Symmetric = false
FEATURE [Part::Revolution] Revolve123  label="frontCaseScrewRetainer005"
  Angle = 360
  Axis = (0,1,0)
  Base = (0,0,0)
  FaceMakerClass = Part::FaceMakerBullseye
  Placement = pos=(89.5,3,3.5) rot=(0,0,1;0rad)
  Solid = false
  Source = -> Face116
  Symmetric = false
FEATURE [Part::Revolution] Revolve124  label="backCaseScrewRetainer003"
  Angle = 360
  Axis = (0,1,0)
  Base = (0,0,0)
  FaceMakerClass = Part::FaceMakerBullseye
  Placement = pos=(12.5,3,10) rot=(0,0,1;0rad)
  Solid = false
  Source = -> Face114
  Symmetric = false
FEATURE [Part::Feature] Face117
  shape: bbox 3.6 x 3.2 x 2e-07 mm, 1 faces, 0 solids (baked)
FEATURE [Part::Revolution] Revolve125  label="moreFrontCaseScrewRetainer004"
  Angle = 360
  Axis = (0,1,0)
  Base = (0,0,0)
  FaceMakerClass = Part::FaceMakerBullseye
  Placement = pos=(109.5,4.5,68.5) rot=(0,0,1;0rad)
  Solid = false
  Source = -> Face117
  Symmetric = false
FEATURE [Part::Feature] Face118
  shape: bbox 3.6 x 3.2 x 2e-07 mm, 1 faces, 0 solids (baked)
FEATURE [Part::Revolution] Revolve126  label="moreFrontCaseScrewRetainer005"
  Angle = 360
  Axis = (0,1,0)
  Base = (0,0,0)
  FaceMakerClass = Part::FaceMakerBullseye
  Placement = pos=(109.5,4.5,3.5) rot=(0,0,1;0rad)
  Solid = false
  Source = -> Face118
  Symmetric = false
FEATURE [Part::MultiFuse] Fusion096  label="screwRetainers001"
  Shapes = -> [Revolve126,Revolve125,Revolve124,Revolve123,Revolve122,Revolve121]
FEATURE [Part::Feature] Face119
  shape: bbox 10 x 16.5 x 2e-07 mm, 1 faces, 0 solids (baked)
FEATURE [Part::Revolution] Revolve130  label="plugHousing050"
  Angle = 360
  Axis = (0,1,0)
  Base = (0,0,0)
  FaceMakerClass = Part::FaceMakerBullseye
  Placement = pos=(0,0,36.15) rot=(0,0,1;0rad)
  Solid = false
  Source = -> Face119
  Symmetric = false
FEATURE [Part::Feature] Face120
  shape: bbox 10 x 16.5 x 2e-07 mm, 1 faces, 0 solids (baked)
FEATURE [Part::Feature] Face121
  shape: bbox 10 x 16.5 x 2e-07 mm, 1 faces, 0 solids (baked)
FEATURE [Part::Revolution] Revolve127  label="plugHousing047"
  Angle = 360
  Axis = (0,1,0)
  Base = (0,0,0)
  FaceMakerClass = Part::FaceMakerBullseye
  Placement = pos=(0,0,36.15) rot=(0,0,1;0rad)
  Solid = false
  Source = -> Face121
  Symmetric = false
FEATURE [Part::Feature] Face122
  shape: bbox 10 x 16.5 x 2e-07 mm, 1 faces, 0 solids (baked)
FEATURE [Part::Feature] Face123
  shape: bbox 10 x 16.5 x 2e-07 mm, 1 faces, 0 solids (baked)
FEATURE [Part::Revolution] Revolve128  label="plugHousing048"
  Angle = 360
  Axis = (0,1,0)
  Base = (0,0,0)
  FaceMakerClass = Part::FaceMakerBullseye
  Placement = pos=(0,0,36.15) rot=(0,0,1;0rad)
  Solid = false
  Source = -> Face123
  Symmetric = false
FEATURE [Part::MultiFuse] Fusion100  label="plugHousing054"
  Placement = pos=(0,0,0) rot=(0,0,1;1.5708rad)
  Shapes = -> [Revolve130,Revolve128]
FEATURE [Part::Feature] Face124
  shape: bbox 10 x 16.5 x 2e-07 mm, 1 faces, 0 solids (baked)
FEATURE [Part::Feature] Face125
  shape: bbox 10 x 16.5 x 2e-07 mm, 1 faces, 0 solids (baked)
FEATURE [Part::Revolution] Revolve129  label="plugHousing049"
  Angle = 360
  Axis = (0,1,0)
  Base = (0,0,0)
  FaceMakerClass = Part::FaceMakerBullseye
  Placement = pos=(0,0,36.15) rot=(0,0,1;0rad)
  Solid = false
  Source = -> Face125
  Symmetric = false
FEATURE [Part::Feature] Face126
  shape: bbox 10 x 16.5 x 2e-07 mm, 1 faces, 0 solids (baked)
FEATURE [Part::Revolution] Revolve131  label="plugHousing058"
  Angle = 360
  Axis = (0,1,0)
  Base = (0,0,0)
  FaceMakerClass = Part::FaceMakerBullseye
  Placement = pos=(0,0,36.15) rot=(0,0,1;0rad)
  Solid = false
  Source = -> Face120
  Symmetric = false
FEATURE [Part::MultiFuse] Fusion099  label="plugHousing053"
  Placement = pos=(0,0,0) rot=(0,0,1;1.5708rad)
  Shapes = -> [Revolve127,Revolve131]
FEATURE [Part::MultiFuse] Fusion102  label="plugHousing056"
  Placement = pos=(0,19,0) rot=(0,0,1;3.14159rad)
  Shapes = -> [Fusion100,Fusion099]
FEATURE [Part::Revolution] Revolve132  label="plugHousing059"
  Angle = 360
  Axis = (0,1,0)
  Base = (0,0,0)
  FaceMakerClass = Part::FaceMakerBullseye
  Placement = pos=(0,0,36.15) rot=(0,0,1;0rad)
  Solid = false
  Source = -> Face126
  Symmetric = false
FEATURE [Part::Revolution] Revolve133  label="plugHousing060"
  Angle = 360
  Axis = (0,1,0)
  Base = (0,0,0)
  FaceMakerClass = Part::FaceMakerBullseye
  Placement = pos=(0,0,36.15) rot=(0,0,1;0rad)
  Solid = false
  Source = -> Face122
  Symmetric = false
FEATURE [Part::MultiFuse] Fusion097  label="plugHousing051"
  Placement = pos=(0,0,0) rot=(0,0,1;1.5708rad)
  Shapes = -> [Revolve133,Revolve132]
FEATURE [Part::Revolution] Revolve134  label="plugHousing061"
  Angle = 360
  Axis = (0,1,0)
  Base = (0,0,0)
  FaceMakerClass = Part::FaceMakerBullseye
  Placement = pos=(0,0,36.15) rot=(0,0,1;0rad)
  Solid = false
  Source = -> Face124
  Symmetric = false
FEATURE [Part::MultiFuse] Fusion101  label="plugHousing055"
  Placement = pos=(0,0,0) rot=(0,0,1;1.5708rad)
  Shapes = -> [Revolve129,Revolve134]
FEATURE [Part::MultiFuse] Fusion098  label="plugHousing052"
  Placement = pos=(0,19,0) rot=(0,0,1;3.14159rad)
  Shapes = -> [Fusion097,Fusion101]
FEATURE [Part::MultiFuse] Fusion103  label="plugHousing057"
  Placement = pos=(122.621,0,-0.15) rot=(0,0,1;0rad)
  Shapes = -> [Fusion102,Fusion098]
FEATURE [Part::Box] Box028  label="Cube015"
  AttacherType = Attacher::AttachEngine3D
  Height = 28
  Length = 3
  Placement = pos=(110.7,19,22) rot=(0,0,1;0rad)
  Width = 15.7
FEATURE [Part::Cylinder] Cylinder044
  Angle = 360
  AttacherType = Attacher::AttachEngine3D
  Height = 20
  Placement = pos=(0,0,36.15) rot=(0,0,1;0rad)
  Radius = 10.3
FEATURE [Part::Cylinder] Cylinder045
  Angle = 360
  AttacherType = Attacher::AttachEngine3D
  Height = 10
  Placement = pos=(0,0,36.15) rot=(0,0,1;0rad)
  Radius = 4
FEATURE [Part::MultiFuse] Fusion104  label="removeToCreteHoleForPlugHousing040"
  Placement = pos=(70,19,36) rot=(0,1,0;1.5708rad)
  Shapes = -> [Cylinder044,Cylinder045]
FEATURE [Part::Cut] Cut046  label="plugHousingTab003"
  Base = -> Box028
  Tool = -> Fusion104
FEATURE [Part::MultiFuse] Fusion105  label="plugHousing062"
  Shapes = -> [Fusion103,Cut046]
FEATURE [Part::Fillet] Fillet042
  Base = -> Fusion105
  Edges = 1 edges r=2: [Edge25]
FEATURE [Part::Fillet] Fillet043  label="plugHousing063"
  Base = -> Fillet042
  Edges = 1 edges r=2: [Edge8]
  Placement = pos=(7,0,0) rot=(0,0,1;0rad)
FEATURE [Part::Feature] Face127
  shape: bbox 10 x 16.5 x 2e-07 mm, 1 faces, 0 solids (baked)
FEATURE [Part::Feature] Face128
  shape: bbox 10 x 16.5 x 2e-07 mm, 1 faces, 0 solids (baked)
FEATURE [Part::Revolution] Revolve137  label="plugHousing070"
  Angle = 360
  Axis = (0,1,0)
  Base = (0,0,0)
  FaceMakerClass = Part::FaceMakerBullseye
  Placement = pos=(0,0,36.15) rot=(0,0,1;0rad)
  Solid = false
  Source = -> Face127
  Symmetric = false
FEATURE [Part::Revolution] Revolve140  label="plugHousing073"
  Angle = 360
  Axis = (0,1,0)
  Base = (0,0,0)
  FaceMakerClass = Part::FaceMakerBullseye
  Placement = pos=(0,0,36.15) rot=(0,0,1;0rad)
  Solid = false
  Source = -> Face128
  Symmetric = false
FEATURE [Part::Feature] Face129
  shape: bbox 10 x 16.5 x 2e-07 mm, 1 faces, 0 solids (baked)
FEATURE [Part::Revolution] Revolve138  label="plugHousing071"
  Angle = 360
  Axis = (0,1,0)
  Base = (0,0,0)
  FaceMakerClass = Part::FaceMakerBullseye
  Placement = pos=(0,0,36.15) rot=(0,0,1;0rad)
  Solid = false
  Source = -> Face129
  Symmetric = false
FEATURE [Part::Feature] Face130
  shape: bbox 10 x 16.5 x 2e-07 mm, 1 faces, 0 solids (baked)
FEATURE [Part::Revolution] Revolve139  label="plugHousing072"
  Angle = 360
  Axis = (0,1,0)
  Base = (0,0,0)
  FaceMakerClass = Part::FaceMakerBullseye
  Placement = pos=(0,0,36.15) rot=(0,0,1;0rad)
  Solid = false
  Source = -> Face130
  Symmetric = false
FEATURE [Part::Feature] Face131
  shape: bbox 10 x 16.5 x 2e-07 mm, 1 faces, 0 solids (baked)
FEATURE [Part::Revolution] Revolve135  label="plugHousing068"
  Angle = 360
  Axis = (0,1,0)
  Base = (0,0,0)
  FaceMakerClass = Part::FaceMakerBullseye
  Placement = pos=(0,0,36.15) rot=(0,0,1;0rad)
  Solid = false
  Source = -> Face131
  Symmetric = false
FEATURE [Part::MultiFuse] Fusion112  label="plugHousing078"
  Placement = pos=(0,0,0) rot=(0,0,1;1.5708rad)
  Shapes = -> [Revolve135,Revolve139]
FEATURE [Part::Feature] Face132
  shape: bbox 10 x 16.5 x 2e-07 mm, 1 faces, 0 solids (baked)
FEATURE [Part::Revolution] Revolve141  label="plugHousing074"
  Angle = 360
  Axis = (0,1,0)
  Base = (0,0,0)
  FaceMakerClass = Part::FaceMakerBullseye
  Placement = pos=(0,0,36.15) rot=(0,0,1;0rad)
  Solid = false
  Source = -> Face132
  Symmetric = false
FEATURE [Part::MultiFuse] Fusion110  label="plugHousing076"
  Placement = pos=(0,0,0) rot=(0,0,1;1.5708rad)
  Shapes = -> [Revolve141,Revolve140]
FEATURE [Part::Feature] Face133
  shape: bbox 10 x 16.5 x 2e-07 mm, 1 faces, 0 solids (baked)
FEATURE [Part::Revolution] Revolve136  label="plugHousing069"
  Angle = 360
  Axis = (0,1,0)
  Base = (0,0,0)
  FaceMakerClass = Part::FaceMakerBullseye
  Placement = pos=(0,0,36.15) rot=(0,0,1;0rad)
  Solid = false
  Source = -> Face133
  Symmetric = false
FEATURE [Part::MultiFuse] Fusion106  label="plugHousing064"
  Placement = pos=(0,0,0) rot=(0,0,1;1.5708rad)
  Shapes = -> [Revolve138,Revolve136]
FEATURE [Part::MultiFuse] Fusion108  label="plugHousing066"
  Placement = pos=(0,19,0) rot=(0,0,1;3.14159rad)
  Shapes = -> [Fusion106,Fusion112]
FEATURE [Part::Feature] Face134
  shape: bbox 10 x 16.5 x 2e-07 mm, 1 faces, 0 solids (baked)
FEATURE [Part::Revolution] Revolve142  label="plugHousing075"
  Angle = 360
  Axis = (0,1,0)
  Base = (0,0,0)
  FaceMakerClass = Part::FaceMakerBullseye
  Placement = pos=(0,0,36.15) rot=(0,0,1;0rad)
  Solid = false
  Source = -> Face134
  Symmetric = false
FEATURE [Part::MultiFuse] Fusion107  label="plugHousing065"
  Placement = pos=(0,0,0) rot=(0,0,1;1.5708rad)
  Shapes = -> [Revolve137,Revolve142]
FEATURE [Part::MultiFuse] Fusion111  label="plugHousing077"
  Placement = pos=(0,19,0) rot=(0,0,1;3.14159rad)
  Shapes = -> [Fusion110,Fusion107]
FEATURE [Part::MultiFuse] Fusion109  label="plugHousing067"
  Placement = pos=(131.236,0,-0.15) rot=(0,0,1;0rad)
  Shapes = -> [Fusion108,Fusion111]
FEATURE [Part::MultiFuse] Fusion113  label="plugHousing079"
  Shapes = -> [Fillet043,Fusion109]
FEATURE [Part::Feature] Face135
  shape: bbox 3.5 x 17.8 x 2e-07 mm, 1 faces, 0 solids (baked)
FEATURE [Part::Revolution] Revolve143  label="removeToCreateScrewAndThreadedInsertHole049"
  Angle = 360
  Axis = (0,1,0)
  Base = (0,0,0)
  FaceMakerClass = Part::FaceMakerBullseye
  Placement = pos=(12.5,0,10) rot=(0,0,1;0rad)
  Solid = false
  Source = -> Face135
  Symmetric = false
FEATURE [Part::Feature] Face136
  shape: bbox 3.5 x 17.8 x 2e-07 mm, 1 faces, 0 solids (baked)
FEATURE [Part::Revolution] Revolve144  label="removeToCreateScrewAndThreadedInsertHole050"
  Angle = 360
  Axis = (0,1,0)
  Base = (0,0,0)
  FaceMakerClass = Part::FaceMakerBullseye
  Placement = pos=(12.5,0,62) rot=(0,0,1;0rad)
  Solid = false
  Source = -> Face136
  Symmetric = false
FEATURE [Part::Feature] Face137
  shape: bbox 3.5 x 17.8 x 2e-07 mm, 1 faces, 0 solids (baked)
FEATURE [Part::Revolution] Revolve145  label="removeToCreateScrewAndThreadedInsertHole051"
  Angle = 360
  Axis = (0,1,0)
  Base = (0,0,0)
  FaceMakerClass = Part::FaceMakerBullseye
  Placement = pos=(89.5,0,68.5) rot=(0,0,1;0rad)
  Solid = false
  Source = -> Face137
  Symmetric = false
FEATURE [Part::Feature] Face138
  shape: bbox 3.5 x 17.8 x 2e-07 mm, 1 faces, 0 solids (baked)
FEATURE [Part::Revolution] Revolve146  label="removeToCreateScrewAndThreadedInsertHole052"
  Angle = 360
  Axis = (0,1,0)
  Base = (0,0,0)
  FaceMakerClass = Part::FaceMakerBullseye
  Placement = pos=(89.5,0,3.5) rot=(0,0,1;0rad)
  Solid = false
  Source = -> Face138
  Symmetric = false
FEATURE [Part::Feature] Face139
  shape: bbox 3.5 x 17.8 x 2e-07 mm, 1 faces, 0 solids (baked)
FEATURE [Part::Revolution] Revolve147  label="removeToCreateScrewAndThreadedInsertHole053"
  Angle = 360
  Axis = (0,1,0)
  Base = (0,0,0)
  FaceMakerClass = Part::FaceMakerBullseye
  Placement = pos=(109.5,4.7,3.5) rot=(0,0,1;0rad)
  Solid = false
  Source = -> Face139
  Symmetric = false
FEATURE [Part::Feature] Face140
  shape: bbox 3.5 x 17.8 x 2e-07 mm, 1 faces, 0 solids (baked)
FEATURE [Part::Revolution] Revolve148  label="removeToCreateScrewAndThreadedInsertHole054"
  Angle = 360
  Axis = (0,1,0)
  Base = (0,0,0)
  FaceMakerClass = Part::FaceMakerBullseye
  Placement = pos=(109.5,4.7,68.5) rot=(0,0,1;0rad)
  Solid = false
  Source = -> Face140
  Symmetric = false
FEATURE [Part::MultiFuse] Fusion114  label="removeToCreateScrewAndThreadedInsertHole055"
  Shapes = -> [Revolve148,Revolve147,Revolve146,Revolve145,Revolve144,Revolve143]
FEATURE [Part::Cut] Cut047  label="casePillars004"
  Base = -> Cut037
  Tool = -> Fusion114
FEATURE [Part::Feature] Face141
  shape: bbox 3.5 x 17.8 x 2e-07 mm, 1 faces, 0 solids (baked)
FEATURE [Part::Feature] Face142
  shape: bbox 3.5 x 17.8 x 2e-07 mm, 1 faces, 0 solids (baked)
FEATURE [Part::Feature] Face143
  shape: bbox 3.5 x 17.8 x 2e-07 mm, 1 faces, 0 solids (baked)
FEATURE [Part::Revolution] Revolve149  label="removeToCreateScrewAndThreadedInsertHole057"
  Angle = 360
  Axis = (0,1,0)
  Base = (0,0,0)
  FaceMakerClass = Part::FaceMakerBullseye
  Placement = pos=(12.5,0,10) rot=(0,0,1;0rad)
  Solid = false
  Source = -> Face141
  Symmetric = false
FEATURE [Part::Feature] Face144
  shape: bbox 3.5 x 17.8 x 2e-07 mm, 1 faces, 0 solids (baked)
FEATURE [Part::Feature] Face145
  shape: bbox 3.5 x 17.8 x 2e-07 mm, 1 faces, 0 solids (baked)
FEATURE [Part::Feature] Face146
  shape: bbox 3.5 x 17.8 x 2e-07 mm, 1 faces, 0 solids (baked)
FEATURE [Part::Revolution] Revolve150  label="removeToCreateScrewAndThreadedInsertHole058"
  Angle = 360
  Axis = (0,1,0)
  Base = (0,0,0)
  FaceMakerClass = Part::FaceMakerBullseye
  Placement = pos=(12.5,0,62) rot=(0,0,1;0rad)
  Solid = false
  Source = -> Face146
  Symmetric = false
FEATURE [Part::Revolution] Revolve151  label="removeToCreateScrewAndThreadedInsertHole059"
  Angle = 360
  Axis = (0,1,0)
  Base = (0,0,0)
  FaceMakerClass = Part::FaceMakerBullseye
  Placement = pos=(89.5,0,68.5) rot=(0,0,1;0rad)
  Solid = false
  Source = -> Face143
  Symmetric = false
FEATURE [Part::Revolution] Revolve152  label="removeToCreateScrewAndThreadedInsertHole060"
  Angle = 360
  Axis = (0,1,0)
  Base = (0,0,0)
  FaceMakerClass = Part::FaceMakerBullseye
  Placement = pos=(89.5,0,3.5) rot=(0,0,1;0rad)
  Solid = false
  Source = -> Face142
  Symmetric = false
FEATURE [Part::Revolution] Revolve153  label="removeToCreateScrewAndThreadedInsertHole061"
  Angle = 360
  Axis = (0,1,0)
  Base = (0,0,0)
  FaceMakerClass = Part::FaceMakerBullseye
  Placement = pos=(109.5,4.7,3.5) rot=(0,0,1;0rad)
  Solid = false
  Source = -> Face145
  Symmetric = false
FEATURE [Part::Revolution] Revolve154  label="removeToCreateScrewAndThreadedInsertHole062"
  Angle = 360
  Axis = (0,1,0)
  Base = (0,0,0)
  FaceMakerClass = Part::FaceMakerBullseye
  Placement = pos=(109.5,4.7,68.5) rot=(0,0,1;0rad)
  Solid = false
  Source = -> Face144
  Symmetric = false
FEATURE [Part::MultiFuse] Fusion115  label="removeToCreateScrewAndThreadedInsertHole056"
  Shapes = -> [Revolve154,Revolve153,Revolve152,Revolve151,Revolve150,Revolve149]
FEATURE [Part::Feature] Face147
  shape: bbox 9.8 x 26.5 x 2e-07 mm, 1 faces, 0 solids (baked)
FEATURE [Part::Revolution] Revolve155
  Angle = 360
  Axis = (0,1,0)
  Base = (0,0,0)
  FaceMakerClass = Part::FaceMakerBullseye
  Placement = pos=(0,0,0) rot=(0,0,1;1.5708rad)
  Solid = false
  Source = -> Face147
  Symmetric = false
FEATURE [Part::Feature] Face148
  shape: bbox 9.8 x 26.5 x 2e-07 mm, 1 faces, 0 solids (baked)
FEATURE [Part::Revolution] Revolve156
  Angle = 360
  Axis = (0,1,0)
  Base = (0,0,0)
  FaceMakerClass = Part::FaceMakerBullseye
  Placement = pos=(0,0,0) rot=(0,0,1;1.5708rad)
  Solid = false
  Source = -> Face148
  Symmetric = false
FEATURE [Part::MultiFuse] Fusion116
  Placement = pos=(-18,19,36) rot=(0,0,1;0rad)
  Shapes = -> [Revolve156,Revolve155]
FEATURE [Part::Box] Box029  label="Cube016"
  AttacherType = Attacher::AttachEngine3D
  Height = 28
  Length = 3
  Placement = pos=(110.7,19,22) rot=(0,0,1;0rad)
  Width = 15.7
FEATURE [Part::Cylinder] Cylinder046
  Angle = 360
  AttacherType = Attacher::AttachEngine3D
  Height = 10
  Placement = pos=(0,0,36.15) rot=(0,0,1;0rad)
  Radius = 4
FEATURE [Part::Cylinder] Cylinder047
  Angle = 360
  AttacherType = Attacher::AttachEngine3D
  Height = 20
  Placement = pos=(0,0,36.15) rot=(0,0,1;0rad)
  Radius = 10.3
FEATURE [Part::MultiFuse] Fusion117  label="removeToCreteHoleForPlugHousing041"
  Placement = pos=(70,19,36) rot=(0,1,0;1.5708rad)
  Shapes = -> [Cylinder047,Cylinder046]
FEATURE [Part::Cut] Cut049  label="plugHousingTab004"
  Base = -> Box029
  Placement = pos=(-107.4,-14,0) rot=(0,0,1;0rad)
  Tool = -> Fusion117
FEATURE [Part::Box] Box030  label="Cube017"
  AttacherType = Attacher::AttachEngine3D
  Height = 28
  Length = 3
  Placement = pos=(110.7,19,22) rot=(0,0,1;0rad)
  Width = 15.7
FEATURE [Part::Cylinder] Cylinder048
  Angle = 360
  AttacherType = Attacher::AttachEngine3D
  Height = 10
  Placement = pos=(0,0,36.15) rot=(0,0,1;0rad)
  Radius = 4
FEATURE [Part::Cylinder] Cylinder049
  Angle = 360
  AttacherType = Attacher::AttachEngine3D
  Height = 20
  Placement = pos=(0,0,36.15) rot=(0,0,1;0rad)
  Radius = 10.3
FEATURE [Part::MultiFuse] Fusion118  label="removeToCreteHoleForPlugHousing042"
  Placement = pos=(70,19,36) rot=(0,1,0;1.5708rad)
  Shapes = -> [Cylinder049,Cylinder048]
FEATURE [Part::Cut] Cut050  label="plugHousingTab005"
  Base = -> Box030
  Placement = pos=(-107.4,-14,0) rot=(0,0,1;0rad)
  Tool = -> Fusion118
FEATURE [Part::MultiFuse] Fusion119
  Placement = pos=(9.6,23,0) rot=(0,0,1;3.14159rad)
  Shapes = -> [Cut049,Cut050]
FEATURE [Part::Box] Box031  label="Cube018"
  AttacherType = Attacher::AttachEngine3D
  Height = 10
  Length = 3
  Placement = pos=(3.3,4,12) rot=(0,0,1;0rad)
  Width = 10
FEATURE [Part::Fillet] Fillet044
  Base = -> Box031
  Edges = 1 edges r=2: [Edge11]
FEATURE [Part::Box] Box032  label="Cube019"
  AttacherType = Attacher::AttachEngine3D
  Height = 10
  Length = 3
  Placement = pos=(3.3,4,50) rot=(0,0,1;0rad)
  Width = 10
FEATURE [Part::Fillet] Fillet045
  Base = -> Box032
  Edges = 1 edges r=2: [Edge12]
FEATURE [Part::Box] Box033  label="Cube020"
  AttacherType = Attacher::AttachEngine3D
  Height = 28
  Length = 4
  Placement = pos=(5,0,22) rot=(0,0,1;0rad)
  Width = 10
FEATURE [Part::Fillet] Fillet046
  Base = -> Box033
  Edges = 1 edges r=1: [Edge7]
FEATURE [Part::Fillet] Fillet047
  Base = -> Fillet046
  Edges = 1 edges r=2: [Edge5]
FEATURE [Part::Fillet] Fillet048
  Base = -> Fillet047
  Edges = 1 edges r=2: [Edge2]
FEATURE [Part::Cylinder] Cylinder050
  Angle = 360
  AttacherType = Attacher::AttachEngine3D
  Height = 20
  Placement = pos=(0,0,36.15) rot=(0,0,1;0rad)
  Radius = 8.2
FEATURE [Part::Cylinder] Cylinder051
  Angle = 360
  AttacherType = Attacher::AttachEngine3D
  Height = 10
  Placement = pos=(0,0,36.15) rot=(0,0,1;0rad)
  Radius = 4
FEATURE [Part::MultiFuse] Fusion120  label="removeToCreteHoleForPlugHousing043"
  Placement = pos=(-42,19,36) rot=(0,1,0;1.5708rad)
  Shapes = -> [Cylinder050,Cylinder051]
FEATURE [Sketcher::SketchObject] Sketch067  label="topSketch018"
  FullyConstrained = true
  sketch-geometry (4):
    g0: LineSegment StartX=16.8446 StartY=31.512 StartZ=0 EndX=16.3251 EndY=34.4666 EndZ=0
    g1: ArcOfCircle CenterX=19 CenterY=19.2524 CenterZ=0 NormalX=0 NormalY=0 NormalZ=1 AngleXU=0 Radius=15.4476 StartAngle=1.74483 EndAngle=2.72717
    g2: ArcOfCircle CenterX=19 CenterY=19.2524 CenterZ=0 NormalX=0 NormalY=0 NormalZ=1 AngleXU=0 Radius=12.4476 StartAngle=1.74483 EndAngle=2.73189
    g3: LineSegment StartX=4.86004 StartY=25.4725 StartZ=0 EndX=7.58253 EndY=24.2107 EndZ=0
  constraints (7):
    c: Block(g0)
    c: Coincident(g1,g0)
    c: Coincident(g2,g0)
    c: Coincident(g3,g1)
    c: Coincident(g3,g2)
    c: Block(g1)
    c: Block(g2)
FEATURE [Part::Extrusion] Extrude058
  Base = -> Sketch067
  Dir = (0,0,1)
  DirMode = 2
  FaceMakerClass = Part::FaceMakerBullseye
  LengthFwd = 10
  LengthRev = 0
  Placement = pos=(0,0,31) rot=(0,0,1;0rad)
  Solid = true
  Symmetric = false
FEATURE [Part::Cut] Cut051
  Base = -> Extrude058
  Tool = -> Fusion120
FEATURE [Part::Fillet] Fillet049
  Base = -> Cut051
  Edges = 1 edges r=2: [Edge1]
FEATURE [Part::Fillet] Fillet050
  Base = -> Fillet049
  Edges = 1 edges r=2.5: [Edge1]
FEATURE [Part::Fillet] Fillet051
  Base = -> Fillet050
  Edges = 1 edges r=2.5: [Edge2]
FEATURE [Part::MultiFuse] Fusion121  label="wireHolder003"
  Shapes = -> [Fusion116,Fillet051]
FEATURE [Part::MultiFuse] Fusion122
  Shapes = -> [Fillet045,Fusion121]
FEATURE [Part::MultiFuse] Fusion123  label="wireHolder004"
  Shapes = -> [Fusion122,Fillet048]
FEATURE [Part::MultiFuse] Fusion124  label="wireHolder005"
  Shapes = -> [Fillet044,Fusion119,Fusion123]
FEATURE [Sketcher::SketchObject] Sketch068  label="topSketch019"
  FullyConstrained = true
  sketch-geometry (6):
    g0: LineSegment StartX=19 StartY=38 StartZ=0 EndX=117 EndY=38 EndZ=0
    g1: ArcOfCircle CenterX=19 CenterY=19 CenterZ=0 NormalX=0 NormalY=0 NormalZ=1 AngleXU=0 Radius=19 StartAngle=1.5708 EndAngle=3.14159
    g2: LineSegment StartX=117 StartY=38 StartZ=0 EndX=117 EndY=19 EndZ=0
    g3: LineSegment StartX=98 StartY=1.0161e-12 StartZ=0 EndX=5.22862e-06 EndY=1.0161e-12 EndZ=0
    g4: LineSegment StartX=5.22862e-06 StartY=19 StartZ=0 EndX=5.22862e-06 EndY=1.0161e-12 EndZ=0
    g5: ArcOfCircle CenterX=98 CenterY=19 CenterZ=0 NormalX=0 NormalY=0 NormalZ=1 AngleXU=0 Radius=19 StartAngle=4.71239 EndAngle=6.28319
  constraints (16):
    c: Horizontal(g0)
    c: Distance(g0) = 98
    c: Coincident(g1,g0)
    c: Block(g1)
    c: Coincident(g2,g0)
    c: Vertical(g2)
    c: Distance(g2) = 19
    c: Horizontal(g3)
    c: Coincident(g4,g1)
    c: Vertical(g4)
    c: Coincident(g3,g4)
    c: Block(g3)
    c: Coincident(g5,g2)
    c: Coincident(g5,g3)
    c: Block(g0)
    c: Block(g5)
FEATURE [Part::Extrusion] Extrude059  label="sideA002"
  Base = -> Sketch068
  Dir = (0,0,1)
  DirMode = 2
  FaceMakerClass = Part::FaceMakerBullseye
  LengthFwd = 3
  LengthRev = 0
  Placement = pos=(0,0,-2.7) rot=(0,0,1;0rad)
  Solid = true
  Symmetric = false
FEATURE [Sketcher::SketchObject] Sketch069  label="topSketch020"
  FullyConstrained = true
  sketch-geometry (6):
    g0: LineSegment StartX=19 StartY=38 StartZ=0 EndX=117 EndY=38 EndZ=0
    g1: ArcOfCircle CenterX=19 CenterY=19 CenterZ=0 NormalX=0 NormalY=0 NormalZ=1 AngleXU=0 Radius=19 StartAngle=1.5708 EndAngle=3.14159
    g2: LineSegment StartX=117 StartY=38 StartZ=0 EndX=117 EndY=19 EndZ=0
    g3: LineSegment StartX=98 StartY=1.0161e-12 StartZ=0 EndX=5.22862e-06 EndY=1.0161e-12 EndZ=0
    g4: LineSegment StartX=5.22862e-06 StartY=19 StartZ=0 EndX=5.22862e-06 EndY=1.0161e-12 EndZ=0
    g5: ArcOfCircle CenterX=98 CenterY=19 CenterZ=0 NormalX=0 NormalY=0 NormalZ=1 AngleXU=0 Radius=19 StartAngle=4.71239 EndAngle=6.28319
  constraints (16):
    c: Horizontal(g0)
    c: Distance(g0) = 98
    c: Coincident(g1,g0)
    c: Block(g1)
    c: Coincident(g2,g0)
    c: Vertical(g2)
    c: Distance(g2) = 19
    c: Horizontal(g3)
    c: Coincident(g4,g1)
    c: Vertical(g4)
    c: Coincident(g3,g4)
    c: Block(g3)
    c: Coincident(g5,g2)
    c: Coincident(g5,g3)
    c: Block(g0)
    c: Block(g5)
FEATURE [Part::Extrusion] Extrude060  label="sideB002"
  Base = -> Sketch069
  Dir = (0,0,1)
  DirMode = 2
  FaceMakerClass = Part::FaceMakerBullseye
  LengthFwd = 3
  LengthRev = 0
  Placement = pos=(0,0,71.7) rot=(0,0,1;0rad)
  Solid = true
  Symmetric = false
FEATURE [Part::MultiFuse] Fusion127  label="removeFromBottom001"
  Placement = pos=(2,0,0) rot=(0,0,1;0rad)
  Shapes = -> [Extrude059,Extrude060]
FEATURE [Part::Cylinder] Cylinder052
  Angle = 360
  AttacherType = Attacher::AttachEngine3D
  Height = 20
  Placement = pos=(0,0,36.15) rot=(0,0,1;0rad)
  Radius = 14
FEATURE [Part::Cylinder] Cylinder053
  Angle = 360
  AttacherType = Attacher::AttachEngine3D
  Height = 10
  Placement = pos=(0,0,36.15) rot=(0,0,1;0rad)
  Radius = 4
FEATURE [Part::MultiFuse] Fusion128  label="removeToCreteHoleForPlugHousing044"
  Placement = pos=(70,19,36) rot=(0,1,0;1.5708rad)
  Shapes = -> [Cylinder052,Cylinder053]
FEATURE [Part::Cut] Cut052  label="bottom011"
  Base = -> Extrude043
  Tool = -> Fusion128
FEATURE [Part::Cut] Cut054  label="bottom012"
  Base = -> Cut052
  Tool = -> Fusion115
FEATURE [Sketcher::SketchObject] Sketch070
  FullyConstrained = true
  Placement = pos=(117,19,0) rot=(0.57735,0.57735,0.57735;2.0944rad)
  sketch-geometry (48):
    g0: LineSegment StartX=-49.19 StartY=69.25 StartZ=0 EndX=-49.19 EndY=66.25 EndZ=0
    g1: LineSegment StartX=-49.19 StartY=63.5 StartZ=0 EndX=-49.19 EndY=60.5 EndZ=0
    g2: LineSegment StartX=-49.19 StartY=57.75 StartZ=0 EndX=-49.19 EndY=54.75 EndZ=0
    g3: LineSegment StartX=-49.19 StartY=52 StartZ=0 EndX=-49.19 EndY=49 EndZ=0
    g4: LineSegment StartX=-49.19 StartY=46.25 StartZ=0 EndX=-49.19 EndY=43.25 EndZ=0
    g5: LineSegment StartX=-49.19 StartY=40.5 StartZ=0 EndX=-49.19 EndY=37.5 EndZ=0
    g6: LineSegment StartX=-49.19 StartY=34.5 StartZ=0 EndX=-49.19 EndY=31.5 EndZ=0
    g7: LineSegment StartX=-49.19 StartY=28.75 StartZ=0 EndX=-49.19 EndY=25.75 EndZ=0
    g8: LineSegment StartX=-49.19 StartY=23 StartZ=0 EndX=-49.19 EndY=20 EndZ=0
    g9: LineSegment StartX=-49.19 StartY=17.25 StartZ=0 EndX=-49.19 EndY=14.25 EndZ=0
    g10: LineSegment StartX=-49.19 StartY=11.5 StartZ=0 EndX=-49.19 EndY=8.5 EndZ=0
    g11: LineSegment StartX=-49.19 StartY=5.75 StartZ=0 EndX=-49.19 EndY=2.75 EndZ=0
    g12: ArcOfCircle CenterX=-1.5 CenterY=67.75 CenterZ=0 NormalX=0 NormalY=0 NormalZ=1 AngleXU=0 Radius=1.5 StartAngle=4.71239 EndAngle=7.85398
    g13: ArcOfCircle CenterX=-1.5 CenterY=62 CenterZ=0 NormalX=0 NormalY=0 NormalZ=1 AngleXU=0 Radius=1.5 StartAngle=4.71239 EndAngle=7.85398
    g14: ArcOfCircle CenterX=-1.5 CenterY=56.25 CenterZ=0 NormalX=0 NormalY=0 NormalZ=1 AngleXU=0 Radius=1.5 StartAngle=4.71239 EndAngle=7.85398
    g15: ArcOfCircle CenterX=-11.49 CenterY=50.5 CenterZ=0 NormalX=0 NormalY=0 NormalZ=1 AngleXU=0 Radius=1.5 StartAngle=4.71239 EndAngle=7.85398
    g16: ArcOfCircle CenterX=-16.28 CenterY=44.75 CenterZ=0 NormalX=0 NormalY=0 NormalZ=1 AngleXU=0 Radius=1.5 StartAngle=4.71239 EndAngle=7.85398
    g17: ArcOfCircle CenterX=-18.2337 CenterY=39 CenterZ=0 NormalX=0 NormalY=0 NormalZ=1 AngleXU=0 Radius=1.5 StartAngle=4.71485 EndAngle=7.85398
    g18: ArcOfCircle CenterX=-16.2837 CenterY=27.25 CenterZ=0 NormalX=0 NormalY=0 NormalZ=1 AngleXU=0 Radius=1.5 StartAngle=4.71485 EndAngle=7.85398
    g19: ArcOfCircle CenterX=-18.2337 CenterY=33 CenterZ=0 NormalX=0 NormalY=0 NormalZ=1 AngleXU=0 Radius=1.5 StartAngle=4.71485 EndAngle=7.85398
    g20: ArcOfCircle CenterX=-11.49 CenterY=21.5 CenterZ=0 NormalX=0 NormalY=0 NormalZ=1 AngleXU=0 Radius=1.5 StartAngle=4.71239 EndAngle=7.85398
    g21: ArcOfCircle CenterX=-1.5 CenterY=4.25 CenterZ=0 NormalX=0 NormalY=0 NormalZ=1 AngleXU=0 Radius=1.5 StartAngle=4.71239 EndAngle=7.85398
    g22: ArcOfCircle CenterX=-1.5 CenterY=10 CenterZ=0 NormalX=0 NormalY=0 NormalZ=1 AngleXU=0 Radius=1.5 StartAngle=4.71239 EndAngle=7.85398
    g23: ArcOfCircle CenterX=-1.5 CenterY=15.75 CenterZ=0 NormalX=0 NormalY=0 NormalZ=1 AngleXU=0 Radius=1.5 StartAngle=4.71239 EndAngle=7.85398
    g24: LineSegment StartX=-49.19 StartY=69.25 StartZ=0 EndX=-1.5 EndY=69.25 EndZ=0
    g25: LineSegment StartX=-49.19 StartY=66.25 StartZ=0 EndX=-1.5 EndY=66.25 EndZ=0
    g26: LineSegment StartX=-49.19 StartY=63.5 StartZ=0 EndX=-1.5 EndY=63.5 EndZ=0
    g27: LineSegment StartX=-49.19 StartY=60.5 StartZ=0 EndX=-1.5 EndY=60.5 EndZ=0
    g28: LineSegment StartX=-49.19 StartY=57.75 StartZ=0 EndX=-1.5 EndY=57.75 EndZ=0
    g29: LineSegment StartX=-49.19 StartY=54.75 StartZ=0 EndX=-1.5 EndY=54.75 EndZ=0
    g30: LineSegment StartX=-49.19 StartY=52 StartZ=0 EndX=-11.49 EndY=52 EndZ=0
    g31: LineSegment StartX=-49.19 StartY=49 StartZ=0 EndX=-11.49 EndY=49 EndZ=0
    g32: LineSegment StartX=-49.19 StartY=46.25 StartZ=0 EndX=-16.28 EndY=46.25 EndZ=0
    g33: LineSegment StartX=-49.19 StartY=43.25 StartZ=0 EndX=-16.28 EndY=43.25 EndZ=0
    g34: LineSegment StartX=-49.19 StartY=40.5 StartZ=0 EndX=-18.2337 EndY=40.5 EndZ=0
    g35: LineSegment StartX=-49.19 StartY=37.5 StartZ=0 EndX=-18.23 EndY=37.5 EndZ=0
    g36: LineSegment StartX=-49.19 StartY=34.5 StartZ=0 EndX=-18.2337 EndY=34.5 EndZ=0
    g37: LineSegment StartX=-49.19 StartY=31.5 StartZ=0 EndX=-18.23 EndY=31.5 EndZ=0
    g38: LineSegment StartX=-49.19 StartY=28.75 StartZ=0 EndX=-16.2837 EndY=28.75 EndZ=0
    g39: LineSegment StartX=-49.19 StartY=25.75 StartZ=0 EndX=-16.28 EndY=25.75 EndZ=0
    g40: LineSegment StartX=-49.19 StartY=23 StartZ=0 EndX=-11.49 EndY=23 EndZ=0
    g41: LineSegment StartX=-49.19 StartY=20 StartZ=0 EndX=-11.49 EndY=20 EndZ=0
    g42: LineSegment StartX=-49.19 StartY=17.25 StartZ=0 EndX=-1.5 EndY=17.25 EndZ=0
    g43: LineSegment StartX=-49.19 StartY=14.25 StartZ=0 EndX=-1.5 EndY=14.25 EndZ=0
    g44: LineSegment StartX=-49.19 StartY=11.5 StartZ=0 EndX=-1.5 EndY=11.5 EndZ=0
    g45: LineSegment StartX=-49.19 StartY=8.5 StartZ=0 EndX=-1.5 EndY=8.5 EndZ=0
    g46: LineSegment StartX=-49.19 StartY=5.75 StartZ=0 EndX=-1.5 EndY=5.75 EndZ=0
    g47: LineSegment StartX=-49.19 StartY=2.75 StartZ=0 EndX=-1.5 EndY=2.75 EndZ=0
  constraints (120):
    c: Vertical(g0)
    c: Distance(g0) = 3
    c: Block(g0)
    c: Vertical(g1)
    c: Distance(g1) = 3
    c: Vertical(g2)
    c: Equal(g0,g2) = 3
    c: Block(g2)
    c: Vertical(g3)
    c: Equal(g1,g3) = 3
    c: Vertical(g4)
    c: Equal(g0,g4) = 3
    c: Block(g4)
    c: Vertical(g5)
    c: Equal(g1,g5) = 3
    c: Vertical(g6)
    c: Equal(g0,g6) = 3
    c: Block(g6)
    c: Vertical(g7)
    c: Equal(g1,g7) = 3
    c: Vertical(g8)
    c: Equal(g0,g8) = 3
    c: Block(g8)
    c: Vertical(g9)
    c: Equal(g1,g9) = 3
    c: Vertical(g10)
    c: Equal(g0,g10) = 3
    c: Block(g10)
    c: Vertical(g11)
    c: Equal(g1,g11) = 3
    c: Block(g12)
    c: Block(g13)
    c: Block(g14)
    c: Block(g15)
    c: Block(g16)
    c: Block(g17)
    c: Block(g18)
    c: Block(g19)
    c: Block(g20)
    c: Block(g21)
    c: Block(g22)
    c: Block(g23)
    c: Block(g11)
    c: Block(g9)
    c: Block(g7)
    c: Block(g5)
    c: Block(g3)
    c: Block(g1)
    c: Coincident(g24,g0)
    c: Coincident(g24,g12)
    c: Horizontal(g24)
    c: Coincident(g25,g0)
    c: Coincident(g25,g12)
    c: Horizontal(g25)
    c: Coincident(g26,g1)
    c: Coincident(g26,g13)
    c: Horizontal(g26)
    c: Coincident(g27,g1)
    c: Coincident(g27,g13)
    c: Horizontal(g27)
    c: Coincident(g28,g2)
    c: Coincident(g28,g14)
    c: Horizontal(g28)
    c: Coincident(g29,g2)
    c: Coincident(g29,g14)
    c: Horizontal(g29)
    c: Coincident(g30,g3)
    c: Coincident(g30,g15)
    c: Horizontal(g30)
    c: Coincident(g31,g3)
    c: Coincident(g31,g15)
    c: Horizontal(g31)
    c: Coincident(g32,g4)
    c: Coincident(g32,g16)
    c: Horizontal(g32)
    c: Coincident(g33,g4)
    c: Coincident(g33,g16)
    c: Horizontal(g33)
    c: Coincident(g34,g5)
    c: Coincident(g34,g17)
    c: Horizontal(g34)
    c: Coincident(g35,g5)
    c: Coincident(g35,g17)
    c: Horizontal(g35)
    c: Coincident(g36,g6)
    c: Coincident(g36,g19)
    c: Horizontal(g36)
    c: Coincident(g37,g6)
    c: Coincident(g37,g19)
    c: Horizontal(g37)
    c: Coincident(g38,g7)
    c: Coincident(g38,g18)
    c: Horizontal(g38)
    c: Coincident(g39,g7)
    c: Coincident(g39,g18)
    c: Horizontal(g39)
    c: Coincident(g40,g8)
    c: Coincident(g40,g20)
    c: Horizontal(g40)
    c: Coincident(g41,g8)
    c: Coincident(g41,g20)
    c: Horizontal(g41)
    c: Coincident(g42,g9)
    c: Coincident(g42,g23)
    c: Horizontal(g42)
    c: Coincident(g43,g9)
    c: Coincident(g43,g23)
    c: Horizontal(g43)
    c: Coincident(g44,g10)
    c: Coincident(g44,g22)
    c: Horizontal(g44)
    c: Coincident(g45,g10)
    c: Coincident(g45,g22)
    c: Horizontal(g45)
    c: Coincident(g46,g11)
    c: Coincident(g46,g21)
    c: Horizontal(g46)
    c: Coincident(g47,g11)
    c: Coincident(g47,g21)
    c: Horizontal(g47)
FEATURE [Part::Extrusion] Extrude061
  Base = -> Sketch070
  Dir = (1,0,0)
  DirMode = 2
  FaceMakerClass = Part::FaceMakerBullseye
  LengthFwd = 23
  LengthRev = 0
  Placement = pos=(-19,0,0) rot=(0,0,1;0rad)
  Solid = true
  Symmetric = false
FEATURE [Part::Fillet] Fillet052  label="removeToCreateVentalationHoles002"
  Base = -> Extrude061
  Edges = <same value as first occurrence — deduplicated (x6 in doc)>
  Placement = pos=(7,0.02,0) rot=(0,0,1;0rad)
FEATURE [Part::MultiFuse] Fusion130  label="bottom013"
  Shapes = -> [Cut054,Cut034]
FEATURE [Part::Cut] Cut055
  Base = -> Fusion130
  Tool = -> Fillet052
FEATURE [Part::Cylinder] Cylinder054
  Angle = 360
  AttacherType = Attacher::AttachEngine3D
  Height = 20
  Placement = pos=(0,0,36.15) rot=(0,0,1;0rad)
  Radius = 4
FEATURE [Sketcher::SketchObject] Sketch071  label="bottomSketch002"
  FullyConstrained = true
  sketch-geometry (32):
    g0: LineSegment StartX=3.3 StartY=-6.03275e-07 StartZ=0 EndX=98 EndY=-6.03275e-07 EndZ=0
    g1: ArcOfCircle CenterX=98 CenterY=19 CenterZ=0 NormalX=0 NormalY=0 NormalZ=1 AngleXU=0 Radius=19 StartAngle=4.71239 EndAngle=5.71103
    g2: LineSegment StartX=6.3 StartY=8 StartZ=0 EndX=3.3 EndY=8 EndZ=0
    g3: LineSegment StartX=3.3 StartY=8 StartZ=0 EndX=3.3 EndY=-6.03275e-07 EndZ=0
    g4: ArcOfCircle CenterX=8.3 CenterY=5 CenterZ=0 NormalX=0 NormalY=0 NormalZ=1 AngleXU=0 Radius=2 StartAngle=3.14159 EndAngle=4.71239
    g5: LineSegment StartX=6.3 StartY=8 StartZ=0 EndX=6.3 EndY=5 EndZ=0
    g6: ArcOfCircle CenterX=98 CenterY=19 CenterZ=0 NormalX=0 NormalY=0 NormalZ=1 AngleXU=0 Radius=12.7 StartAngle=4.71239 EndAngle=6.28319
    g7: LineSegment StartX=94.7 StartY=3 StartZ=0 EndX=8.3 EndY=3 EndZ=0
    g8-g12: Circle x5 (B-spline internal-alignment scaffolding for g13; pole/knot coordinates omitted)
    g13: BSplineCurve PolesCount=5 KnotsCount=3 Degree=3 IsPeriodic=0
    g14: GeomPoint X=98 Y=6.3 Z=0
    g15: GeomPoint X=96.3938 Y=4.71946 Z=0
    g16: GeomPoint X=94.7 Y=3 Z=0
    g17-g23: Circle x7 (B-spline internal-alignment scaffolding for g24; pole/knot coordinates omitted)
    g24: BSplineCurve PolesCount=7 KnotsCount=5 Degree=3 IsPeriodic=0
    g25-g29: GeomPoint x5 (B-spline internal-alignment scaffolding for g24; pole/knot coordinates omitted)
    g30: ArcOfCircle CenterX=98 CenterY=19 CenterZ=0 NormalX=0 NormalY=0 NormalZ=1 AngleXU=0 Radius=15.7 StartAngle=5.81226 EndAngle=6.28319
    g31: LineSegment StartX=110.7 StartY=19 StartZ=0 EndX=113.7 EndY=19 EndZ=0
  constraints (41):
    c: Horizontal(g0)
    c: Coincident(g1,g0)
    c: Block(g1)
    c: Horizontal(g2)
    c: Distance(g2) = 3
    c: Coincident(g3,g2)
    c: Vertical(g3)
    c: Coincident(g3,g0)
    c: Block(g4)
    c: Block(g2)
    c: Coincident(g5,g2)
    c: Coincident(g5,g4)
    c: Vertical(g5)
    c: Coincident(g6,g1)
    c: Block(g6)
    c: Coincident(g7,g4)
    c: Horizontal(g7)
    c: Block(g0)
    c: Block(g7)
    c: Block(g3)
    c: Coincident(g13,g6)
    c: Weight(g8) = 1
    c: Equal(g8, g9-g12) x4
    c: Coincident(g13,g7)
    c: InternalAlignment(g8-g12 -> g13) x5
    c: InternalAlignment(g14,g13)
    c: InternalAlignment(g15,g13)
    c: InternalAlignment(g16,g13)
    c: Block(g13)
    c: Weight(g17) = 1
    c: Equal(g17, g18-g23) x6
    c: Coincident(g24,g1)
    c: InternalAlignment(g17-g23 -> g24) x7
    c: InternalAlignment(g25-g29 -> g24) x5
    c: Block(g24)
    c: Coincident(g30,g24)
    c: Coincident(g31,g6)
    c: Coincident(g31,g30)
    c: Horizontal(g31)
    c: Block(g31)
    c: Block(g30)
FEATURE [Part::Extrusion] Extrude062  label="bottom014"
  Base = -> Sketch071
  Dir = (0,0,1)
  DirMode = 2
  FaceMakerClass = Part::FaceMakerBullseye
  LengthFwd = 71.4
  LengthRev = 0
  Placement = pos=(0,0,0.3) rot=(0,0,1;0rad)
  Solid = true
  Symmetric = false
FEATURE [Part::Fillet] Fillet054
  Base = -> Extrude062
  Edges = 1 edges r=2.4: [Edge17]
FEATURE [Part::Fillet] Fillet055  label="bottom015"
  Base = -> Fillet054
  Edges = 1 edges r=2.4: [Edge36]
FEATURE [Part::Cylinder] Cylinder055
  Angle = 360
  AttacherType = Attacher::AttachEngine3D
  Height = 10
  Placement = pos=(0,0,36.15) rot=(0,0,1;0rad)
  Radius = 4
FEATURE [Part::MultiFuse] Fusion131  label="removeToCreateHoleForPlugHousing002"
  Placement = pos=(70,19,36.15) rot=(0,1,0;1.5708rad)
  Shapes = -> [Cylinder054,Cylinder055]
FEATURE [Part::Cut] Cut056  label="Bottom001"
  Base = -> Fillet055
  Placement = pos=(9,0,0) rot=(0,0,1;0rad)
  Tool = -> Fusion131
FEATURE [Part::Cut] Cut057
  Base = -> Cut055
  Tool = -> Cut056
FEATURE [Sketcher::SketchObject] Sketch072  label="topSketch021"
  FullyConstrained = true
  sketch-geometry (4):
    g0: ArcOfCircle CenterX=105 CenterY=19 CenterZ=0 NormalX=0 NormalY=0 NormalZ=1 AngleXU=0 Radius=20.6155 StartAngle=5.54125 EndAngle=6.28319
    g1: ArcOfCircle CenterX=105 CenterY=19 CenterZ=0 NormalX=0 NormalY=0 NormalZ=1 AngleXU=0 Radius=13 StartAngle=5.54125 EndAngle=6.28319
    g2: LineSegment StartX=118 StartY=19 StartZ=0 EndX=125.616 EndY=19 EndZ=0
    g3: LineSegment StartX=114.583 StartY=10.2157 StartZ=0 EndX=120.197 EndY=5.06982 EndZ=0
  constraints (7):
    c: Block(g0)
    c: Block(g1)
    c: Coincident(g2,g1)
    c: Coincident(g2,g0)
    c: Horizontal(g2)
    c: Coincident(g3,g1)
    c: Coincident(g3,g0)
FEATURE [Part::Extrusion] Extrude063  label="bottomPlugHousingBit003"
  Base = -> Sketch072
  Dir = (0,0,1)
  DirMode = 2
  FaceMakerClass = Part::FaceMakerBullseye
  LengthFwd = 72
  LengthRev = 0
  Solid = true
  Symmetric = false
FEATURE [Part::Cylinder] Cylinder056
  Angle = 360
  AttacherType = Attacher::AttachEngine3D
  Height = 20
  Placement = pos=(0,0,36.15) rot=(0,0,1;0rad)
  Radius = 14.3
FEATURE [Part::Cylinder] Cylinder057
  Angle = 360
  AttacherType = Attacher::AttachEngine3D
  Height = 10
  Placement = pos=(0,0,36.15) rot=(0,0,1;0rad)
  Radius = 4
FEATURE [Part::Box] Box034  label="removeToCreteHoleForPlugHousing047"
  AttacherType = Attacher::AttachEngine3D
  Height = 28.6
  Length = 20
  Placement = pos=(106.15,0,21.7) rot=(0,0,1;0rad)
  Width = 19
FEATURE [Part::Cylinder] Cylinder058
  Angle = 360
  AttacherType = Attacher::AttachEngine3D
  Height = 20
  Placement = pos=(0,0,36.15) rot=(0,0,1;0rad)
  Radius = 14.3
FEATURE [Part::Cylinder] Cylinder059
  Angle = 360
  AttacherType = Attacher::AttachEngine3D
  Height = 10
  Placement = pos=(0,0,36.15) rot=(0,0,1;0rad)
  Radius = 4
FEATURE [Part::MultiFuse] Fusion134  label="removeToCreteHoleForPlugHousing046"
  Placement = pos=(70,19,36) rot=(0,1,0;1.5708rad)
  Shapes = -> [Cylinder058,Cylinder059]
FEATURE [Part::Cylinder] Cylinder060
  Angle = 360
  AttacherType = Attacher::AttachEngine3D
  Height = 20
  Placement = pos=(0,0,36.15) rot=(0,0,1;0rad)
  Radius = 14
FEATURE [Part::Cylinder] Cylinder061
  Angle = 360
  AttacherType = Attacher::AttachEngine3D
  Height = 10
  Placement = pos=(0,0,36.15) rot=(0,0,1;0rad)
  Radius = 4
FEATURE [Part::MultiFuse] Fusion135  label="removeToCreteHoleForPlugHousing048"
  Placement = pos=(70,19,36) rot=(0,1,0;1.5708rad)
  Shapes = -> [Cylinder060,Cylinder061]
FEATURE [Part::Box] Box035  label="removeToCreteHoleForPlugHousing049"
  AttacherType = Attacher::AttachEngine3D
  Height = 28.6
  Length = 20
  Placement = pos=(106.15,0,21.7) rot=(0,0,1;0rad)
  Width = 19
FEATURE [Part::MultiFuse] Fusion133  label="removeToCreteHoleForPlugHousing045"
  Placement = pos=(0,0,-28.3) rot=(0,0,1;0rad)
  Shapes = -> [Box035,Fusion134]
FEATURE [Part::MultiFuse] Fusion138  label="removeToCreteHoleForPlugHousing051"
  Placement = pos=(70,19,36) rot=(0,1,0;1.5708rad)
  Shapes = -> [Cylinder056,Cylinder057]
FEATURE [Part::MultiFuse] Fusion137  label="removeToCreteHoleForPlugHousing050"
  Placement = pos=(0,0,28.3) rot=(0,0,1;0rad)
  Shapes = -> [Box034,Fusion138]
FEATURE [Part::MultiFuse] Fusion132  label="removeToCreatePlugHousingBottomBit002"
  Shapes = -> [Fusion133,Fusion137]
FEATURE [Part::MultiFuse] Fusion136  label="removeToCreatePlugHousingBottomBit003"
  Shapes = -> [Fusion135,Fusion132]
FEATURE [Part::Cut] Cut058  label="bottomPlugHousingBit002"
  Base = -> Extrude063
  Placement = pos=(-0.09,0,0) rot=(0,0,1;0rad)
  Tool = -> Fusion136
FEATURE [Sketcher::SketchObject] Sketch073  label="bottomSketch003"
  FullyConstrained = true
  sketch-geometry (45):
    g0: LineSegment StartX=6.29999 StartY=8 StartZ=0 EndX=3.29999 EndY=8 EndZ=0
    g1: LineSegment StartX=3.29999 StartY=8 StartZ=0 EndX=3.29999 EndY=-6.03275e-07 EndZ=0
    g2: ArcOfCircle CenterX=8.29999 CenterY=5 CenterZ=0 NormalX=0 NormalY=0 NormalZ=1 AngleXU=0 Radius=2 StartAngle=3.14159 EndAngle=4.71239
    g3: LineSegment StartX=6.29999 StartY=8 StartZ=0 EndX=6.29999 EndY=5 EndZ=0
    g4: ArcOfCircle CenterX=105 CenterY=19 CenterZ=0 NormalX=0 NormalY=0 NormalZ=1 AngleXU=0 Radius=12.7 StartAngle=4.71239 EndAngle=5.94289
    g5-g11: Circle x7 (B-spline internal-alignment scaffolding for g12; pole/knot coordinates omitted)
    g12: BSplineCurve PolesCount=7 KnotsCount=5 Degree=3 IsPeriodic=0
    g13-g17: GeomPoint x5 (B-spline internal-alignment scaffolding for g12; pole/knot coordinates omitted)
    g18: ArcOfCircle CenterX=105 CenterY=19 CenterZ=0 NormalX=0 NormalY=0 NormalZ=1 AngleXU=0 Radius=15.7 StartAngle=5.81226 EndAngle=6.28319
    g19: BSplineCurve PolesCount=5 KnotsCount=3 Degree=3 IsPeriodic=0
    g20: LineSegment StartX=8.29999 StartY=3 StartZ=0 EndX=101.7 EndY=3 EndZ=0
    g21: LineSegment StartX=3.29999 StartY=-6.03275e-07 StartZ=0 EndX=105 EndY=-6.03275e-07 EndZ=0
    g22: LineSegment StartX=120.974 StartY=8.71251 StartZ=0 EndX=122.332 EndY=7.83778 EndZ=0
    g23: LineSegment StartX=105 StartY=-6.03274e-07 StartZ=0 EndX=113 EndY=-6.03274e-07 EndZ=0
    g24: ArcOfCircle CenterX=105 CenterY=19 CenterZ=0 NormalX=0 NormalY=0 NormalZ=1 AngleXU=0 Radius=20.6155 StartAngle=5.11091 EndAngle=5.71103
    g25: ArcOfCircle CenterX=117.7 CenterY=19 CenterZ=0 NormalX=0 NormalY=0 NormalZ=1 AngleXU=0 Radius=3 StartAngle=1.2e-15 EndAngle=2.10468
    g26: Circle CenterX=116.345 CenterY=16.3232 CenterZ=0 NormalX=0 NormalY=0 NormalZ=1 AngleXU=0 Radius=1
    g27: Circle CenterX=117.24 CenterY=15.7584 CenterZ=0 NormalX=0 NormalY=0 NormalZ=1 AngleXU=0 Radius=1
    g28: Circle CenterX=116.972 CenterY=14.7612 CenterZ=0 NormalX=0 NormalY=0 NormalZ=1 AngleXU=0 Radius=1
    g29: BSplineCurve PolesCount=3 KnotsCount=2 Degree=2 IsPeriodic=0
    g30: GeomPoint X=116.345 Y=16.3232 Z=0
    g31: GeomPoint X=116.972 Y=14.7612 Z=0
    g32: Circle CenterX=115.828 CenterY=17.157 CenterZ=0 NormalX=0 NormalY=0 NormalZ=1 AngleXU=0 Radius=1
    g33: Circle CenterX=115.841 CenterY=16.639 CenterZ=0 NormalX=0 NormalY=0 NormalZ=1 AngleXU=0 Radius=1
    g34: Circle CenterX=116.345 CenterY=16.3232 CenterZ=0 NormalX=0 NormalY=0 NormalZ=1 AngleXU=0 Radius=1
    g35: BSplineCurve PolesCount=3 KnotsCount=2 Degree=2 IsPeriodic=0
    g36: GeomPoint X=115.828 Y=17.157 Z=0
    g37: GeomPoint X=116.345 Y=16.3232 Z=0
    g38: LineSegment StartX=115.828 StartY=17.157 StartZ=0 EndX=115.828 EndY=20.8307 EndZ=0
    g39: Circle CenterX=115.828 CenterY=20.8307 CenterZ=0 NormalX=0 NormalY=0 NormalZ=1 AngleXU=0 Radius=1
    g40: Circle CenterX=115.831 CenterY=21.3396 CenterZ=0 NormalX=0 NormalY=0 NormalZ=1 AngleXU=0 Radius=1
    g41: Circle CenterX=116.173 CenterY=21.5825 CenterZ=0 NormalX=0 NormalY=0 NormalZ=1 AngleXU=0 Radius=1
    g42: BSplineCurve PolesCount=3 KnotsCount=2 Degree=2 IsPeriodic=0
    g43: GeomPoint X=115.828 Y=20.8307 Z=0
    g44: GeomPoint X=116.173 Y=21.5825 Z=0
  constraints (70):
    c: Horizontal(g0)
    c: Distance(g0) = 3
    c: Coincident(g1,g0)
    c: Vertical(g1)
    c: Block(g2)
    c: Block(g0)
    c: Coincident(g3,g0)
    c: Coincident(g3,g2)
    c: Vertical(g3)
    c: Block(g1)
    c: Block(g4)
    c: Coincident(g19,g4)
    c: Block(g19)
    c: Equal(g5, g6-g11) x6
    c: InternalAlignment(g5-g11 -> g12) x7
    c: InternalAlignment(g13-g17 -> g12) x5
    c: Block(g12)
    c: Coincident(g18,g12)
    c: Block(g18)
    c: Coincident(g20,g2)
    c: Coincident(g20,g19)
    c: Horizontal(g20)
    c: Distance(g20) = 93.4
    c: Coincident(g21,g1)
    c: Horizontal(g21)
    c: Distance(g21) = 101.7
    c: Horizontal(g23)
    c: Distance(g23) = 8
    c: Coincident(g24,g23)
    c: Block(g23)
    c: Coincident(g22,g24)
    c: Block(g24)
    c: Block(g22)
    c: Distance(g22) = 1.61553
    c: Coincident(g25,g18)
    c: Block(g25)
    c: Weight(g26) = 1
    c: Equal(g26,g27)
    c: Equal(g26,g28)
    c: Coincident(g29,g4)
    c: InternalAlignment(g26,g29)
    c: InternalAlignment(g27,g29)
    c: InternalAlignment(g28,g29)
    c: InternalAlignment(g30,g29)
    c: InternalAlignment(g31,g29)
    c: Block(g29)
    c: Weight(g32) = 1
    c: Equal(g32,g33)
    c: Equal(g32,g34)
    c: Coincident(g35,g29)
    c: InternalAlignment(g32,g35)
    c: InternalAlignment(g33,g35)
    c: InternalAlignment(g34,g35)
    c: InternalAlignment(g36,g35)
    c: InternalAlignment(g37,g35)
    c: Block(g35)
    c: Coincident(g38,g35)
    c: Vertical(g38)
    c: Block(g38)
    c: Coincident(g42,g38)
    c: Weight(g39) = 1
    c: Equal(g39,g40)
    c: Equal(g39,g41)
    c: Coincident(g42,g25)
    c: InternalAlignment(g39,g42)
    c: InternalAlignment(g40,g42)
    c: InternalAlignment(g41,g42)
    c: InternalAlignment(g43,g42)
    c: InternalAlignment(g44,g42)
    c: Block(g42)
FEATURE [Part::Extrusion] Extrude064  label="bottom016"
  Base = -> Sketch073
  Dir = (0,0,1)
  DirMode = 2
  FaceMakerClass = Part::FaceMakerBullseye
  LengthFwd = 71.4
  LengthRev = 0
  Placement = pos=(0,0,0.3) rot=(0,0,1;0rad)
  Solid = true
  Symmetric = false
FEATURE [Part::Revolution] Revolve157  label="removeToCreateScrewAndThreadedInsertHole063"
  Angle = 360
  Axis = (0,1,0)
  Base = (0,0,0)
  FaceMakerClass = Part::FaceMakerBullseye
  Placement = pos=(12.5,0,10) rot=(0,0,1;0rad)
  Solid = false
  Source = -> Face141
  Symmetric = false
FEATURE [Sketcher::SketchObject] Sketch074
  FullyConstrained = true
  Placement = pos=(117,19,0) rot=(0.57735,0.57735,0.57735;2.0944rad)
  sketch-geometry (48):
    g0: LineSegment StartX=-49.19 StartY=69.25 StartZ=0 EndX=-49.19 EndY=66.25 EndZ=0
    g1: LineSegment StartX=-49.19 StartY=63.5 StartZ=0 EndX=-49.19 EndY=60.5 EndZ=0
    g2: LineSegment StartX=-49.19 StartY=57.75 StartZ=0 EndX=-49.19 EndY=54.75 EndZ=0
    g3: LineSegment StartX=-49.19 StartY=52 StartZ=0 EndX=-49.19 EndY=49 EndZ=0
    g4: LineSegment StartX=-49.19 StartY=46.25 StartZ=0 EndX=-49.19 EndY=43.25 EndZ=0
    g5: LineSegment StartX=-49.19 StartY=40.5 StartZ=0 EndX=-49.19 EndY=37.5 EndZ=0
    g6: LineSegment StartX=-49.19 StartY=34.5 StartZ=0 EndX=-49.19 EndY=31.5 EndZ=0
    g7: LineSegment StartX=-49.19 StartY=28.75 StartZ=0 EndX=-49.19 EndY=25.75 EndZ=0
    g8: LineSegment StartX=-49.19 StartY=23 StartZ=0 EndX=-49.19 EndY=20 EndZ=0
    g9: LineSegment StartX=-49.19 StartY=17.25 StartZ=0 EndX=-49.19 EndY=14.25 EndZ=0
    g10: LineSegment StartX=-49.19 StartY=11.5 StartZ=0 EndX=-49.19 EndY=8.5 EndZ=0
    g11: LineSegment StartX=-49.19 StartY=5.75 StartZ=0 EndX=-49.19 EndY=2.75 EndZ=0
    g12: ArcOfCircle CenterX=-1.5 CenterY=67.75 CenterZ=0 NormalX=0 NormalY=0 NormalZ=1 AngleXU=0 Radius=1.5 StartAngle=4.71239 EndAngle=7.85398
    g13: ArcOfCircle CenterX=-1.5 CenterY=62 CenterZ=0 NormalX=0 NormalY=0 NormalZ=1 AngleXU=0 Radius=1.5 StartAngle=4.71239 EndAngle=7.85398
    g14: ArcOfCircle CenterX=-1.5 CenterY=56.25 CenterZ=0 NormalX=0 NormalY=0 NormalZ=1 AngleXU=0 Radius=1.5 StartAngle=4.71239 EndAngle=7.85398
    g15: ArcOfCircle CenterX=-11.49 CenterY=50.5 CenterZ=0 NormalX=0 NormalY=0 NormalZ=1 AngleXU=0 Radius=1.5 StartAngle=4.71239 EndAngle=7.85398
    g16: ArcOfCircle CenterX=-16.28 CenterY=44.75 CenterZ=0 NormalX=0 NormalY=0 NormalZ=1 AngleXU=0 Radius=1.5 StartAngle=4.71239 EndAngle=7.85398
    g17: ArcOfCircle CenterX=-18.2337 CenterY=39 CenterZ=0 NormalX=0 NormalY=0 NormalZ=1 AngleXU=0 Radius=1.5 StartAngle=4.71485 EndAngle=7.85398
    g18: ArcOfCircle CenterX=-16.2837 CenterY=27.25 CenterZ=0 NormalX=0 NormalY=0 NormalZ=1 AngleXU=0 Radius=1.5 StartAngle=4.71485 EndAngle=7.85398
    g19: ArcOfCircle CenterX=-18.2337 CenterY=33 CenterZ=0 NormalX=0 NormalY=0 NormalZ=1 AngleXU=0 Radius=1.5 StartAngle=4.71485 EndAngle=7.85398
    g20: ArcOfCircle CenterX=-11.49 CenterY=21.5 CenterZ=0 NormalX=0 NormalY=0 NormalZ=1 AngleXU=0 Radius=1.5 StartAngle=4.71239 EndAngle=7.85398
    g21: ArcOfCircle CenterX=-1.5 CenterY=4.25 CenterZ=0 NormalX=0 NormalY=0 NormalZ=1 AngleXU=0 Radius=1.5 StartAngle=4.71239 EndAngle=7.85398
    g22: ArcOfCircle CenterX=-1.5 CenterY=10 CenterZ=0 NormalX=0 NormalY=0 NormalZ=1 AngleXU=0 Radius=1.5 StartAngle=4.71239 EndAngle=7.85398
    g23: ArcOfCircle CenterX=-1.5 CenterY=15.75 CenterZ=0 NormalX=0 NormalY=0 NormalZ=1 AngleXU=0 Radius=1.5 StartAngle=4.71239 EndAngle=7.85398
    g24: LineSegment StartX=-49.19 StartY=69.25 StartZ=0 EndX=-1.5 EndY=69.25 EndZ=0
    g25: LineSegment StartX=-49.19 StartY=66.25 StartZ=0 EndX=-1.5 EndY=66.25 EndZ=0
    g26: LineSegment StartX=-49.19 StartY=63.5 StartZ=0 EndX=-1.5 EndY=63.5 EndZ=0
    g27: LineSegment StartX=-49.19 StartY=60.5 StartZ=0 EndX=-1.5 EndY=60.5 EndZ=0
    g28: LineSegment StartX=-49.19 StartY=57.75 StartZ=0 EndX=-1.5 EndY=57.75 EndZ=0
    g29: LineSegment StartX=-49.19 StartY=54.75 StartZ=0 EndX=-1.5 EndY=54.75 EndZ=0
    g30: LineSegment StartX=-49.19 StartY=52 StartZ=0 EndX=-11.49 EndY=52 EndZ=0
    g31: LineSegment StartX=-49.19 StartY=49 StartZ=0 EndX=-11.49 EndY=49 EndZ=0
    g32: LineSegment StartX=-49.19 StartY=46.25 StartZ=0 EndX=-16.28 EndY=46.25 EndZ=0
    g33: LineSegment StartX=-49.19 StartY=43.25 StartZ=0 EndX=-16.28 EndY=43.25 EndZ=0
    g34: LineSegment StartX=-49.19 StartY=40.5 StartZ=0 EndX=-18.2337 EndY=40.5 EndZ=0
    g35: LineSegment StartX=-49.19 StartY=37.5 StartZ=0 EndX=-18.23 EndY=37.5 EndZ=0
    g36: LineSegment StartX=-49.19 StartY=34.5 StartZ=0 EndX=-18.2337 EndY=34.5 EndZ=0
    g37: LineSegment StartX=-49.19 StartY=31.5 StartZ=0 EndX=-18.23 EndY=31.5 EndZ=0
    g38: LineSegment StartX=-49.19 StartY=28.75 StartZ=0 EndX=-16.2837 EndY=28.75 EndZ=0
    g39: LineSegment StartX=-49.19 StartY=25.75 StartZ=0 EndX=-16.28 EndY=25.75 EndZ=0
    g40: LineSegment StartX=-49.19 StartY=23 StartZ=0 EndX=-11.49 EndY=23 EndZ=0
    g41: LineSegment StartX=-49.19 StartY=20 StartZ=0 EndX=-11.49 EndY=20 EndZ=0
    g42: LineSegment StartX=-49.19 StartY=17.25 StartZ=0 EndX=-1.5 EndY=17.25 EndZ=0
    g43: LineSegment StartX=-49.19 StartY=14.25 StartZ=0 EndX=-1.5 EndY=14.25 EndZ=0
    g44: LineSegment StartX=-49.19 StartY=11.5 StartZ=0 EndX=-1.5 EndY=11.5 EndZ=0
    g45: LineSegment StartX=-49.19 StartY=8.5 StartZ=0 EndX=-1.5 EndY=8.5 EndZ=0
    g46: LineSegment StartX=-49.19 StartY=5.75 StartZ=0 EndX=-1.5 EndY=5.75 EndZ=0
    g47: LineSegment StartX=-49.19 StartY=2.75 StartZ=0 EndX=-1.5 EndY=2.75 EndZ=0
  constraints (120):
    c: Vertical(g0)
    c: Distance(g0) = 3
    c: Block(g0)
    c: Vertical(g1)
    c: Distance(g1) = 3
    c: Vertical(g2)
    c: Equal(g0,g2) = 3
    c: Block(g2)
    c: Vertical(g3)
    c: Equal(g1,g3) = 3
    c: Vertical(g4)
    c: Equal(g0,g4) = 3
    c: Block(g4)
    c: Vertical(g5)
    c: Equal(g1,g5) = 3
    c: Vertical(g6)
    c: Equal(g0,g6) = 3
    c: Block(g6)
    c: Vertical(g7)
    c: Equal(g1,g7) = 3
    c: Vertical(g8)
    c: Equal(g0,g8) = 3
    c: Block(g8)
    c: Vertical(g9)
    c: Equal(g1,g9) = 3
    c: Vertical(g10)
    c: Equal(g0,g10) = 3
    c: Block(g10)
    c: Vertical(g11)
    c: Equal(g1,g11) = 3
    c: Block(g12)
    c: Block(g13)
    c: Block(g14)
    c: Block(g15)
    c: Block(g16)
    c: Block(g17)
    c: Block(g18)
    c: Block(g19)
    c: Block(g20)
    c: Block(g21)
    c: Block(g22)
    c: Block(g23)
    c: Block(g11)
    c: Block(g9)
    c: Block(g7)
    c: Block(g5)
    c: Block(g3)
    c: Block(g1)
    c: Coincident(g24,g0)
    c: Coincident(g24,g12)
    c: Horizontal(g24)
    c: Coincident(g25,g0)
    c: Coincident(g25,g12)
    c: Horizontal(g25)
    c: Coincident(g26,g1)
    c: Coincident(g26,g13)
    c: Horizontal(g26)
    c: Coincident(g27,g1)
    c: Coincident(g27,g13)
    c: Horizontal(g27)
    c: Coincident(g28,g2)
    c: Coincident(g28,g14)
    c: Horizontal(g28)
    c: Coincident(g29,g2)
    c: Coincident(g29,g14)
    c: Horizontal(g29)
    c: Coincident(g30,g3)
    c: Coincident(g30,g15)
    c: Horizontal(g30)
    c: Coincident(g31,g3)
    c: Coincident(g31,g15)
    c: Horizontal(g31)
    c: Coincident(g32,g4)
    c: Coincident(g32,g16)
    c: Horizontal(g32)
    c: Coincident(g33,g4)
    c: Coincident(g33,g16)
    c: Horizontal(g33)
    c: Coincident(g34,g5)
    c: Coincident(g34,g17)
    c: Horizontal(g34)
    c: Coincident(g35,g5)
    c: Coincident(g35,g17)
    c: Horizontal(g35)
    c: Coincident(g36,g6)
    c: Coincident(g36,g19)
    c: Horizontal(g36)
    c: Coincident(g37,g6)
    c: Coincident(g37,g19)
    c: Horizontal(g37)
    c: Coincident(g38,g7)
    c: Coincident(g38,g18)
    c: Horizontal(g38)
    c: Coincident(g39,g7)
    c: Coincident(g39,g18)
    c: Horizontal(g39)
    c: Coincident(g40,g8)
    c: Coincident(g40,g20)
    c: Horizontal(g40)
    c: Coincident(g41,g8)
    c: Coincident(g41,g20)
    c: Horizontal(g41)
    c: Coincident(g42,g9)
    c: Coincident(g42,g23)
    c: Horizontal(g42)
    c: Coincident(g43,g9)
    c: Coincident(g43,g23)
    c: Horizontal(g43)
    c: Coincident(g44,g10)
    c: Coincident(g44,g22)
    c: Horizontal(g44)
    c: Coincident(g45,g10)
    c: Coincident(g45,g22)
    c: Horizontal(g45)
    c: Coincident(g46,g11)
    c: Coincident(g46,g21)
    c: Horizontal(g46)
    c: Coincident(g47,g11)
    c: Coincident(g47,g21)
    c: Horizontal(g47)
FEATURE [Part::Extrusion] Extrude065
  Base = -> Sketch074
  Dir = (1,0,0)
  DirMode = 2
  FaceMakerClass = Part::FaceMakerBullseye
  LengthFwd = 23
  LengthRev = 0
  Placement = pos=(-19,0,0) rot=(0,0,1;0rad)
  Solid = true
  Symmetric = false
FEATURE [Part::Fillet] Fillet056  label="removeToCreateVentalationHoles003"
  Base = -> Extrude065
  Edges = <same value as first occurrence — deduplicated (x6 in doc)>
  Placement = pos=(7,0.02,0) rot=(0,0,1;0rad)
FEATURE [Part::Revolution] Revolve158  label="removeToCreateScrewAndThreadedInsertHole065"
  Angle = 360
  Axis = (0,1,0)
  Base = (0,0,0)
  FaceMakerClass = Part::FaceMakerBullseye
  Placement = pos=(12.5,0,62) rot=(0,0,1;0rad)
  Solid = false
  Source = -> Face146
  Symmetric = false
FEATURE [Part::Revolution] Revolve159  label="removeToCreateScrewAndThreadedInsertHole066"
  Angle = 360
  Axis = (0,1,0)
  Base = (0,0,0)
  FaceMakerClass = Part::FaceMakerBullseye
  Placement = pos=(89.5,0,68.5) rot=(0,0,1;0rad)
  Solid = false
  Source = -> Face143
  Symmetric = false
FEATURE [Part::Revolution] Revolve160  label="removeToCreateScrewAndThreadedInsertHole067"
  Angle = 360
  Axis = (0,1,0)
  Base = (0,0,0)
  FaceMakerClass = Part::FaceMakerBullseye
  Placement = pos=(89.5,0,3.5) rot=(0,0,1;0rad)
  Solid = false
  Source = -> Face142
  Symmetric = false
FEATURE [Part::Revolution] Revolve161  label="removeToCreateScrewAndThreadedInsertHole068"
  Angle = 360
  Axis = (0,1,0)
  Base = (0,0,0)
  FaceMakerClass = Part::FaceMakerBullseye
  Placement = pos=(109.5,4.7,3.5) rot=(0,0,1;0rad)
  Solid = false
  Source = -> Face145
  Symmetric = false
FEATURE [Part::Revolution] Revolve162  label="removeToCreateScrewAndThreadedInsertHole069"
  Angle = 360
  Axis = (0,1,0)
  Base = (0,0,0)
  FaceMakerClass = Part::FaceMakerBullseye
  Placement = pos=(109.5,4.7,68.5) rot=(0,0,1;0rad)
  Solid = false
  Source = -> Face144
  Symmetric = false
FEATURE [Part::MultiFuse] Fusion141  label="removeToCreateScrewAndThreadedInsertHole064"
  Shapes = -> [Revolve162,Revolve161,Revolve160,Revolve159,Revolve158,Revolve157]
FEATURE [Part::Cylinder] Cylinder062
  Angle = 360
  AttacherType = Attacher::AttachEngine3D
  Height = 20
  Placement = pos=(0,0,36.15) rot=(0,0,1;0rad)
  Radius = 14
FEATURE [Part::Cylinder] Cylinder063
  Angle = 360
  AttacherType = Attacher::AttachEngine3D
  Height = 10
  Placement = pos=(0,0,36.15) rot=(0,0,1;0rad)
  Radius = 4
FEATURE [Part::MultiFuse] Fusion139  label="removeToCreteHoleForPlugHousing052"
  Placement = pos=(70,19,36) rot=(0,1,0;1.5708rad)
  Shapes = -> [Cylinder062,Cylinder063]
FEATURE [Part::Cut] Cut060  label="bottom017"
  Base = -> Extrude064
  Tool = -> Fusion139
FEATURE [Part::Cut] Cut061  label="bottom019"
  Base = -> Cut060
  Tool = -> Fusion141
FEATURE [Part::MultiFuse] Fusion140  label="bottom018"
  Shapes = -> [Cut061,Cut058]
FEATURE [Part::Cut] Cut059  label="bottom020"
  Base = -> Fusion140
  Tool = -> Fillet056
FEATURE [Part::Box] Box036  label="Cube021"
  AttacherType = Attacher::AttachEngine3D
  Height = 80
  Length = 26
  Placement = pos=(0,-1,-5) rot=(0,0,1;0rad)
  Width = 11
FEATURE [Part::Cut] Cut062  label="removeFromBottom002"
  Base = -> Cut057
  Tool = -> Box036
FEATURE [Part::Cut] Cut063
  Base = -> Cut059
  Tool = -> Cut062
FEATURE [Part::Cut] Cut064  label="pcbStands"
  Base = -> Fusion095
  Tool = -> Fusion127
FEATURE [Sketcher::SketchObject] Sketch075  label="topSketch022"
  FullyConstrained = true
  sketch-geometry (6):
    g0: LineSegment StartX=19 StartY=38 StartZ=0 EndX=117 EndY=38 EndZ=0
    g1: ArcOfCircle CenterX=19 CenterY=19 CenterZ=0 NormalX=0 NormalY=0 NormalZ=1 AngleXU=0 Radius=19 StartAngle=1.5708 EndAngle=3.14159
    g2: LineSegment StartX=117 StartY=38 StartZ=0 EndX=117 EndY=19 EndZ=0
    g3: LineSegment StartX=98 StartY=1.0161e-12 StartZ=0 EndX=5.22862e-06 EndY=1.0161e-12 EndZ=0
    g4: LineSegment StartX=5.22862e-06 StartY=19 StartZ=0 EndX=5.22862e-06 EndY=1.0161e-12 EndZ=0
    g5: ArcOfCircle CenterX=98 CenterY=19 CenterZ=0 NormalX=0 NormalY=0 NormalZ=1 AngleXU=0 Radius=19 StartAngle=4.71239 EndAngle=6.28319
  constraints (16):
    c: Horizontal(g0)
    c: Distance(g0) = 98
    c: Coincident(g1,g0)
    c: Block(g1)
    c: Coincident(g2,g0)
    c: Vertical(g2)
    c: Distance(g2) = 19
    c: Horizontal(g3)
    c: Coincident(g4,g1)
    c: Vertical(g4)
    c: Coincident(g3,g4)
    c: Block(g3)
    c: Coincident(g5,g2)
    c: Coincident(g5,g3)
    c: Block(g0)
    c: Block(g5)
FEATURE [Part::Extrusion] Extrude067  label="sideB003"
  Base = -> Sketch075
  Dir = (0,0,1)
  DirMode = 2
  FaceMakerClass = Part::FaceMakerBullseye
  LengthFwd = 3
  LengthRev = 0
  Placement = pos=(0,0,71.7) rot=(0,0,1;0rad)
  Solid = true
  Symmetric = false
FEATURE [Sketcher::SketchObject] Sketch076  label="topSketch023"
  FullyConstrained = true
  sketch-geometry (6):
    g0: LineSegment StartX=19 StartY=38 StartZ=0 EndX=117 EndY=38 EndZ=0
    g1: ArcOfCircle CenterX=19 CenterY=19 CenterZ=0 NormalX=0 NormalY=0 NormalZ=1 AngleXU=0 Radius=19 StartAngle=1.5708 EndAngle=3.14159
    g2: LineSegment StartX=117 StartY=38 StartZ=0 EndX=117 EndY=19 EndZ=0
    g3: LineSegment StartX=98 StartY=1.0161e-12 StartZ=0 EndX=5.22862e-06 EndY=1.0161e-12 EndZ=0
    g4: LineSegment StartX=5.22862e-06 StartY=19 StartZ=0 EndX=5.22862e-06 EndY=1.0161e-12 EndZ=0
    g5: ArcOfCircle CenterX=98 CenterY=19 CenterZ=0 NormalX=0 NormalY=0 NormalZ=1 AngleXU=0 Radius=19 StartAngle=4.71239 EndAngle=6.28319
  constraints (16):
    c: Horizontal(g0)
    c: Distance(g0) = 98
    c: Coincident(g1,g0)
    c: Block(g1)
    c: Coincident(g2,g0)
    c: Vertical(g2)
    c: Distance(g2) = 19
    c: Horizontal(g3)
    c: Coincident(g4,g1)
    c: Vertical(g4)
    c: Coincident(g3,g4)
    c: Block(g3)
    c: Coincident(g5,g2)
    c: Coincident(g5,g3)
    c: Block(g0)
    c: Block(g5)
FEATURE [Part::Extrusion] Extrude066  label="sideA003"
  Base = -> Sketch076
  Dir = (0,0,1)
  DirMode = 2
  FaceMakerClass = Part::FaceMakerBullseye
  LengthFwd = 3
  LengthRev = 0
  Placement = pos=(0,0,-2.7) rot=(0,0,1;0rad)
  Solid = true
  Symmetric = false
FEATURE [Part::MultiFuse] Fusion142  label="removeFromBottom003"
  Placement = pos=(2,0,0) rot=(0,0,1;0rad)
  Shapes = -> [Extrude066,Extrude067]
FEATURE [Part::Cut] Cut065  label="screwRetainers002"
  Base = -> Fusion096
  Tool = -> Fusion142
FEATURE [Sketcher::SketchObject] Sketch077
  FullyConstrained = true
  Placement = pos=(117,19,0) rot=(0.57735,0.57735,0.57735;2.0944rad)
  sketch-geometry (8):
    g0: LineSegment StartX=-49.19 StartY=63.5 StartZ=0 EndX=-49.19 EndY=60.5 EndZ=0
    g1: LineSegment StartX=-49.19 StartY=11.5 StartZ=0 EndX=-49.19 EndY=8.5 EndZ=0
    g2: ArcOfCircle CenterX=-1.5 CenterY=62 CenterZ=0 NormalX=0 NormalY=0 NormalZ=1 AngleXU=0 Radius=1.5 StartAngle=4.71239 EndAngle=7.85398
    g3: ArcOfCircle CenterX=-1.5 CenterY=10 CenterZ=0 NormalX=0 NormalY=0 NormalZ=1 AngleXU=0 Radius=1.5 StartAngle=4.71239 EndAngle=7.85398
    g4: LineSegment StartX=-49.19 StartY=63.5 StartZ=0 EndX=-1.5 EndY=63.5 EndZ=0
    g5: LineSegment StartX=-49.19 StartY=60.5 StartZ=0 EndX=-1.5 EndY=60.5 EndZ=0
    g6: LineSegment StartX=-49.19 StartY=11.5 StartZ=0 EndX=-1.5 EndY=11.5 EndZ=0
    g7: LineSegment StartX=-49.19 StartY=8.5 StartZ=0 EndX=-1.5 EndY=8.5 EndZ=0
  constraints (19):
    c: Vertical(g0)
    c: Distance(g0) = 3
    c: Vertical(g1)
    c: Block(g1)
    c: Block(g2)
    c: Block(g3)
    c: Block(g0)
    c: Coincident(g4,g0)
    c: Coincident(g4,g2)
    c: Horizontal(g4)
    c: Coincident(g5,g0)
    c: Coincident(g5,g2)
    c: Horizontal(g5)
    c: Coincident(g6,g1)
    c: Coincident(g6,g3)
    c: Horizontal(g6)
    c: Coincident(g7,g1)
    c: Coincident(g7,g3)
    c: Horizontal(g7)
FEATURE [Part::Extrusion] Extrude068
  Base = -> Sketch077
  Dir = (1,0,0)
  DirMode = 2
  FaceMakerClass = Part::FaceMakerBullseye
  LengthFwd = 10
  LengthRev = 0
  Solid = true
  Symmetric = false
FEATURE [Part::Fillet] Fillet057  label="removeFromtMoreFrontCaseScrewRetainers002"
  Base = -> Extrude068
  Edges = 4 edges r=1.49: [Edge6,Edge11,Edge18,Edge23]
  Placement = pos=(-12,0,0) rot=(0,0,1;0rad)
FEATURE [Sketcher::SketchObject] Sketch078
  FullyConstrained = true
  Placement = pos=(117,19,0) rot=(0.57735,0.57735,0.57735;2.0944rad)
  sketch-geometry (8):
    g0: LineSegment StartX=-49.19 StartY=69.25 StartZ=0 EndX=-49.19 EndY=66.25 EndZ=0
    g1: LineSegment StartX=-49.19 StartY=5.75 StartZ=0 EndX=-49.19 EndY=2.75 EndZ=0
    g2: ArcOfCircle CenterX=-1.5 CenterY=67.75 CenterZ=0 NormalX=0 NormalY=0 NormalZ=1 AngleXU=0 Radius=1.5 StartAngle=4.71239 EndAngle=7.85398
    g3: ArcOfCircle CenterX=-1.5 CenterY=4.25 CenterZ=0 NormalX=0 NormalY=0 NormalZ=1 AngleXU=0 Radius=1.5 StartAngle=4.71239 EndAngle=7.85398
    g4: LineSegment StartX=-49.19 StartY=69.25 StartZ=0 EndX=-1.5 EndY=69.25 EndZ=0
    g5: LineSegment StartX=-49.19 StartY=66.25 StartZ=0 EndX=-1.5 EndY=66.25 EndZ=0
    g6: LineSegment StartX=-49.19 StartY=5.75 StartZ=0 EndX=-1.5 EndY=5.75 EndZ=0
    g7: LineSegment StartX=-49.19 StartY=2.75 StartZ=0 EndX=-1.5 EndY=2.75 EndZ=0
  constraints (19):
    c: Vertical(g0)
    c: Distance(g0) = 3
    c: Block(g0)
    c: Vertical(g1)
    c: Block(g2)
    c: Block(g3)
    c: Block(g1)
    c: Coincident(g4,g0)
    c: Coincident(g4,g2)
    c: Horizontal(g4)
    c: Coincident(g5,g0)
    c: Coincident(g5,g2)
    c: Horizontal(g5)
    c: Coincident(g6,g1)
    c: Coincident(g6,g3)
    c: Horizontal(g6)
    c: Coincident(g7,g1)
    c: Coincident(g7,g3)
    c: Horizontal(g7)
FEATURE [Part::Extrusion] Extrude069
  Base = -> Sketch078
  Dir = (1,0,0)
  DirMode = 2
  FaceMakerClass = Part::FaceMakerBullseye
  LengthFwd = 10
  LengthRev = 0
  Solid = true
  Symmetric = false
FEATURE [Part::Fillet] Fillet058  label="removeFromtMoreFrontCaseScrewRetainers003"
  Base = -> Extrude069
  Edges = 4 edges r=1.49: [Edge6,Edge11,Edge18,Edge23]
  Placement = pos=(-4,0,0) rot=(0,0,1;0rad)
FEATURE [Part::Cut] Cut066
  Base = -> Cut065
  Tool = -> Fillet058
FEATURE [Part::Cut] Cut067  label="screwPillars"
  Base = -> Cut066
  Tool = -> Fillet057
FEATURE [Part::MultiFuse] Fusion143  label="bottom021"
  Shapes = -> [Cut031,Cut063]
FEATURE [Part::Cylinder] Cylinder
  Angle = 360
  AttacherType = Attacher::AttachEngine3D
  Height = 10
  Placement = pos=(20.65,12,4.68) rot=(1,0,0;1.5708rad)
  Radius = 2
FEATURE [Part::Cylinder] Cylinder064
  Angle = 360
  AttacherType = Attacher::AttachEngine3D
  Height = 10
  Placement = pos=(20.65,12,67.38) rot=(1,0,0;1.5708rad)
  Radius = 2
FEATURE [Part::Cylinder] Cylinder065
  Angle = 360
  AttacherType = Attacher::AttachEngine3D
  Height = 10
  Placement = pos=(77.15,12,67.38) rot=(1,0,0;1.5708rad)
  Radius = 2
FEATURE [Part::Cylinder] Cylinder066
  Angle = 360
  AttacherType = Attacher::AttachEngine3D
  Height = 10
  Placement = pos=(77.15,12,4.68) rot=(1,0,0;1.5708rad)
  Radius = 2
FEATURE [Part::MultiFuse] Fusion144  label="removeFromThreadedInsertHousing"
  Shapes = -> [Cylinder065,Cylinder064,Cylinder,Cylinder066]
FEATURE [Part::Cut] Cut068  label="pcbStands001"
  Base = -> Cut064
  Tool = -> Fusion144
FEATURE [Part::MultiFuse] Fusion145
  Shapes = -> [Cut068,Fusion143]
FEATURE [Part::MultiFuse] Fusion146
  Shapes = -> [Fusion145]
FEATURE [Part::MultiFuse] Fusion147  label="bottom022"
  Shapes = -> [Cut067,Fusion146]
FEATURE [Part::MultiFuse] Fusion148  label="casePillars005"
  Shapes = -> [Cut047,Fusion092]
FEATURE [Part::MultiFuse] Fusion149  label="bottom023"
  Shapes = -> [Fusion124,Fusion113,Fusion147]
FEATURE [Part::MultiFuse] Fusion150  label="topBits"
  Shapes = -> [Cut025,Fusion148,Cut030,Fillet034]
FEATURE [Part::Feature] Face149 .. Face152  x4 (patterned run collapsed; names and placements below)
  shape: bbox 3.2 x 1.5 x 2e-07 mm, 1 faces, 0 solids (baked)
FEATURE [Part::Feature] Face153
  shape: bbox 3.6 x 3.2 x 2e-07 mm, 1 faces, 0 solids (baked)
FEATURE [Part::Feature] Face154
  shape: bbox 3.6 x 3.2 x 2e-07 mm, 1 faces, 0 solids (baked)
FEATURE [Sketcher::SketchObject] Sketch079  label="topSketch024"
  FullyConstrained = true
  sketch-geometry (6):
    g0: LineSegment StartX=19 StartY=38 StartZ=0 EndX=117 EndY=38 EndZ=0
    g1: ArcOfCircle CenterX=19 CenterY=19 CenterZ=0 NormalX=0 NormalY=0 NormalZ=1 AngleXU=0 Radius=19 StartAngle=1.5708 EndAngle=3.14159
    g2: LineSegment StartX=117 StartY=38 StartZ=0 EndX=117 EndY=19 EndZ=0
    g3: LineSegment StartX=98 StartY=1.0161e-12 StartZ=0 EndX=5.22862e-06 EndY=1.0161e-12 EndZ=0
    g4: LineSegment StartX=5.22862e-06 StartY=19 StartZ=0 EndX=5.22862e-06 EndY=1.0161e-12 EndZ=0
    g5: ArcOfCircle CenterX=98 CenterY=19 CenterZ=0 NormalX=0 NormalY=0 NormalZ=1 AngleXU=0 Radius=19 StartAngle=4.71239 EndAngle=6.28319
  constraints (16):
    c: Horizontal(g0)
    c: Distance(g0) = 98
    c: Coincident(g1,g0)
    c: Block(g1)
    c: Coincident(g2,g0)
    c: Vertical(g2)
    c: Distance(g2) = 19
    c: Horizontal(g3)
    c: Coincident(g4,g1)
    c: Vertical(g4)
    c: Coincident(g3,g4)
    c: Block(g3)
    c: Coincident(g5,g2)
    c: Coincident(g5,g3)
    c: Block(g0)
    c: Block(g5)
FEATURE [Sketcher::SketchObject] Sketch080  label="topSketch025"
  FullyConstrained = true
  sketch-geometry (6):
    g0: LineSegment StartX=19 StartY=38 StartZ=0 EndX=117 EndY=38 EndZ=0
    g1: ArcOfCircle CenterX=19 CenterY=19 CenterZ=0 NormalX=0 NormalY=0 NormalZ=1 AngleXU=0 Radius=19 StartAngle=1.5708 EndAngle=3.14159
    g2: LineSegment StartX=117 StartY=38 StartZ=0 EndX=117 EndY=19 EndZ=0
    g3: LineSegment StartX=98 StartY=1.0161e-12 StartZ=0 EndX=5.22862e-06 EndY=1.0161e-12 EndZ=0
    g4: LineSegment StartX=5.22862e-06 StartY=19 StartZ=0 EndX=5.22862e-06 EndY=1.0161e-12 EndZ=0
    g5: ArcOfCircle CenterX=98 CenterY=19 CenterZ=0 NormalX=0 NormalY=0 NormalZ=1 AngleXU=0 Radius=19 StartAngle=4.71239 EndAngle=6.28319
  constraints (16):
    c: Horizontal(g0)
    c: Distance(g0) = 98
    c: Coincident(g1,g0)
    c: Block(g1)
    c: Coincident(g2,g0)
    c: Vertical(g2)
    c: Distance(g2) = 19
    c: Horizontal(g3)
    c: Coincident(g4,g1)
    c: Vertical(g4)
    c: Coincident(g3,g4)
    c: Block(g3)
    c: Coincident(g5,g2)
    c: Coincident(g5,g3)
    c: Block(g0)
    c: Block(g5)
FEATURE [Part::Extrusion] Extrude070  label="sideA004"
  Base = -> Sketch080
  Dir = (0,0,1)
  DirMode = 2
  FaceMakerClass = Part::FaceMakerBullseye
  LengthFwd = 3
  LengthRev = 0
  Placement = pos=(0,0,-2.7) rot=(0,0,1;0rad)
  Solid = true
  Symmetric = false
FEATURE [Sketcher::SketchObject] Sketch081
  FullyConstrained = true
  Placement = pos=(117,19,0) rot=(0.57735,0.57735,0.57735;2.0944rad)
  sketch-geometry (8):
    g0: LineSegment StartX=-49.19 StartY=63.5 StartZ=0 EndX=-49.19 EndY=60.5 EndZ=0
    g1: LineSegment StartX=-49.19 StartY=11.5 StartZ=0 EndX=-49.19 EndY=8.5 EndZ=0
    g2: ArcOfCircle CenterX=-1.5 CenterY=62 CenterZ=0 NormalX=0 NormalY=0 NormalZ=1 AngleXU=0 Radius=1.5 StartAngle=4.71239 EndAngle=7.85398
    g3: ArcOfCircle CenterX=-1.5 CenterY=10 CenterZ=0 NormalX=0 NormalY=0 NormalZ=1 AngleXU=0 Radius=1.5 StartAngle=4.71239 EndAngle=7.85398
    g4: LineSegment StartX=-49.19 StartY=63.5 StartZ=0 EndX=-1.5 EndY=63.5 EndZ=0
    g5: LineSegment StartX=-49.19 StartY=60.5 StartZ=0 EndX=-1.5 EndY=60.5 EndZ=0
    g6: LineSegment StartX=-49.19 StartY=11.5 StartZ=0 EndX=-1.5 EndY=11.5 EndZ=0
    g7: LineSegment StartX=-49.19 StartY=8.5 StartZ=0 EndX=-1.5 EndY=8.5 EndZ=0
  constraints (19):
    c: Vertical(g0)
    c: Distance(g0) = 3
    c: Vertical(g1)
    c: Block(g1)
    c: Block(g2)
    c: Block(g3)
    c: Block(g0)
    c: Coincident(g4,g0)
    c: Coincident(g4,g2)
    c: Horizontal(g4)
    c: Coincident(g5,g0)
    c: Coincident(g5,g2)
    c: Horizontal(g5)
    c: Coincident(g6,g1)
    c: Coincident(g6,g3)
    c: Horizontal(g6)
    c: Coincident(g7,g1)
    c: Coincident(g7,g3)
    c: Horizontal(g7)
FEATURE [Part::Extrusion] Extrude071  label="sideB004"
  Base = -> Sketch079
  Dir = (0,0,1)
  DirMode = 2
  FaceMakerClass = Part::FaceMakerBullseye
  LengthFwd = 3
  LengthRev = 0
  Placement = pos=(0,0,71.7) rot=(0,0,1;0rad)
  Solid = true
  Symmetric = false
FEATURE [Part::MultiFuse] Fusion152  label="removeFromBottom004"
  Placement = pos=(2,0,0) rot=(0,0,1;0rad)
  Shapes = -> [Extrude070,Extrude071]
FEATURE [Part::Extrusion] Extrude072
  Base = -> Sketch081
  Dir = (1,0,0)
  DirMode = 2
  FaceMakerClass = Part::FaceMakerBullseye
  LengthFwd = 10
  LengthRev = 0
  Solid = true
  Symmetric = false
FEATURE [Part::Fillet] Fillet059  label="removeFromtMoreFrontCaseScrewRetainers004"
  Base = -> Extrude072
  Edges = 4 edges r=1.49: [Edge6,Edge11,Edge18,Edge23]
  Placement = pos=(-12,0,0) rot=(0,0,1;0rad)
FEATURE [Sketcher::SketchObject] Sketch082
  FullyConstrained = true
  Placement = pos=(117,19,0) rot=(0.57735,0.57735,0.57735;2.0944rad)
  sketch-geometry (8):
    g0: LineSegment StartX=-49.19 StartY=69.25 StartZ=0 EndX=-49.19 EndY=66.25 EndZ=0
    g1: LineSegment StartX=-49.19 StartY=5.75 StartZ=0 EndX=-49.19 EndY=2.75 EndZ=0
    g2: ArcOfCircle CenterX=-1.5 CenterY=67.75 CenterZ=0 NormalX=0 NormalY=0 NormalZ=1 AngleXU=0 Radius=1.5 StartAngle=4.71239 EndAngle=7.85398
    g3: ArcOfCircle CenterX=-1.5 CenterY=4.25 CenterZ=0 NormalX=0 NormalY=0 NormalZ=1 AngleXU=0 Radius=1.5 StartAngle=4.71239 EndAngle=7.85398
    g4: LineSegment StartX=-49.19 StartY=69.25 StartZ=0 EndX=-1.5 EndY=69.25 EndZ=0
    g5: LineSegment StartX=-49.19 StartY=66.25 StartZ=0 EndX=-1.5 EndY=66.25 EndZ=0
    g6: LineSegment StartX=-49.19 StartY=5.75 StartZ=0 EndX=-1.5 EndY=5.75 EndZ=0
    g7: LineSegment StartX=-49.19 StartY=2.75 StartZ=0 EndX=-1.5 EndY=2.75 EndZ=0
  constraints (19):
    c: Vertical(g0)
    c: Distance(g0) = 3
    c: Block(g0)
    c: Vertical(g1)
    c: Block(g2)
    c: Block(g3)
    c: Block(g1)
    c: Coincident(g4,g0)
    c: Coincident(g4,g2)
    c: Horizontal(g4)
    c: Coincident(g5,g0)
    c: Coincident(g5,g2)
    c: Horizontal(g5)
    c: Coincident(g6,g1)
    c: Coincident(g6,g3)
    c: Horizontal(g6)
    c: Coincident(g7,g1)
    c: Coincident(g7,g3)
    c: Horizontal(g7)
FEATURE [Part::Extrusion] Extrude073
  Base = -> Sketch082
  Dir = (1,0,0)
  DirMode = 2
  FaceMakerClass = Part::FaceMakerBullseye
  LengthFwd = 10
  LengthRev = 0
  Solid = true
  Symmetric = false
FEATURE [Part::Fillet] Fillet060  label="removeFromtMoreFrontCaseScrewRetainers005"
  Base = -> Extrude073
  Edges = 4 edges r=1.49: [Edge6,Edge11,Edge18,Edge23]
  Placement = pos=(-4,0,0) rot=(0,0,1;0rad)
FEATURE [Part::Revolution] Revolve163  label="backCaseScrewRetainer004"
  Angle = 360
  Axis = (0,1,0)
  Base = (0,0,0)
  FaceMakerClass = Part::FaceMakerBullseye
  Placement = pos=(12.5,3,62) rot=(0,0,1;0rad)
  Solid = false
  Source = -> Face149
  Symmetric = false
FEATURE [Part::Revolution] Revolve164  label="frontCaseScrewRetainer006"
  Angle = 360
  Axis = (0,1,0)
  Base = (0,0,0)
  FaceMakerClass = Part::FaceMakerBullseye
  Placement = pos=(89.5,3,68.5) rot=(0,0,1;0rad)
  Solid = false
  Source = -> Face151
  Symmetric = false
FEATURE [Part::Revolution] Revolve165  label="frontCaseScrewRetainer007"
  Angle = 360
  Axis = (0,1,0)
  Base = (0,0,0)
  FaceMakerClass = Part::FaceMakerBullseye
  Placement = pos=(89.5,3,3.5) rot=(0,0,1;0rad)
  Solid = false
  Source = -> Face152
  Symmetric = false
FEATURE [Part::Revolution] Revolve166  label="backCaseScrewRetainer005"
  Angle = 360
  Axis = (0,1,0)
  Base = (0,0,0)
  FaceMakerClass = Part::FaceMakerBullseye
  Placement = pos=(12.5,3,10) rot=(0,0,1;0rad)
  Solid = false
  Source = -> Face150
  Symmetric = false
FEATURE [Part::Revolution] Revolve167  label="moreFrontCaseScrewRetainer006"
  Angle = 360
  Axis = (0,1,0)
  Base = (0,0,0)
  FaceMakerClass = Part::FaceMakerBullseye
  Placement = pos=(109.5,4.5,68.5) rot=(0,0,1;0rad)
  Solid = false
  Source = -> Face153
  Symmetric = false
FEATURE [Part::Revolution] Revolve168  label="moreFrontCaseScrewRetainer007"
  Angle = 360
  Axis = (0,1,0)
  Base = (0,0,0)
  FaceMakerClass = Part::FaceMakerBullseye
  Placement = pos=(109.5,4.5,3.5) rot=(0,0,1;0rad)
  Solid = false
  Source = -> Face154
  Symmetric = false
FEATURE [Part::MultiFuse] Fusion151  label="screwRetainers003"
  Shapes = -> [Revolve168,Revolve167,Revolve166,Revolve165,Revolve164,Revolve163]
FEATURE [Part::Cut] Cut069  label="screwRetainers004"
  Base = -> Fusion151
  Tool = -> Fusion152
FEATURE [Part::Cut] Cut070
  Base = -> Cut069
  Tool = -> Fillet060
FEATURE [Part::Cut] Cut071  label="screwPillars001"
  Base = -> Cut070
  Tool = -> Fillet059
FEATURE [Part::MultiFuse] Fusion153  label="bottom024"
  Shapes = -> [Fusion149,Cut071]
